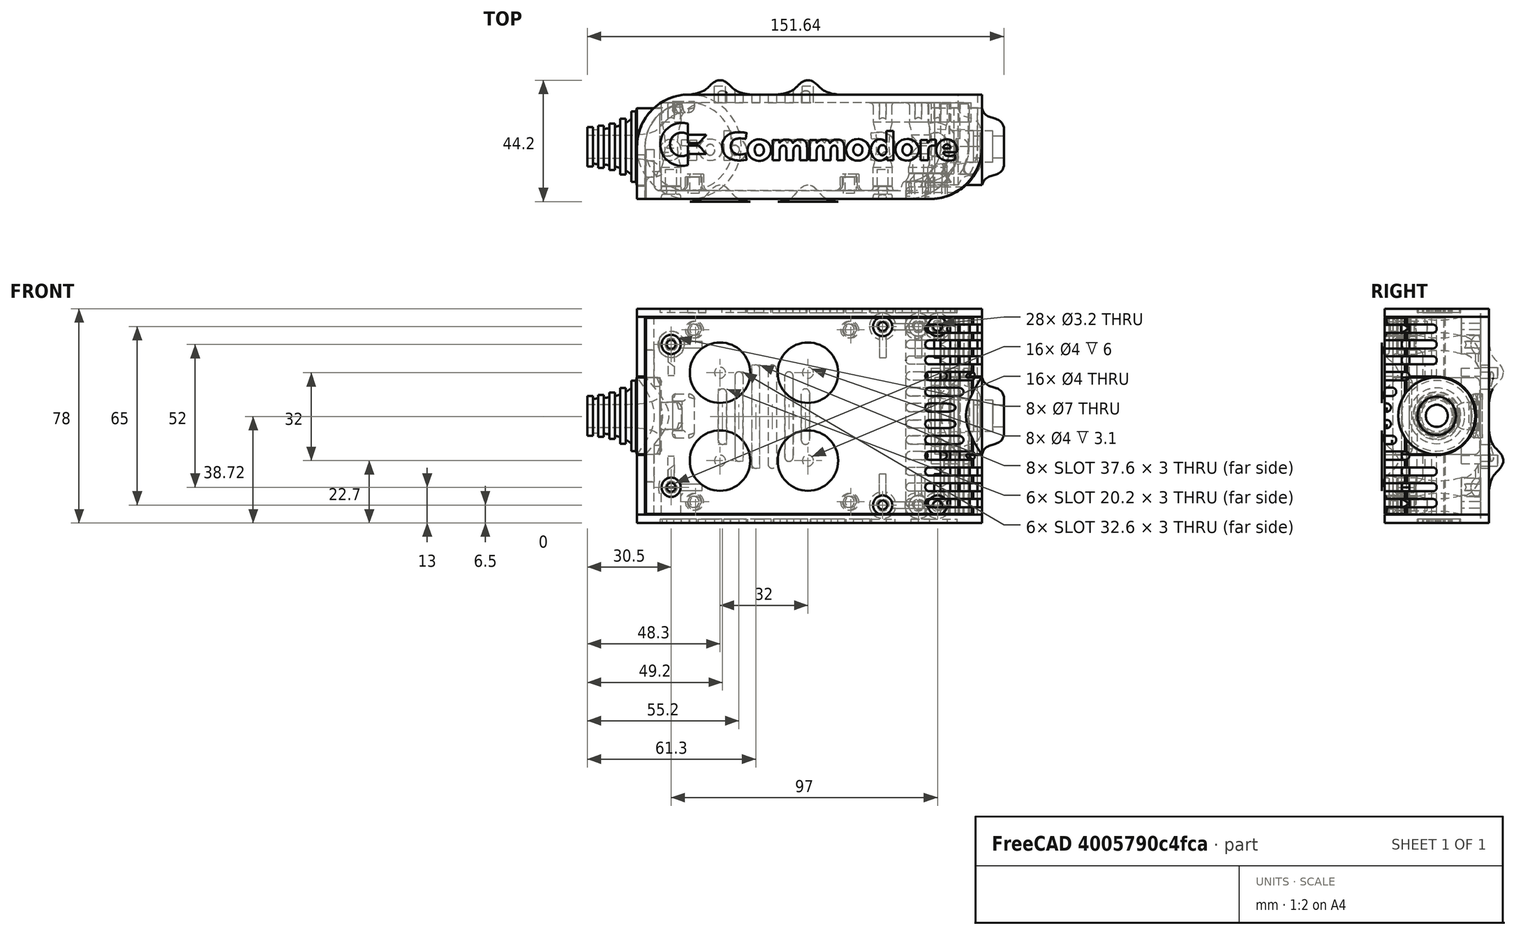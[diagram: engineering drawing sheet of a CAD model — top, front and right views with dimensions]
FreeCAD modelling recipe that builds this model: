
FCSTD DOCUMENT  (FreeCAD 0.19R0.19.2)
Label: enclosure_212FCStd
License: All rights reserved
LicenseURL: http://en.wikipedia.org/wiki/All_rights_reserved
objects: Part::Revolution×152, Part::MultiFuse×146, Part::Feature×146, Sketcher::SketchObject×85, Part::Cut×72, Part::Cylinder×70, Part::Extrusion×69, Part::Fillet×58, Part::Box×37, App::MeasureDistance×4, Part::FeaturePython×2, Image::ImagePlane×1, PartDesign::Body×1, Part::Mirroring×1
note: 839 computed .brp shape members not serialized (recipe doc carries the construction recipe); baked Part::Feature solids carry a one-line shape summary decoded from their .brp

FEATURE [Sketcher::SketchObject] Sketch  label="topSketch"
  FullyConstrained = true
  sketch-geometry (20):
    g0: LineSegment StartX=5.21097e-06 StartY=3 StartZ=0 EndX=5.21097e-06 EndY=19 EndZ=0
    g1: ArcOfCircle CenterX=19 CenterY=19 CenterZ=0 NormalX=0 NormalY=0 NormalZ=1 AngleXU=0 Radius=19 StartAngle=1.5708 EndAngle=3.14159
    g2: ArcOfCircle CenterX=19 CenterY=19 CenterZ=0 NormalX=0 NormalY=0 NormalZ=1 AngleXU=0 Radius=16 StartAngle=1.5708 EndAngle=3.14159
    g3: LineSegment StartX=114 StartY=35 StartZ=0 EndX=19 EndY=35 EndZ=0
    g4: LineSegment StartX=5.21097e-06 StartY=3 StartZ=0 EndX=5.21097e-06 EndY=0 EndZ=0
    g5: LineSegment StartX=3 StartY=0 StartZ=0 EndX=5.21097e-06 EndY=0 EndZ=0
    g6: LineSegment StartX=3 StartY=19 StartZ=0 EndX=3 EndY=0 EndZ=0
    g7: LineSegment StartX=19 StartY=38 StartZ=0 EndX=124 EndY=38 EndZ=0
    g8: Circle CenterX=119 CenterY=35 CenterZ=0 NormalX=0 NormalY=0 NormalZ=1 AngleXU=0 Radius=1
    g9: Circle CenterX=121 CenterY=35 CenterZ=0 NormalX=0 NormalY=0 NormalZ=1 AngleXU=0 Radius=1
    g10: Circle CenterX=121 CenterY=33 CenterZ=0 NormalX=0 NormalY=0 NormalZ=1 AngleXU=0 Radius=1
    g11: BSplineCurve PolesCount=3 KnotsCount=2 Degree=2 IsPeriodic=0
    g12: GeomPoint X=119 Y=35 Z=0
    g13: GeomPoint X=121 Y=33 Z=0
    g14: LineSegment StartX=119 StartY=35 StartZ=0 EndX=114 EndY=35 EndZ=0
    g15: ArcOfCircle CenterX=105 CenterY=19 CenterZ=0 NormalX=0 NormalY=0 NormalZ=1 AngleXU=0 Radius=19 StartAngle=5.7297 EndAngle=6.28319
    g16: ArcOfCircle CenterX=105 CenterY=19 CenterZ=0 NormalX=0 NormalY=0 NormalZ=1 AngleXU=0 Radius=16 StartAngle=5.60905 EndAngle=6.28319
    g17: LineSegment StartX=121 StartY=33 StartZ=0 EndX=121 EndY=19 EndZ=0
    g18: LineSegment StartX=124 StartY=38 StartZ=0 EndX=124 EndY=19 EndZ=0
    g19: LineSegment StartX=117.5 StartY=9.01251 StartZ=0 EndX=121.163 EndY=9.0125 EndZ=0
  constraints (46):
    c: Vertical(g0)
    c: Block(g0)
    c: Coincident(g1,g0)
    c: Block(g1)
    c: Coincident(g2,g1)
    c: Block(g2)
    c: Coincident(g3,g2)
    c: Horizontal(g3)
    c: Tangent(g3,g2)
    c: Coincident(g4,g0)
    c: Distance(g4) = 3
    c: Vertical(g4)
    c: Coincident(g5,g4)
    c: Horizontal(g5)
    c: Coincident(g6,g2)
    c: Coincident(g6,g5)
    c: Vertical(g6)
    c: Horizontal(g7)
    c: Distance(g7) = 105
    c: Coincident(g7,g1)
    c: Block(g3)
    c: Weight(g8) = 1
    c: Equal(g8,g9)
    c: Equal(g8,g10)
    c: InternalAlignment(g8,g11)
    c: InternalAlignment(g9,g11)
    c: InternalAlignment(g10,g11)
    c: InternalAlignment(g12,g11)
    c: InternalAlignment(g13,g11)
    c: Block(g11)
    c: Coincident(g14,g11)
    c: Coincident(g14,g3)
    c: Horizontal(g14)
    c: Block(g15)
    c: Coincident(g16,g15)
    c: Block(g16)
    c: Coincident(g17,g11)
    c: Coincident(g17,g16)
    c: Vertical(g17)
    c: Distance(g17) = 14
    c: Coincident(g18,g7)
    c: Coincident(g18,g15)
    c: Vertical(g18)
    c: Distance(g18) = 19
    c: Coincident(g19,g16)
    c: Coincident(g19,g15)
FEATURE [Sketcher::SketchObject] Sketch001  label="bottomSketch"
  FullyConstrained = true
  sketch-geometry (32):
    g0: LineSegment StartX=3.3 StartY=-6.03275e-07 StartZ=0 EndX=98 EndY=-6.03275e-07 EndZ=0
    g1: ArcOfCircle CenterX=98 CenterY=19 CenterZ=0 NormalX=0 NormalY=0 NormalZ=1 AngleXU=0 Radius=19 StartAngle=4.71239 EndAngle=5.71103
    g2: LineSegment StartX=6.3 StartY=8 StartZ=0 EndX=3.3 EndY=8 EndZ=0
    g3: LineSegment StartX=3.3 StartY=8 StartZ=0 EndX=3.3 EndY=-6.03275e-07 EndZ=0
    g4: ArcOfCircle CenterX=8.3 CenterY=5 CenterZ=0 NormalX=0 NormalY=0 NormalZ=1 AngleXU=0 Radius=2 StartAngle=3.14159 EndAngle=4.71239
    g5: LineSegment StartX=6.3 StartY=8 StartZ=0 EndX=6.3 EndY=5 EndZ=0
    g6: ArcOfCircle CenterX=98 CenterY=19 CenterZ=0 NormalX=0 NormalY=0 NormalZ=1 AngleXU=0 Radius=12.7 StartAngle=4.71239 EndAngle=6.28319
    g7: LineSegment StartX=94.7 StartY=3 StartZ=0 EndX=8.3 EndY=3 EndZ=0
    g8-g12: Circle x5 (B-spline internal-alignment scaffolding for g13; pole/knot coordinates omitted)
    g13: BSplineCurve PolesCount=5 KnotsCount=3 Degree=3 IsPeriodic=0
    g14: GeomPoint X=98 Y=6.3 Z=0
    g15: GeomPoint X=96.3938 Y=4.71946 Z=0
    g16: GeomPoint X=94.7 Y=3 Z=0
    g17-g23: Circle x7 (B-spline internal-alignment scaffolding for g24; pole/knot coordinates omitted)
    g24: BSplineCurve PolesCount=7 KnotsCount=5 Degree=3 IsPeriodic=0
    g25-g29: GeomPoint x5 (B-spline internal-alignment scaffolding for g24; pole/knot coordinates omitted)
    g30: ArcOfCircle CenterX=98 CenterY=19 CenterZ=0 NormalX=0 NormalY=0 NormalZ=1 AngleXU=0 Radius=15.7 StartAngle=5.81226 EndAngle=6.28319
    g31: LineSegment StartX=110.7 StartY=19 StartZ=0 EndX=113.7 EndY=19 EndZ=0
  constraints (41):
    c: Horizontal(g0)
    c: Coincident(g1,g0)
    c: Block(g1)
    c: Horizontal(g2)
    c: Distance(g2) = 3
    c: Coincident(g3,g2)
    c: Vertical(g3)
    c: Coincident(g3,g0)
    c: Block(g4)
    c: Block(g2)
    c: Coincident(g5,g2)
    c: Coincident(g5,g4)
    c: Vertical(g5)
    c: Coincident(g6,g1)
    c: Block(g6)
    c: Coincident(g7,g4)
    c: Horizontal(g7)
    c: Block(g0)
    c: Block(g7)
    c: Block(g3)
    c: Coincident(g13,g6)
    c: Weight(g8) = 1
    c: Equal(g8, g9-g12) x4
    c: Coincident(g13,g7)
    c: InternalAlignment(g8-g12 -> g13) x5
    c: InternalAlignment(g14,g13)
    c: InternalAlignment(g15,g13)
    c: InternalAlignment(g16,g13)
    c: Block(g13)
    c: Weight(g17) = 1
    c: Equal(g17, g18-g23) x6
    c: Coincident(g24,g1)
    c: InternalAlignment(g17-g23 -> g24) x7
    c: InternalAlignment(g25-g29 -> g24) x5
    c: Block(g24)
    c: Coincident(g30,g24)
    c: Coincident(g31,g6)
    c: Coincident(g31,g30)
    c: Horizontal(g31)
    c: Block(g31)
    c: Block(g30)
FEATURE [Part::Extrusion] Extrude  label="top"
  Base = -> Sketch
  Dir = (0,0,1)
  DirMode = 2
  FaceMakerClass = Part::FaceMakerBullseye
  LengthFwd = 72
  LengthRev = 0
  Solid = true
  Symmetric = false
FEATURE [Part::Extrusion] Extrude001  label="bottom"
  Base = -> Sketch001
  Dir = (0,0,1)
  DirMode = 2
  FaceMakerClass = Part::FaceMakerBullseye
  LengthFwd = 71.4
  LengthRev = 0
  Placement = pos=(0,0,0.3) rot=(0,0,1;0rad)
  Solid = true
  Symmetric = false
FEATURE [Sketcher::SketchObject] Sketch002  label="topSketch001"
  FullyConstrained = true
  sketch-geometry (8):
    g0: ArcOfCircle CenterX=19 CenterY=19.0975 CenterZ=0 NormalX=0 NormalY=0 NormalZ=1 AngleXU=0 Radius=18.9025 StartAngle=1.5708 EndAngle=3.14674
    g1: LineSegment StartX=0.0977805 StartY=19.0003 StartZ=0 EndX=0.0977805 EndY=0.000251602 EndZ=0
    g2: LineSegment StartX=19 StartY=38 StartZ=0 EndX=124 EndY=38 EndZ=0
    g3: LineSegment StartX=0.0977805 StartY=0.000251602 StartZ=0 EndX=105.098 EndY=0.000251602 EndZ=0
    g4: LineSegment StartX=124 StartY=38 StartZ=0 EndX=125.616 EndY=38 EndZ=0
    g5: LineSegment StartX=105.098 StartY=0.000251602 StartZ=0 EndX=106.713 EndY=0.000251602 EndZ=0
    g6: ArcOfCircle CenterX=106.616 CenterY=19 CenterZ=0 NormalX=0 NormalY=0 NormalZ=1 AngleXU=0 Radius=19 StartAngle=4.71754 EndAngle=6.28319
    g7: LineSegment StartX=125.616 StartY=38 StartZ=0 EndX=125.616 EndY=19 EndZ=0
  constraints (21):
    c: Block(g0)
    c: Coincident(g1,g0)
    c: Vertical(g1)
    c: Horizontal(g2)
    c: Distance(g2) = 105
    c: Coincident(g2,g0)
    c: Distance(g1) = 19
    c: Coincident(g3,g1)
    c: Horizontal(g3)
    c: Distance(g3) = 105
    c: Coincident(g4,g2)
    c: Horizontal(g4)
    c: Distance(g4) = 1.61553
    c: Horizontal(g5)
    c: Equal(g4,g5) = 1.61553
    c: Coincident(g5,g3)
    c: Block(g6)
    c: Coincident(g6,g5)
    c: Coincident(g7,g4)
    c: Coincident(g7,g6)
    c: Vertical(g7)
FEATURE [Part::Extrusion] Extrude002  label="sideA"
  Base = -> Sketch002
  Dir = (0,0,1)
  DirMode = 2
  FaceMakerClass = Part::FaceMakerBullseye
  LengthFwd = 3
  LengthRev = 0
  Placement = pos=(0,0,-3) rot=(0,0,1;0rad)
  Solid = true
  Symmetric = false
FEATURE [Sketcher::SketchObject] Sketch003  label="topSketch002"
  FullyConstrained = true
  sketch-geometry (6):
    g0: LineSegment StartX=19 StartY=38 StartZ=0 EndX=117 EndY=38 EndZ=0
    g1: ArcOfCircle CenterX=19 CenterY=19 CenterZ=0 NormalX=0 NormalY=0 NormalZ=1 AngleXU=0 Radius=19 StartAngle=1.5708 EndAngle=3.14159
    g2: LineSegment StartX=117 StartY=38 StartZ=0 EndX=117 EndY=19 EndZ=0
    g3: LineSegment StartX=98 StartY=1.0161e-12 StartZ=0 EndX=5.22862e-06 EndY=1.0161e-12 EndZ=0
    g4: LineSegment StartX=5.22862e-06 StartY=19 StartZ=0 EndX=5.22862e-06 EndY=1.0161e-12 EndZ=0
    g5: ArcOfCircle CenterX=98 CenterY=19 CenterZ=0 NormalX=0 NormalY=0 NormalZ=1 AngleXU=0 Radius=19 StartAngle=4.71239 EndAngle=6.28319
  constraints (16):
    c: Horizontal(g0)
    c: Distance(g0) = 98
    c: Coincident(g1,g0)
    c: Block(g1)
    c: Coincident(g2,g0)
    c: Vertical(g2)
    c: Distance(g2) = 19
    c: Horizontal(g3)
    c: Coincident(g4,g1)
    c: Vertical(g4)
    c: Coincident(g3,g4)
    c: Block(g3)
    c: Coincident(g5,g2)
    c: Coincident(g5,g3)
    c: Block(g0)
    c: Block(g5)
FEATURE [Sketcher::SketchObject] Sketch004
  FullyConstrained = true
  MapMode = 3
  Placement = pos=(0,0,0) rot=(1,0,0;1.5708rad)
  Support = -> [Extrude]
  sketch-geometry (8):
    g0: Circle CenterX=80.351 CenterY=-67.6202 CenterZ=0 NormalX=0 NormalY=0 NormalZ=1 AngleXU=0 Radius=2
    g1: Circle CenterX=80.351 CenterY=-67.6202 CenterZ=0 NormalX=0 NormalY=0 NormalZ=1 AngleXU=0 Radius=3
    g2: Circle CenterX=80.351 CenterY=-4.92017 CenterZ=0 NormalX=0 NormalY=0 NormalZ=1 AngleXU=0 Radius=2
    g3: Circle CenterX=80.351 CenterY=-4.92017 CenterZ=0 NormalX=0 NormalY=0 NormalZ=1 AngleXU=0 Radius=3
    g4: Circle CenterX=23.851 CenterY=-4.92017 CenterZ=0 NormalX=0 NormalY=0 NormalZ=1 AngleXU=0 Radius=2
    g5: Circle CenterX=23.851 CenterY=-4.92017 CenterZ=0 NormalX=0 NormalY=0 NormalZ=1 AngleXU=0 Radius=3
    g6: Circle CenterX=23.851 CenterY=-67.6202 CenterZ=0 NormalX=0 NormalY=0 NormalZ=1 AngleXU=0 Radius=2
    g7: Circle CenterX=23.851 CenterY=-67.6202 CenterZ=0 NormalX=0 NormalY=0 NormalZ=1 AngleXU=0 Radius=3
  constraints (8):
    c: Block(g3)
    c: Block(g2)
    c: Block(g1)
    c: Block(g0)
    c: Block(g6)
    c: Block(g7)
    c: Block(g4)
    c: Block(g5)
FEATURE [Part::Extrusion] Extrude004
  Base = -> Sketch004
  Dir = (0,-1,2e-16)
  DirMode = 2
  FaceMakerClass = Part::FaceMakerBullseye
  LengthFwd = 6
  LengthRev = 0
  Placement = pos=(0,9,0) rot=(0,0,1;0rad)
  Solid = true
  Symmetric = false
FEATURE [Sketcher::SketchObject] Sketch005
  FullyConstrained = true
  MapMode = 3
  Placement = pos=(0,0,0) rot=(1,0,0;1.5708rad)
  Support = -> [Extrude]
  sketch-geometry (8):
    g0: Circle CenterX=80.351 CenterY=-67.6202 CenterZ=0 NormalX=0 NormalY=0 NormalZ=1 AngleXU=0 Radius=3
    g1: Circle CenterX=80.351 CenterY=-4.92017 CenterZ=0 NormalX=0 NormalY=0 NormalZ=1 AngleXU=0 Radius=3
    g2: Circle CenterX=23.851 CenterY=-4.92017 CenterZ=0 NormalX=0 NormalY=0 NormalZ=1 AngleXU=0 Radius=3
    g3: Circle CenterX=23.851 CenterY=-67.6202 CenterZ=0 NormalX=0 NormalY=0 NormalZ=1 AngleXU=0 Radius=3
    g4: Circle CenterX=23.851 CenterY=-67.6202 CenterZ=0 NormalX=0 NormalY=0 NormalZ=1 AngleXU=0 Radius=5
    g5: Circle CenterX=80.351 CenterY=-67.6202 CenterZ=0 NormalX=0 NormalY=0 NormalZ=1 AngleXU=0 Radius=5
    g6: Circle CenterX=23.851 CenterY=-4.92017 CenterZ=0 NormalX=0 NormalY=0 NormalZ=1 AngleXU=0 Radius=5
    g7: Circle CenterX=80.351 CenterY=-4.92017 CenterZ=0 NormalX=0 NormalY=0 NormalZ=1 AngleXU=0 Radius=5
  constraints (8):
    c: Block(g1)
    c: Block(g0)
    c: Block(g3)
    c: Block(g2)
    c: Block(g5)
    c: Block(g4)
    c: Block(g6)
    c: Block(g7)
FEATURE [Part::Extrusion] Extrude005
  Base = -> Sketch005
  Dir = (0,-1,2e-16)
  DirMode = 2
  FaceMakerClass = Part::FaceMakerBullseye
  LengthFwd = 2
  LengthRev = 0
  Solid = true
  Symmetric = false
FEATURE [Sketcher::SketchObject] Sketch006
  FullyConstrained = true
  MapMode = 3
  Placement = pos=(0,0,0) rot=(1,0,0;1.5708rad)
  sketch-geometry (8):
    g0: Circle CenterX=80.351 CenterY=-67.6202 CenterZ=0 NormalX=0 NormalY=0 NormalZ=1 AngleXU=0 Radius=3
    g1: Circle CenterX=80.351 CenterY=-4.92017 CenterZ=0 NormalX=0 NormalY=0 NormalZ=1 AngleXU=0 Radius=3
    g2: Circle CenterX=23.851 CenterY=-4.92017 CenterZ=0 NormalX=0 NormalY=0 NormalZ=1 AngleXU=0 Radius=3
    g3: Circle CenterX=23.851 CenterY=-67.6202 CenterZ=0 NormalX=0 NormalY=0 NormalZ=1 AngleXU=0 Radius=3
    g4: Circle CenterX=23.851 CenterY=-67.6202 CenterZ=0 NormalX=0 NormalY=0 NormalZ=1 AngleXU=0 Radius=5
    g5: Circle CenterX=80.351 CenterY=-67.6202 CenterZ=0 NormalX=0 NormalY=0 NormalZ=1 AngleXU=0 Radius=5
    g6: Circle CenterX=23.851 CenterY=-4.92017 CenterZ=0 NormalX=0 NormalY=0 NormalZ=1 AngleXU=0 Radius=5
    g7: Circle CenterX=80.351 CenterY=-4.92017 CenterZ=0 NormalX=0 NormalY=0 NormalZ=1 AngleXU=0 Radius=5
  constraints (8):
    c: Block(g1)
    c: Block(g0)
    c: Block(g3)
    c: Block(g2)
    c: Block(g5)
    c: Block(g4)
    c: Block(g6)
    c: Block(g7)
FEATURE [Part::Extrusion] Extrude007
  Base = -> Sketch006
  Dir = (0,-1,2e-16)
  DirMode = 2
  FaceMakerClass = Part::FaceMakerBullseye
  LengthFwd = 2
  LengthRev = 0
  Solid = true
  Symmetric = false
FEATURE [Part::Fillet] Fillet
  Base = -> Extrude007
  Edges = 4 edges r=1.99: [Edge6,Edge12,Edge18,Edge24]
FEATURE [Part::Cut] Cut
  Base = -> Extrude005
  Placement = pos=(0,5,0) rot=(0,0,1;0rad)
  Tool = -> Fillet
FEATURE [Part::MultiFuse] Fusion  label="pCBScrews"
  Placement = pos=(-2.5,0,72.3) rot=(0,0,1;0rad)
  Shapes = -> [Extrude004,Cut]
FEATURE [App::MeasureDistance] Distance  label="Distance: 0.69 mm"
  Distance = 0.685967
  P1 = (24.0138,2.9647,0.3)
  P2 = (23.8901,3,-0.373787)
FEATURE [App::MeasureDistance] Distance001  label="Distance: 0.53 mm"
  Distance = 0.533607
  P1 = (80.2939,3,72.2334)
  P2 = (80.281,2.99661,71.7)
FEATURE [Part::Fillet] Fillet001
  Base = -> Extrude001
  Edges = 1 edges r=2.4: [Edge17]
FEATURE [Part::Fillet] Fillet002  label="bottom001"
  Base = -> Fillet001
  Edges = 1 edges r=2.4: [Edge36]
FEATURE [Part::Fillet] Fillet003  label="top001"
  Base = -> Extrude
  Edges = 1 edges r=2: [Edge1]
FEATURE [Sketcher::SketchObject] Sketch007
  FullyConstrained = true
  sketch-geometry (16):
    g0: LineSegment StartX=4 StartY=0 StartZ=0 EndX=4 EndY=2.4 EndZ=0
    g1: LineSegment StartX=4 StartY=2.4 StartZ=0 EndX=7 EndY=2.4 EndZ=0
    g2: LineSegment StartX=4 StartY=0 StartZ=0 EndX=5.7 EndY=0 EndZ=0
    g3: LineSegment StartX=5.7 StartY=0 StartZ=0 EndX=5.7 EndY=-5.6 EndZ=0
    g4-g8: Circle x5 (B-spline internal-alignment scaffolding for g9; pole/knot coordinates omitted)
    g9: BSplineCurve PolesCount=5 KnotsCount=3 Degree=3 IsPeriodic=0
    g10: GeomPoint X=7 Y=2.4 Z=0
    g11: GeomPoint X=10.4582 Y=-1.55472 Z=0
    g12: GeomPoint X=14 Y=-5.6 Z=0
    g13: LineSegment StartX=14 StartY=-5.6 StartZ=0 EndX=14 EndY=-14.1 EndZ=0
    g14: LineSegment StartX=14 StartY=-14.1 StartZ=0 EndX=6.5 EndY=-14.1 EndZ=0
    g15: LineSegment StartX=5.7 StartY=-5.6 StartZ=0 EndX=6.5 EndY=-14.1 EndZ=0
  constraints (28):
    c: Distance(g0) = 2.4
    c: Vertical(g0)
    c: Block(g0)
    c: Coincident(g1,g0)
    c: Horizontal(g1)
    c: Distance(g1) = 3
    c: Coincident(g2,g0)
    c: Horizontal(g2)
    c: Distance(g2) = 1.7
    c: Coincident(g3,g2)
    c: Vertical(g3)
    c: Distance(g3) = 5.6
    c: Coincident(g9,g1)
    c: Weight(g4) = 1
    c: Equal(g4, g5-g8) x4
    c: InternalAlignment(g4-g8 -> g9) x5
    c: InternalAlignment(g10,g9)
    c: InternalAlignment(g11,g9)
    c: InternalAlignment(g12,g9)
    c: Block(g9)
    c: Coincident(g13,g9)
    c: Vertical(g13)
    c: Distance(g13) = 8.5
    c: Coincident(g14,g13)
    c: Horizontal(g14)
    c: Distance(g14) = 7.5
    c: Coincident(g15,g3)
    c: Coincident(g15,g14)
FEATURE [Part::Feature] Face
  shape: bbox 10 x 16.5 x 2e-07 mm, 1 faces, 0 solids (baked)
FEATURE [Part::Revolution] Revolve  label="plugHousing"
  Angle = 360
  Axis = (0,1,0)
  Base = (0,0,0)
  FaceMakerClass = Part::FaceMakerBullseye
  Placement = pos=(0,0,36.15) rot=(0,0,1;0rad)
  Solid = false
  Source = -> Face
  Symmetric = false
FEATURE [Part::Feature] Face001
  shape: bbox 10 x 16.5 x 2e-07 mm, 1 faces, 0 solids (baked)
FEATURE [Part::Revolution] Revolve001  label="plugHousing001"
  Angle = 360
  Axis = (0,1,0)
  Base = (0,0,0)
  FaceMakerClass = Part::FaceMakerBullseye
  Placement = pos=(0,0,36.15) rot=(0,0,1;0rad)
  Solid = false
  Source = -> Face001
  Symmetric = false
FEATURE [Part::MultiFuse] Fusion001  label="plugHousing002"
  Placement = pos=(0,0,0) rot=(0,0,1;1.5708rad)
  Shapes = -> [Revolve001,Revolve]
FEATURE [Part::Feature] Face002
  shape: bbox 10 x 16.5 x 2e-07 mm, 1 faces, 0 solids (baked)
FEATURE [Part::Revolution] Revolve003  label="plugHousing005"
  Angle = 360
  Axis = (0,1,0)
  Base = (0,0,0)
  FaceMakerClass = Part::FaceMakerBullseye
  Placement = pos=(0,0,36.15) rot=(0,0,1;0rad)
  Solid = false
  Source = -> Face002
  Symmetric = false
FEATURE [Part::Feature] Face003
  shape: bbox 10 x 16.5 x 2e-07 mm, 1 faces, 0 solids (baked)
FEATURE [Part::Revolution] Revolve002  label="plugHousing003"
  Angle = 360
  Axis = (0,1,0)
  Base = (0,0,0)
  FaceMakerClass = Part::FaceMakerBullseye
  Placement = pos=(0,0,36.15) rot=(0,0,1;0rad)
  Solid = false
  Source = -> Face003
  Symmetric = false
FEATURE [Part::MultiFuse] Fusion002  label="plugHousing004"
  Placement = pos=(0,0,0) rot=(0,0,1;1.5708rad)
  Shapes = -> [Revolve002,Revolve003]
FEATURE [Part::MultiFuse] Fusion003  label="plugHousing006"
  Placement = pos=(0,19,0) rot=(0,0,1;3.14159rad)
  Shapes = -> [Fusion002,Fusion001]
FEATURE [Part::Feature] Face004
  shape: bbox 10 x 16.5 x 2e-07 mm, 1 faces, 0 solids (baked)
FEATURE [Part::Revolution] Revolve006  label="plugHousing010"
  Angle = 360
  Axis = (0,1,0)
  Base = (0,0,0)
  FaceMakerClass = Part::FaceMakerBullseye
  Placement = pos=(0,0,36.15) rot=(0,0,1;0rad)
  Solid = false
  Source = -> Face004
  Symmetric = false
FEATURE [Part::Feature] Face005
  shape: bbox 10 x 16.5 x 2e-07 mm, 1 faces, 0 solids (baked)
FEATURE [Part::Revolution] Revolve007  label="plugHousing011"
  Angle = 360
  Axis = (0,1,0)
  Base = (0,0,0)
  FaceMakerClass = Part::FaceMakerBullseye
  Placement = pos=(0,0,36.15) rot=(0,0,1;0rad)
  Solid = false
  Source = -> Face005
  Symmetric = false
FEATURE [Part::Feature] Face006
  shape: bbox 10 x 16.5 x 2e-07 mm, 1 faces, 0 solids (baked)
FEATURE [Part::Revolution] Revolve004  label="plugHousing007"
  Angle = 360
  Axis = (0,1,0)
  Base = (0,0,0)
  FaceMakerClass = Part::FaceMakerBullseye
  Placement = pos=(0,0,36.15) rot=(0,0,1;0rad)
  Solid = false
  Source = -> Face006
  Symmetric = false
FEATURE [Part::MultiFuse] Fusion004  label="plugHousing009"
  Placement = pos=(0,0,0) rot=(0,0,1;1.5708rad)
  Shapes = -> [Revolve004,Revolve007]
FEATURE [Part::Feature] Face007
  shape: bbox 10 x 16.5 x 2e-07 mm, 1 faces, 0 solids (baked)
FEATURE [Part::Revolution] Revolve005  label="plugHousing008"
  Angle = 360
  Axis = (0,1,0)
  Base = (0,0,0)
  FaceMakerClass = Part::FaceMakerBullseye
  Placement = pos=(0,0,36.15) rot=(0,0,1;0rad)
  Solid = false
  Source = -> Face007
  Symmetric = false
FEATURE [Part::MultiFuse] Fusion005  label="plugHousing012"
  Placement = pos=(0,0,0) rot=(0,0,1;1.5708rad)
  Shapes = -> [Revolve006,Revolve005]
FEATURE [Part::MultiFuse] Fusion006  label="plugHousing013"
  Placement = pos=(0,19,0) rot=(0,0,1;3.14159rad)
  Shapes = -> [Fusion005,Fusion004]
FEATURE [Part::MultiFuse] Fusion007  label="plugHousing014"
  Placement = pos=(122.621,0,-0.15) rot=(0,0,1;0rad)
  Shapes = -> [Fusion003,Fusion006]
FEATURE [Part::Cylinder] Cylinder002
  Angle = 360
  AttacherType = Attacher::AttachEngine3D
  Height = 20
  Placement = pos=(0,0,36.15) rot=(0,0,1;0rad)
  Radius = 4
FEATURE [Part::Cylinder] Cylinder003
  Angle = 360
  AttacherType = Attacher::AttachEngine3D
  Height = 10
  Placement = pos=(0,0,36.15) rot=(0,0,1;0rad)
  Radius = 4
FEATURE [Part::MultiFuse] Fusion009  label="removeToCreateHoleForPlugHousing"
  Placement = pos=(70,19,36.15) rot=(0,1,0;1.5708rad)
  Shapes = -> [Cylinder002,Cylinder003]
FEATURE [Part::Cylinder] Cylinder004
  Angle = 360
  AttacherType = Attacher::AttachEngine3D
  Height = 20
  Placement = pos=(0,0,36.15) rot=(0,0,1;0rad)
  Radius = 4
FEATURE [Part::Cylinder] Cylinder005
  Angle = 360
  AttacherType = Attacher::AttachEngine3D
  Height = 10
  Placement = pos=(0,0,36.15) rot=(0,0,1;0rad)
  Radius = 4
FEATURE [Part::MultiFuse] Fusion010  label="removeToCreateHoleForPlugHousing001"
  Placement = pos=(70,19,36.15) rot=(0,1,0;1.5708rad)
  Shapes = -> [Cylinder004,Cylinder005]
FEATURE [Part::Cut] Cut001
  Base = -> Fillet003
  Tool = -> Fusion010
FEATURE [Part::Cut] Cut002  label="Bottom"
  Base = -> Fillet002
  Tool = -> Fusion009
FEATURE [Part::Feature] Face008
  shape: bbox 10 x 16.5 x 2e-07 mm, 1 faces, 0 solids (baked)
FEATURE [Part::Revolution] Revolve011  label="plugHousing021"
  Angle = 360
  Axis = (0,1,0)
  Base = (0,0,0)
  FaceMakerClass = Part::FaceMakerBullseye
  Placement = pos=(0,0,36.15) rot=(0,0,1;0rad)
  Solid = false
  Source = -> Face008
  Symmetric = false
FEATURE [Part::Feature] Face009
  shape: bbox 10 x 16.5 x 2e-07 mm, 1 faces, 0 solids (baked)
FEATURE [Part::Revolution] Revolve012  label="plugHousing022"
  Angle = 360
  Axis = (0,1,0)
  Base = (0,0,0)
  FaceMakerClass = Part::FaceMakerBullseye
  Placement = pos=(0,0,36.15) rot=(0,0,1;0rad)
  Solid = false
  Source = -> Face009
  Symmetric = false
FEATURE [Part::Feature] Face010 .. Face013  x4 (patterned run collapsed; names and placements below)
  shape: bbox 10 x 16.5 x 2e-07 mm, 1 faces, 0 solids (baked)
FEATURE [Part::Revolution] Revolve015  label="plugHousing027"
  Angle = 360
  Axis = (0,1,0)
  Base = (0,0,0)
  FaceMakerClass = Part::FaceMakerBullseye
  Placement = pos=(0,0,36.15) rot=(0,0,1;0rad)
  Solid = false
  Source = -> Face013
  Symmetric = false
FEATURE [Part::Feature] Face014
  shape: bbox 10 x 16.5 x 2e-07 mm, 1 faces, 0 solids (baked)
FEATURE [Part::Feature] Face015
  shape: bbox 10 x 16.5 x 2e-07 mm, 1 faces, 0 solids (baked)
FEATURE [Part::Feature] Face016
  shape: bbox 10 x 16.5 x 2e-07 mm, 1 faces, 0 solids (baked)
FEATURE [Part::Revolution] Revolve019  label="plugHousing033"
  Angle = 360
  Axis = (0,1,0)
  Base = (0,0,0)
  FaceMakerClass = Part::FaceMakerBullseye
  Placement = pos=(0,0,36.15) rot=(0,0,1;0rad)
  Solid = false
  Source = -> Face016
  Symmetric = false
FEATURE [Part::Feature] Face017
  shape: bbox 10 x 16.5 x 2e-07 mm, 1 faces, 0 solids (baked)
FEATURE [Part::Revolution] Revolve020  label="plugHousing034"
  Angle = 360
  Axis = (0,1,0)
  Base = (0,0,0)
  FaceMakerClass = Part::FaceMakerBullseye
  Placement = pos=(0,0,36.15) rot=(0,0,1;0rad)
  Solid = false
  Source = -> Face017
  Symmetric = false
FEATURE [Part::Feature] Face018
  shape: bbox 10 x 16.5 x 2e-07 mm, 1 faces, 0 solids (baked)
FEATURE [Part::Revolution] Revolve016  label="plugHousing030"
  Angle = 360
  Axis = (0,1,0)
  Base = (0,0,0)
  FaceMakerClass = Part::FaceMakerBullseye
  Placement = pos=(0,0,36.15) rot=(0,0,1;0rad)
  Solid = false
  Source = -> Face018
  Symmetric = false
FEATURE [Part::MultiFuse] Fusion020  label="plugHousing038"
  Placement = pos=(0,0,0) rot=(0,0,1;1.5708rad)
  Shapes = -> [Revolve016,Revolve020]
FEATURE [Part::Feature] Face019
  shape: bbox 10 x 16.5 x 2e-07 mm, 1 faces, 0 solids (baked)
FEATURE [Part::Feature] Face020
  shape: bbox 10 x 16.5 x 2e-07 mm, 1 faces, 0 solids (baked)
FEATURE [Part::Revolution] Revolve017  label="plugHousing031"
  Angle = 360
  Axis = (0,1,0)
  Base = (0,0,0)
  FaceMakerClass = Part::FaceMakerBullseye
  Placement = pos=(0,0,36.15) rot=(0,0,1;0rad)
  Solid = false
  Source = -> Face020
  Symmetric = false
FEATURE [Part::MultiFuse] Fusion021  label="plugHousing039"
  Placement = pos=(0,0,0) rot=(0,0,1;1.5708rad)
  Shapes = -> [Revolve019,Revolve017]
FEATURE [Part::MultiFuse] Fusion023  label="plugHousing041"
  Placement = pos=(0,19,0) rot=(0,0,1;3.14159rad)
  Shapes = -> [Fusion021,Fusion020]
FEATURE [Part::Revolution] Revolve022  label="plugHousing043"
  Angle = 360
  Axis = (0,1,0)
  Base = (0,0,0)
  FaceMakerClass = Part::FaceMakerBullseye
  Placement = pos=(0,0,36.15) rot=(0,0,1;0rad)
  Solid = false
  Source = -> Face019
  Symmetric = false
FEATURE [Part::Feature] Face021
  shape: bbox 10 x 16.5 x 2e-07 mm, 1 faces, 0 solids (baked)
FEATURE [Part::Revolution] Revolve023  label="plugHousing044"
  Angle = 360
  Axis = (0,1,0)
  Base = (0,0,0)
  FaceMakerClass = Part::FaceMakerBullseye
  Placement = pos=(0,0,36.15) rot=(0,0,1;0rad)
  Solid = false
  Source = -> Face021
  Symmetric = false
FEATURE [Part::Feature] Face022
  shape: bbox 10 x 16.5 x 2e-07 mm, 1 faces, 0 solids (baked)
FEATURE [Part::Revolution] Revolve018  label="plugHousing032"
  Angle = 360
  Axis = (0,1,0)
  Base = (0,0,0)
  FaceMakerClass = Part::FaceMakerBullseye
  Placement = pos=(0,0,36.15) rot=(0,0,1;0rad)
  Solid = false
  Source = -> Face022
  Symmetric = false
FEATURE [Part::MultiFuse] Fusion022  label="plugHousing040"
  Placement = pos=(0,0,0) rot=(0,0,1;1.5708rad)
  Shapes = -> [Revolve018,Revolve023]
FEATURE [Part::Feature] Face023
  shape: bbox 10 x 16.5 x 2e-07 mm, 1 faces, 0 solids (baked)
FEATURE [Part::Revolution] Revolve021  label="plugHousing035"
  Angle = 360
  Axis = (0,1,0)
  Base = (0,0,0)
  FaceMakerClass = Part::FaceMakerBullseye
  Placement = pos=(0,0,36.15) rot=(0,0,1;0rad)
  Solid = false
  Source = -> Face023
  Symmetric = false
FEATURE [Part::MultiFuse] Fusion018  label="plugHousing036"
  Placement = pos=(0,0,0) rot=(0,0,1;1.5708rad)
  Shapes = -> [Revolve022,Revolve021]
FEATURE [Part::MultiFuse] Fusion019  label="plugHousing037"
  Placement = pos=(0,19,0) rot=(0,0,1;3.14159rad)
  Shapes = -> [Fusion018,Fusion022]
FEATURE [Part::MultiFuse] Fusion024  label="plugHousing042"
  Placement = pos=(122.621,0,-0.15) rot=(0,0,1;0rad)
  Shapes = -> [Fusion023,Fusion019]
FEATURE [Part::Cylinder] Cylinder006
  Angle = 360
  AttacherType = Attacher::AttachEngine3D
  Height = 20
  Placement = pos=(0,0,36.15) rot=(0,0,1;0rad)
  Radius = 14.3
FEATURE [Part::Cylinder] Cylinder007
  Angle = 360
  AttacherType = Attacher::AttachEngine3D
  Height = 10
  Placement = pos=(0,0,36.15) rot=(0,0,1;0rad)
  Radius = 4
FEATURE [Part::MultiFuse] Fusion026  label="removeToCreteHoleForPlugHousing"
  Placement = pos=(70,19,36) rot=(0,1,0;1.5708rad)
  Shapes = -> [Cylinder006,Cylinder007]
FEATURE [Part::Box] Box001  label="Cube001"
  AttacherType = Attacher::AttachEngine3D
  Height = 28
  Length = 3
  Placement = pos=(110.7,19,22) rot=(0,0,1;0rad)
  Width = 15.7
FEATURE [Part::Cut] Cut003  label="top002"
  Base = -> Cut001
  Tool = -> Fusion007
FEATURE [Part::Revolution] Revolve008  label="plugHousing015"
  Angle = 360
  Axis = (0,1,0)
  Base = (0,0,0)
  FaceMakerClass = Part::FaceMakerBullseye
  Placement = pos=(0,0,36.15) rot=(0,0,1;0rad)
  Solid = false
  Source = -> Face010
  Symmetric = false
FEATURE [Part::MultiFuse] Fusion013  label="plugHousing020"
  Placement = pos=(0,0,0) rot=(0,0,1;1.5708rad)
  Shapes = -> [Revolve008,Revolve012]
FEATURE [Part::Cut] Cut004  label="top003"
  Base = -> Cut003
  Placement = pos=(1,0,0) rot=(0,0,1;0rad)
  Tool = -> Fusion026
FEATURE [Part::Cylinder] Cylinder008
  Angle = 360
  AttacherType = Attacher::AttachEngine3D
  Height = 20
  Placement = pos=(0,0,36.15) rot=(0,0,1;0rad)
  Radius = 10.3
FEATURE [Part::Cylinder] Cylinder009
  Angle = 360
  AttacherType = Attacher::AttachEngine3D
  Height = 10
  Placement = pos=(0,0,36.15) rot=(0,0,1;0rad)
  Radius = 4
FEATURE [Part::MultiFuse] Fusion027  label="removeToCreteHoleForPlugHousing001"
  Placement = pos=(70,19,36) rot=(0,1,0;1.5708rad)
  Shapes = -> [Cylinder008,Cylinder009]
FEATURE [Part::Cut] Cut005  label="plugHousingTab"
  Base = -> Box001
  Tool = -> Fusion027
FEATURE [Part::MultiFuse] Fusion028  label="plugHousing045"
  Shapes = -> [Fusion024,Cut005]
FEATURE [Part::Box] Box002  label="Cube002"
  AttacherType = Attacher::AttachEngine3D
  Height = 28.8
  Length = 3
  Placement = pos=(107.3,28,21.6) rot=(0,0,1;0rad)
  Width = 7
FEATURE [Part::Box] Box003  label="Cube003"
  AttacherType = Attacher::AttachEngine3D
  Height = 3
  Length = 6.4
  Placement = pos=(107.3,28,18.6) rot=(0,0,1;0rad)
  Width = 7
FEATURE [Part::Box] Box004  label="Cube004"
  AttacherType = Attacher::AttachEngine3D
  Height = 3
  Length = 6.4
  Placement = pos=(107.3,28,50.4) rot=(0,0,1;0rad)
  Width = 7
FEATURE [Part::MultiFuse] Fusion029  label="plugHousingBracketHolder"
  Shapes = -> [Box004,Box002,Box003]
FEATURE [Part::Cylinder] Cylinder010
  Angle = 360
  AttacherType = Attacher::AttachEngine3D
  Height = 20
  Placement = pos=(0,0,36.15) rot=(0,0,1;0rad)
  Radius = 14.3
FEATURE [Part::Cylinder] Cylinder011
  Angle = 360
  AttacherType = Attacher::AttachEngine3D
  Height = 10
  Placement = pos=(0,0,36.15) rot=(0,0,1;0rad)
  Radius = 4
FEATURE [Part::MultiFuse] Fusion030  label="removeToCreteHoleForPlugHousing002"
  Placement = pos=(70,19,36) rot=(0,1,0;1.5708rad)
  Shapes = -> [Cylinder010,Cylinder011]
FEATURE [Part::Cut] Cut006  label="plugHousingBracketHolder001"
  Base = -> Fusion029
  Tool = -> Fusion030
FEATURE [Part::Cylinder] Cylinder012
  Angle = 360
  AttacherType = Attacher::AttachEngine3D
  Height = 20
  Placement = pos=(0,0,36.15) rot=(0,0,1;0rad)
  Radius = 7
FEATURE [Part::Cylinder] Cylinder013
  Angle = 360
  AttacherType = Attacher::AttachEngine3D
  Height = 10
  Placement = pos=(0,0,36.15) rot=(0,0,1;0rad)
  Radius = 4
FEATURE [Part::MultiFuse] Fusion032  label="removeToCreteHoleForPlugHousing003"
  Placement = pos=(70,19,36) rot=(0,1,0;1.5708rad)
  Shapes = -> [Cylinder012,Cylinder013]
FEATURE [Part::Cut] Cut007  label="bottom002"
  Base = -> Cut002
  Tool = -> Fusion032
FEATURE [Sketcher::SketchObject] Sketch008
  FullyConstrained = true
  sketch-geometry (54):
    g0: LineSegment StartX=-4.2 StartY=0 StartZ=0 EndX=-6.2 EndY=0 EndZ=0
    g1: LineSegment StartX=-14 StartY=-18 StartZ=0 EndX=-14 EndY=-26.5 EndZ=0
    g2: LineSegment StartX=-4.2 StartY=0 StartZ=0 EndX=-4.2 EndY=-13.4877 EndZ=0
    g3: Circle CenterX=-4.2 CenterY=-13.4877 CenterZ=0 NormalX=0 NormalY=0 NormalZ=1 AngleXU=0 Radius=1
    g4: Circle CenterX=-4.2 CenterY=-26.5 CenterZ=0 NormalX=0 NormalY=0 NormalZ=1 AngleXU=0 Radius=1
    g5: Circle CenterX=-8.2 CenterY=-26.5 CenterZ=0 NormalX=0 NormalY=0 NormalZ=1 AngleXU=0 Radius=1
    g6: BSplineCurve PolesCount=3 KnotsCount=2 Degree=2 IsPeriodic=0
    g7: GeomPoint X=-4.2 Y=-13.4877 Z=0
    g8: GeomPoint X=-8.2 Y=-26.5 Z=0
    g9: LineSegment StartX=-14 StartY=-26.5 StartZ=0 EndX=-8.2 EndY=-26.5 EndZ=0
    g10: LineSegment StartX=-10.15 StartY=-12 StartZ=0 EndX=-10.15 EndY=-14 EndZ=0
    g11: LineSegment StartX=-12.8401 StartY=-16 StartZ=0 EndX=-10.1571 EndY=-16 EndZ=0
    g12: LineSegment StartX=-10.15 StartY=-14 StartZ=0 EndX=-8.70761 EndY=-14 EndZ=0
    g13: LineSegment StartX=-12.8401 StartY=-16 StartZ=0 EndX=-12.8401 EndY=-17.6958 EndZ=0
    g14: LineSegment StartX=-10.15 StartY=-12 StartZ=0 EndX=-7.79258 EndY=-12 EndZ=0
    g15: Circle CenterX=-6.2215 CenterY=-2 CenterZ=0 NormalX=0 NormalY=0 NormalZ=1 AngleXU=0 Radius=1
    g16: Circle CenterX=-6.22762 CenterY=-2.58724 CenterZ=0 NormalX=0 NormalY=0 NormalZ=1 AngleXU=0 Radius=1
    g17: Circle CenterX=-6.32538 CenterY=-4 CenterZ=0 NormalX=0 NormalY=0 NormalZ=1 AngleXU=0 Radius=1
    g18: BSplineCurve PolesCount=3 KnotsCount=2 Degree=2 IsPeriodic=0
    g19: GeomPoint X=-6.2215 Y=-2 Z=0
    g20: GeomPoint X=-6.32538 Y=-4 Z=0
    g21: Circle CenterX=-6.48644 CenterY=-5.99526 CenterZ=0 NormalX=0 NormalY=0 NormalZ=1 AngleXU=0 Radius=1
    g22: Circle CenterX=-6.58486 CenterY=-6.99526 CenterZ=0 NormalX=0 NormalY=0 NormalZ=1 AngleXU=0 Radius=1
    g23: Circle CenterX=-6.77343 CenterY=-8 CenterZ=0 NormalX=0 NormalY=0 NormalZ=1 AngleXU=0 Radius=1
    g24: BSplineCurve PolesCount=3 KnotsCount=2 Degree=2 IsPeriodic=0
    g25: GeomPoint X=-6.48644 Y=-5.99526 Z=0
    g26: GeomPoint X=-6.77343 Y=-8 Z=0
    g27: Circle CenterX=-7.19003 CenterY=-10 CenterZ=0 NormalX=0 NormalY=0 NormalZ=1 AngleXU=0 Radius=1
    g28: Circle CenterX=-7.44407 CenterY=-11.0915 CenterZ=0 NormalX=0 NormalY=0 NormalZ=1 AngleXU=0 Radius=1
    g29: Circle CenterX=-7.79258 CenterY=-12 CenterZ=0 NormalX=0 NormalY=0 NormalZ=1 AngleXU=0 Radius=1
    g30: BSplineCurve PolesCount=3 KnotsCount=2 Degree=2 IsPeriodic=0
    g31: GeomPoint X=-7.19003 Y=-10 Z=0
    g32: GeomPoint X=-7.79258 Y=-12 Z=0
    g33: Circle CenterX=-8.70761 CenterY=-14 CenterZ=0 NormalX=0 NormalY=0 NormalZ=1 AngleXU=0 Radius=1
    g34: Circle CenterX=-9.33087 CenterY=-15.1837 CenterZ=0 NormalX=0 NormalY=0 NormalZ=1 AngleXU=0 Radius=1
    g35: Circle CenterX=-10.1571 CenterY=-16 CenterZ=0 NormalX=0 NormalY=0 NormalZ=1 AngleXU=0 Radius=1
    g36: BSplineCurve PolesCount=3 KnotsCount=2 Degree=2 IsPeriodic=0
    g37: GeomPoint X=-8.70761 Y=-14 Z=0
    g38: GeomPoint X=-10.1571 Y=-16 Z=0
    g39: Circle CenterX=-12.8401 CenterY=-17.6958 CenterZ=0 NormalX=0 NormalY=0 NormalZ=1 AngleXU=0 Radius=1
    g40: Circle CenterX=-13.3521 CenterY=-17.9027 CenterZ=0 NormalX=0 NormalY=0 NormalZ=1 AngleXU=0 Radius=1
    g41: Circle CenterX=-14 CenterY=-18 CenterZ=0 NormalX=0 NormalY=0 NormalZ=1 AngleXU=0 Radius=1
    g42: BSplineCurve PolesCount=3 KnotsCount=2 Degree=2 IsPeriodic=0
    g43: GeomPoint X=-12.8401 Y=-17.6958 Z=0
    g44: GeomPoint X=-14 Y=-18 Z=0
    g45: LineSegment StartX=-6.2 StartY=0 StartZ=0 EndX=-7.2 EndY=0 EndZ=0
    g46: LineSegment StartX=-7.2 StartY=0 StartZ=0 EndX=-7.2 EndY=-2 EndZ=0
    g47: LineSegment StartX=-7.2 StartY=-2 StartZ=0 EndX=-6.2215 EndY=-2 EndZ=0
    g48: LineSegment StartX=-6.32538 StartY=-4 StartZ=0 EndX=-7.65538 EndY=-4 EndZ=0
    g49: LineSegment StartX=-7.65538 StartY=-4 StartZ=0 EndX=-7.65538 EndY=-5.99526 EndZ=0
    g50: LineSegment StartX=-7.65538 StartY=-5.99526 StartZ=0 EndX=-6.48644 EndY=-5.99526 EndZ=0
    g51: LineSegment StartX=-6.77343 StartY=-8 StartZ=0 EndX=-8.43343 EndY=-8 EndZ=0
    g52: LineSegment StartX=-8.43343 StartY=-8 StartZ=0 EndX=-8.43343 EndY=-10 EndZ=0
    g53: LineSegment StartX=-8.43343 StartY=-10 StartZ=0 EndX=-7.19003 EndY=-10 EndZ=0
  constraints (112):
    c: Horizontal(g0)
    c: Distance(g0) = 2
    c: Block(g0)
    c: Vertical(g1)
    c: Coincident(g2,g0)
    c: Vertical(g2)
    c: Block(g2)
    c: Coincident(g6,g2)
    c: Weight(g3) = 1
    c: Equal(g3,g4)
    c: Equal(g3,g5)
    c: InternalAlignment(g3,g6)
    c: InternalAlignment(g4,g6)
    c: InternalAlignment(g5,g6)
    c: InternalAlignment(g7,g6)
    c: InternalAlignment(g8,g6)
    c: Block(g6)
    c: Coincident(g9,g1)
    c: Coincident(g9,g6)
    c: Horizontal(g9)
    c: Vertical(g10)
    c: Block(g10)
    c: Horizontal(g11)
    c: Block(g11)
    c: Coincident(g12,g10)
    c: Horizontal(g12)
    c: Block(g12)
    c: Coincident(g13,g11)
    c: Vertical(g13)
    c: Block(g13)
    c: Coincident(g14,g10)
    c: Horizontal(g14)
    c: Block(g14)
    c: Block(g9)
    c: Block(g1)
    c: Weight(g15) = 1
    c: Equal(g15,g16)
    c: Equal(g15,g17)
    c: InternalAlignment(g15,g18)
    c: InternalAlignment(g16,g18)
    c: InternalAlignment(g17,g18)
    c: InternalAlignment(g19,g18)
    c: InternalAlignment(g20,g18)
    c: Weight(g21) = 1
    c: Equal(g21,g22)
    c: Equal(g21,g23)
    c: InternalAlignment(g21,g24)
    c: InternalAlignment(g22,g24)
    c: InternalAlignment(g23,g24)
    c: InternalAlignment(g25,g24)
    c: InternalAlignment(g26,g24)
    c: Weight(g27) = 1
    c: Equal(g27,g28)
    c: Equal(g27,g29)
    c: Coincident(g30,g14)
    c: InternalAlignment(g27,g30)
    c: InternalAlignment(g28,g30)
    c: InternalAlignment(g29,g30)
    c: InternalAlignment(g31,g30)
    c: InternalAlignment(g32,g30)
    c: Coincident(g36,g12)
    c: Weight(g33) = 1
    c: Equal(g33,g34)
    c: Equal(g33,g35)
    c: Coincident(g36,g11)
    c: InternalAlignment(g33,g36)
    c: InternalAlignment(g34,g36)
    c: InternalAlignment(g35,g36)
    c: InternalAlignment(g37,g36)
    c: InternalAlignment(g38,g36)
    c: Coincident(g42,g13)
    c: Weight(g39) = 1
    c: Equal(g39,g40)
    c: Equal(g39,g41)
    c: Coincident(g42,g1)
    c: InternalAlignment(g39,g42)
    c: InternalAlignment(g40,g42)
    c: InternalAlignment(g41,g42)
    c: InternalAlignment(g43,g42)
    c: InternalAlignment(g44,g42)
    c: Block(g18)
    c: Block(g24)
    c: Block(g30)
    c: Block(g36)
    c: Block(g42)
    c: Horizontal(g45)
    c: Coincident(g45,g0)
    c: Vertical(g46)
    c: Coincident(g46,g45)
    c: Coincident(g47,g46)
    c: Coincident(g47,g18)
    c: Horizontal(g47)
    c: Block(g46)
    c: Coincident(g48,g18)
    c: Horizontal(g48)
    c: Distance(g48) = 1.33
    c: Vertical(g49)
    c: Coincident(g49,g48)
    c: Coincident(g50,g49)
    c: Coincident(g50,g24)
    c: Horizontal(g50)
    c: Tangent(g50,g22)
    c: Horizontal(g51)
    c: Coincident(g51,g24)
    c: Block(g51)
    c: Vertical(g52)
    c: Block(g52)
    c: Coincident(g52,g51)
    c: Coincident(g53,g52)
    c: Coincident(g53,g30)
    c: Horizontal(g53)
    c: Distance(g1) = 8.5
FEATURE [Part::Feature] Face024
  shape: bbox 9.8 x 26.5 x 2e-07 mm, 1 faces, 0 solids (baked)
FEATURE [Part::Revolution] Revolve024
  Angle = 360
  Axis = (0,1,0)
  Base = (0,0,0)
  FaceMakerClass = Part::FaceMakerBullseye
  Placement = pos=(0,0,0) rot=(0,0,1;1.5708rad)
  Solid = false
  Source = -> Face024
  Symmetric = false
FEATURE [Part::Feature] Face025
  shape: bbox 9.8 x 26.5 x 2e-07 mm, 1 faces, 0 solids (baked)
FEATURE [Part::Revolution] Revolve025
  Angle = 360
  Axis = (0,1,0)
  Base = (0,0,0)
  FaceMakerClass = Part::FaceMakerBullseye
  Placement = pos=(0,0,0) rot=(0,0,1;1.5708rad)
  Solid = false
  Source = -> Face025
  Symmetric = false
FEATURE [Part::MultiFuse] Fusion033
  Placement = pos=(-18,19,36) rot=(0,0,1;0rad)
  Shapes = -> [Revolve025,Revolve024]
FEATURE [Part::Cylinder] Cylinder014
  Angle = 360
  AttacherType = Attacher::AttachEngine3D
  Height = 20
  Placement = pos=(0,0,36.15) rot=(0,0,1;0rad)
  Radius = 14.3
FEATURE [Part::Cylinder] Cylinder015
  Angle = 360
  AttacherType = Attacher::AttachEngine3D
  Height = 10
  Placement = pos=(0,0,36.15) rot=(0,0,1;0rad)
  Radius = 4
FEATURE [Part::MultiFuse] Fusion034  label="removeToCreteHoleForPlugHousing004"
  Placement = pos=(-42,19,36) rot=(0,1,0;1.5708rad)
  Shapes = -> [Cylinder014,Cylinder015]
FEATURE [Part::Cut] Cut008  label="top004"
  Base = -> Cut004
  Placement = pos=(-1,0,0) rot=(0,0,1;0rad)
  Tool = -> Fusion034
FEATURE [Part::Box] Box005  label="Cube005"
  AttacherType = Attacher::AttachEngine3D
  Height = 28
  Length = 3
  Placement = pos=(110.7,19,22) rot=(0,0,1;0rad)
  Width = 15.7
FEATURE [Part::Cylinder] Cylinder016
  Angle = 360
  AttacherType = Attacher::AttachEngine3D
  Height = 10
  Placement = pos=(0,0,36.15) rot=(0,0,1;0rad)
  Radius = 4
FEATURE [Part::Cylinder] Cylinder017
  Angle = 360
  AttacherType = Attacher::AttachEngine3D
  Height = 20
  Placement = pos=(0,0,36.15) rot=(0,0,1;0rad)
  Radius = 10.3
FEATURE [Part::MultiFuse] Fusion035  label="removeToCreteHoleForPlugHousing005"
  Placement = pos=(70,19,36) rot=(0,1,0;1.5708rad)
  Shapes = -> [Cylinder017,Cylinder016]
FEATURE [Part::Cut] Cut009  label="plugHousingTab001"
  Base = -> Box005
  Placement = pos=(-107.4,-14,0) rot=(0,0,1;0rad)
  Tool = -> Fusion035
FEATURE [Part::Box] Box006  label="Cube006"
  AttacherType = Attacher::AttachEngine3D
  Height = 28
  Length = 3
  Placement = pos=(110.7,19,22) rot=(0,0,1;0rad)
  Width = 15.7
FEATURE [Part::Cylinder] Cylinder018
  Angle = 360
  AttacherType = Attacher::AttachEngine3D
  Height = 10
  Placement = pos=(0,0,36.15) rot=(0,0,1;0rad)
  Radius = 4
FEATURE [Part::Cylinder] Cylinder019
  Angle = 360
  AttacherType = Attacher::AttachEngine3D
  Height = 20
  Placement = pos=(0,0,36.15) rot=(0,0,1;0rad)
  Radius = 10.3
FEATURE [Part::MultiFuse] Fusion036  label="removeToCreteHoleForPlugHousing006"
  Placement = pos=(70,19,36) rot=(0,1,0;1.5708rad)
  Shapes = -> [Cylinder019,Cylinder018]
FEATURE [Part::Cut] Cut010  label="plugHousingTab002"
  Base = -> Box006
  Placement = pos=(-107.4,-14,0) rot=(0,0,1;0rad)
  Tool = -> Fusion036
FEATURE [Part::MultiFuse] Fusion037
  Placement = pos=(9.6,23,0) rot=(0,0,1;3.14159rad)
  Shapes = -> [Cut009,Cut010]
FEATURE [Part::Box] Box  label="Cube"
  AttacherType = Attacher::AttachEngine3D
  Height = 10
  Length = 3
  Placement = pos=(3.3,4,12) rot=(0,0,1;0rad)
  Width = 10
FEATURE [Part::Fillet] Fillet004
  Base = -> Fusion028
  Edges = 1 edges r=2: [Edge25]
FEATURE [Part::Fillet] Fillet005  label="plugHousing046"
  Base = -> Fillet004
  Edges = 1 edges r=2: [Edge8]
FEATURE [Part::Fillet] Fillet006
  Base = -> Box
  Edges = 1 edges r=2: [Edge11]
FEATURE [Part::Box] Box007  label="Cube007"
  AttacherType = Attacher::AttachEngine3D
  Height = 10
  Length = 3
  Placement = pos=(3.3,4,50) rot=(0,0,1;0rad)
  Width = 10
FEATURE [Part::Fillet] Fillet007
  Base = -> Box007
  Edges = 1 edges r=2: [Edge12]
FEATURE [Part::Box] Box008  label="Cube008"
  AttacherType = Attacher::AttachEngine3D
  Height = 28
  Length = 4
  Placement = pos=(5,0,22) rot=(0,0,1;0rad)
  Width = 10
FEATURE [Part::Fillet] Fillet008
  Base = -> Box008
  Edges = 1 edges r=1: [Edge7]
FEATURE [Part::Fillet] Fillet009
  Base = -> Fillet008
  Edges = 1 edges r=2: [Edge5]
FEATURE [Part::Fillet] Fillet010
  Base = -> Fillet009
  Edges = 1 edges r=2: [Edge2]
FEATURE [Sketcher::SketchObject] Sketch009  label="topSketch003"
  FullyConstrained = true
  sketch-geometry (4):
    g0: LineSegment StartX=16.8446 StartY=31.512 StartZ=0 EndX=16.3251 EndY=34.4666 EndZ=0
    g1: ArcOfCircle CenterX=19 CenterY=19.2524 CenterZ=0 NormalX=0 NormalY=0 NormalZ=1 AngleXU=0 Radius=15.4476 StartAngle=1.74483 EndAngle=2.72717
    g2: ArcOfCircle CenterX=19 CenterY=19.2524 CenterZ=0 NormalX=0 NormalY=0 NormalZ=1 AngleXU=0 Radius=12.4476 StartAngle=1.74483 EndAngle=2.73189
    g3: LineSegment StartX=4.86004 StartY=25.4725 StartZ=0 EndX=7.58253 EndY=24.2107 EndZ=0
  constraints (7):
    c: Block(g0)
    c: Coincident(g1,g0)
    c: Coincident(g2,g0)
    c: Coincident(g3,g1)
    c: Coincident(g3,g2)
    c: Block(g1)
    c: Block(g2)
FEATURE [Part::Extrusion] Extrude008
  Base = -> Sketch009
  Dir = (0,0,1)
  DirMode = 2
  FaceMakerClass = Part::FaceMakerBullseye
  LengthFwd = 10
  LengthRev = 0
  Placement = pos=(0,0,31) rot=(0,0,1;0rad)
  Solid = true
  Symmetric = false
FEATURE [Part::Cylinder] Cylinder020
  Angle = 360
  AttacherType = Attacher::AttachEngine3D
  Height = 20
  Placement = pos=(0,0,36.15) rot=(0,0,1;0rad)
  Radius = 8.2
FEATURE [Part::Cylinder] Cylinder021
  Angle = 360
  AttacherType = Attacher::AttachEngine3D
  Height = 10
  Placement = pos=(0,0,36.15) rot=(0,0,1;0rad)
  Radius = 4
FEATURE [Part::MultiFuse] Fusion038  label="removeToCreteHoleForPlugHousing007"
  Placement = pos=(-42,19,36) rot=(0,1,0;1.5708rad)
  Shapes = -> [Cylinder020,Cylinder021]
FEATURE [Part::Cut] Cut011
  Base = -> Extrude008
  Tool = -> Fusion038
FEATURE [Part::Fillet] Fillet011
  Base = -> Cut011
  Edges = 1 edges r=2: [Edge1]
FEATURE [Part::Fillet] Fillet012
  Base = -> Fillet011
  Edges = 1 edges r=2.5: [Edge1]
FEATURE [Part::Fillet] Fillet013
  Base = -> Fillet012
  Edges = 1 edges r=2.5: [Edge2]
FEATURE [Part::Box] Box010  label="Cube010"
  AttacherType = Attacher::AttachEngine3D
  Height = 16
  Length = 8
  Placement = pos=(12.7,31.52,28) rot=(0,0,1;0rad)
  Width = 4
FEATURE [Sketcher::SketchObject] Sketch010  label="topSketch004"
  FullyConstrained = true
  sketch-geometry (4):
    g0: LineSegment StartX=16.8446 StartY=31.512 StartZ=0 EndX=16.3251 EndY=34.4666 EndZ=0
    g1: ArcOfCircle CenterX=19 CenterY=19.2524 CenterZ=0 NormalX=0 NormalY=0 NormalZ=1 AngleXU=0 Radius=15.4476 StartAngle=1.74483 EndAngle=2.72717
    g2: ArcOfCircle CenterX=19 CenterY=19.2524 CenterZ=0 NormalX=0 NormalY=0 NormalZ=1 AngleXU=0 Radius=12.4476 StartAngle=1.74483 EndAngle=2.73189
    g3: LineSegment StartX=4.86004 StartY=25.4725 StartZ=0 EndX=7.58253 EndY=24.2107 EndZ=0
  constraints (7):
    c: Block(g0)
    c: Coincident(g1,g0)
    c: Coincident(g2,g0)
    c: Coincident(g3,g1)
    c: Coincident(g3,g2)
    c: Block(g1)
    c: Block(g2)
FEATURE [Part::Cylinder] Cylinder022
  Angle = 360
  AttacherType = Attacher::AttachEngine3D
  Height = 10
  Placement = pos=(0,0,36.15) rot=(0,0,1;0rad)
  Radius = 4
FEATURE [Sketcher::SketchObject] Sketch011  label="topSketch005"
  FullyConstrained = true
  sketch-geometry (4):
    g0: LineSegment StartX=16.8446 StartY=31.512 StartZ=0 EndX=16.3251 EndY=34.4666 EndZ=0
    g1: ArcOfCircle CenterX=19 CenterY=19.2524 CenterZ=0 NormalX=0 NormalY=0 NormalZ=1 AngleXU=0 Radius=15.4476 StartAngle=1.74483 EndAngle=2.72717
    g2: ArcOfCircle CenterX=19 CenterY=19.2524 CenterZ=0 NormalX=0 NormalY=0 NormalZ=1 AngleXU=0 Radius=12.4476 StartAngle=1.74483 EndAngle=2.73189
    g3: LineSegment StartX=4.86004 StartY=25.4725 StartZ=0 EndX=7.58253 EndY=24.2107 EndZ=0
  constraints (7):
    c: Block(g0)
    c: Coincident(g1,g0)
    c: Coincident(g2,g0)
    c: Coincident(g3,g1)
    c: Coincident(g3,g2)
    c: Block(g1)
    c: Block(g2)
FEATURE [Part::Extrusion] Extrude010
  Base = -> Sketch011
  Dir = (0,0,1)
  DirMode = 2
  FaceMakerClass = Part::FaceMakerBullseye
  LengthFwd = 10.6
  LengthRev = 0
  Placement = pos=(0,0,31) rot=(0,0,1;0rad)
  Solid = true
  Symmetric = false
FEATURE [Part::Cylinder] Cylinder023
  Angle = 360
  AttacherType = Attacher::AttachEngine3D
  Height = 20
  Placement = pos=(0,0,36.15) rot=(0,0,1;0rad)
  Radius = 8.2
FEATURE [Part::MultiFuse] Fusion039  label="removeToCreteHoleForPlugHousing008"
  Placement = pos=(-42,19,36) rot=(0,1,0;1.5708rad)
  Shapes = -> [Cylinder023,Cylinder022]
FEATURE [Part::Cut] Cut012
  Base = -> Extrude010
  Placement = pos=(0,0,-0.3) rot=(0,0,1;0rad)
  Tool = -> Fusion039
FEATURE [Part::Cut] Cut013
  Base = -> Box010
  Tool = -> Cut012
FEATURE [Part::Fillet] Fillet014
  Base = -> Cut013
  Edges = 1 edges r=0.7: [Edge13]
FEATURE [Part::Fillet] Fillet015
  Base = -> Fillet014
  Edges = 1 edges r=0.7: [Edge13]
FEATURE [Part::Fillet] Fillet016
  Base = -> Fillet015
  Edges = 1 edges r=0.7: [Edge16]
FEATURE [Part::Fillet] Fillet017
  Base = -> Fillet016
  Edges = 1 edges r=0.7: [Edge11]
FEATURE [Part::Fillet] Fillet018
  Base = -> Fillet017
  Edges = 1 edges r=0.7: [Edge10]
FEATURE [Part::Fillet] Fillet019
  Base = -> Fillet018
  Edges = 1 edges r=1.2: [Edge5]
FEATURE [Part::Fillet] Fillet020
  Base = -> Fillet019
  Edges = 1 edges r=1.2: [Edge12]
FEATURE [Part::Fillet] Fillet021
  Base = -> Fillet020
  Edges = 1 edges r=2: [Edge1]
  Placement = pos=(0.3,0,0) rot=(0,0,1;0rad)
FEATURE [Part::MultiFuse] Fusion040  label="top005"
  Shapes = -> [Cut008,Fillet021]
FEATURE [Part::MultiFuse] Fusion041  label="wireHolder"
  Shapes = -> [Fusion033,Fillet013]
FEATURE [Part::MultiFuse] Fusion042
  Shapes = -> [Fillet007,Fusion041]
FEATURE [Part::MultiFuse] Fusion043  label="wireHolder001"
  Shapes = -> [Fusion042,Fillet010]
FEATURE [Part::MultiFuse] Fusion044  label="wireHolder002"
  Shapes = -> [Fillet006,Fusion037,Fusion043]
FEATURE [Part::Feature] Face026
  shape: bbox 11 x 6 x 2e-07 mm, 1 faces, 0 solids (baked)
FEATURE [Part::Revolution] Revolve026
  Angle = 360
  Axis = (0,1,0)
  Base = (0,0,0)
  FaceMakerClass = Part::FaceMakerBullseye
  Placement = pos=(30.3,-1,19.7) rot=(0,0,1;0rad)
  Solid = false
  Source = -> Face026
  Symmetric = false
FEATURE [Sketcher::SketchObject] Sketch013  label="topSketch006"
  FullyConstrained = true
  sketch-geometry (13):
    g0: LineSegment StartX=117 StartY=19 StartZ=0 EndX=117 EndY=38 EndZ=0
    g1: ArcOfCircle CenterX=98 CenterY=19 CenterZ=0 NormalX=0 NormalY=0 NormalZ=1 AngleXU=0 Radius=19 StartAngle=5.7297 EndAngle=6.28319
    g2: LineSegment StartX=0 StartY=3 StartZ=0 EndX=0 EndY=19 EndZ=0
    g3: LineSegment StartX=19 StartY=38 StartZ=0 EndX=117 EndY=38 EndZ=0
    g4: ArcOfCircle CenterX=19 CenterY=19 CenterZ=0 NormalX=0 NormalY=0 NormalZ=1 AngleXU=0 Radius=19 StartAngle=1.5708 EndAngle=3.14159
    g5: ArcOfCircle CenterX=19 CenterY=19 CenterZ=0 NormalX=0 NormalY=0 NormalZ=1 AngleXU=0 Radius=16 StartAngle=1.5708 EndAngle=3.14159
    g6: ArcOfCircle CenterX=98 CenterY=19 CenterZ=0 NormalX=0 NormalY=0 NormalZ=1 AngleXU=0 Radius=16 StartAngle=5.60905 EndAngle=6.28319
    g7: LineSegment StartX=114 StartY=19 StartZ=0 EndX=114 EndY=35 EndZ=0
    g8: LineSegment StartX=110.5 StartY=9.01251 StartZ=0 EndX=114.163 EndY=9.01251 EndZ=0
    g9: LineSegment StartX=114 StartY=35 StartZ=0 EndX=19 EndY=35 EndZ=0
    g10: LineSegment StartX=0 StartY=3 StartZ=0 EndX=0 EndY=0 EndZ=0
    g11: LineSegment StartX=3 StartY=0 StartZ=0 EndX=0 EndY=0 EndZ=0
    g12: LineSegment StartX=3 StartY=19 StartZ=0 EndX=3 EndY=0 EndZ=0
  constraints (33):
    c: Vertical(g0)
    c: Distance(g0) = 19
    c: Block(g0)
    c: Coincident(g1,g0)
    c: Block(g1)
    c: Vertical(g2)
    c: Block(g2)
    c: Coincident(g3,g0)
    c: Horizontal(g3)
    c: Distance(g3) = 98
    c: Coincident(g4,g3)
    c: Coincident(g4,g2)
    c: Block(g4)
    c: Coincident(g5,g4)
    c: Coincident(g6,g1)
    c: Block(g6)
    c: Block(g5)
    c: Coincident(g7,g6)
    c: Vertical(g7)
    c: Coincident(g8,g6)
    c: Coincident(g8,g1)
    c: Coincident(g9,g7)
    c: Coincident(g9,g5)
    c: Horizontal(g9)
    c: Tangent(g9,g5)
    c: Coincident(g10,g2)
    c: Distance(g10) = 3
    c: Vertical(g10)
    c: Coincident(g11,g10)
    c: Horizontal(g11)
    c: Coincident(g12,g5)
    c: Coincident(g12,g11)
    c: Vertical(g12)
FEATURE [Part::Extrusion] Extrude011  label="top006"
  Base = -> Sketch013
  Dir = (0,0,1)
  DirMode = 2
  FaceMakerClass = Part::FaceMakerBullseye
  LengthFwd = 72
  LengthRev = 0
  Solid = true
  Symmetric = false
FEATURE [Sketcher::SketchObject] Sketch014
  FullyConstrained = true
  MapMode = 3
  Placement = pos=(0,0,0) rot=(1,0,0;1.5708rad)
  Support = -> [Extrude011]
  sketch-geometry (8):
    g0: Circle CenterX=80.351 CenterY=-67.6202 CenterZ=0 NormalX=0 NormalY=0 NormalZ=1 AngleXU=0 Radius=2
    g1: Circle CenterX=80.351 CenterY=-67.6202 CenterZ=0 NormalX=0 NormalY=0 NormalZ=1 AngleXU=0 Radius=3
    g2: Circle CenterX=80.351 CenterY=-4.92017 CenterZ=0 NormalX=0 NormalY=0 NormalZ=1 AngleXU=0 Radius=2
    g3: Circle CenterX=80.351 CenterY=-4.92017 CenterZ=0 NormalX=0 NormalY=0 NormalZ=1 AngleXU=0 Radius=3
    g4: Circle CenterX=23.851 CenterY=-4.92017 CenterZ=0 NormalX=0 NormalY=0 NormalZ=1 AngleXU=0 Radius=2
    g5: Circle CenterX=23.851 CenterY=-4.92017 CenterZ=0 NormalX=0 NormalY=0 NormalZ=1 AngleXU=0 Radius=3
    g6: Circle CenterX=23.851 CenterY=-67.6202 CenterZ=0 NormalX=0 NormalY=0 NormalZ=1 AngleXU=0 Radius=2
    g7: Circle CenterX=23.851 CenterY=-67.6202 CenterZ=0 NormalX=0 NormalY=0 NormalZ=1 AngleXU=0 Radius=3
  constraints (8):
    c: Block(g3)
    c: Block(g2)
    c: Block(g1)
    c: Block(g0)
    c: Block(g6)
    c: Block(g7)
    c: Block(g4)
    c: Block(g5)
FEATURE [Part::Feature] Face027
  shape: bbox 11 x 6 x 2e-07 mm, 1 faces, 0 solids (baked)
FEATURE [Part::Revolution] Revolve027
  Angle = 360
  Axis = (0,1,0)
  Base = (0,0,0)
  FaceMakerClass = Part::FaceMakerBullseye
  Placement = pos=(30.3,-1,51.7) rot=(0,0,1;0rad)
  Solid = false
  Source = -> Face027
  Symmetric = false
FEATURE [Part::Feature] Face028
  shape: bbox 11 x 6 x 2e-07 mm, 1 faces, 0 solids (baked)
FEATURE [Part::Revolution] Revolve028
  Angle = 360
  Axis = (0,1,0)
  Base = (0,0,0)
  FaceMakerClass = Part::FaceMakerBullseye
  Placement = pos=(62.3,-1,19.7) rot=(0,0,1;0rad)
  Solid = false
  Source = -> Face028
  Symmetric = false
FEATURE [Part::Feature] Face029
  shape: bbox 11 x 6 x 2e-07 mm, 1 faces, 0 solids (baked)
FEATURE [Part::Revolution] Revolve029
  Angle = 360
  Axis = (0,1,0)
  Base = (0,0,0)
  FaceMakerClass = Part::FaceMakerBullseye
  Placement = pos=(62.3,-1,51.7) rot=(0,0,1;0rad)
  Solid = false
  Source = -> Face029
  Symmetric = false
FEATURE [Part::Feature] Wire
  shape: bbox 11 x 5.2 x 2e-07 mm, 0 faces, 0 solids (baked)
FEATURE [Part::Revolution] Revolve030
  Angle = 360
  Axis = (0,1,0)
  Base = (0,0,0)
  FaceMakerClass = Part::FaceMakerBullseye
  Placement = pos=(30.3,38,19.7) rot=(0,0,1;0rad)
  Solid = true
  Source = -> Wire
  Symmetric = false
FEATURE [Part::Feature] Wire001
  shape: bbox 11 x 5.2 x 2e-07 mm, 0 faces, 0 solids (baked)
FEATURE [Part::Revolution] Revolve031
  Angle = 360
  Axis = (0,1,0)
  Base = (0,0,0)
  FaceMakerClass = Part::FaceMakerBullseye
  Placement = pos=(30.3,38,51.7) rot=(0,0,1;0rad)
  Solid = true
  Source = -> Wire001
  Symmetric = false
FEATURE [Part::Feature] Wire002
  shape: bbox 11 x 5.2 x 2e-07 mm, 0 faces, 0 solids (baked)
FEATURE [Part::Revolution] Revolve032
  Angle = 360
  Axis = (0,1,0)
  Base = (0,0,0)
  FaceMakerClass = Part::FaceMakerBullseye
  Placement = pos=(62.3,38,51.7) rot=(0,0,1;0rad)
  Solid = true
  Source = -> Wire002
  Symmetric = false
FEATURE [Part::Feature] Wire003
  shape: bbox 11 x 5.2 x 2e-07 mm, 0 faces, 0 solids (baked)
FEATURE [Part::Revolution] Revolve033
  Angle = 360
  Axis = (0,1,0)
  Base = (0,0,0)
  FaceMakerClass = Part::FaceMakerBullseye
  Placement = pos=(62.3,38,19.7) rot=(0,0,1;0rad)
  Solid = true
  Source = -> Wire003
  Symmetric = false
FEATURE [Part::MultiFuse] Fusion045  label="altRandScrewHousing"
  Shapes = -> [Revolve029,Revolve027,Revolve028,Revolve026]
FEATURE [Part::MultiFuse] Fusion046  label="fanScrewHousing"
  Shapes = -> [Revolve033,Revolve032,Revolve031,Revolve030]
FEATURE [Sketcher::SketchObject] Sketch015
  FullyConstrained = true
  sketch-geometry (17):
    g0: Circle CenterX=-3.5 CenterY=23.5 CenterZ=0 NormalX=0 NormalY=0 NormalZ=1 AngleXU=0 Radius=1
    g1: Circle CenterX=-1 CenterY=15.25 CenterZ=0 NormalX=0 NormalY=0 NormalZ=1 AngleXU=0 Radius=1
    g2: Circle CenterX=-3.5 CenterY=7 CenterZ=0 NormalX=0 NormalY=0 NormalZ=1 AngleXU=0 Radius=1
    g3: BSplineCurve PolesCount=3 KnotsCount=2 Degree=2 IsPeriodic=0
    g4: GeomPoint X=-3.5 Y=23.5 Z=0
    g5: GeomPoint X=-3.5 Y=7 Z=0
    g6: Circle CenterX=-4.8 CenterY=30.5 CenterZ=0 NormalX=0 NormalY=0 NormalZ=1 AngleXU=0 Radius=1
    g7: Circle CenterX=-3.5 CenterY=30.5 CenterZ=0 NormalX=0 NormalY=0 NormalZ=1 AngleXU=0 Radius=1
    g8: Circle CenterX=-3.5 CenterY=29.2 CenterZ=0 NormalX=0 NormalY=0 NormalZ=1 AngleXU=0 Radius=1
    g9: BSplineCurve PolesCount=3 KnotsCount=2 Degree=2 IsPeriodic=0
    g10: GeomPoint X=-4.8 Y=30.5 Z=0
    g11: GeomPoint X=-3.5 Y=29.2 Z=0
    g12: LineSegment StartX=-3.5 StartY=29.2 StartZ=0 EndX=-3.5 EndY=23.5 EndZ=0
    g13: LineSegment StartX=-4.8 StartY=30.5 StartZ=0 EndX=0 EndY=30.5 EndZ=0
    g14: LineSegment StartX=-3.5 StartY=0.3 StartZ=0 EndX=0 EndY=0.3 EndZ=0
    g15: LineSegment StartX=-3.5 StartY=0.3 StartZ=0 EndX=-3.5 EndY=7 EndZ=0
    g16: LineSegment StartX=0 StartY=0.3 StartZ=0 EndX=0 EndY=30.5 EndZ=0
  constraints (34):
    c: Weight(g0) = 1
    c: Equal(g0,g1)
    c: Equal(g0,g2)
    c: InternalAlignment(g0,g3)
    c: InternalAlignment(g1,g3)
    c: InternalAlignment(g2,g3)
    c: InternalAlignment(g4,g3)
    c: InternalAlignment(g5,g3)
    c: Block(g3)
    c: Weight(g6) = 1
    c: Equal(g6,g7)
    c: Equal(g6,g8)
    c: InternalAlignment(g6,g9)
    c: InternalAlignment(g7,g9)
    c: InternalAlignment(g8,g9)
    c: InternalAlignment(g10,g9)
    c: InternalAlignment(g11,g9)
    c: Block(g9)
    c: Coincident(g12,g9)
    c: Coincident(g12,g3)
    c: Vertical(g12)
    c: Coincident(g13,g9)
    c: Horizontal(g13)
    c: Distance(g13) = 4.8
    c: Horizontal(g14)
    c: Block(g14)
    c: Coincident(g15,g14)
    c: Coincident(g15,g3)
    c: Vertical(g15)
    c: Coincident(g16,g14)
    c: Coincident(g16,g13)
    c: Vertical(g16)
    c: Tangent(g16,g1)
    c: Distance(g14) = 3.5
FEATURE [Sketcher::SketchObject] Sketch016
  FullyConstrained = true
  sketch-geometry (16):
    g0: Circle CenterX=-3.5 CenterY=23.5 CenterZ=0 NormalX=0 NormalY=0 NormalZ=1 AngleXU=0 Radius=1
    g1: Circle CenterX=-1 CenterY=15.25 CenterZ=0 NormalX=0 NormalY=0 NormalZ=1 AngleXU=0 Radius=1
    g2: Circle CenterX=-3.5 CenterY=7 CenterZ=0 NormalX=0 NormalY=0 NormalZ=1 AngleXU=0 Radius=1
    g3: BSplineCurve PolesCount=3 KnotsCount=2 Degree=2 IsPeriodic=0
    g4: GeomPoint X=-3.5 Y=23.5 Z=0
    g5: GeomPoint X=-3.5 Y=7 Z=0
    g6: LineSegment StartX=-3.5 StartY=28.2 StartZ=0 EndX=-3.5 EndY=23.5 EndZ=0
    g7: LineSegment StartX=0 StartY=29.5 StartZ=0 EndX=0 EndY=30 EndZ=0
    g8: LineSegment StartX=-3.5 StartY=28.2 StartZ=0 EndX=-3.5 EndY=30 EndZ=0
    g9: LineSegment StartX=0 StartY=30 StartZ=0 EndX=0 EndY=30.5 EndZ=0
    g10: LineSegment StartX=0 StartY=30.5 StartZ=0 EndX=-3.5 EndY=30.5 EndZ=0
    g11: LineSegment StartX=-3.5 StartY=30.5 StartZ=0 EndX=-3.5 EndY=30 EndZ=0
    g12: LineSegment StartX=0 StartY=29.5 StartZ=0 EndX=0 EndY=5 EndZ=0
    g13: LineSegment StartX=-3.5 StartY=0.3 StartZ=0 EndX=-3.5 EndY=7 EndZ=0
    g14: LineSegment StartX=-3.5 StartY=0.3 StartZ=0 EndX=0 EndY=0.3 EndZ=0
    g15: LineSegment StartX=0 StartY=5 StartZ=0 EndX=0 EndY=0.3 EndZ=0
  constraints (39):
    c: Weight(g0) = 1
    c: Equal(g0,g1)
    c: Equal(g0,g2)
    c: InternalAlignment(g0,g3)
    c: InternalAlignment(g1,g3)
    c: InternalAlignment(g2,g3)
    c: InternalAlignment(g4,g3)
    c: InternalAlignment(g5,g3)
    c: Block(g3)
    c: Coincident(g6,g3)
    c: Vertical(g6)
    c: Vertical(g7)
    c: Distance(g7) = 0.5
    c: Coincident(g8,g6)
    c: Vertical(g8)
    c: Block(g6)
    c: Block(g7)
    c: Vertical(g9)
    c: Equal(g7,g9) = 0.5
    c: Block(g9)
    c: Coincident(g9,g7)
    c: Horizontal(g10)
    c: Coincident(g10,g9)
    c: Coincident(g11,g10)
    c: Coincident(g11,g8)
    c: Vertical(g11)
    c: Block(g11)
    c: Coincident(g12,g7)
    c: Vertical(g12)
    c: Coincident(g13,g3)
    c: Vertical(g13)
    c: Distance(g13) = 6.7
    c: Coincident(g14,g13)
    c: Horizontal(g14)
    c: Block(g14)
    c: Coincident(g15,g12)
    c: Coincident(g15,g14)
    c: Vertical(g15)
    c: Block(g15)
FEATURE [Sketcher::SketchObject] Sketch017
  FullyConstrained = true
  sketch-geometry (11):
    g0: LineSegment StartX=-3.5 StartY=1e-16 StartZ=0 EndX=-1.6 EndY=1e-16 EndZ=0
    g1: LineSegment StartX=-1.6 StartY=1e-16 StartZ=0 EndX=-1.6 EndY=1.5 EndZ=0
    g2: LineSegment StartX=-3.5 StartY=1.5 StartZ=0 EndX=-1.6 EndY=1.5 EndZ=0
    g3: LineSegment StartX=-3.5 StartY=1e-16 StartZ=0 EndX=-4.8 EndY=1e-16 EndZ=0
    g4: Circle CenterX=-3.5 CenterY=1.3 CenterZ=0 NormalX=0 NormalY=0 NormalZ=1 AngleXU=0 Radius=1
    g5: Circle CenterX=-3.5 CenterY=1e-16 CenterZ=0 NormalX=0 NormalY=0 NormalZ=1 AngleXU=0 Radius=1
    g6: Circle CenterX=-4.8 CenterY=1e-16 CenterZ=0 NormalX=0 NormalY=0 NormalZ=1 AngleXU=0 Radius=1
    g7: BSplineCurve PolesCount=3 KnotsCount=2 Degree=2 IsPeriodic=0
    g8: GeomPoint X=-3.5 Y=1.3 Z=0
    g9: GeomPoint X=-4.8 Y=1e-16 Z=0
    g10: LineSegment StartX=-3.5 StartY=1.3 StartZ=0 EndX=-3.5 EndY=1.5 EndZ=0
  constraints (24):
    c: Horizontal(g0)
    c: Distance(g0) = 1.9
    c: Block(g0)
    c: Coincident(g1,g0)
    c: Vertical(g1)
    c: Coincident(g2,g1)
    c: Horizontal(g2)
    c: Coincident(g3,g0)
    c: Horizontal(g3)
    c: Distance(g3) = 1.3
    c: Weight(g4) = 1
    c: Equal(g4,g5)
    c: Coincident(g5,g0)
    c: Equal(g4,g6)
    c: Coincident(g7,g3)
    c: InternalAlignment(g4,g7)
    c: InternalAlignment(g5,g7)
    c: InternalAlignment(g6,g7)
    c: InternalAlignment(g8,g7)
    c: InternalAlignment(g9,g7)
    c: Coincident(g10,g7)
    c: Coincident(g10,g2)
    c: Vertical(g10)
    c: Block(g10)
FEATURE [Part::Feature] Face035
  shape: bbox 3.2 x 1.5 x 2e-07 mm, 1 faces, 0 solids (baked)
FEATURE [Part::Revolution] Revolve039  label="backCaseScrewRetainer"
  Angle = 360
  Axis = (0,1,0)
  Base = (0,0,0)
  FaceMakerClass = Part::FaceMakerBullseye
  Placement = pos=(12.5,3,62) rot=(0,0,1;0rad)
  Solid = false
  Source = -> Face035
  Symmetric = false
FEATURE [Part::Feature] Face036
  shape: bbox 3.2 x 1.5 x 2e-07 mm, 1 faces, 0 solids (baked)
FEATURE [Part::Feature] Face039
  shape: bbox 4.8 x 30.2 x 2e-07 mm, 1 faces, 0 solids (baked)
FEATURE [Part::Revolution] Revolve043  label="frontCaseScrewPost002"
  Angle = 360
  Axis = (0,1,0)
  Base = (0,0,0)
  FaceMakerClass = Part::FaceMakerBullseye
  Placement = pos=(89.5,4.5,3.5) rot=(0,0,1;0rad)
  Solid = false
  Source = -> Face039
  Symmetric = false
FEATURE [Part::Feature] Face042
  shape: bbox 4.8 x 30.2 x 2e-07 mm, 1 faces, 0 solids (baked)
FEATURE [Part::Revolution] Revolve046  label="frontCaseScrewPost003"
  Angle = 360
  Axis = (0,1,0)
  Base = (0,0,0)
  FaceMakerClass = Part::FaceMakerBullseye
  Placement = pos=(89.5,4.5,68.5) rot=(0,0,1;0rad)
  Solid = false
  Source = -> Face042
  Symmetric = false
FEATURE [Part::Feature] Face043
  shape: bbox 3.2 x 1.5 x 2e-07 mm, 1 faces, 0 solids (baked)
FEATURE [Part::Revolution] Revolve047  label="frontCaseScrewRetainer002"
  Angle = 360
  Axis = (0,1,0)
  Base = (0,0,0)
  FaceMakerClass = Part::FaceMakerBullseye
  Placement = pos=(89.5,3,68.5) rot=(0,0,1;0rad)
  Solid = false
  Source = -> Face043
  Symmetric = false
FEATURE [Part::Feature] Face044
  shape: bbox 3.2 x 1.5 x 2e-07 mm, 1 faces, 0 solids (baked)
FEATURE [Part::Revolution] Revolve048  label="frontCaseScrewRetainer003"
  Angle = 360
  Axis = (0,1,0)
  Base = (0,0,0)
  FaceMakerClass = Part::FaceMakerBullseye
  Placement = pos=(89.5,3,3.5) rot=(0,0,1;0rad)
  Solid = false
  Source = -> Face044
  Symmetric = false
FEATURE [App::MeasureDistance] Distance002  label="Distance: 1.67 mm"
  Distance = 1.66921
  P1 = (99.2361,4.7524,71.7)
  P2 = (99.2347,6.42161,71.7)
FEATURE [Sketcher::SketchObject] Sketch018
  FullyConstrained = true
  sketch-geometry (7):
    g0: LineSegment StartX=0 StartY=0 StartZ=0 EndX=0 EndY=6 EndZ=0
    g1: Circle CenterX=0 CenterY=0 CenterZ=0 NormalX=0 NormalY=0 NormalZ=1 AngleXU=0 Radius=1
    g2: Circle CenterX=8 CenterY=6 CenterZ=0 NormalX=0 NormalY=0 NormalZ=1 AngleXU=0 Radius=1
    g3: BSplineCurve PolesCount=3 KnotsCount=2 Degree=2 IsPeriodic=0
    g4: GeomPoint X=0 Y=0 Z=0
    g5: GeomPoint X=8 Y=6 Z=0
    g6: LineSegment StartX=0 StartY=6 StartZ=0 EndX=8 EndY=6 EndZ=0
  constraints (14):
    c: Coincident(g0,g-1)
    c: Distance(g0) = 6
    c: Vertical(g0)
    c: Coincident(g3,g0)
    c: Weight(g1) = 1
    c: Equal(g1,g2)
    c: InternalAlignment(g1,g3)
    c: InternalAlignment(g2,g3)
    c: InternalAlignment(g4,g3)
    c: InternalAlignment(g5,g3)
    c: Block(g3)
    c: Coincident(g6,g0)
    c: Coincident(g6,g3)
    c: Horizontal(g6)
FEATURE [Part::Extrusion] Extrude012  label="caseScrewPillarBracket"
  Base = -> Sketch018
  Dir = (0,0,1)
  DirMode = 2
  FaceMakerClass = Part::FaceMakerBullseye
  LengthFwd = 2.4
  LengthRev = 0
  Placement = pos=(15.76,29,8.8) rot=(0,1,0;0rad)
  Solid = true
  Symmetric = false
FEATURE [Sketcher::SketchObject] Sketch019
  FullyConstrained = true
  sketch-geometry (7):
    g0: LineSegment StartX=0 StartY=0 StartZ=0 EndX=0 EndY=6 EndZ=0
    g1: Circle CenterX=0 CenterY=0 CenterZ=0 NormalX=0 NormalY=0 NormalZ=1 AngleXU=0 Radius=1
    g2: Circle CenterX=8 CenterY=6 CenterZ=0 NormalX=0 NormalY=0 NormalZ=1 AngleXU=0 Radius=1
    g3: BSplineCurve PolesCount=3 KnotsCount=2 Degree=2 IsPeriodic=0
    g4: GeomPoint X=0 Y=0 Z=0
    g5: GeomPoint X=8 Y=6 Z=0
    g6: LineSegment StartX=0 StartY=6 StartZ=0 EndX=8 EndY=6 EndZ=0
  constraints (14):
    c: Coincident(g0,g-1)
    c: Distance(g0) = 6
    c: Vertical(g0)
    c: Coincident(g3,g0)
    c: Weight(g1) = 1
    c: Equal(g1,g2)
    c: InternalAlignment(g1,g3)
    c: InternalAlignment(g2,g3)
    c: InternalAlignment(g4,g3)
    c: InternalAlignment(g5,g3)
    c: Block(g3)
    c: Coincident(g6,g0)
    c: Coincident(g6,g3)
    c: Horizontal(g6)
FEATURE [Part::Extrusion] Extrude013  label="caseScrewPillarBracket001"
  Base = -> Sketch019
  Dir = (0,0,1)
  DirMode = 2
  FaceMakerClass = Part::FaceMakerBullseye
  LengthFwd = 2.4
  LengthRev = 0
  Placement = pos=(15.76,29,60.8) rot=(0,0,1;0rad)
  Solid = true
  Symmetric = false
FEATURE [Sketcher::SketchObject] Sketch020
  FullyConstrained = true
  sketch-geometry (7):
    g0: LineSegment StartX=0 StartY=0 StartZ=0 EndX=0 EndY=6 EndZ=0
    g1: Circle CenterX=0 CenterY=0 CenterZ=0 NormalX=0 NormalY=0 NormalZ=1 AngleXU=0 Radius=1
    g2: Circle CenterX=8 CenterY=6 CenterZ=0 NormalX=0 NormalY=0 NormalZ=1 AngleXU=0 Radius=1
    g3: BSplineCurve PolesCount=3 KnotsCount=2 Degree=2 IsPeriodic=0
    g4: GeomPoint X=0 Y=0 Z=0
    g5: GeomPoint X=8 Y=6 Z=0
    g6: LineSegment StartX=0 StartY=6 StartZ=0 EndX=8 EndY=6 EndZ=0
  constraints (14):
    c: Coincident(g0,g-1)
    c: Distance(g0) = 6
    c: Vertical(g0)
    c: Coincident(g3,g0)
    c: Weight(g1) = 1
    c: Equal(g1,g2)
    c: InternalAlignment(g1,g3)
    c: InternalAlignment(g2,g3)
    c: InternalAlignment(g4,g3)
    c: InternalAlignment(g5,g3)
    c: Block(g3)
    c: Coincident(g6,g0)
    c: Coincident(g6,g3)
    c: Horizontal(g6)
FEATURE [Part::Extrusion] Extrude014  label="caseScrewPillarBracket002"
  Base = -> Sketch020
  Dir = (0,0,1)
  DirMode = 2
  FaceMakerClass = Part::FaceMakerBullseye
  LengthFwd = 2.4
  LengthRev = 0
  Placement = pos=(13.7,29,13.26) rot=(0,-1,0;1.5708rad)
  Solid = true
  Symmetric = false
FEATURE [Sketcher::SketchObject] Sketch021
  FullyConstrained = true
  sketch-geometry (7):
    g0: LineSegment StartX=0 StartY=0 StartZ=0 EndX=0 EndY=6 EndZ=0
    g1: Circle CenterX=0 CenterY=0 CenterZ=0 NormalX=0 NormalY=0 NormalZ=1 AngleXU=0 Radius=1
    g2: Circle CenterX=8 CenterY=6 CenterZ=0 NormalX=0 NormalY=0 NormalZ=1 AngleXU=0 Radius=1
    g3: BSplineCurve PolesCount=3 KnotsCount=2 Degree=2 IsPeriodic=0
    g4: GeomPoint X=0 Y=0 Z=0
    g5: GeomPoint X=8 Y=6 Z=0
    g6: LineSegment StartX=0 StartY=6 StartZ=0 EndX=8 EndY=6 EndZ=0
  constraints (14):
    c: Coincident(g0,g-1)
    c: Distance(g0) = 6
    c: Vertical(g0)
    c: Coincident(g3,g0)
    c: Weight(g1) = 1
    c: Equal(g1,g2)
    c: InternalAlignment(g1,g3)
    c: InternalAlignment(g2,g3)
    c: InternalAlignment(g4,g3)
    c: InternalAlignment(g5,g3)
    c: Block(g3)
    c: Coincident(g6,g0)
    c: Coincident(g6,g3)
    c: Horizontal(g6)
FEATURE [Part::Extrusion] Extrude015  label="caseScrewPillarBracket003"
  Base = -> Sketch021
  Dir = (0,0,1)
  DirMode = 2
  FaceMakerClass = Part::FaceMakerBullseye
  LengthFwd = 2.4
  LengthRev = 0
  Placement = pos=(11.3,29,58.74) rot=(0,1,0;1.5708rad)
  Solid = true
  Symmetric = false
FEATURE [Sketcher::SketchObject] Sketch022
  FullyConstrained = true
  sketch-geometry (7):
    g0: LineSegment StartX=0 StartY=0 StartZ=0 EndX=0 EndY=6 EndZ=0
    g1: Circle CenterX=0 CenterY=0 CenterZ=0 NormalX=0 NormalY=0 NormalZ=1 AngleXU=0 Radius=1
    g2: Circle CenterX=8 CenterY=6 CenterZ=0 NormalX=0 NormalY=0 NormalZ=1 AngleXU=0 Radius=1
    g3: BSplineCurve PolesCount=3 KnotsCount=2 Degree=2 IsPeriodic=0
    g4: GeomPoint X=0 Y=0 Z=0
    g5: GeomPoint X=8 Y=6 Z=0
    g6: LineSegment StartX=0 StartY=6 StartZ=0 EndX=8 EndY=6 EndZ=0
  constraints (14):
    c: Coincident(g0,g-1)
    c: Distance(g0) = 6
    c: Vertical(g0)
    c: Coincident(g3,g0)
    c: Weight(g1) = 1
    c: Equal(g1,g2)
    c: InternalAlignment(g1,g3)
    c: InternalAlignment(g2,g3)
    c: InternalAlignment(g4,g3)
    c: InternalAlignment(g5,g3)
    c: Block(g3)
    c: Coincident(g6,g0)
    c: Coincident(g6,g3)
    c: Horizontal(g6)
FEATURE [Part::Extrusion] Extrude016  label="caseScrewPillarBracket004"
  Base = -> Sketch022
  Dir = (0,0,1)
  DirMode = 2
  FaceMakerClass = Part::FaceMakerBullseye
  LengthFwd = 2.4
  LengthRev = 0
  Placement = pos=(88.3,29,65.23) rot=(0,1,0;1.5708rad)
  Solid = true
  Symmetric = false
FEATURE [Sketcher::SketchObject] Sketch023
  FullyConstrained = true
  sketch-geometry (7):
    g0: LineSegment StartX=0 StartY=0 StartZ=0 EndX=0 EndY=6 EndZ=0
    g1: Circle CenterX=0 CenterY=0 CenterZ=0 NormalX=0 NormalY=0 NormalZ=1 AngleXU=0 Radius=1
    g2: Circle CenterX=8 CenterY=6 CenterZ=0 NormalX=0 NormalY=0 NormalZ=1 AngleXU=0 Radius=1
    g3: BSplineCurve PolesCount=3 KnotsCount=2 Degree=2 IsPeriodic=0
    g4: GeomPoint X=0 Y=0 Z=0
    g5: GeomPoint X=8 Y=6 Z=0
    g6: LineSegment StartX=0 StartY=6 StartZ=0 EndX=8 EndY=6 EndZ=0
  constraints (14):
    c: Coincident(g0,g-1)
    c: Distance(g0) = 6
    c: Vertical(g0)
    c: Coincident(g3,g0)
    c: Weight(g1) = 1
    c: Equal(g1,g2)
    c: InternalAlignment(g1,g3)
    c: InternalAlignment(g2,g3)
    c: InternalAlignment(g4,g3)
    c: InternalAlignment(g5,g3)
    c: Block(g3)
    c: Coincident(g6,g0)
    c: Coincident(g6,g3)
    c: Horizontal(g6)
FEATURE [Part::Extrusion] Extrude017  label="caseScrewPillarBracket005"
  Base = -> Sketch023
  Dir = (0,0,1)
  DirMode = 2
  FaceMakerClass = Part::FaceMakerBullseye
  LengthFwd = 2.4
  LengthRev = 0
  Placement = pos=(90.7,29,6.77) rot=(0,-1,0;1.5708rad)
  Solid = true
  Symmetric = false
FEATURE [Sketcher::SketchObject] Sketch024
  FullyConstrained = true
  sketch-geometry (7):
    g0: LineSegment StartX=0 StartY=0 StartZ=0 EndX=0 EndY=6 EndZ=0
    g1: Circle CenterX=0 CenterY=0 CenterZ=0 NormalX=0 NormalY=0 NormalZ=1 AngleXU=0 Radius=1
    g2: Circle CenterX=8 CenterY=6 CenterZ=0 NormalX=0 NormalY=0 NormalZ=1 AngleXU=0 Radius=1
    g3: BSplineCurve PolesCount=3 KnotsCount=2 Degree=2 IsPeriodic=0
    g4: GeomPoint X=0 Y=0 Z=0
    g5: GeomPoint X=8 Y=6 Z=0
    g6: LineSegment StartX=0 StartY=6 StartZ=0 EndX=8 EndY=6 EndZ=0
  constraints (14):
    c: Coincident(g0,g-1)
    c: Distance(g0) = 6
    c: Vertical(g0)
    c: Coincident(g3,g0)
    c: Weight(g1) = 1
    c: Equal(g1,g2)
    c: InternalAlignment(g1,g3)
    c: InternalAlignment(g2,g3)
    c: InternalAlignment(g4,g3)
    c: InternalAlignment(g5,g3)
    c: Block(g3)
    c: Coincident(g6,g0)
    c: Coincident(g6,g3)
    c: Horizontal(g6)
FEATURE [Part::Extrusion] Extrude018  label="caseScrewPillarBracket006"
  Base = -> Sketch024
  Dir = (0,0,1)
  DirMode = 2
  FaceMakerClass = Part::FaceMakerBullseye
  LengthFwd = 2.4
  LengthRev = 0
  Placement = pos=(103.7,29,6.77) rot=(0,-1,0;1.5708rad)
  Solid = true
  Symmetric = false
FEATURE [Sketcher::SketchObject] Sketch025
  FullyConstrained = true
  sketch-geometry (7):
    g0: LineSegment StartX=0 StartY=0 StartZ=0 EndX=0 EndY=6 EndZ=0
    g1: Circle CenterX=0 CenterY=0 CenterZ=0 NormalX=0 NormalY=0 NormalZ=1 AngleXU=0 Radius=1
    g2: Circle CenterX=8 CenterY=6 CenterZ=0 NormalX=0 NormalY=0 NormalZ=1 AngleXU=0 Radius=1
    g3: BSplineCurve PolesCount=3 KnotsCount=2 Degree=2 IsPeriodic=0
    g4: GeomPoint X=0 Y=0 Z=0
    g5: GeomPoint X=8 Y=6 Z=0
    g6: LineSegment StartX=0 StartY=6 StartZ=0 EndX=8 EndY=6 EndZ=0
  constraints (14):
    c: Coincident(g0,g-1)
    c: Distance(g0) = 6
    c: Vertical(g0)
    c: Coincident(g3,g0)
    c: Weight(g1) = 1
    c: Equal(g1,g2)
    c: InternalAlignment(g1,g3)
    c: InternalAlignment(g2,g3)
    c: InternalAlignment(g4,g3)
    c: InternalAlignment(g5,g3)
    c: Block(g3)
    c: Coincident(g6,g0)
    c: Coincident(g6,g3)
    c: Horizontal(g6)
FEATURE [Part::Extrusion] Extrude019  label="caseScrewPillarBracket007"
  Base = -> Sketch025
  Dir = (0,0,1)
  DirMode = 2
  FaceMakerClass = Part::FaceMakerBullseye
  LengthFwd = 2.4
  LengthRev = 0
  Placement = pos=(101.3,29,65.23) rot=(0,1,0;1.5708rad)
  Solid = true
  Symmetric = false
FEATURE [Part::Box] Box011  label="frontCaseScrewPillarBracket"
  AttacherType = Attacher::AttachEngine3D
  Height = 2.4
  Length = 16
  Placement = pos=(87,28,2.3) rot=(0,0,1;0rad)
  Width = 7
FEATURE [Part::Box] Box012  label="frontCaseScrewPillarBracket001"
  AttacherType = Attacher::AttachEngine3D
  Height = 2.4
  Length = 16
  Placement = pos=(87,28,67.3) rot=(0,0,1;0rad)
  Width = 7
FEATURE [Sketcher::SketchObject] Sketch026
  FullyConstrained = true
  sketch-geometry (17):
    g0: Circle CenterX=-3.5 CenterY=23.5 CenterZ=0 NormalX=0 NormalY=0 NormalZ=1 AngleXU=0 Radius=1
    g1: Circle CenterX=-1 CenterY=15.25 CenterZ=0 NormalX=0 NormalY=0 NormalZ=1 AngleXU=0 Radius=1
    g2: Circle CenterX=-3.5 CenterY=7 CenterZ=0 NormalX=0 NormalY=0 NormalZ=1 AngleXU=0 Radius=1
    g3: BSplineCurve PolesCount=3 KnotsCount=2 Degree=2 IsPeriodic=0
    g4: GeomPoint X=-3.5 Y=23.5 Z=0
    g5: GeomPoint X=-3.5 Y=7 Z=0
    g6: Circle CenterX=-4.8 CenterY=30.5 CenterZ=0 NormalX=0 NormalY=0 NormalZ=1 AngleXU=0 Radius=1
    g7: Circle CenterX=-3.5 CenterY=30.5 CenterZ=0 NormalX=0 NormalY=0 NormalZ=1 AngleXU=0 Radius=1
    g8: Circle CenterX=-3.5 CenterY=29.2 CenterZ=0 NormalX=0 NormalY=0 NormalZ=1 AngleXU=0 Radius=1
    g9: BSplineCurve PolesCount=3 KnotsCount=2 Degree=2 IsPeriodic=0
    g10: GeomPoint X=-4.8 Y=30.5 Z=0
    g11: GeomPoint X=-3.5 Y=29.2 Z=0
    g12: LineSegment StartX=-3.5 StartY=29.2 StartZ=0 EndX=-3.5 EndY=23.5 EndZ=0
    g13: LineSegment StartX=-4.8 StartY=30.5 StartZ=0 EndX=0 EndY=30.5 EndZ=0
    g14: LineSegment StartX=-3.5 StartY=5 StartZ=0 EndX=-3.5 EndY=7 EndZ=0
    g15: LineSegment StartX=0 StartY=5 StartZ=0 EndX=0 EndY=30.5 EndZ=0
    g16: LineSegment StartX=-3.5 StartY=5 StartZ=0 EndX=0 EndY=5 EndZ=0
  constraints (33):
    c: Weight(g0) = 1
    c: Equal(g0,g1)
    c: Equal(g0,g2)
    c: InternalAlignment(g0,g3)
    c: InternalAlignment(g1,g3)
    c: InternalAlignment(g2,g3)
    c: InternalAlignment(g4,g3)
    c: InternalAlignment(g5,g3)
    c: Block(g3)
    c: Weight(g6) = 1
    c: Equal(g6,g7)
    c: Equal(g6,g8)
    c: InternalAlignment(g6,g9)
    c: InternalAlignment(g7,g9)
    c: InternalAlignment(g8,g9)
    c: InternalAlignment(g10,g9)
    c: InternalAlignment(g11,g9)
    c: Block(g9)
    c: Coincident(g12,g9)
    c: Coincident(g12,g3)
    c: Vertical(g12)
    c: Coincident(g13,g9)
    c: Horizontal(g13)
    c: Distance(g13) = 4.8
    c: Coincident(g14,g3)
    c: Vertical(g14)
    c: Coincident(g15,g13)
    c: Vertical(g15)
    c: Tangent(g15,g1)
    c: Distance(g14) = 2
    c: Coincident(g16,g14)
    c: Horizontal(g16)
    c: Coincident(g15,g16)
FEATURE [Part::Feature] Face050
  shape: bbox 4.8 x 25.5 x 2e-07 mm, 1 faces, 0 solids (baked)
FEATURE [Part::Revolution] Revolve054  label="moreFrontCaseScrewPost001"
  Angle = 360
  Axis = (0,1,0)
  Base = (0,0,0)
  FaceMakerClass = Part::FaceMakerBullseye
  Placement = pos=(102.5,4.5,3.5) rot=(0,0,1;0rad)
  Solid = false
  Source = -> Face050
  Symmetric = false
FEATURE [Part::Feature] Face051
  shape: bbox 4.8 x 25.5 x 2e-07 mm, 1 faces, 0 solids (baked)
FEATURE [Part::Revolution] Revolve055  label="moreFrontCaseScrewPost002"
  Angle = 360
  Axis = (0,1,0)
  Base = (0,0,0)
  FaceMakerClass = Part::FaceMakerBullseye
  Placement = pos=(102.5,4.5,68.5) rot=(0,0,1;0rad)
  Solid = false
  Source = -> Face051
  Symmetric = false
FEATURE [Sketcher::SketchObject] Sketch027
  FullyConstrained = true
  sketch-geometry (10):
    g0: LineSegment StartX=-1.6 StartY=4.7 StartZ=0 EndX=-1.6 EndY=1.7 EndZ=0
    g1: LineSegment StartX=-3.5 StartY=4.7 StartZ=0 EndX=-1.6 EndY=4.7 EndZ=0
    g2: LineSegment StartX=-1.6 StartY=1.7 StartZ=0 EndX=-1.6 EndY=1.5 EndZ=0
    g3: LineSegment StartX=-1.6 StartY=1.5 StartZ=0 EndX=-5.2 EndY=1.5 EndZ=0
    g4: Circle CenterX=-3.5 CenterY=4.7 CenterZ=0 NormalX=0 NormalY=0 NormalZ=1 AngleXU=0 Radius=1
    g5: Circle CenterX=-3.59627 CenterY=2.99743 CenterZ=0 NormalX=0 NormalY=0 NormalZ=1 AngleXU=0 Radius=1
    g6: Circle CenterX=-5.2 CenterY=1.5 CenterZ=0 NormalX=0 NormalY=0 NormalZ=1 AngleXU=0 Radius=1
    g7: BSplineCurve PolesCount=3 KnotsCount=2 Degree=2 IsPeriodic=0
    g8: GeomPoint X=-3.5 Y=4.7 Z=0
    g9: GeomPoint X=-5.2 Y=1.5 Z=0
  constraints (23):
    c: Vertical(g0)
    c: Distance(g0) = 3
    c: Coincident(g1,g0)
    c: Horizontal(g1)
    c: Block(g0)
    c: Block(g1)
    c: Coincident(g2,g0)
    c: Vertical(g2)
    c: Distance(g2) = 0.2
    c: Coincident(g3,g2)
    c: Horizontal(g3)
    c: Block(g3)
    c: Coincident(g7,g1)
    c: Weight(g4) = 1
    c: Equal(g4,g5)
    c: Equal(g4,g6)
    c: Coincident(g7,g3)
    c: InternalAlignment(g4,g7)
    c: InternalAlignment(g5,g7)
    c: InternalAlignment(g6,g7)
    c: InternalAlignment(g8,g7)
    c: InternalAlignment(g9,g7)
    c: Block(g7)
FEATURE [Sketcher::SketchObject] Sketch028
  FullyConstrained = true
  sketch-geometry (18):
    g0: LineSegment StartX=0 StartY=3e-16 StartZ=0 EndX=0 EndY=1.7 EndZ=0
    g1: LineSegment StartX=-3.5 StartY=0 StartZ=0 EndX=-3.5 EndY=0.9 EndZ=0
    g2: Circle CenterX=-2.7 CenterY=1.7 CenterZ=0 NormalX=0 NormalY=0 NormalZ=1 AngleXU=0 Radius=1
    g3: Circle CenterX=-3.5 CenterY=1.7 CenterZ=0 NormalX=0 NormalY=0 NormalZ=1 AngleXU=0 Radius=1
    g4: Circle CenterX=-3.5 CenterY=0.9 CenterZ=0 NormalX=0 NormalY=0 NormalZ=1 AngleXU=0 Radius=1
    g5: BSplineCurve PolesCount=3 KnotsCount=2 Degree=2 IsPeriodic=0
    g6: GeomPoint X=-2.7 Y=1.7 Z=0
    g7: GeomPoint X=-3.5 Y=0.9 Z=0
    g8: LineSegment StartX=-3.5 StartY=0 StartZ=0 EndX=-3.5 EndY=-7 EndZ=0
    g9: LineSegment StartX=0 StartY=3e-16 StartZ=0 EndX=0 EndY=-7 EndZ=0
    g10: LineSegment StartX=-3.5 StartY=-7 StartZ=0 EndX=0 EndY=-7 EndZ=0
    g11: LineSegment StartX=-2.7 StartY=1.7 StartZ=0 EndX=-1.6 EndY=1.7 EndZ=0
    g12: LineSegment StartX=0 StartY=1.7 StartZ=0 EndX=0 EndY=4.5 EndZ=0
    g13: LineSegment StartX=0 StartY=4.5 StartZ=0 EndX=0 EndY=10.8 EndZ=0
    g14: LineSegment StartX=0 StartY=10.8 StartZ=0 EndX=-2 EndY=10.8 EndZ=0
    g15: LineSegment StartX=-1.6 StartY=4.7 StartZ=0 EndX=-1.6 EndY=1.7 EndZ=0
    g16: LineSegment StartX=-1.6 StartY=4.7 StartZ=0 EndX=-2 EndY=4.7 EndZ=0
    g17: LineSegment StartX=-2 StartY=4.7 StartZ=0 EndX=-2 EndY=10.8 EndZ=0
  constraints (44):
    c: Vertical(g0)
    c: Vertical(g1)
    c: Distance(g1) = 0.9
    c: Block(g0)
    c: Distance(g0) = 1.7
    c: Weight(g2) = 1
    c: Equal(g2,g3)
    c: Equal(g2,g4)
    c: Coincident(g5,g1)
    c: InternalAlignment(g2,g5)
    c: InternalAlignment(g3,g5)
    c: InternalAlignment(g4,g5)
    c: InternalAlignment(g6,g5)
    c: InternalAlignment(g7,g5)
    c: Block(g5)
    c: Coincident(g8,g1)
    c: Vertical(g8)
    c: Distance(g8) = 7
    c: Vertical(g9)
    c: Equal(g8,g9) = 7
    c: Coincident(g9,g0)
    c: Coincident(g10,g8)
    c: Coincident(g10,g9)
    c: Horizontal(g10)
    c: Coincident(g11,g5)
    c: Horizontal(g11)
    c: Coincident(g12,g0)
    c: Vertical(g12)
    c: Distance(g12) = 2.8
    c: Coincident(g13,g12)
    c: Vertical(g13)
    c: Distance(g13) = 6.3
    c: Coincident(g14,g13)
    c: Horizontal(g14)
    c: Distance(g14) = 2
    c: Vertical(g15)
    c: Distance(g15) = 3
    c: Block(g11)
    c: Coincident(g15,g11)
    c: Coincident(g16,g15)
    c: Horizontal(g16)
    c: Coincident(g17,g16)
    c: Coincident(g17,g14)
    c: Vertical(g17)
FEATURE [Part::Revolution] Revolve040  label="backCaseScrewRetainer001"
  Angle = 360
  Axis = (0,1,0)
  Base = (0,0,0)
  FaceMakerClass = Part::FaceMakerBullseye
  Placement = pos=(12.5,3,10) rot=(0,0,1;0rad)
  Solid = false
  Source = -> Face036
  Symmetric = false
FEATURE [Part::Feature] Face055
  shape: bbox 3.5 x 30.2 x 2e-07 mm, 1 faces, 0 solids (baked)
FEATURE [Part::Revolution] Revolve059  label="backCaseScrewPost"
  Angle = 360
  Axis = (0,1,0)
  Base = (0,0,0)
  FaceMakerClass = Part::FaceMakerBullseye
  Placement = pos=(12.5,4.5,10) rot=(0,0,1;0rad)
  Solid = false
  Source = -> Face055
  Symmetric = false
FEATURE [Part::Feature] Face056
  shape: bbox 3.5 x 30.2 x 2e-07 mm, 1 faces, 0 solids (baked)
FEATURE [Part::Revolution] Revolve060  label="backCaseScrewPost001"
  Angle = 360
  Axis = (0,1,0)
  Base = (0,0,0)
  FaceMakerClass = Part::FaceMakerBullseye
  Placement = pos=(12.5,4.5,62) rot=(0,0,1;0rad)
  Solid = false
  Source = -> Face056
  Symmetric = false
FEATURE [Part::Feature] Face057
  shape: bbox 3.5 x 17.8 x 2e-07 mm, 1 faces, 0 solids (baked)
FEATURE [Part::Revolution] Revolve061  label="removeToCreateScrewAndThreadedInsertHole"
  Angle = 360
  Axis = (0,1,0)
  Base = (0,0,0)
  FaceMakerClass = Part::FaceMakerBullseye
  Placement = pos=(12.5,0,10) rot=(0,0,1;0rad)
  Solid = false
  Source = -> Face057
  Symmetric = false
FEATURE [Part::Feature] Face058
  shape: bbox 3.5 x 17.8 x 2e-07 mm, 1 faces, 0 solids (baked)
FEATURE [Part::Revolution] Revolve062  label="removeToCreateScrewAndThreadedInsertHole001"
  Angle = 360
  Axis = (0,1,0)
  Base = (0,0,0)
  FaceMakerClass = Part::FaceMakerBullseye
  Placement = pos=(12.5,0,62) rot=(0,0,1;0rad)
  Solid = false
  Source = -> Face058
  Symmetric = false
FEATURE [Part::Feature] Face059
  shape: bbox 3.5 x 17.8 x 2e-07 mm, 1 faces, 0 solids (baked)
FEATURE [Part::Revolution] Revolve063  label="removeToCreateScrewAndThreadedInsertHole002"
  Angle = 360
  Axis = (0,1,0)
  Base = (0,0,0)
  FaceMakerClass = Part::FaceMakerBullseye
  Placement = pos=(89.5,0,68.5) rot=(0,0,1;0rad)
  Solid = false
  Source = -> Face059
  Symmetric = false
FEATURE [Part::Feature] Face060
  shape: bbox 3.5 x 17.8 x 2e-07 mm, 1 faces, 0 solids (baked)
FEATURE [Part::Revolution] Revolve064  label="removeToCreateScrewAndThreadedInsertHole003"
  Angle = 360
  Axis = (0,1,0)
  Base = (0,0,0)
  FaceMakerClass = Part::FaceMakerBullseye
  Placement = pos=(89.5,0,3.5) rot=(0,0,1;0rad)
  Solid = false
  Source = -> Face060
  Symmetric = false
FEATURE [Part::Feature] Face061
  shape: bbox 3.5 x 17.8 x 2e-07 mm, 1 faces, 0 solids (baked)
FEATURE [Part::Revolution] Revolve065  label="removeToCreateScrewAndThreadedInsertHole004"
  Angle = 360
  Axis = (0,1,0)
  Base = (0,0,0)
  FaceMakerClass = Part::FaceMakerBullseye
  Placement = pos=(102.5,4.7,3.5) rot=(0,0,1;0rad)
  Solid = false
  Source = -> Face061
  Symmetric = false
FEATURE [Part::Feature] Face062
  shape: bbox 3.5 x 17.8 x 2e-07 mm, 1 faces, 0 solids (baked)
FEATURE [Part::Revolution] Revolve066  label="removeToCreateScrewAndThreadedInsertHole005"
  Angle = 360
  Axis = (0,1,0)
  Base = (0,0,0)
  FaceMakerClass = Part::FaceMakerBullseye
  Placement = pos=(102.5,4.7,68.5) rot=(0,0,1;0rad)
  Solid = false
  Source = -> Face062
  Symmetric = false
FEATURE [Part::MultiFuse] Fusion047  label="makeHoles"
  Shapes = -> [Revolve066,Revolve065,Revolve064,Revolve063,Revolve062,Revolve061]
FEATURE [Part::Feature] Face063
  shape: bbox 3.6 x 3.2 x 2e-07 mm, 1 faces, 0 solids (baked)
FEATURE [Part::Revolution] Revolve067  label="moreFrontCaseScrewRetainer002"
  Angle = 360
  Axis = (0,1,0)
  Base = (0,0,0)
  FaceMakerClass = Part::FaceMakerBullseye
  Placement = pos=(102.5,4.5,68.5) rot=(0,0,1;0rad)
  Solid = false
  Source = -> Face063
  Symmetric = false
FEATURE [Part::Feature] Face064
  shape: bbox 3.6 x 3.2 x 2e-07 mm, 1 faces, 0 solids (baked)
FEATURE [Part::Revolution] Revolve068  label="moreFrontCaseScrewRetainer003"
  Angle = 360
  Axis = (0,1,0)
  Base = (0,0,0)
  FaceMakerClass = Part::FaceMakerBullseye
  Placement = pos=(102.5,4.5,3.5) rot=(0,0,1;0rad)
  Solid = false
  Source = -> Face064
  Symmetric = false
FEATURE [Part::Feature] Face065
  shape: bbox 3.5 x 17.8 x 2e-07 mm, 1 faces, 0 solids (baked)
FEATURE [Part::Revolution] Revolve069  label="removeToCreateScrewAndThreadedInsertHole006"
  Angle = 360
  Axis = (0,1,0)
  Base = (0,0,0)
  FaceMakerClass = Part::FaceMakerBullseye
  Placement = pos=(12.5,0,10) rot=(0,0,1;0rad)
  Solid = false
  Source = -> Face065
  Symmetric = false
FEATURE [Part::Feature] Face066
  shape: bbox 3.5 x 17.8 x 2e-07 mm, 1 faces, 0 solids (baked)
FEATURE [Part::Revolution] Revolve070  label="removeToCreateScrewAndThreadedInsertHole007"
  Angle = 360
  Axis = (0,1,0)
  Base = (0,0,0)
  FaceMakerClass = Part::FaceMakerBullseye
  Placement = pos=(12.5,0,62) rot=(0,0,1;0rad)
  Solid = false
  Source = -> Face066
  Symmetric = false
FEATURE [Part::Feature] Face067
  shape: bbox 3.5 x 17.8 x 2e-07 mm, 1 faces, 0 solids (baked)
FEATURE [Part::Revolution] Revolve071  label="removeToCreateScrewAndThreadedInsertHole008"
  Angle = 360
  Axis = (0,1,0)
  Base = (0,0,0)
  FaceMakerClass = Part::FaceMakerBullseye
  Placement = pos=(89.5,0,68.5) rot=(0,0,1;0rad)
  Solid = false
  Source = -> Face067
  Symmetric = false
FEATURE [Part::Feature] Face068
  shape: bbox 3.5 x 17.8 x 2e-07 mm, 1 faces, 0 solids (baked)
FEATURE [Part::Revolution] Revolve072  label="removeToCreateScrewAndThreadedInsertHole009"
  Angle = 360
  Axis = (0,1,0)
  Base = (0,0,0)
  FaceMakerClass = Part::FaceMakerBullseye
  Placement = pos=(89.5,0,3.5) rot=(0,0,1;0rad)
  Solid = false
  Source = -> Face068
  Symmetric = false
FEATURE [Part::Feature] Face069
  shape: bbox 3.5 x 17.8 x 2e-07 mm, 1 faces, 0 solids (baked)
FEATURE [Part::Feature] Face070
  shape: bbox 3.5 x 17.8 x 2e-07 mm, 1 faces, 0 solids (baked)
FEATURE [Part::Revolution] Revolve073  label="removeToCreateScrewAndThreadedInsertHole010"
  Angle = 360
  Axis = (0,1,0)
  Base = (0,0,0)
  FaceMakerClass = Part::FaceMakerBullseye
  Placement = pos=(102.5,4.7,3.5) rot=(0,0,1;0rad)
  Solid = false
  Source = -> Face069
  Symmetric = false
FEATURE [Part::Revolution] Revolve074  label="removeToCreateScrewAndThreadedInsertHole011"
  Angle = 360
  Axis = (0,1,0)
  Base = (0,0,0)
  FaceMakerClass = Part::FaceMakerBullseye
  Placement = pos=(102.5,4.7,68.5) rot=(0,0,1;0rad)
  Solid = false
  Source = -> Face070
  Symmetric = false
FEATURE [Part::MultiFuse] Fusion048  label="makeHoles001"
  Shapes = -> [Revolve074,Revolve073,Revolve072,Revolve071,Revolve070,Revolve069]
FEATURE [Part::MultiFuse] Fusion049  label="caseScrewRetainers"
  Shapes = -> [Revolve067,Revolve068,Revolve048,Revolve047,Revolve039,Revolve040]
FEATURE [Part::Cut] Cut015  label="caseScrewRetainers001"
  Base = -> Fusion049
  Tool = -> Fusion048
FEATURE [Part::MultiFuse] Fusion050  label="casePillars"
  Shapes = -> [Revolve055,Revolve054,Revolve043,Revolve046,Revolve059,Revolve060]
FEATURE [Part::Feature] Face071 .. Face076  x6 (patterned run collapsed; names and placements below)
  shape: bbox 3.5 x 17.8 x 2e-07 mm, 1 faces, 0 solids (baked)
FEATURE [Part::Revolution] Revolve075  label="removeToCreateScrewAndThreadedInsertHole012"
  Angle = 360
  Axis = (0,1,0)
  Base = (0,0,0)
  FaceMakerClass = Part::FaceMakerBullseye
  Placement = pos=(12.5,0,10) rot=(0,0,1;0rad)
  Solid = false
  Source = -> Face071
  Symmetric = false
FEATURE [Part::Revolution] Revolve076  label="removeToCreateScrewAndThreadedInsertHole013"
  Angle = 360
  Axis = (0,1,0)
  Base = (0,0,0)
  FaceMakerClass = Part::FaceMakerBullseye
  Placement = pos=(12.5,0,62) rot=(0,0,1;0rad)
  Solid = false
  Source = -> Face072
  Symmetric = false
FEATURE [Part::Revolution] Revolve077  label="removeToCreateScrewAndThreadedInsertHole014"
  Angle = 360
  Axis = (0,1,0)
  Base = (0,0,0)
  FaceMakerClass = Part::FaceMakerBullseye
  Placement = pos=(89.5,0,68.5) rot=(0,0,1;0rad)
  Solid = false
  Source = -> Face073
  Symmetric = false
FEATURE [Part::Revolution] Revolve078  label="removeToCreateScrewAndThreadedInsertHole015"
  Angle = 360
  Axis = (0,1,0)
  Base = (0,0,0)
  FaceMakerClass = Part::FaceMakerBullseye
  Placement = pos=(89.5,0,3.5) rot=(0,0,1;0rad)
  Solid = false
  Source = -> Face074
  Symmetric = false
FEATURE [Part::Revolution] Revolve079  label="removeToCreateScrewAndThreadedInsertHole016"
  Angle = 360
  Axis = (0,1,0)
  Base = (0,0,0)
  FaceMakerClass = Part::FaceMakerBullseye
  Placement = pos=(102.5,4.7,3.5) rot=(0,0,1;0rad)
  Solid = false
  Source = -> Face075
  Symmetric = false
FEATURE [Part::Revolution] Revolve080  label="removeToCreateScrewAndThreadedInsertHole017"
  Angle = 360
  Axis = (0,1,0)
  Base = (0,0,0)
  FaceMakerClass = Part::FaceMakerBullseye
  Placement = pos=(102.5,4.7,68.5) rot=(0,0,1;0rad)
  Solid = false
  Source = -> Face076
  Symmetric = false
FEATURE [Part::MultiFuse] Fusion051  label="makeHoles002"
  Shapes = -> [Revolve080,Revolve079,Revolve078,Revolve077,Revolve076,Revolve075]
FEATURE [Part::Cut] Cut016  label="caesPillars"
  Base = -> Fusion050
  Tool = -> Fusion051
FEATURE [Part::Revolution] Revolve009  label="plugHousing016"
  Angle = 360
  Axis = (0,1,0)
  Base = (0,0,0)
  FaceMakerClass = Part::FaceMakerBullseye
  Placement = pos=(0,0,36.15) rot=(0,0,1;0rad)
  Solid = false
  Source = -> Face012
  Symmetric = false
FEATURE [Part::MultiFuse] Fusion014  label="plugHousing023"
  Placement = pos=(0,0,0) rot=(0,0,1;1.5708rad)
  Shapes = -> [Revolve011,Revolve009]
FEATURE [Part::Revolution] Revolve010  label="plugHousing017"
  Angle = 360
  Axis = (0,1,0)
  Base = (0,0,0)
  FaceMakerClass = Part::FaceMakerBullseye
  Placement = pos=(0,0,36.15) rot=(0,0,1;0rad)
  Solid = false
  Source = -> Face014
  Symmetric = false
FEATURE [Part::MultiFuse] Fusion015  label="plugHousing024"
  Placement = pos=(0,0,0) rot=(0,0,1;1.5708rad)
  Shapes = -> [Revolve010,Revolve015]
FEATURE [Part::Revolution] Revolve014  label="plugHousing026"
  Angle = 360
  Axis = (0,1,0)
  Base = (0,0,0)
  FaceMakerClass = Part::FaceMakerBullseye
  Placement = pos=(0,0,36.15) rot=(0,0,1;0rad)
  Solid = false
  Source = -> Face011
  Symmetric = false
FEATURE [Part::Revolution] Revolve013  label="plugHousing025"
  Angle = 360
  Axis = (0,1,0)
  Base = (0,0,0)
  FaceMakerClass = Part::FaceMakerBullseye
  Placement = pos=(0,0,36.15) rot=(0,0,1;0rad)
  Solid = false
  Source = -> Face015
  Symmetric = false
FEATURE [Part::MultiFuse] Fusion016  label="plugHousing028"
  Placement = pos=(0,19,0) rot=(0,0,1;3.14159rad)
  Shapes = -> [Fusion014,Fusion013]
FEATURE [Part::MultiFuse] Fusion011  label="plugHousing018"
  Placement = pos=(0,0,0) rot=(0,0,1;1.5708rad)
  Shapes = -> [Revolve014,Revolve013]
FEATURE [Part::MultiFuse] Fusion012  label="plugHousing019"
  Placement = pos=(0,19,0) rot=(0,0,1;3.14159rad)
  Shapes = -> [Fusion011,Fusion015]
FEATURE [Part::MultiFuse] Fusion017  label="plugHousing029"
  Placement = pos=(122.621,0,-0.15) rot=(0,0,1;0rad)
  Shapes = -> [Fusion016,Fusion012]
FEATURE [Part::MultiFuse] Fusion052  label="casePillarRetainers"
  Shapes = -> [Extrude012,Extrude013,Extrude014,Extrude015,Extrude016,Extrude017,Extrude018,Extrude019,Box011,Box012]
FEATURE [Part::Feature] Face077
  shape: bbox 3.5 x 17.8 x 2e-07 mm, 1 faces, 0 solids (baked)
FEATURE [Part::Revolution] Revolve081  label="removeToCreateScrewAndThreadedInsertHole018"
  Angle = 360
  Axis = (0,1,0)
  Base = (0,0,0)
  FaceMakerClass = Part::FaceMakerBullseye
  Placement = pos=(62.3,30.3,19.7) rot=(0,0,1;0rad)
  Solid = false
  Source = -> Face077
  Symmetric = false
FEATURE [Part::Feature] Face078
  shape: bbox 3.5 x 17.8 x 2e-07 mm, 1 faces, 0 solids (baked)
FEATURE [Part::Revolution] Revolve082  label="removeToCreateScrewAndThreadedInsertHole019"
  Angle = 360
  Axis = (0,1,0)
  Base = (0,0,0)
  FaceMakerClass = Part::FaceMakerBullseye
  Placement = pos=(62.3,30.3,51.7) rot=(0,0,1;0rad)
  Solid = false
  Source = -> Face078
  Symmetric = false
FEATURE [Part::Feature] Face079
  shape: bbox 3.5 x 17.8 x 2e-07 mm, 1 faces, 0 solids (baked)
FEATURE [Part::Revolution] Revolve083  label="removeToCreateScrewAndThreadedInsertHole020"
  Angle = 360
  Axis = (0,1,0)
  Base = (0,0,0)
  FaceMakerClass = Part::FaceMakerBullseye
  Placement = pos=(30.3,30.3,19.7) rot=(0,0,1;0rad)
  Solid = false
  Source = -> Face079
  Symmetric = false
FEATURE [Part::Feature] Face080
  shape: bbox 3.5 x 17.8 x 2e-07 mm, 1 faces, 0 solids (baked)
FEATURE [Part::Revolution] Revolve084  label="removeToCreateScrewAndThreadedInsertHole021"
  Angle = 360
  Axis = (0,1,0)
  Base = (0,0,0)
  FaceMakerClass = Part::FaceMakerBullseye
  Placement = pos=(30.3,30.3,51.7) rot=(0,0,1;0rad)
  Solid = false
  Source = -> Face080
  Symmetric = false
FEATURE [Part::MultiFuse] Fusion053  label="createThreadedInsertHolesForFan"
  Shapes = -> [Revolve081,Revolve082,Revolve083,Revolve084]
FEATURE [Part::Cut] Cut017  label="fanScrewHousing001"
  Base = -> Fusion046
  Tool = -> Fusion053
FEATURE [Part::Feature] Face081
  shape: bbox 3.5 x 17.8 x 2e-07 mm, 1 faces, 0 solids (baked)
FEATURE [Part::Revolution] Revolve085  label="removeToCreateScrewAndThreadedInsertHole022"
  Angle = 360
  Axis = (0,1,0)
  Base = (0,0,0)
  FaceMakerClass = Part::FaceMakerBullseye
  Placement = pos=(62.3,30.3,19.7) rot=(0,0,1;0rad)
  Solid = false
  Source = -> Face081
  Symmetric = false
FEATURE [Part::Feature] Face082
  shape: bbox 3.5 x 17.8 x 2e-07 mm, 1 faces, 0 solids (baked)
FEATURE [Part::Revolution] Revolve086  label="removeToCreateScrewAndThreadedInsertHole023"
  Angle = 360
  Axis = (0,1,0)
  Base = (0,0,0)
  FaceMakerClass = Part::FaceMakerBullseye
  Placement = pos=(62.3,30.3,51.7) rot=(0,0,1;0rad)
  Solid = false
  Source = -> Face082
  Symmetric = false
FEATURE [Part::Feature] Face083
  shape: bbox 3.5 x 17.8 x 2e-07 mm, 1 faces, 0 solids (baked)
FEATURE [Part::Revolution] Revolve087  label="removeToCreateScrewAndThreadedInsertHole024"
  Angle = 360
  Axis = (0,1,0)
  Base = (0,0,0)
  FaceMakerClass = Part::FaceMakerBullseye
  Placement = pos=(30.3,30.3,19.7) rot=(0,0,1;0rad)
  Solid = false
  Source = -> Face083
  Symmetric = false
FEATURE [Part::Feature] Face084
  shape: bbox 3.5 x 17.8 x 2e-07 mm, 1 faces, 0 solids (baked)
FEATURE [Part::Revolution] Revolve088  label="removeToCreateScrewAndThreadedInsertHole025"
  Angle = 360
  Axis = (0,1,0)
  Base = (0,0,0)
  FaceMakerClass = Part::FaceMakerBullseye
  Placement = pos=(30.3,30.3,51.7) rot=(0,0,1;0rad)
  Solid = false
  Source = -> Face084
  Symmetric = false
FEATURE [Part::MultiFuse] Fusion054  label="createThreadedInsertHolesForFan001"
  Shapes = -> [Revolve085,Revolve086,Revolve087,Revolve088]
FEATURE [Part::Cut] Cut018  label="top007"
  Base = -> Fusion040
  Tool = -> Fusion054
FEATURE [Sketcher::SketchObject] Sketch029
  FullyConstrained = false
  Placement = pos=(0,0,0) rot=(1,0,0;1.5708rad)
  sketch-geometry (24):
    g0: ArcOfCircle CenterX=-4 CenterY=-10.5 CenterZ=0 NormalX=0 NormalY=0 NormalZ=1 AngleXU=0 Radius=1.5 StartAngle=6e-16 EndAngle=3.14159
    g1: ArcOfCircle CenterX=-34.2 CenterY=-10.5 CenterZ=0 NormalX=0 NormalY=0 NormalZ=1 AngleXU=0 Radius=1.5 StartAngle=0 EndAngle=3.14159
    g2: ArcOfCircle CenterX=-34.2 CenterY=-27.7 CenterZ=0 NormalX=0 NormalY=0 NormalZ=1 AngleXU=0 Radius=1.5 StartAngle=3.14159 EndAngle=6.28319
    g3: ArcOfCircle CenterX=-4 CenterY=-27.7 CenterZ=0 NormalX=0 NormalY=0 NormalZ=1 AngleXU=0 Radius=1.5 StartAngle=3.1416 EndAngle=6.28319
    g4: ArcOfCircle CenterX=-10 CenterY=-4.3 CenterZ=0 NormalX=0 NormalY=0 NormalZ=1 AngleXU=0 Radius=1.5 StartAngle=2e-16 EndAngle=3.14159
    g5: ArcOfCircle CenterX=-16.1 CenterY=-1.8 CenterZ=0 NormalX=0 NormalY=0 NormalZ=1 AngleXU=0 Radius=1.5 StartAngle=5e-16 EndAngle=3.14159
    g6: ArcOfCircle CenterX=-22.1 CenterY=-1.8 CenterZ=0 NormalX=0 NormalY=0 NormalZ=1 AngleXU=0 Radius=1.5 StartAngle=5e-16 EndAngle=3.14159
    g7: ArcOfCircle CenterX=-28.2 CenterY=-4.3 CenterZ=0 NormalX=0 NormalY=0 NormalZ=1 AngleXU=0 Radius=1.5 StartAngle=2e-16 EndAngle=3.14159
    g8: ArcOfCircle CenterX=-10 CenterY=-33.9 CenterZ=0 NormalX=0 NormalY=0 NormalZ=1 AngleXU=0 Radius=1.5 StartAngle=3.14159 EndAngle=6.28319
    g9: ArcOfCircle CenterX=-16.1 CenterY=-36.4 CenterZ=0 NormalX=0 NormalY=0 NormalZ=1 AngleXU=0 Radius=1.5 StartAngle=3.14159 EndAngle=6.28319
    g10: ArcOfCircle CenterX=-22.1 CenterY=-36.4 CenterZ=0 NormalX=0 NormalY=0 NormalZ=1 AngleXU=0 Radius=1.5 StartAngle=3.14159 EndAngle=6.28319
    g11: ArcOfCircle CenterX=-28.2 CenterY=-33.9 CenterZ=0 NormalX=0 NormalY=0 NormalZ=1 AngleXU=0 Radius=1.5 StartAngle=3.14159 EndAngle=6.28319
    g12: LineSegment StartX=-35.7 StartY=-10.5 StartZ=0 EndX=-35.7 EndY=-27.7 EndZ=0
    g13: LineSegment StartX=-32.7 StartY=-10.5 StartZ=0 EndX=-32.7 EndY=-27.7 EndZ=0
    g14: LineSegment StartX=-29.7 StartY=-33.9 StartZ=0 EndX=-29.7 EndY=-4.3 EndZ=0
    g15: LineSegment StartX=-26.7 StartY=-33.9 StartZ=0 EndX=-26.7 EndY=-4.3 EndZ=0
    g16: LineSegment StartX=-2.5 StartY=-10.5 StartZ=0 EndX=-2.5 EndY=-27.7 EndZ=0
    g17: LineSegment StartX=-8.5 StartY=-4.3 StartZ=0 EndX=-8.5 EndY=-33.9 EndZ=0
    g18: LineSegment StartX=-5.5 StartY=-10.5 StartZ=0 EndX=-5.5 EndY=-27.7 EndZ=0
    g19: LineSegment StartX=-11.5 StartY=-4.3 StartZ=0 EndX=-11.5 EndY=-33.9 EndZ=0
    g20: LineSegment StartX=-14.6 StartY=-1.8 StartZ=0 EndX=-14.6 EndY=-36.4 EndZ=0
    g21: LineSegment StartX=-17.6 StartY=-1.8 StartZ=0 EndX=-17.6 EndY=-36.4 EndZ=0
    g22: LineSegment StartX=-20.6 StartY=-36.4 StartZ=0 EndX=-20.6 EndY=-1.8 EndZ=0
    g23: LineSegment StartX=-23.6 StartY=-1.8 StartZ=0 EndX=-23.6 EndY=-36.4 EndZ=0
  constraints (48):
    c: Block(g0)
    c: Block(g1)
    c: Block(g2)
    c: Block(g3)
    c: Block(g4)
    c: Block(g5)
    c: Block(g6)
    c: Block(g7)
    c: Block(g8)
    c: Block(g9)
    c: Block(g10)
    c: Block(g11)
    c: Coincident(g12,g1)
    c: Coincident(g12,g2)
    c: Vertical(g12)
    c: Coincident(g13,g1)
    c: Coincident(g13,g2)
    c: Vertical(g13)
    c: Coincident(g14,g11)
    c: Coincident(g14,g7)
    c: Vertical(g14)
    c: Coincident(g15,g11)
    c: Coincident(g15,g7)
    c: Vertical(g15)
    c: Coincident(g16,g0)
    c: Coincident(g16,g3)
    c: Vertical(g16)
    c: Coincident(g17,g4)
    c: Coincident(g17,g8)
    c: Vertical(g17)
    c: Coincident(g18,g0)
    c: Coincident(g18,g3)
    c: Vertical(g18)
    c: Coincident(g19,g4)
    c: Coincident(g19,g8)
    c: Vertical(g19)
    c: Coincident(g20,g5)
    c: Coincident(g20,g9)
    c: Vertical(g20)
    c: Coincident(g21,g5)
    c: Coincident(g21,g9)
    c: Vertical(g21)
    c: Coincident(g22,g10)
    c: Coincident(g22,g6)
    c: Vertical(g22)
    c: Coincident(g23,g6)
    c: Coincident(g23,g10)
    c: Vertical(g23)
FEATURE [Part::Extrusion] Extrude020  label="removeToCreateFanGrillHoles"
  Base = -> Sketch029
  Dir = (0,-1,6e-16)
  DirMode = 2
  FaceMakerClass = Part::FaceMakerBullseye
  LengthFwd = 10
  LengthRev = 0
  Placement = pos=(65.4,44,54.82) rot=(0,0,1;0rad)
  Solid = true
  Symmetric = false
FEATURE [Part::MultiFuse] Fusion055  label="top008"
  Shapes = -> [Cut017,Cut018]
FEATURE [Part::Cut] Cut019  label="top009"
  Base = -> Fusion055
  Tool = -> Extrude020
FEATURE [App::MeasureDistance] Distance003  label="Distance: 71.95 mm"
  Distance = 71.9513
  P1 = (117,38,72)
  P2 = (117,38,0.0487319)
FEATURE [Sketcher::SketchObject] Sketch030
  FullyConstrained = true
  Placement = pos=(117,19,0) rot=(0.57735,0.57735,0.57735;2.0944rad)
  sketch-geometry (48):
    g0: LineSegment StartX=-49.19 StartY=69.25 StartZ=0 EndX=-49.19 EndY=66.25 EndZ=0
    g1: LineSegment StartX=-49.19 StartY=63.5 StartZ=0 EndX=-49.19 EndY=60.5 EndZ=0
    g2: LineSegment StartX=-49.19 StartY=57.75 StartZ=0 EndX=-49.19 EndY=54.75 EndZ=0
    g3: LineSegment StartX=-49.19 StartY=52 StartZ=0 EndX=-49.19 EndY=49 EndZ=0
    g4: LineSegment StartX=-49.19 StartY=46.25 StartZ=0 EndX=-49.19 EndY=43.25 EndZ=0
    g5: LineSegment StartX=-49.19 StartY=40.5 StartZ=0 EndX=-49.19 EndY=37.5 EndZ=0
    g6: LineSegment StartX=-49.19 StartY=34.5 StartZ=0 EndX=-49.19 EndY=31.5 EndZ=0
    g7: LineSegment StartX=-49.19 StartY=28.75 StartZ=0 EndX=-49.19 EndY=25.75 EndZ=0
    g8: LineSegment StartX=-49.19 StartY=23 StartZ=0 EndX=-49.19 EndY=20 EndZ=0
    g9: LineSegment StartX=-49.19 StartY=17.25 StartZ=0 EndX=-49.19 EndY=14.25 EndZ=0
    g10: LineSegment StartX=-49.19 StartY=11.5 StartZ=0 EndX=-49.19 EndY=8.5 EndZ=0
    g11: LineSegment StartX=-49.19 StartY=5.75 StartZ=0 EndX=-49.19 EndY=2.75 EndZ=0
    g12: ArcOfCircle CenterX=-1.5 CenterY=67.75 CenterZ=0 NormalX=0 NormalY=0 NormalZ=1 AngleXU=0 Radius=1.5 StartAngle=4.71239 EndAngle=7.85398
    g13: ArcOfCircle CenterX=-1.5 CenterY=62 CenterZ=0 NormalX=0 NormalY=0 NormalZ=1 AngleXU=0 Radius=1.5 StartAngle=4.71239 EndAngle=7.85398
    g14: ArcOfCircle CenterX=-1.5 CenterY=56.25 CenterZ=0 NormalX=0 NormalY=0 NormalZ=1 AngleXU=0 Radius=1.5 StartAngle=4.71239 EndAngle=7.85398
    g15: ArcOfCircle CenterX=-11.49 CenterY=50.5 CenterZ=0 NormalX=0 NormalY=0 NormalZ=1 AngleXU=0 Radius=1.5 StartAngle=4.71239 EndAngle=7.85398
    g16: ArcOfCircle CenterX=-16.28 CenterY=44.75 CenterZ=0 NormalX=0 NormalY=0 NormalZ=1 AngleXU=0 Radius=1.5 StartAngle=4.71239 EndAngle=7.85398
    g17: ArcOfCircle CenterX=-18.2337 CenterY=39 CenterZ=0 NormalX=0 NormalY=0 NormalZ=1 AngleXU=0 Radius=1.5 StartAngle=4.71485 EndAngle=7.85398
    g18: ArcOfCircle CenterX=-16.2837 CenterY=27.25 CenterZ=0 NormalX=0 NormalY=0 NormalZ=1 AngleXU=0 Radius=1.5 StartAngle=4.71485 EndAngle=7.85398
    g19: ArcOfCircle CenterX=-18.2337 CenterY=33 CenterZ=0 NormalX=0 NormalY=0 NormalZ=1 AngleXU=0 Radius=1.5 StartAngle=4.71485 EndAngle=7.85398
    g20: ArcOfCircle CenterX=-11.49 CenterY=21.5 CenterZ=0 NormalX=0 NormalY=0 NormalZ=1 AngleXU=0 Radius=1.5 StartAngle=4.71239 EndAngle=7.85398
    g21: ArcOfCircle CenterX=-1.5 CenterY=4.25 CenterZ=0 NormalX=0 NormalY=0 NormalZ=1 AngleXU=0 Radius=1.5 StartAngle=4.71239 EndAngle=7.85398
    g22: ArcOfCircle CenterX=-1.5 CenterY=10 CenterZ=0 NormalX=0 NormalY=0 NormalZ=1 AngleXU=0 Radius=1.5 StartAngle=4.71239 EndAngle=7.85398
    g23: ArcOfCircle CenterX=-1.5 CenterY=15.75 CenterZ=0 NormalX=0 NormalY=0 NormalZ=1 AngleXU=0 Radius=1.5 StartAngle=4.71239 EndAngle=7.85398
    g24: LineSegment StartX=-49.19 StartY=69.25 StartZ=0 EndX=-1.5 EndY=69.25 EndZ=0
    g25: LineSegment StartX=-49.19 StartY=66.25 StartZ=0 EndX=-1.5 EndY=66.25 EndZ=0
    g26: LineSegment StartX=-49.19 StartY=63.5 StartZ=0 EndX=-1.5 EndY=63.5 EndZ=0
    g27: LineSegment StartX=-49.19 StartY=60.5 StartZ=0 EndX=-1.5 EndY=60.5 EndZ=0
    g28: LineSegment StartX=-49.19 StartY=57.75 StartZ=0 EndX=-1.5 EndY=57.75 EndZ=0
    g29: LineSegment StartX=-49.19 StartY=54.75 StartZ=0 EndX=-1.5 EndY=54.75 EndZ=0
    g30: LineSegment StartX=-49.19 StartY=52 StartZ=0 EndX=-11.49 EndY=52 EndZ=0
    g31: LineSegment StartX=-49.19 StartY=49 StartZ=0 EndX=-11.49 EndY=49 EndZ=0
    g32: LineSegment StartX=-49.19 StartY=46.25 StartZ=0 EndX=-16.28 EndY=46.25 EndZ=0
    g33: LineSegment StartX=-49.19 StartY=43.25 StartZ=0 EndX=-16.28 EndY=43.25 EndZ=0
    g34: LineSegment StartX=-49.19 StartY=40.5 StartZ=0 EndX=-18.2337 EndY=40.5 EndZ=0
    g35: LineSegment StartX=-49.19 StartY=37.5 StartZ=0 EndX=-18.23 EndY=37.5 EndZ=0
    g36: LineSegment StartX=-49.19 StartY=34.5 StartZ=0 EndX=-18.2337 EndY=34.5 EndZ=0
    g37: LineSegment StartX=-49.19 StartY=31.5 StartZ=0 EndX=-18.23 EndY=31.5 EndZ=0
    g38: LineSegment StartX=-49.19 StartY=28.75 StartZ=0 EndX=-16.2837 EndY=28.75 EndZ=0
    g39: LineSegment StartX=-49.19 StartY=25.75 StartZ=0 EndX=-16.28 EndY=25.75 EndZ=0
    g40: LineSegment StartX=-49.19 StartY=23 StartZ=0 EndX=-11.49 EndY=23 EndZ=0
    g41: LineSegment StartX=-49.19 StartY=20 StartZ=0 EndX=-11.49 EndY=20 EndZ=0
    g42: LineSegment StartX=-49.19 StartY=17.25 StartZ=0 EndX=-1.5 EndY=17.25 EndZ=0
    g43: LineSegment StartX=-49.19 StartY=14.25 StartZ=0 EndX=-1.5 EndY=14.25 EndZ=0
    g44: LineSegment StartX=-49.19 StartY=11.5 StartZ=0 EndX=-1.5 EndY=11.5 EndZ=0
    g45: LineSegment StartX=-49.19 StartY=8.5 StartZ=0 EndX=-1.5 EndY=8.5 EndZ=0
    g46: LineSegment StartX=-49.19 StartY=5.75 StartZ=0 EndX=-1.5 EndY=5.75 EndZ=0
    g47: LineSegment StartX=-49.19 StartY=2.75 StartZ=0 EndX=-1.5 EndY=2.75 EndZ=0
  constraints (120):
    c: Vertical(g0)
    c: Distance(g0) = 3
    c: Block(g0)
    c: Vertical(g1)
    c: Distance(g1) = 3
    c: Vertical(g2)
    c: Equal(g0,g2) = 3
    c: Block(g2)
    c: Vertical(g3)
    c: Equal(g1,g3) = 3
    c: Vertical(g4)
    c: Equal(g0,g4) = 3
    c: Block(g4)
    c: Vertical(g5)
    c: Equal(g1,g5) = 3
    c: Vertical(g6)
    c: Equal(g0,g6) = 3
    c: Block(g6)
    c: Vertical(g7)
    c: Equal(g1,g7) = 3
    c: Vertical(g8)
    c: Equal(g0,g8) = 3
    c: Block(g8)
    c: Vertical(g9)
    c: Equal(g1,g9) = 3
    c: Vertical(g10)
    c: Equal(g0,g10) = 3
    c: Block(g10)
    c: Vertical(g11)
    c: Equal(g1,g11) = 3
    c: Block(g12)
    c: Block(g13)
    c: Block(g14)
    c: Block(g15)
    c: Block(g16)
    c: Block(g17)
    c: Block(g18)
    c: Block(g19)
    c: Block(g20)
    c: Block(g21)
    c: Block(g22)
    c: Block(g23)
    c: Block(g11)
    c: Block(g9)
    c: Block(g7)
    c: Block(g5)
    c: Block(g3)
    c: Block(g1)
    c: Coincident(g24,g0)
    c: Coincident(g24,g12)
    c: Horizontal(g24)
    c: Coincident(g25,g0)
    c: Coincident(g25,g12)
    c: Horizontal(g25)
    c: Coincident(g26,g1)
    c: Coincident(g26,g13)
    c: Horizontal(g26)
    c: Coincident(g27,g1)
    c: Coincident(g27,g13)
    c: Horizontal(g27)
    c: Coincident(g28,g2)
    c: Coincident(g28,g14)
    c: Horizontal(g28)
    c: Coincident(g29,g2)
    c: Coincident(g29,g14)
    c: Horizontal(g29)
    c: Coincident(g30,g3)
    c: Coincident(g30,g15)
    c: Horizontal(g30)
    c: Coincident(g31,g3)
    c: Coincident(g31,g15)
    c: Horizontal(g31)
    c: Coincident(g32,g4)
    c: Coincident(g32,g16)
    c: Horizontal(g32)
    c: Coincident(g33,g4)
    c: Coincident(g33,g16)
    c: Horizontal(g33)
    c: Coincident(g34,g5)
    c: Coincident(g34,g17)
    c: Horizontal(g34)
    c: Coincident(g35,g5)
    c: Coincident(g35,g17)
    c: Horizontal(g35)
    c: Coincident(g36,g6)
    c: Coincident(g36,g19)
    c: Horizontal(g36)
    c: Coincident(g37,g6)
    c: Coincident(g37,g19)
    c: Horizontal(g37)
    c: Coincident(g38,g7)
    c: Coincident(g38,g18)
    c: Horizontal(g38)
    c: Coincident(g39,g7)
    c: Coincident(g39,g18)
    c: Horizontal(g39)
    c: Coincident(g40,g8)
    c: Coincident(g40,g20)
    c: Horizontal(g40)
    c: Coincident(g41,g8)
    c: Coincident(g41,g20)
    c: Horizontal(g41)
    c: Coincident(g42,g9)
    c: Coincident(g42,g23)
    c: Horizontal(g42)
    c: Coincident(g43,g9)
    c: Coincident(g43,g23)
    c: Horizontal(g43)
    c: Coincident(g44,g10)
    c: Coincident(g44,g22)
    c: Horizontal(g44)
    c: Coincident(g45,g10)
    c: Coincident(g45,g22)
    c: Horizontal(g45)
    c: Coincident(g46,g11)
    c: Coincident(g46,g21)
    c: Horizontal(g46)
    c: Coincident(g47,g11)
    c: Coincident(g47,g21)
    c: Horizontal(g47)
FEATURE [Sketcher::SketchObject] Sketch031
  FullyConstrained = true
  Placement = pos=(117,19,0) rot=(0.57735,0.57735,0.57735;2.0944rad)
  sketch-geometry (24):
    g0: ArcOfCircle CenterX=-49.19 CenterY=67.75 CenterZ=0 NormalX=0 NormalY=0 NormalZ=1 AngleXU=0 Radius=1.5 StartAngle=1.5708 EndAngle=4.71239
    g1: ArcOfCircle CenterX=-49.19 CenterY=62 CenterZ=0 NormalX=0 NormalY=0 NormalZ=1 AngleXU=0 Radius=1.5 StartAngle=1.5708 EndAngle=4.71239
    g2: ArcOfCircle CenterX=-49.19 CenterY=56.25 CenterZ=0 NormalX=0 NormalY=0 NormalZ=1 AngleXU=0 Radius=1.5 StartAngle=1.5708 EndAngle=4.71239
    g3: ArcOfCircle CenterX=-49.19 CenterY=50.5 CenterZ=0 NormalX=0 NormalY=0 NormalZ=1 AngleXU=0 Radius=1.5 StartAngle=1.5708 EndAngle=4.71239
    g4: ArcOfCircle CenterX=-49.19 CenterY=44.75 CenterZ=0 NormalX=0 NormalY=0 NormalZ=1 AngleXU=0 Radius=1.5 StartAngle=1.5708 EndAngle=4.71239
    g5: ArcOfCircle CenterX=-49.19 CenterY=39 CenterZ=0 NormalX=0 NormalY=0 NormalZ=1 AngleXU=0 Radius=1.5 StartAngle=1.5708 EndAngle=4.71239
    g6: ArcOfCircle CenterX=-49.19 CenterY=33 CenterZ=0 NormalX=0 NormalY=0 NormalZ=1 AngleXU=0 Radius=1.5 StartAngle=1.5708 EndAngle=4.71239
    g7: ArcOfCircle CenterX=-49.19 CenterY=27.25 CenterZ=0 NormalX=0 NormalY=0 NormalZ=1 AngleXU=0 Radius=1.5 StartAngle=1.5708 EndAngle=4.71239
    g8: ArcOfCircle CenterX=-49.19 CenterY=21.5 CenterZ=0 NormalX=0 NormalY=0 NormalZ=1 AngleXU=0 Radius=1.5 StartAngle=1.5708 EndAngle=4.71239
    g9: ArcOfCircle CenterX=-49.19 CenterY=15.75 CenterZ=0 NormalX=0 NormalY=0 NormalZ=1 AngleXU=0 Radius=1.5 StartAngle=1.5708 EndAngle=4.71239
    g10: ArcOfCircle CenterX=-49.19 CenterY=10 CenterZ=0 NormalX=0 NormalY=0 NormalZ=1 AngleXU=0 Radius=1.5 StartAngle=1.5708 EndAngle=4.71239
    g11: ArcOfCircle CenterX=-49.19 CenterY=4.25 CenterZ=0 NormalX=0 NormalY=0 NormalZ=1 AngleXU=0 Radius=1.5 StartAngle=1.5708 EndAngle=4.71239
    g12: LineSegment StartX=-49.19 StartY=69.25 StartZ=0 EndX=-49.19 EndY=66.25 EndZ=0
    g13: LineSegment StartX=-49.19 StartY=63.5 StartZ=0 EndX=-49.19 EndY=60.5 EndZ=0
    g14: LineSegment StartX=-49.19 StartY=57.75 StartZ=0 EndX=-49.19 EndY=54.75 EndZ=0
    g15: LineSegment StartX=-49.19 StartY=52 StartZ=0 EndX=-49.19 EndY=49 EndZ=0
    g16: LineSegment StartX=-49.19 StartY=46.25 StartZ=0 EndX=-49.19 EndY=43.25 EndZ=0
    g17: LineSegment StartX=-49.19 StartY=40.5 StartZ=0 EndX=-49.19 EndY=37.5 EndZ=0
    g18: LineSegment StartX=-49.19 StartY=34.5 StartZ=0 EndX=-49.19 EndY=31.5 EndZ=0
    g19: LineSegment StartX=-49.19 StartY=28.75 StartZ=0 EndX=-49.19 EndY=25.75 EndZ=0
    g20: LineSegment StartX=-49.19 StartY=23 StartZ=0 EndX=-49.19 EndY=20 EndZ=0
    g21: LineSegment StartX=-49.19 StartY=17.25 StartZ=0 EndX=-49.19 EndY=14.25 EndZ=0
    g22: LineSegment StartX=-49.19 StartY=11.5 StartZ=0 EndX=-49.19 EndY=8.5 EndZ=0
    g23: LineSegment StartX=-49.19 StartY=5.75 StartZ=0 EndX=-49.19 EndY=2.75 EndZ=0
  constraints (48):
    c: Block(g0)
    c: Block(g1)
    c: Block(g2)
    c: Block(g3)
    c: Block(g4)
    c: Block(g5)
    c: Block(g6)
    c: Block(g7)
    c: Block(g8)
    c: Block(g9)
    c: Block(g10)
    c: Block(g11)
    c: Coincident(g12,g0)
    c: Coincident(g12,g0)
    c: Vertical(g12)
    c: Vertical(g13)
    c: Coincident(g13,g1)
    c: Vertical(g14)
    c: Coincident(g14,g2)
    c: Vertical(g15)
    c: Coincident(g15,g3)
    c: Vertical(g16)
    c: Coincident(g16,g4)
    c: Vertical(g17)
    c: Coincident(g17,g5)
    c: Vertical(g18)
    c: Coincident(g18,g6)
    c: Vertical(g19)
    c: Coincident(g19,g7)
    c: Vertical(g20)
    c: Coincident(g20,g8)
    c: Vertical(g21)
    c: Coincident(g21,g9)
    c: Vertical(g22)
    c: Coincident(g22,g10)
    c: Vertical(g23)
    c: Coincident(g23,g11)
    c: Block(g23)
    c: Block(g22)
    c: Block(g21)
    c: Block(g20)
    c: Block(g13)
    c: Block(g14)
    c: Block(g15)
    c: Block(g16)
    c: Block(g17)
    c: Block(g18)
    c: Block(g19)
FEATURE [Part::Extrusion] Extrude022
  Base = -> Sketch030
  Dir = (1,-2e-16,2e-16)
  DirMode = 2
  FaceMakerClass = Part::FaceMakerBullseye
  LengthFwd = 19
  LengthRev = 0
  Placement = pos=(-19,0,0) rot=(0,0,1;0rad)
  Solid = true
  Symmetric = false
FEATURE [Part::Fillet] Fillet022
  Base = -> Extrude022
  Edges = 24 edges r=1.49: [Edge6,Edge11,Edge18,Edge23,Edge30,Edge35,Edge42,Edge47,Edge54,Edge59,Edge66,Edge71,Edge78,Edge83,Edge90,Edge95,Edge102,Edge107,Edge114,Edge119,Edge126,Edge131,Edge138,Edge143]
FEATURE [Part::Cut] Cut020  label="top010"
  Base = -> Cut019
  Tool = -> Fillet022
FEATURE [Sketcher::SketchObject] Sketch032
  FullyConstrained = true
  Placement = pos=(117,19,0) rot=(0.57735,0.57735,0.57735;2.0944rad)
  sketch-geometry (48):
    g0: LineSegment StartX=-49.19 StartY=69.25 StartZ=0 EndX=-49.19 EndY=66.25 EndZ=0
    g1: LineSegment StartX=-49.19 StartY=63.5 StartZ=0 EndX=-49.19 EndY=60.5 EndZ=0
    g2: LineSegment StartX=-49.19 StartY=57.75 StartZ=0 EndX=-49.19 EndY=54.75 EndZ=0
    g3: LineSegment StartX=-49.19 StartY=52 StartZ=0 EndX=-49.19 EndY=49 EndZ=0
    g4: LineSegment StartX=-49.19 StartY=46.25 StartZ=0 EndX=-49.19 EndY=43.25 EndZ=0
    g5: LineSegment StartX=-49.19 StartY=40.5 StartZ=0 EndX=-49.19 EndY=37.5 EndZ=0
    g6: LineSegment StartX=-49.19 StartY=34.5 StartZ=0 EndX=-49.19 EndY=31.5 EndZ=0
    g7: LineSegment StartX=-49.19 StartY=28.75 StartZ=0 EndX=-49.19 EndY=25.75 EndZ=0
    g8: LineSegment StartX=-49.19 StartY=23 StartZ=0 EndX=-49.19 EndY=20 EndZ=0
    g9: LineSegment StartX=-49.19 StartY=17.25 StartZ=0 EndX=-49.19 EndY=14.25 EndZ=0
    g10: LineSegment StartX=-49.19 StartY=11.5 StartZ=0 EndX=-49.19 EndY=8.5 EndZ=0
    g11: LineSegment StartX=-49.19 StartY=5.75 StartZ=0 EndX=-49.19 EndY=2.75 EndZ=0
    g12: ArcOfCircle CenterX=-1.5 CenterY=67.75 CenterZ=0 NormalX=0 NormalY=0 NormalZ=1 AngleXU=0 Radius=1.5 StartAngle=4.71239 EndAngle=7.85398
    g13: ArcOfCircle CenterX=-1.5 CenterY=62 CenterZ=0 NormalX=0 NormalY=0 NormalZ=1 AngleXU=0 Radius=1.5 StartAngle=4.71239 EndAngle=7.85398
    g14: ArcOfCircle CenterX=-1.5 CenterY=56.25 CenterZ=0 NormalX=0 NormalY=0 NormalZ=1 AngleXU=0 Radius=1.5 StartAngle=4.71239 EndAngle=7.85398
    g15: ArcOfCircle CenterX=-11.49 CenterY=50.5 CenterZ=0 NormalX=0 NormalY=0 NormalZ=1 AngleXU=0 Radius=1.5 StartAngle=4.71239 EndAngle=7.85398
    g16: ArcOfCircle CenterX=-16.28 CenterY=44.75 CenterZ=0 NormalX=0 NormalY=0 NormalZ=1 AngleXU=0 Radius=1.5 StartAngle=4.71239 EndAngle=7.85398
    g17: ArcOfCircle CenterX=-18.2337 CenterY=39 CenterZ=0 NormalX=0 NormalY=0 NormalZ=1 AngleXU=0 Radius=1.5 StartAngle=4.71485 EndAngle=7.85398
    g18: ArcOfCircle CenterX=-16.2837 CenterY=27.25 CenterZ=0 NormalX=0 NormalY=0 NormalZ=1 AngleXU=0 Radius=1.5 StartAngle=4.71485 EndAngle=7.85398
    g19: ArcOfCircle CenterX=-18.2337 CenterY=33 CenterZ=0 NormalX=0 NormalY=0 NormalZ=1 AngleXU=0 Radius=1.5 StartAngle=4.71485 EndAngle=7.85398
    g20: ArcOfCircle CenterX=-11.49 CenterY=21.5 CenterZ=0 NormalX=0 NormalY=0 NormalZ=1 AngleXU=0 Radius=1.5 StartAngle=4.71239 EndAngle=7.85398
    g21: ArcOfCircle CenterX=-1.5 CenterY=4.25 CenterZ=0 NormalX=0 NormalY=0 NormalZ=1 AngleXU=0 Radius=1.5 StartAngle=4.71239 EndAngle=7.85398
    g22: ArcOfCircle CenterX=-1.5 CenterY=10 CenterZ=0 NormalX=0 NormalY=0 NormalZ=1 AngleXU=0 Radius=1.5 StartAngle=4.71239 EndAngle=7.85398
    g23: ArcOfCircle CenterX=-1.5 CenterY=15.75 CenterZ=0 NormalX=0 NormalY=0 NormalZ=1 AngleXU=0 Radius=1.5 StartAngle=4.71239 EndAngle=7.85398
    g24: LineSegment StartX=-49.19 StartY=69.25 StartZ=0 EndX=-1.5 EndY=69.25 EndZ=0
    g25: LineSegment StartX=-49.19 StartY=66.25 StartZ=0 EndX=-1.5 EndY=66.25 EndZ=0
    g26: LineSegment StartX=-49.19 StartY=63.5 StartZ=0 EndX=-1.5 EndY=63.5 EndZ=0
    g27: LineSegment StartX=-49.19 StartY=60.5 StartZ=0 EndX=-1.5 EndY=60.5 EndZ=0
    g28: LineSegment StartX=-49.19 StartY=57.75 StartZ=0 EndX=-1.5 EndY=57.75 EndZ=0
    g29: LineSegment StartX=-49.19 StartY=54.75 StartZ=0 EndX=-1.5 EndY=54.75 EndZ=0
    g30: LineSegment StartX=-49.19 StartY=52 StartZ=0 EndX=-11.49 EndY=52 EndZ=0
    g31: LineSegment StartX=-49.19 StartY=49 StartZ=0 EndX=-11.49 EndY=49 EndZ=0
    g32: LineSegment StartX=-49.19 StartY=46.25 StartZ=0 EndX=-16.28 EndY=46.25 EndZ=0
    g33: LineSegment StartX=-49.19 StartY=43.25 StartZ=0 EndX=-16.28 EndY=43.25 EndZ=0
    g34: LineSegment StartX=-49.19 StartY=40.5 StartZ=0 EndX=-18.2337 EndY=40.5 EndZ=0
    g35: LineSegment StartX=-49.19 StartY=37.5 StartZ=0 EndX=-18.23 EndY=37.5 EndZ=0
    g36: LineSegment StartX=-49.19 StartY=34.5 StartZ=0 EndX=-18.2337 EndY=34.5 EndZ=0
    g37: LineSegment StartX=-49.19 StartY=31.5 StartZ=0 EndX=-18.23 EndY=31.5 EndZ=0
    g38: LineSegment StartX=-49.19 StartY=28.75 StartZ=0 EndX=-16.2837 EndY=28.75 EndZ=0
    g39: LineSegment StartX=-49.19 StartY=25.75 StartZ=0 EndX=-16.28 EndY=25.75 EndZ=0
    g40: LineSegment StartX=-49.19 StartY=23 StartZ=0 EndX=-11.49 EndY=23 EndZ=0
    g41: LineSegment StartX=-49.19 StartY=20 StartZ=0 EndX=-11.49 EndY=20 EndZ=0
    g42: LineSegment StartX=-49.19 StartY=17.25 StartZ=0 EndX=-1.5 EndY=17.25 EndZ=0
    g43: LineSegment StartX=-49.19 StartY=14.25 StartZ=0 EndX=-1.5 EndY=14.25 EndZ=0
    g44: LineSegment StartX=-49.19 StartY=11.5 StartZ=0 EndX=-1.5 EndY=11.5 EndZ=0
    g45: LineSegment StartX=-49.19 StartY=8.5 StartZ=0 EndX=-1.5 EndY=8.5 EndZ=0
    g46: LineSegment StartX=-49.19 StartY=5.75 StartZ=0 EndX=-1.5 EndY=5.75 EndZ=0
    g47: LineSegment StartX=-49.19 StartY=2.75 StartZ=0 EndX=-1.5 EndY=2.75 EndZ=0
  constraints (120):
    c: Vertical(g0)
    c: Distance(g0) = 3
    c: Block(g0)
    c: Vertical(g1)
    c: Distance(g1) = 3
    c: Vertical(g2)
    c: Equal(g0,g2) = 3
    c: Block(g2)
    c: Vertical(g3)
    c: Equal(g1,g3) = 3
    c: Vertical(g4)
    c: Equal(g0,g4) = 3
    c: Block(g4)
    c: Vertical(g5)
    c: Equal(g1,g5) = 3
    c: Vertical(g6)
    c: Equal(g0,g6) = 3
    c: Block(g6)
    c: Vertical(g7)
    c: Equal(g1,g7) = 3
    c: Vertical(g8)
    c: Equal(g0,g8) = 3
    c: Block(g8)
    c: Vertical(g9)
    c: Equal(g1,g9) = 3
    c: Vertical(g10)
    c: Equal(g0,g10) = 3
    c: Block(g10)
    c: Vertical(g11)
    c: Equal(g1,g11) = 3
    c: Block(g12)
    c: Block(g13)
    c: Block(g14)
    c: Block(g15)
    c: Block(g16)
    c: Block(g17)
    c: Block(g18)
    c: Block(g19)
    c: Block(g20)
    c: Block(g21)
    c: Block(g22)
    c: Block(g23)
    c: Block(g11)
    c: Block(g9)
    c: Block(g7)
    c: Block(g5)
    c: Block(g3)
    c: Block(g1)
    c: Coincident(g24,g0)
    c: Coincident(g24,g12)
    c: Horizontal(g24)
    c: Coincident(g25,g0)
    c: Coincident(g25,g12)
    c: Horizontal(g25)
    c: Coincident(g26,g1)
    c: Coincident(g26,g13)
    c: Horizontal(g26)
    c: Coincident(g27,g1)
    c: Coincident(g27,g13)
    c: Horizontal(g27)
    c: Coincident(g28,g2)
    c: Coincident(g28,g14)
    c: Horizontal(g28)
    c: Coincident(g29,g2)
    c: Coincident(g29,g14)
    c: Horizontal(g29)
    c: Coincident(g30,g3)
    c: Coincident(g30,g15)
    c: Horizontal(g30)
    c: Coincident(g31,g3)
    c: Coincident(g31,g15)
    c: Horizontal(g31)
    c: Coincident(g32,g4)
    c: Coincident(g32,g16)
    c: Horizontal(g32)
    c: Coincident(g33,g4)
    c: Coincident(g33,g16)
    c: Horizontal(g33)
    c: Coincident(g34,g5)
    c: Coincident(g34,g17)
    c: Horizontal(g34)
    c: Coincident(g35,g5)
    c: Coincident(g35,g17)
    c: Horizontal(g35)
    c: Coincident(g36,g6)
    c: Coincident(g36,g19)
    c: Horizontal(g36)
    c: Coincident(g37,g6)
    c: Coincident(g37,g19)
    c: Horizontal(g37)
    c: Coincident(g38,g7)
    c: Coincident(g38,g18)
    c: Horizontal(g38)
    c: Coincident(g39,g7)
    c: Coincident(g39,g18)
    c: Horizontal(g39)
    c: Coincident(g40,g8)
    c: Coincident(g40,g20)
    c: Horizontal(g40)
    c: Coincident(g41,g8)
    c: Coincident(g41,g20)
    c: Horizontal(g41)
    c: Coincident(g42,g9)
    c: Coincident(g42,g23)
    c: Horizontal(g42)
    c: Coincident(g43,g9)
    c: Coincident(g43,g23)
    c: Horizontal(g43)
    c: Coincident(g44,g10)
    c: Coincident(g44,g22)
    c: Horizontal(g44)
    c: Coincident(g45,g10)
    c: Coincident(g45,g22)
    c: Horizontal(g45)
    c: Coincident(g46,g11)
    c: Coincident(g46,g21)
    c: Horizontal(g46)
    c: Coincident(g47,g11)
    c: Coincident(g47,g21)
    c: Horizontal(g47)
FEATURE [Part::Extrusion] Extrude023
  Base = -> Sketch032
  Dir = (1,-2e-16,2e-16)
  DirMode = 2
  FaceMakerClass = Part::FaceMakerBullseye
  LengthFwd = 19
  LengthRev = 0
  Placement = pos=(-19,0,0) rot=(0,0,1;0rad)
  Solid = true
  Symmetric = false
FEATURE [Part::Fillet] Fillet023
  Base = -> Extrude023
  Edges = <same value as first occurrence — deduplicated (x6 in doc)>
  Placement = pos=(0,0.05,0) rot=(0,0,1;0rad)
FEATURE [Part::Cut] Cut014  label="bottom003"
  Base = -> Cut007
  Tool = -> Fusion047
FEATURE [Part::Cut] Cut021  label="bottom004"
  Base = -> Cut014
  Tool = -> Fillet023
FEATURE [Sketcher::SketchObject] Sketch033
  FullyConstrained = true
  Placement = pos=(117,19,0) rot=(0.57735,0.57735,0.57735;2.0944rad)
  sketch-geometry (8):
    g0: LineSegment StartX=-49.19 StartY=69.25 StartZ=0 EndX=-49.19 EndY=66.25 EndZ=0
    g1: LineSegment StartX=-49.19 StartY=5.75 StartZ=0 EndX=-49.19 EndY=2.75 EndZ=0
    g2: ArcOfCircle CenterX=-1.5 CenterY=67.75 CenterZ=0 NormalX=0 NormalY=0 NormalZ=1 AngleXU=0 Radius=1.5 StartAngle=4.71239 EndAngle=7.85398
    g3: ArcOfCircle CenterX=-1.5 CenterY=4.25 CenterZ=0 NormalX=0 NormalY=0 NormalZ=1 AngleXU=0 Radius=1.5 StartAngle=4.71239 EndAngle=7.85398
    g4: LineSegment StartX=-49.19 StartY=69.25 StartZ=0 EndX=-1.5 EndY=69.25 EndZ=0
    g5: LineSegment StartX=-49.19 StartY=66.25 StartZ=0 EndX=-1.5 EndY=66.25 EndZ=0
    g6: LineSegment StartX=-49.19 StartY=5.75 StartZ=0 EndX=-1.5 EndY=5.75 EndZ=0
    g7: LineSegment StartX=-49.19 StartY=2.75 StartZ=0 EndX=-1.5 EndY=2.75 EndZ=0
  constraints (19):
    c: Vertical(g0)
    c: Distance(g0) = 3
    c: Block(g0)
    c: Vertical(g1)
    c: Block(g2)
    c: Block(g3)
    c: Block(g1)
    c: Coincident(g4,g0)
    c: Coincident(g4,g2)
    c: Horizontal(g4)
    c: Coincident(g5,g0)
    c: Coincident(g5,g2)
    c: Horizontal(g5)
    c: Coincident(g6,g1)
    c: Coincident(g6,g3)
    c: Horizontal(g6)
    c: Coincident(g7,g1)
    c: Coincident(g7,g3)
    c: Horizontal(g7)
FEATURE [Sketcher::SketchObject] Sketch034
  FullyConstrained = true
  Placement = pos=(117,19,0) rot=(0.57735,0.57735,0.57735;2.0944rad)
  sketch-geometry (8):
    g0: LineSegment StartX=-49.19 StartY=63.5 StartZ=0 EndX=-49.19 EndY=60.5 EndZ=0
    g1: LineSegment StartX=-49.19 StartY=11.5 StartZ=0 EndX=-49.19 EndY=8.5 EndZ=0
    g2: ArcOfCircle CenterX=-1.5 CenterY=62 CenterZ=0 NormalX=0 NormalY=0 NormalZ=1 AngleXU=0 Radius=1.5 StartAngle=4.71239 EndAngle=7.85398
    g3: ArcOfCircle CenterX=-1.5 CenterY=10 CenterZ=0 NormalX=0 NormalY=0 NormalZ=1 AngleXU=0 Radius=1.5 StartAngle=4.71239 EndAngle=7.85398
    g4: LineSegment StartX=-49.19 StartY=63.5 StartZ=0 EndX=-1.5 EndY=63.5 EndZ=0
    g5: LineSegment StartX=-49.19 StartY=60.5 StartZ=0 EndX=-1.5 EndY=60.5 EndZ=0
    g6: LineSegment StartX=-49.19 StartY=11.5 StartZ=0 EndX=-1.5 EndY=11.5 EndZ=0
    g7: LineSegment StartX=-49.19 StartY=8.5 StartZ=0 EndX=-1.5 EndY=8.5 EndZ=0
  constraints (19):
    c: Vertical(g0)
    c: Distance(g0) = 3
    c: Vertical(g1)
    c: Block(g1)
    c: Block(g2)
    c: Block(g3)
    c: Block(g0)
    c: Coincident(g4,g0)
    c: Coincident(g4,g2)
    c: Horizontal(g4)
    c: Coincident(g5,g0)
    c: Coincident(g5,g2)
    c: Horizontal(g5)
    c: Coincident(g6,g1)
    c: Coincident(g6,g3)
    c: Horizontal(g6)
    c: Coincident(g7,g1)
    c: Coincident(g7,g3)
    c: Horizontal(g7)
FEATURE [Part::Extrusion] Extrude024
  Base = -> Sketch033
  Dir = (1,0,0)
  DirMode = 2
  FaceMakerClass = Part::FaceMakerBullseye
  LengthFwd = 10
  LengthRev = 0
  Solid = true
  Symmetric = false
FEATURE [Part::Extrusion] Extrude025
  Base = -> Sketch034
  Dir = (1,0,0)
  DirMode = 2
  FaceMakerClass = Part::FaceMakerBullseye
  LengthFwd = 10
  LengthRev = 0
  Solid = true
  Symmetric = false
FEATURE [Part::Fillet] Fillet024  label="removeFromtMoreFrontCaseScrewRetainers"
  Base = -> Extrude024
  Edges = 4 edges r=1.49: [Edge6,Edge11,Edge18,Edge23]
  Placement = pos=(-11,0,0) rot=(0,0,1;0rad)
FEATURE [Part::Fillet] Fillet025  label="removeFromtMoreFrontCaseScrewRetainers001"
  Base = -> Extrude025
  Edges = 4 edges r=1.49: [Edge6,Edge11,Edge18,Edge23]
  Placement = pos=(-19,0,0) rot=(0,0,1;0rad)
FEATURE [Part::Cut] Cut022
  Base = -> Cut015
  Tool = -> Fillet025
FEATURE [Part::Cut] Cut023  label="screwRetainers"
  Base = -> Cut022
  Tool = -> Fillet024
FEATURE [Part::MultiFuse] Fusion056  label="bottom005"
  Shapes = -> [Fusion044,Cut021]
FEATURE [Part::MultiFuse] Fusion057  label="casePillars001"
  Shapes = -> [Cut016,Fusion052]
FEATURE [Part::MultiFuse] Fusion058  label="bottom006"
  Shapes = -> [Fusion056,Cut023]
FEATURE [Part::MultiFuse] Fusion059  label="bottom007"
  Shapes = -> [Fusion058,Fillet005]
FEATURE [Part::MultiFuse] Fusion060  label="bottom008"
  Shapes = -> [Fusion059,Fusion]
FEATURE [Part::MultiFuse] Fusion061  label="top011"
  Shapes = -> [Cut006,Cut020]
FEATURE [Part::MultiFuse] Fusion062  label="top012"
  Shapes = -> [Fusion057,Fusion061]
FEATURE [Sketcher::SketchObject] Sketch035  label="topSketch007"
  FullyConstrained = true
  sketch-geometry (6):
    g0: LineSegment StartX=19 StartY=38 StartZ=0 EndX=117 EndY=38 EndZ=0
    g1: ArcOfCircle CenterX=19 CenterY=19 CenterZ=0 NormalX=0 NormalY=0 NormalZ=1 AngleXU=0 Radius=19 StartAngle=1.5708 EndAngle=3.14159
    g2: LineSegment StartX=117 StartY=38 StartZ=0 EndX=117 EndY=19 EndZ=0
    g3: LineSegment StartX=98 StartY=1.0161e-12 StartZ=0 EndX=5.22862e-06 EndY=1.0161e-12 EndZ=0
    g4: LineSegment StartX=5.22862e-06 StartY=19 StartZ=0 EndX=5.22862e-06 EndY=1.0161e-12 EndZ=0
    g5: ArcOfCircle CenterX=98 CenterY=19 CenterZ=0 NormalX=0 NormalY=0 NormalZ=1 AngleXU=0 Radius=19 StartAngle=4.71239 EndAngle=6.28319
  constraints (16):
    c: Horizontal(g0)
    c: Distance(g0) = 98
    c: Coincident(g1,g0)
    c: Block(g1)
    c: Coincident(g2,g0)
    c: Vertical(g2)
    c: Distance(g2) = 19
    c: Horizontal(g3)
    c: Coincident(g4,g1)
    c: Vertical(g4)
    c: Coincident(g3,g4)
    c: Block(g3)
    c: Coincident(g5,g2)
    c: Coincident(g5,g3)
    c: Block(g0)
    c: Block(g5)
FEATURE [Part::Extrusion] Extrude026  label="sideA001"
  Base = -> Sketch035
  Dir = (0,0,1)
  DirMode = 2
  FaceMakerClass = Part::FaceMakerBullseye
  LengthFwd = 3
  LengthRev = 0
  Placement = pos=(0,0,-2.7) rot=(0,0,1;0rad)
  Solid = true
  Symmetric = false
FEATURE [Sketcher::SketchObject] Sketch036  label="topSketch008"
  FullyConstrained = true
  sketch-geometry (6):
    g0: LineSegment StartX=19 StartY=38 StartZ=0 EndX=117 EndY=38 EndZ=0
    g1: ArcOfCircle CenterX=19 CenterY=19 CenterZ=0 NormalX=0 NormalY=0 NormalZ=1 AngleXU=0 Radius=19 StartAngle=1.5708 EndAngle=3.14159
    g2: LineSegment StartX=117 StartY=38 StartZ=0 EndX=117 EndY=19 EndZ=0
    g3: LineSegment StartX=98 StartY=1.0161e-12 StartZ=0 EndX=5.22862e-06 EndY=1.0161e-12 EndZ=0
    g4: LineSegment StartX=5.22862e-06 StartY=19 StartZ=0 EndX=5.22862e-06 EndY=1.0161e-12 EndZ=0
    g5: ArcOfCircle CenterX=98 CenterY=19 CenterZ=0 NormalX=0 NormalY=0 NormalZ=1 AngleXU=0 Radius=19 StartAngle=4.71239 EndAngle=6.28319
  constraints (16):
    c: Horizontal(g0)
    c: Distance(g0) = 98
    c: Coincident(g1,g0)
    c: Block(g1)
    c: Coincident(g2,g0)
    c: Vertical(g2)
    c: Distance(g2) = 19
    c: Horizontal(g3)
    c: Coincident(g4,g1)
    c: Vertical(g4)
    c: Coincident(g3,g4)
    c: Block(g3)
    c: Coincident(g5,g2)
    c: Coincident(g5,g3)
    c: Block(g0)
    c: Block(g5)
FEATURE [Part::Extrusion] Extrude027  label="sideB001"
  Base = -> Sketch036
  Dir = (0,0,1)
  DirMode = 2
  FaceMakerClass = Part::FaceMakerBullseye
  LengthFwd = 3
  LengthRev = 0
  Placement = pos=(0,0,71.7) rot=(0,0,1;0rad)
  Solid = true
  Symmetric = false
FEATURE [Part::MultiFuse] Fusion064  label="removeFromBottom"
  Shapes = -> [Extrude026,Extrude027]
FEATURE [Part::Cut] Cut024  label="bottom009"
  Base = -> Fusion060
  Tool = -> Fusion064
FEATURE [Sketcher::SketchObject] Sketch037  label="topSketch009"
  FullyConstrained = true
  sketch-geometry (8):
    g0: ArcOfCircle CenterX=19 CenterY=19.1201 CenterZ=0 NormalX=0 NormalY=0 NormalZ=1 AngleXU=0 Radius=18.8799 StartAngle=1.5708 EndAngle=3.14793
    g1: LineSegment StartX=0.120501 StartY=19.0004 StartZ=0 EndX=0.120501 EndY=0.000382114 EndZ=0
    g2: LineSegment StartX=19 StartY=38 StartZ=0 EndX=124 EndY=38 EndZ=0
    g3: LineSegment StartX=0.120501 StartY=0.000382114 StartZ=0 EndX=105.121 EndY=0.000382114 EndZ=0
    g4: LineSegment StartX=124 StartY=38 StartZ=0 EndX=125.616 EndY=38 EndZ=0
    g5: LineSegment StartX=105.121 StartY=0.000382114 StartZ=0 EndX=106.736 EndY=0.000382114 EndZ=0
    g6: ArcOfCircle CenterX=106.616 CenterY=19 CenterZ=0 NormalX=0 NormalY=0 NormalZ=1 AngleXU=0 Radius=19 StartAngle=4.71873 EndAngle=6.28319
    g7: LineSegment StartX=125.616 StartY=38 StartZ=0 EndX=125.616 EndY=19 EndZ=0
  constraints (21):
    c: Block(g0)
    c: Coincident(g1,g0)
    c: Vertical(g1)
    c: Horizontal(g2)
    c: Distance(g2) = 105
    c: Coincident(g2,g0)
    c: Distance(g1) = 19
    c: Coincident(g3,g1)
    c: Horizontal(g3)
    c: Distance(g3) = 105
    c: Coincident(g4,g2)
    c: Horizontal(g4)
    c: Distance(g4) = 1.61553
    c: Horizontal(g5)
    c: Equal(g4,g5) = 1.61553
    c: Coincident(g5,g3)
    c: Block(g6)
    c: Coincident(g6,g5)
    c: Coincident(g7,g4)
    c: Coincident(g7,g6)
    c: Vertical(g7)
FEATURE [Part::Extrusion] Extrude028  label="sideB"
  Base = -> Sketch037
  Dir = (0,0,1)
  DirMode = 2
  FaceMakerClass = Part::FaceMakerBullseye
  LengthFwd = 3
  LengthRev = 0
  Placement = pos=(0,0,72) rot=(0,0,1;0rad)
  Solid = true
  Symmetric = false
FEATURE [Sketcher::SketchObject] Sketch038  label="topSketch010"
  FullyConstrained = true
  sketch-geometry (22):
    g0: LineSegment StartX=5.21097e-06 StartY=3 StartZ=0 EndX=5.21097e-06 EndY=19 EndZ=0
    g1: ArcOfCircle CenterX=19 CenterY=19 CenterZ=0 NormalX=0 NormalY=0 NormalZ=1 AngleXU=0 Radius=19 StartAngle=1.5708 EndAngle=3.14159
    g2: ArcOfCircle CenterX=19 CenterY=19 CenterZ=0 NormalX=0 NormalY=0 NormalZ=1 AngleXU=0 Radius=16 StartAngle=1.5708 EndAngle=3.14159
    g3: LineSegment StartX=114 StartY=35 StartZ=0 EndX=19 EndY=35 EndZ=0
    g4: LineSegment StartX=5.21097e-06 StartY=3 StartZ=0 EndX=5.21097e-06 EndY=0 EndZ=0
    g5: LineSegment StartX=3 StartY=0 StartZ=0 EndX=5.21097e-06 EndY=0 EndZ=0
    g6: LineSegment StartX=3 StartY=19 StartZ=0 EndX=3 EndY=0 EndZ=0
    g7: LineSegment StartX=19 StartY=38 StartZ=0 EndX=124 EndY=38 EndZ=0
    g8: Circle CenterX=119 CenterY=35 CenterZ=0 NormalX=0 NormalY=0 NormalZ=1 AngleXU=0 Radius=1
    g9: Circle CenterX=121 CenterY=35 CenterZ=0 NormalX=0 NormalY=0 NormalZ=1 AngleXU=0 Radius=1
    g10: Circle CenterX=121 CenterY=33 CenterZ=0 NormalX=0 NormalY=0 NormalZ=1 AngleXU=0 Radius=1
    g11: BSplineCurve PolesCount=3 KnotsCount=2 Degree=2 IsPeriodic=0
    g12: GeomPoint X=119 Y=35 Z=0
    g13: GeomPoint X=121 Y=33 Z=0
    g14: LineSegment StartX=119 StartY=35 StartZ=0 EndX=114 EndY=35 EndZ=0
    g15: ArcOfCircle CenterX=105 CenterY=19 CenterZ=0 NormalX=0 NormalY=0 NormalZ=1 AngleXU=0 Radius=16 StartAngle=5.60905 EndAngle=6.28319
    g16: LineSegment StartX=121 StartY=33 StartZ=0 EndX=121 EndY=19 EndZ=0
    g17: LineSegment StartX=117.5 StartY=9.01251 StartZ=0 EndX=121.163 EndY=9.0125 EndZ=0
    g18: ArcOfCircle CenterX=105 CenterY=19 CenterZ=0 NormalX=0 NormalY=0 NormalZ=1 AngleXU=0 Radius=20.6155 StartAngle=5.7297 EndAngle=6.28319
    g19: LineSegment StartX=121.163 StartY=9.0125 StartZ=0 EndX=122.538 EndY=8.16329 EndZ=0
    g20: LineSegment StartX=124 StartY=38 StartZ=0 EndX=125.616 EndY=38 EndZ=0
    g21: LineSegment StartX=125.616 StartY=19 StartZ=0 EndX=125.616 EndY=38 EndZ=0
  constraints (49):
    c: Vertical(g0)
    c: Block(g0)
    c: Coincident(g1,g0)
    c: Block(g1)
    c: Coincident(g2,g1)
    c: Block(g2)
    c: Coincident(g3,g2)
    c: Horizontal(g3)
    c: Tangent(g3,g2)
    c: Coincident(g4,g0)
    c: Distance(g4) = 3
    c: Vertical(g4)
    c: Coincident(g5,g4)
    c: Horizontal(g5)
    c: Coincident(g6,g2)
    c: Coincident(g6,g5)
    c: Vertical(g6)
    c: Horizontal(g7)
    c: Distance(g7) = 105
    c: Coincident(g7,g1)
    c: Block(g3)
    c: Weight(g8) = 1
    c: Equal(g8,g9)
    c: Equal(g8,g10)
    c: InternalAlignment(g8,g11)
    c: InternalAlignment(g9,g11)
    c: InternalAlignment(g10,g11)
    c: InternalAlignment(g12,g11)
    c: InternalAlignment(g13,g11)
    c: Block(g11)
    c: Coincident(g14,g11)
    c: Coincident(g14,g3)
    c: Horizontal(g14)
    c: Block(g15)
    c: Coincident(g16,g11)
    c: Coincident(g16,g15)
    c: Vertical(g16)
    c: Distance(g16) = 14
    c: Coincident(g17,g15)
    c: Block(g18)
    c: Coincident(g19,g18)
    c: Coincident(g20,g7)
    c: Horizontal(g20)
    c: Vertical(g21)
    c: Coincident(g20,g21)
    c: Block(g20)
    c: Block(g21)
    c: Block(g19)
    c: Block(g17)
FEATURE [Part::Extrusion] Extrude029
  Base = -> Sketch038
  Dir = (0,0,1)
  DirMode = 2
  FaceMakerClass = Part::FaceMakerBullseye
  LengthFwd = 72
  LengthRev = 0
  Solid = true
  Symmetric = false
FEATURE [Part::Feature] Face085
  shape: bbox 4.8 x 25.5 x 2e-07 mm, 1 faces, 0 solids (baked)
FEATURE [Part::Revolution] Revolve089  label="moreFrontCaseScrewPost003"
  Angle = 360
  Axis = (0,1,0)
  Base = (0,0,0)
  FaceMakerClass = Part::FaceMakerBullseye
  Placement = pos=(109.5,4.5,3.5) rot=(0,0,1;0rad)
  Solid = false
  Source = -> Face085
  Symmetric = false
FEATURE [Part::Feature] Face086
  shape: bbox 4.8 x 25.5 x 2e-07 mm, 1 faces, 0 solids (baked)
FEATURE [Part::Revolution] Revolve090  label="moreFrontCaseScrewPost004"
  Angle = 360
  Axis = (0,1,0)
  Base = (0,0,0)
  FaceMakerClass = Part::FaceMakerBullseye
  Placement = pos=(109.5,4.5,68.5) rot=(0,0,1;0rad)
  Solid = false
  Source = -> Face086
  Symmetric = false
FEATURE [Part::Fillet] Fillet026  label="top013"
  Base = -> Extrude029
  Edges = 1 edges r=2: [Edge35]
FEATURE [Sketcher::SketchObject] Sketch039
  FullyConstrained = true
  sketch-geometry (7):
    g0: LineSegment StartX=0 StartY=0 StartZ=0 EndX=0 EndY=6 EndZ=0
    g1: Circle CenterX=0 CenterY=0 CenterZ=0 NormalX=0 NormalY=0 NormalZ=1 AngleXU=0 Radius=1
    g2: Circle CenterX=8 CenterY=6 CenterZ=0 NormalX=0 NormalY=0 NormalZ=1 AngleXU=0 Radius=1
    g3: BSplineCurve PolesCount=3 KnotsCount=2 Degree=2 IsPeriodic=0
    g4: GeomPoint X=0 Y=0 Z=0
    g5: GeomPoint X=8 Y=6 Z=0
    g6: LineSegment StartX=0 StartY=6 StartZ=0 EndX=8 EndY=6 EndZ=0
  constraints (14):
    c: Coincident(g0,g-1)
    c: Distance(g0) = 6
    c: Vertical(g0)
    c: Coincident(g3,g0)
    c: Weight(g1) = 1
    c: Equal(g1,g2)
    c: InternalAlignment(g1,g3)
    c: InternalAlignment(g2,g3)
    c: InternalAlignment(g4,g3)
    c: InternalAlignment(g5,g3)
    c: Block(g3)
    c: Coincident(g6,g0)
    c: Coincident(g6,g3)
    c: Horizontal(g6)
FEATURE [Sketcher::SketchObject] Sketch040
  FullyConstrained = true
  sketch-geometry (7):
    g0: LineSegment StartX=0 StartY=0 StartZ=0 EndX=0 EndY=6 EndZ=0
    g1: Circle CenterX=0 CenterY=0 CenterZ=0 NormalX=0 NormalY=0 NormalZ=1 AngleXU=0 Radius=1
    g2: Circle CenterX=8 CenterY=6 CenterZ=0 NormalX=0 NormalY=0 NormalZ=1 AngleXU=0 Radius=1
    g3: BSplineCurve PolesCount=3 KnotsCount=2 Degree=2 IsPeriodic=0
    g4: GeomPoint X=0 Y=0 Z=0
    g5: GeomPoint X=8 Y=6 Z=0
    g6: LineSegment StartX=0 StartY=6 StartZ=0 EndX=8 EndY=6 EndZ=0
  constraints (14):
    c: Coincident(g0,g-1)
    c: Distance(g0) = 6
    c: Vertical(g0)
    c: Coincident(g3,g0)
    c: Weight(g1) = 1
    c: Equal(g1,g2)
    c: InternalAlignment(g1,g3)
    c: InternalAlignment(g2,g3)
    c: InternalAlignment(g4,g3)
    c: InternalAlignment(g5,g3)
    c: Block(g3)
    c: Coincident(g6,g0)
    c: Coincident(g6,g3)
    c: Horizontal(g6)
FEATURE [Sketcher::SketchObject] Sketch041
  FullyConstrained = true
  sketch-geometry (7):
    g0: LineSegment StartX=0 StartY=0 StartZ=0 EndX=0 EndY=6 EndZ=0
    g1: Circle CenterX=0 CenterY=0 CenterZ=0 NormalX=0 NormalY=0 NormalZ=1 AngleXU=0 Radius=1
    g2: Circle CenterX=8 CenterY=6 CenterZ=0 NormalX=0 NormalY=0 NormalZ=1 AngleXU=0 Radius=1
    g3: BSplineCurve PolesCount=3 KnotsCount=2 Degree=2 IsPeriodic=0
    g4: GeomPoint X=0 Y=0 Z=0
    g5: GeomPoint X=8 Y=6 Z=0
    g6: LineSegment StartX=0 StartY=6 StartZ=0 EndX=8 EndY=6 EndZ=0
  constraints (14):
    c: Coincident(g0,g-1)
    c: Distance(g0) = 6
    c: Vertical(g0)
    c: Coincident(g3,g0)
    c: Weight(g1) = 1
    c: Equal(g1,g2)
    c: InternalAlignment(g1,g3)
    c: InternalAlignment(g2,g3)
    c: InternalAlignment(g4,g3)
    c: InternalAlignment(g5,g3)
    c: Block(g3)
    c: Coincident(g6,g0)
    c: Coincident(g6,g3)
    c: Horizontal(g6)
FEATURE [Sketcher::SketchObject] Sketch042
  FullyConstrained = true
  sketch-geometry (7):
    g0: LineSegment StartX=0 StartY=0 StartZ=0 EndX=0 EndY=6 EndZ=0
    g1: Circle CenterX=0 CenterY=0 CenterZ=0 NormalX=0 NormalY=0 NormalZ=1 AngleXU=0 Radius=1
    g2: Circle CenterX=8 CenterY=6 CenterZ=0 NormalX=0 NormalY=0 NormalZ=1 AngleXU=0 Radius=1
    g3: BSplineCurve PolesCount=3 KnotsCount=2 Degree=2 IsPeriodic=0
    g4: GeomPoint X=0 Y=0 Z=0
    g5: GeomPoint X=8 Y=6 Z=0
    g6: LineSegment StartX=0 StartY=6 StartZ=0 EndX=8 EndY=6 EndZ=0
  constraints (14):
    c: Coincident(g0,g-1)
    c: Distance(g0) = 6
    c: Vertical(g0)
    c: Coincident(g3,g0)
    c: Weight(g1) = 1
    c: Equal(g1,g2)
    c: InternalAlignment(g1,g3)
    c: InternalAlignment(g2,g3)
    c: InternalAlignment(g4,g3)
    c: InternalAlignment(g5,g3)
    c: Block(g3)
    c: Coincident(g6,g0)
    c: Coincident(g6,g3)
    c: Horizontal(g6)
FEATURE [Part::Extrusion] Extrude030  label="caseScrewPillarBracket008"
  Base = -> Sketch039
  Dir = (0,0,1)
  DirMode = 2
  FaceMakerClass = Part::FaceMakerBullseye
  LengthFwd = 2.4
  LengthRev = 0
  Placement = pos=(15.76,29,8.8) rot=(0,1,0;0rad)
  Solid = true
  Symmetric = false
FEATURE [Part::Extrusion] Extrude031  label="caseScrewPillarBracket009"
  Base = -> Sketch040
  Dir = (0,0,1)
  DirMode = 2
  FaceMakerClass = Part::FaceMakerBullseye
  LengthFwd = 2.4
  LengthRev = 0
  Placement = pos=(15.76,29,60.8) rot=(0,0,1;0rad)
  Solid = true
  Symmetric = false
FEATURE [Part::Extrusion] Extrude032  label="caseScrewPillarBracket010"
  Base = -> Sketch041
  Dir = (0,0,1)
  DirMode = 2
  FaceMakerClass = Part::FaceMakerBullseye
  LengthFwd = 2.4
  LengthRev = 0
  Placement = pos=(13.7,29,13.26) rot=(0,-1,0;1.5708rad)
  Solid = true
  Symmetric = false
FEATURE [Part::Extrusion] Extrude033  label="caseScrewPillarBracket011"
  Base = -> Sketch042
  Dir = (0,0,1)
  DirMode = 2
  FaceMakerClass = Part::FaceMakerBullseye
  LengthFwd = 2.4
  LengthRev = 0
  Placement = pos=(11.3,29,58.74) rot=(0,1,0;1.5708rad)
  Solid = true
  Symmetric = false
FEATURE [Sketcher::SketchObject] Sketch043
  FullyConstrained = true
  sketch-geometry (7):
    g0: LineSegment StartX=0 StartY=0 StartZ=0 EndX=0 EndY=6 EndZ=0
    g1: Circle CenterX=0 CenterY=0 CenterZ=0 NormalX=0 NormalY=0 NormalZ=1 AngleXU=0 Radius=1
    g2: Circle CenterX=8 CenterY=6 CenterZ=0 NormalX=0 NormalY=0 NormalZ=1 AngleXU=0 Radius=1
    g3: BSplineCurve PolesCount=3 KnotsCount=2 Degree=2 IsPeriodic=0
    g4: GeomPoint X=0 Y=0 Z=0
    g5: GeomPoint X=8 Y=6 Z=0
    g6: LineSegment StartX=0 StartY=6 StartZ=0 EndX=8 EndY=6 EndZ=0
  constraints (14):
    c: Coincident(g0,g-1)
    c: Distance(g0) = 6
    c: Vertical(g0)
    c: Coincident(g3,g0)
    c: Weight(g1) = 1
    c: Equal(g1,g2)
    c: InternalAlignment(g1,g3)
    c: InternalAlignment(g2,g3)
    c: InternalAlignment(g4,g3)
    c: InternalAlignment(g5,g3)
    c: Block(g3)
    c: Coincident(g6,g0)
    c: Coincident(g6,g3)
    c: Horizontal(g6)
FEATURE [Part::Extrusion] Extrude034  label="caseScrewPillarBracket012"
  Base = -> Sketch043
  Dir = (0,0,1)
  DirMode = 2
  FaceMakerClass = Part::FaceMakerBullseye
  LengthFwd = 2.4
  LengthRev = 0
  Placement = pos=(88.3,29,65.23) rot=(0,1,0;1.5708rad)
  Solid = true
  Symmetric = false
FEATURE [Sketcher::SketchObject] Sketch044
  FullyConstrained = true
  sketch-geometry (7):
    g0: LineSegment StartX=0 StartY=0 StartZ=0 EndX=0 EndY=6 EndZ=0
    g1: Circle CenterX=0 CenterY=0 CenterZ=0 NormalX=0 NormalY=0 NormalZ=1 AngleXU=0 Radius=1
    g2: Circle CenterX=8 CenterY=6 CenterZ=0 NormalX=0 NormalY=0 NormalZ=1 AngleXU=0 Radius=1
    g3: BSplineCurve PolesCount=3 KnotsCount=2 Degree=2 IsPeriodic=0
    g4: GeomPoint X=0 Y=0 Z=0
    g5: GeomPoint X=8 Y=6 Z=0
    g6: LineSegment StartX=0 StartY=6 StartZ=0 EndX=8 EndY=6 EndZ=0
  constraints (14):
    c: Coincident(g0,g-1)
    c: Distance(g0) = 6
    c: Vertical(g0)
    c: Coincident(g3,g0)
    c: Weight(g1) = 1
    c: Equal(g1,g2)
    c: InternalAlignment(g1,g3)
    c: InternalAlignment(g2,g3)
    c: InternalAlignment(g4,g3)
    c: InternalAlignment(g5,g3)
    c: Block(g3)
    c: Coincident(g6,g0)
    c: Coincident(g6,g3)
    c: Horizontal(g6)
FEATURE [Part::Extrusion] Extrude035  label="caseScrewPillarBracket013"
  Base = -> Sketch044
  Dir = (0,0,1)
  DirMode = 2
  FaceMakerClass = Part::FaceMakerBullseye
  LengthFwd = 2.4
  LengthRev = 0
  Placement = pos=(90.7,29,6.77) rot=(0,-1,0;1.5708rad)
  Solid = true
  Symmetric = false
FEATURE [Sketcher::SketchObject] Sketch045
  FullyConstrained = true
  sketch-geometry (7):
    g0: LineSegment StartX=0 StartY=0 StartZ=0 EndX=0 EndY=6 EndZ=0
    g1: Circle CenterX=0 CenterY=0 CenterZ=0 NormalX=0 NormalY=0 NormalZ=1 AngleXU=0 Radius=1
    g2: Circle CenterX=8 CenterY=6 CenterZ=0 NormalX=0 NormalY=0 NormalZ=1 AngleXU=0 Radius=1
    g3: BSplineCurve PolesCount=3 KnotsCount=2 Degree=2 IsPeriodic=0
    g4: GeomPoint X=0 Y=0 Z=0
    g5: GeomPoint X=8 Y=6 Z=0
    g6: LineSegment StartX=0 StartY=6 StartZ=0 EndX=8 EndY=6 EndZ=0
  constraints (14):
    c: Coincident(g0,g-1)
    c: Distance(g0) = 6
    c: Vertical(g0)
    c: Coincident(g3,g0)
    c: Weight(g1) = 1
    c: Equal(g1,g2)
    c: InternalAlignment(g1,g3)
    c: InternalAlignment(g2,g3)
    c: InternalAlignment(g4,g3)
    c: InternalAlignment(g5,g3)
    c: Block(g3)
    c: Coincident(g6,g0)
    c: Coincident(g6,g3)
    c: Horizontal(g6)
FEATURE [Sketcher::SketchObject] Sketch046
  FullyConstrained = true
  sketch-geometry (7):
    g0: LineSegment StartX=0 StartY=0 StartZ=0 EndX=0 EndY=6 EndZ=0
    g1: Circle CenterX=0 CenterY=0 CenterZ=0 NormalX=0 NormalY=0 NormalZ=1 AngleXU=0 Radius=1
    g2: Circle CenterX=8 CenterY=6 CenterZ=0 NormalX=0 NormalY=0 NormalZ=1 AngleXU=0 Radius=1
    g3: BSplineCurve PolesCount=3 KnotsCount=2 Degree=2 IsPeriodic=0
    g4: GeomPoint X=0 Y=0 Z=0
    g5: GeomPoint X=8 Y=6 Z=0
    g6: LineSegment StartX=0 StartY=6 StartZ=0 EndX=8 EndY=6 EndZ=0
  constraints (14):
    c: Coincident(g0,g-1)
    c: Distance(g0) = 6
    c: Vertical(g0)
    c: Coincident(g3,g0)
    c: Weight(g1) = 1
    c: Equal(g1,g2)
    c: InternalAlignment(g1,g3)
    c: InternalAlignment(g2,g3)
    c: InternalAlignment(g4,g3)
    c: InternalAlignment(g5,g3)
    c: Block(g3)
    c: Coincident(g6,g0)
    c: Coincident(g6,g3)
    c: Horizontal(g6)
FEATURE [Part::Extrusion] Extrude036  label="caseScrewPillarBracket014"
  Base = -> Sketch045
  Dir = (0,0,1)
  DirMode = 2
  FaceMakerClass = Part::FaceMakerBullseye
  LengthFwd = 2.4
  LengthRev = 0
  Placement = pos=(110.7,29,6.77) rot=(0,-1,0;1.5708rad)
  Solid = true
  Symmetric = false
FEATURE [Part::Extrusion] Extrude037  label="caseScrewPillarBracket015"
  Base = -> Sketch046
  Dir = (0,0,1)
  DirMode = 2
  FaceMakerClass = Part::FaceMakerBullseye
  LengthFwd = 2.4
  LengthRev = 0
  Placement = pos=(108.3,29,65.23) rot=(0,1,0;1.5708rad)
  Solid = true
  Symmetric = false
FEATURE [Part::Box] Box013  label="frontCaseScrewPillarBracket002"
  AttacherType = Attacher::AttachEngine3D
  Height = 2.4
  Length = 22
  Placement = pos=(87,28,2.3) rot=(0,0,1;0rad)
  Width = 7
FEATURE [Part::Box] Box014  label="frontCaseScrewPillarBracket003"
  AttacherType = Attacher::AttachEngine3D
  Height = 2.4
  Length = 22
  Placement = pos=(87,28,67.3) rot=(0,0,1;0rad)
  Width = 7
FEATURE [Part::Feature] Face087
  shape: bbox 4.8 x 30.2 x 2e-07 mm, 1 faces, 0 solids (baked)
FEATURE [Part::Revolution] Revolve091  label="frontCaseScrewPost004"
  Angle = 360
  Axis = (0,1,0)
  Base = (0,0,0)
  FaceMakerClass = Part::FaceMakerBullseye
  Placement = pos=(89.5,4.5,3.5) rot=(0,0,1;0rad)
  Solid = false
  Source = -> Face087
  Symmetric = false
FEATURE [Part::Feature] Face088
  shape: bbox 4.8 x 30.2 x 2e-07 mm, 1 faces, 0 solids (baked)
FEATURE [Part::Revolution] Revolve092  label="frontCaseScrewPost005"
  Angle = 360
  Axis = (0,1,0)
  Base = (0,0,0)
  FaceMakerClass = Part::FaceMakerBullseye
  Placement = pos=(89.5,4.5,68.5) rot=(0,0,1;0rad)
  Solid = false
  Source = -> Face088
  Symmetric = false
FEATURE [Part::Feature] Face089
  shape: bbox 3.5 x 30.2 x 2e-07 mm, 1 faces, 0 solids (baked)
FEATURE [Part::Revolution] Revolve093  label="backCaseScrewPost002"
  Angle = 360
  Axis = (0,1,0)
  Base = (0,0,0)
  FaceMakerClass = Part::FaceMakerBullseye
  Placement = pos=(12.5,4.5,10) rot=(0,0,1;0rad)
  Solid = false
  Source = -> Face089
  Symmetric = false
FEATURE [Part::Feature] Face090
  shape: bbox 3.5 x 30.2 x 2e-07 mm, 1 faces, 0 solids (baked)
FEATURE [Part::Revolution] Revolve094  label="backCaseScrewPost003"
  Angle = 360
  Axis = (0,1,0)
  Base = (0,0,0)
  FaceMakerClass = Part::FaceMakerBullseye
  Placement = pos=(12.5,4.5,62) rot=(0,0,1;0rad)
  Solid = false
  Source = -> Face090
  Symmetric = false
FEATURE [Part::Box] Box015  label="Cube011"
  AttacherType = Attacher::AttachEngine3D
  Height = 28.8
  Length = 3
  Placement = pos=(107.3,28,21.6) rot=(0,0,1;0rad)
  Width = 7
FEATURE [Part::Box] Box016  label="Cube012"
  AttacherType = Attacher::AttachEngine3D
  Height = 3
  Length = 7.4
  Placement = pos=(107.3,28,18.6) rot=(0,0,1;0rad)
  Width = 7
FEATURE [Part::Box] Box017  label="Cube013"
  AttacherType = Attacher::AttachEngine3D
  Height = 3
  Length = 7.4
  Placement = pos=(107.3,28,50.4) rot=(0,0,1;0rad)
  Width = 7
FEATURE [Part::Cylinder] Cylinder024
  Angle = 360
  AttacherType = Attacher::AttachEngine3D
  Height = 20
  Placement = pos=(0,0,36.15) rot=(0,0,1;0rad)
  Radius = 14.3
FEATURE [Part::Cylinder] Cylinder025
  Angle = 360
  AttacherType = Attacher::AttachEngine3D
  Height = 10
  Placement = pos=(0,0,36.15) rot=(0,0,1;0rad)
  Radius = 4
FEATURE [Part::MultiFuse] Fusion066  label="removeToCreteHoleForPlugHousing009"
  Placement = pos=(70,19,36) rot=(0,1,0;1.5708rad)
  Shapes = -> [Cylinder024,Cylinder025]
FEATURE [Part::MultiFuse] Fusion065  label="plugHousingBracketHolder002"
  Shapes = -> [Box017,Box015,Box016]
FEATURE [Part::Cut] Cut025  label="plugHousingBracketHolder003"
  Base = -> Fusion065
  Placement = pos=(7,0,0) rot=(0,0,1;0rad)
  Tool = -> Fusion066
FEATURE [Sketcher::SketchObject] Sketch047
  FullyConstrained = false
  Placement = pos=(0,0,0) rot=(1,0,0;1.5708rad)
  sketch-geometry (24):
    g0: ArcOfCircle CenterX=-4 CenterY=-10.5 CenterZ=0 NormalX=0 NormalY=0 NormalZ=1 AngleXU=0 Radius=1.5 StartAngle=6e-16 EndAngle=3.14159
    g1: ArcOfCircle CenterX=-34.2 CenterY=-10.5 CenterZ=0 NormalX=0 NormalY=0 NormalZ=1 AngleXU=0 Radius=1.5 StartAngle=0 EndAngle=3.14159
    g2: ArcOfCircle CenterX=-34.2 CenterY=-27.7 CenterZ=0 NormalX=0 NormalY=0 NormalZ=1 AngleXU=0 Radius=1.5 StartAngle=3.14159 EndAngle=6.28319
    g3: ArcOfCircle CenterX=-4 CenterY=-27.7 CenterZ=0 NormalX=0 NormalY=0 NormalZ=1 AngleXU=0 Radius=1.5 StartAngle=3.1416 EndAngle=6.28319
    g4: ArcOfCircle CenterX=-10 CenterY=-4.3 CenterZ=0 NormalX=0 NormalY=0 NormalZ=1 AngleXU=0 Radius=1.5 StartAngle=2e-16 EndAngle=3.14159
    g5: ArcOfCircle CenterX=-16.1 CenterY=-1.8 CenterZ=0 NormalX=0 NormalY=0 NormalZ=1 AngleXU=0 Radius=1.5 StartAngle=5e-16 EndAngle=3.14159
    g6: ArcOfCircle CenterX=-22.1 CenterY=-1.8 CenterZ=0 NormalX=0 NormalY=0 NormalZ=1 AngleXU=0 Radius=1.5 StartAngle=5e-16 EndAngle=3.14159
    g7: ArcOfCircle CenterX=-28.2 CenterY=-4.3 CenterZ=0 NormalX=0 NormalY=0 NormalZ=1 AngleXU=0 Radius=1.5 StartAngle=2e-16 EndAngle=3.14159
    g8: ArcOfCircle CenterX=-10 CenterY=-33.9 CenterZ=0 NormalX=0 NormalY=0 NormalZ=1 AngleXU=0 Radius=1.5 StartAngle=3.14159 EndAngle=6.28319
    g9: ArcOfCircle CenterX=-16.1 CenterY=-36.4 CenterZ=0 NormalX=0 NormalY=0 NormalZ=1 AngleXU=0 Radius=1.5 StartAngle=3.14159 EndAngle=6.28319
    g10: ArcOfCircle CenterX=-22.1 CenterY=-36.4 CenterZ=0 NormalX=0 NormalY=0 NormalZ=1 AngleXU=0 Radius=1.5 StartAngle=3.14159 EndAngle=6.28319
    g11: ArcOfCircle CenterX=-28.2 CenterY=-33.9 CenterZ=0 NormalX=0 NormalY=0 NormalZ=1 AngleXU=0 Radius=1.5 StartAngle=3.14159 EndAngle=6.28319
    g12: LineSegment StartX=-35.7 StartY=-10.5 StartZ=0 EndX=-35.7 EndY=-27.7 EndZ=0
    g13: LineSegment StartX=-32.7 StartY=-10.5 StartZ=0 EndX=-32.7 EndY=-27.7 EndZ=0
    g14: LineSegment StartX=-29.7 StartY=-33.9 StartZ=0 EndX=-29.7 EndY=-4.3 EndZ=0
    g15: LineSegment StartX=-26.7 StartY=-33.9 StartZ=0 EndX=-26.7 EndY=-4.3 EndZ=0
    g16: LineSegment StartX=-2.5 StartY=-10.5 StartZ=0 EndX=-2.5 EndY=-27.7 EndZ=0
    g17: LineSegment StartX=-8.5 StartY=-4.3 StartZ=0 EndX=-8.5 EndY=-33.9 EndZ=0
    g18: LineSegment StartX=-5.5 StartY=-10.5 StartZ=0 EndX=-5.5 EndY=-27.7 EndZ=0
    g19: LineSegment StartX=-11.5 StartY=-4.3 StartZ=0 EndX=-11.5 EndY=-33.9 EndZ=0
    g20: LineSegment StartX=-14.6 StartY=-1.8 StartZ=0 EndX=-14.6 EndY=-36.4 EndZ=0
    g21: LineSegment StartX=-17.6 StartY=-1.8 StartZ=0 EndX=-17.6 EndY=-36.4 EndZ=0
    g22: LineSegment StartX=-20.6 StartY=-36.4 StartZ=0 EndX=-20.6 EndY=-1.8 EndZ=0
    g23: LineSegment StartX=-23.6 StartY=-1.8 StartZ=0 EndX=-23.6 EndY=-36.4 EndZ=0
  constraints (48):
    c: Block(g0)
    c: Block(g1)
    c: Block(g2)
    c: Block(g3)
    c: Block(g4)
    c: Block(g5)
    c: Block(g6)
    c: Block(g7)
    c: Block(g8)
    c: Block(g9)
    c: Block(g10)
    c: Block(g11)
    c: Coincident(g12,g1)
    c: Coincident(g12,g2)
    c: Vertical(g12)
    c: Coincident(g13,g1)
    c: Coincident(g13,g2)
    c: Vertical(g13)
    c: Coincident(g14,g11)
    c: Coincident(g14,g7)
    c: Vertical(g14)
    c: Coincident(g15,g11)
    c: Coincident(g15,g7)
    c: Vertical(g15)
    c: Coincident(g16,g0)
    c: Coincident(g16,g3)
    c: Vertical(g16)
    c: Coincident(g17,g4)
    c: Coincident(g17,g8)
    c: Vertical(g17)
    c: Coincident(g18,g0)
    c: Coincident(g18,g3)
    c: Vertical(g18)
    c: Coincident(g19,g4)
    c: Coincident(g19,g8)
    c: Vertical(g19)
    c: Coincident(g20,g5)
    c: Coincident(g20,g9)
    c: Vertical(g20)
    c: Coincident(g21,g5)
    c: Coincident(g21,g9)
    c: Vertical(g21)
    c: Coincident(g22,g10)
    c: Coincident(g22,g6)
    c: Vertical(g22)
    c: Coincident(g23,g6)
    c: Coincident(g23,g10)
    c: Vertical(g23)
FEATURE [Part::Extrusion] Extrude038  label="removeToCreateFanGrillHoles001"
  Base = -> Sketch047
  Dir = (0,-1,6e-16)
  DirMode = 2
  FaceMakerClass = Part::FaceMakerBullseye
  LengthFwd = 10
  LengthRev = 0
  Placement = pos=(65.4,44,54.82) rot=(0,0,1;0rad)
  Solid = true
  Symmetric = false
FEATURE [Part::Feature] Wire004
  shape: bbox 11 x 5.2 x 2e-07 mm, 0 faces, 0 solids (baked)
FEATURE [Part::Revolution] Revolve095
  Angle = 360
  Axis = (0,1,0)
  Base = (0,0,0)
  FaceMakerClass = Part::FaceMakerBullseye
  Placement = pos=(30.3,38,19.7) rot=(0,0,1;0rad)
  Solid = true
  Source = -> Wire004
  Symmetric = false
FEATURE [Part::Feature] Wire005
  shape: bbox 11 x 5.2 x 2e-07 mm, 0 faces, 0 solids (baked)
FEATURE [Part::Revolution] Revolve096
  Angle = 360
  Axis = (0,1,0)
  Base = (0,0,0)
  FaceMakerClass = Part::FaceMakerBullseye
  Placement = pos=(30.3,38,51.7) rot=(0,0,1;0rad)
  Solid = true
  Source = -> Wire005
  Symmetric = false
FEATURE [Part::Feature] Wire006
  shape: bbox 11 x 5.2 x 2e-07 mm, 0 faces, 0 solids (baked)
FEATURE [Part::Revolution] Revolve097
  Angle = 360
  Axis = (0,1,0)
  Base = (0,0,0)
  FaceMakerClass = Part::FaceMakerBullseye
  Placement = pos=(62.3,38,51.7) rot=(0,0,1;0rad)
  Solid = true
  Source = -> Wire006
  Symmetric = false
FEATURE [Part::Feature] Wire007
  shape: bbox 11 x 5.2 x 2e-07 mm, 0 faces, 0 solids (baked)
FEATURE [Part::Revolution] Revolve098
  Angle = 360
  Axis = (0,1,0)
  Base = (0,0,0)
  FaceMakerClass = Part::FaceMakerBullseye
  Placement = pos=(62.3,38,19.7) rot=(0,0,1;0rad)
  Solid = true
  Source = -> Wire007
  Symmetric = false
FEATURE [Part::MultiFuse] Fusion067  label="fanScrewHousing002"
  Shapes = -> [Revolve098,Revolve097,Revolve096,Revolve095]
FEATURE [Part::Feature] Face091 .. Face094  x4 (patterned run collapsed; names and placements below)
  shape: bbox 3.5 x 17.8 x 2e-07 mm, 1 faces, 0 solids (baked)
FEATURE [Part::Revolution] Revolve099  label="removeToCreateScrewAndThreadedInsertHole026"
  Angle = 360
  Axis = (0,1,0)
  Base = (0,0,0)
  FaceMakerClass = Part::FaceMakerBullseye
  Placement = pos=(62.3,30.3,19.7) rot=(0,0,1;0rad)
  Solid = false
  Source = -> Face091
  Symmetric = false
FEATURE [Part::Revolution] Revolve100  label="removeToCreateScrewAndThreadedInsertHole027"
  Angle = 360
  Axis = (0,1,0)
  Base = (0,0,0)
  FaceMakerClass = Part::FaceMakerBullseye
  Placement = pos=(62.3,30.3,51.7) rot=(0,0,1;0rad)
  Solid = false
  Source = -> Face092
  Symmetric = false
FEATURE [Part::Revolution] Revolve101  label="removeToCreateScrewAndThreadedInsertHole028"
  Angle = 360
  Axis = (0,1,0)
  Base = (0,0,0)
  FaceMakerClass = Part::FaceMakerBullseye
  Placement = pos=(30.3,30.3,19.7) rot=(0,0,1;0rad)
  Solid = false
  Source = -> Face093
  Symmetric = false
FEATURE [Part::Revolution] Revolve102  label="removeToCreateScrewAndThreadedInsertHole029"
  Angle = 360
  Axis = (0,1,0)
  Base = (0,0,0)
  FaceMakerClass = Part::FaceMakerBullseye
  Placement = pos=(30.3,30.3,51.7) rot=(0,0,1;0rad)
  Solid = false
  Source = -> Face094
  Symmetric = false
FEATURE [Part::MultiFuse] Fusion068  label="createThreadedInsertHolesForFan002"
  Shapes = -> [Revolve099,Revolve100,Revolve101,Revolve102]
FEATURE [Part::Cut] Cut026  label="fanScrewHousing003"
  Base = -> Fusion067
  Tool = -> Fusion068
FEATURE [Sketcher::SketchObject] Sketch048
  FullyConstrained = false
  Placement = pos=(0,0,0) rot=(1,0,0;1.5708rad)
  sketch-geometry (24):
    g0: ArcOfCircle CenterX=-4 CenterY=-10.5 CenterZ=0 NormalX=0 NormalY=0 NormalZ=1 AngleXU=0 Radius=1.5 StartAngle=6e-16 EndAngle=3.14159
    g1: ArcOfCircle CenterX=-34.2 CenterY=-10.5 CenterZ=0 NormalX=0 NormalY=0 NormalZ=1 AngleXU=0 Radius=1.5 StartAngle=0 EndAngle=3.14159
    g2: ArcOfCircle CenterX=-34.2 CenterY=-27.7 CenterZ=0 NormalX=0 NormalY=0 NormalZ=1 AngleXU=0 Radius=1.5 StartAngle=3.14159 EndAngle=6.28319
    g3: ArcOfCircle CenterX=-4 CenterY=-27.7 CenterZ=0 NormalX=0 NormalY=0 NormalZ=1 AngleXU=0 Radius=1.5 StartAngle=3.1416 EndAngle=6.28319
    g4: ArcOfCircle CenterX=-10 CenterY=-4.3 CenterZ=0 NormalX=0 NormalY=0 NormalZ=1 AngleXU=0 Radius=1.5 StartAngle=2e-16 EndAngle=3.14159
    g5: ArcOfCircle CenterX=-16.1 CenterY=-1.8 CenterZ=0 NormalX=0 NormalY=0 NormalZ=1 AngleXU=0 Radius=1.5 StartAngle=5e-16 EndAngle=3.14159
    g6: ArcOfCircle CenterX=-22.1 CenterY=-1.8 CenterZ=0 NormalX=0 NormalY=0 NormalZ=1 AngleXU=0 Radius=1.5 StartAngle=5e-16 EndAngle=3.14159
    g7: ArcOfCircle CenterX=-28.2 CenterY=-4.3 CenterZ=0 NormalX=0 NormalY=0 NormalZ=1 AngleXU=0 Radius=1.5 StartAngle=2e-16 EndAngle=3.14159
    g8: ArcOfCircle CenterX=-10 CenterY=-33.9 CenterZ=0 NormalX=0 NormalY=0 NormalZ=1 AngleXU=0 Radius=1.5 StartAngle=3.14159 EndAngle=6.28319
    g9: ArcOfCircle CenterX=-16.1 CenterY=-36.4 CenterZ=0 NormalX=0 NormalY=0 NormalZ=1 AngleXU=0 Radius=1.5 StartAngle=3.14159 EndAngle=6.28319
    g10: ArcOfCircle CenterX=-22.1 CenterY=-36.4 CenterZ=0 NormalX=0 NormalY=0 NormalZ=1 AngleXU=0 Radius=1.5 StartAngle=3.14159 EndAngle=6.28319
    g11: ArcOfCircle CenterX=-28.2 CenterY=-33.9 CenterZ=0 NormalX=0 NormalY=0 NormalZ=1 AngleXU=0 Radius=1.5 StartAngle=3.14159 EndAngle=6.28319
    g12: LineSegment StartX=-35.7 StartY=-10.5 StartZ=0 EndX=-35.7 EndY=-27.7 EndZ=0
    g13: LineSegment StartX=-32.7 StartY=-10.5 StartZ=0 EndX=-32.7 EndY=-27.7 EndZ=0
    g14: LineSegment StartX=-29.7 StartY=-33.9 StartZ=0 EndX=-29.7 EndY=-4.3 EndZ=0
    g15: LineSegment StartX=-26.7 StartY=-33.9 StartZ=0 EndX=-26.7 EndY=-4.3 EndZ=0
    g16: LineSegment StartX=-2.5 StartY=-10.5 StartZ=0 EndX=-2.5 EndY=-27.7 EndZ=0
    g17: LineSegment StartX=-8.5 StartY=-4.3 StartZ=0 EndX=-8.5 EndY=-33.9 EndZ=0
    g18: LineSegment StartX=-5.5 StartY=-10.5 StartZ=0 EndX=-5.5 EndY=-27.7 EndZ=0
    g19: LineSegment StartX=-11.5 StartY=-4.3 StartZ=0 EndX=-11.5 EndY=-33.9 EndZ=0
    g20: LineSegment StartX=-14.6 StartY=-1.8 StartZ=0 EndX=-14.6 EndY=-36.4 EndZ=0
    g21: LineSegment StartX=-17.6 StartY=-1.8 StartZ=0 EndX=-17.6 EndY=-36.4 EndZ=0
    g22: LineSegment StartX=-20.6 StartY=-36.4 StartZ=0 EndX=-20.6 EndY=-1.8 EndZ=0
    g23: LineSegment StartX=-23.6 StartY=-1.8 StartZ=0 EndX=-23.6 EndY=-36.4 EndZ=0
  constraints (48):
    c: Block(g0)
    c: Block(g1)
    c: Block(g2)
    c: Block(g3)
    c: Block(g4)
    c: Block(g5)
    c: Block(g6)
    c: Block(g7)
    c: Block(g8)
    c: Block(g9)
    c: Block(g10)
    c: Block(g11)
    c: Coincident(g12,g1)
    c: Coincident(g12,g2)
    c: Vertical(g12)
    c: Coincident(g13,g1)
    c: Coincident(g13,g2)
    c: Vertical(g13)
    c: Coincident(g14,g11)
    c: Coincident(g14,g7)
    c: Vertical(g14)
    c: Coincident(g15,g11)
    c: Coincident(g15,g7)
    c: Vertical(g15)
    c: Coincident(g16,g0)
    c: Coincident(g16,g3)
    c: Vertical(g16)
    c: Coincident(g17,g4)
    c: Coincident(g17,g8)
    c: Vertical(g17)
    c: Coincident(g18,g0)
    c: Coincident(g18,g3)
    c: Vertical(g18)
    c: Coincident(g19,g4)
    c: Coincident(g19,g8)
    c: Vertical(g19)
    c: Coincident(g20,g5)
    c: Coincident(g20,g9)
    c: Vertical(g20)
    c: Coincident(g21,g5)
    c: Coincident(g21,g9)
    c: Vertical(g21)
    c: Coincident(g22,g10)
    c: Coincident(g22,g6)
    c: Vertical(g22)
    c: Coincident(g23,g6)
    c: Coincident(g23,g10)
    c: Vertical(g23)
FEATURE [Part::Extrusion] Extrude039  label="removeToCreateFanGrillHoles002"
  Base = -> Sketch048
  Dir = (0,-1,6e-16)
  DirMode = 2
  FaceMakerClass = Part::FaceMakerBullseye
  LengthFwd = 10
  LengthRev = 0
  Placement = pos=(65.4,44,54.82) rot=(0,0,1;0rad)
  Solid = true
  Symmetric = false
FEATURE [Part::Cut] Cut027  label="fanScrewHousing004"
  Base = -> Cut026
  Tool = -> Extrude038
FEATURE [Part::Cut] Cut028  label="top014"
  Base = -> Fillet026
  Tool = -> Extrude039
FEATURE [Part::Feature] Face095 .. Face098  x4 (patterned run collapsed; names and placements below)
  shape: bbox 3.5 x 17.8 x 2e-07 mm, 1 faces, 0 solids (baked)
FEATURE [Part::Revolution] Revolve103  label="removeToCreateScrewAndThreadedInsertHole030"
  Angle = 360
  Axis = (0,1,0)
  Base = (0,0,0)
  FaceMakerClass = Part::FaceMakerBullseye
  Placement = pos=(62.3,30.3,19.7) rot=(0,0,1;0rad)
  Solid = false
  Source = -> Face095
  Symmetric = false
FEATURE [Part::Revolution] Revolve104  label="removeToCreateScrewAndThreadedInsertHole031"
  Angle = 360
  Axis = (0,1,0)
  Base = (0,0,0)
  FaceMakerClass = Part::FaceMakerBullseye
  Placement = pos=(62.3,30.3,51.7) rot=(0,0,1;0rad)
  Solid = false
  Source = -> Face096
  Symmetric = false
FEATURE [Part::Revolution] Revolve105  label="removeToCreateScrewAndThreadedInsertHole032"
  Angle = 360
  Axis = (0,1,0)
  Base = (0,0,0)
  FaceMakerClass = Part::FaceMakerBullseye
  Placement = pos=(30.3,30.3,19.7) rot=(0,0,1;0rad)
  Solid = false
  Source = -> Face097
  Symmetric = false
FEATURE [Part::Revolution] Revolve106  label="removeToCreateScrewAndThreadedInsertHole033"
  Angle = 360
  Axis = (0,1,0)
  Base = (0,0,0)
  FaceMakerClass = Part::FaceMakerBullseye
  Placement = pos=(30.3,30.3,51.7) rot=(0,0,1;0rad)
  Solid = false
  Source = -> Face098
  Symmetric = false
FEATURE [Part::MultiFuse] Fusion069  label="createThreadedInsertHolesForFan003"
  Shapes = -> [Revolve103,Revolve104,Revolve105,Revolve106]
FEATURE [Part::Cut] Cut029  label="top015"
  Base = -> Cut028
  Tool = -> Fusion054
FEATURE [Part::Cut] Cut030  label="fanScrewHousing005"
  Base = -> Cut027
  Tool = -> Fusion069
FEATURE [Part::Cylinder] Cylinder026  label="removeToCreteHoleForPlugHousing010"
  Angle = 360
  AttacherType = Attacher::AttachEngine3D
  Height = 20
  Placement = pos=(-2,19,36) rot=(0,1,0;1.5708rad)
  Radius = 14.3
FEATURE [Part::Box] Box018  label="removeToCreteHoleForPlugHousing011"
  AttacherType = Attacher::AttachEngine3D
  Height = 28.6
  Length = 10
  Placement = pos=(-2,0,21.7) rot=(0,0,1;0rad)
  Width = 19
FEATURE [Part::Box] Box019  label="wireHolderBottomCaseBit"
  AttacherType = Attacher::AttachEngine3D
  Height = 28
  Length = 3
  Placement = pos=(0,0,22) rot=(0,0,1;0rad)
  Width = 21
FEATURE [Part::Cylinder] Cylinder027  label="removeToCreteHoleForPlugHousing012"
  Angle = 360
  AttacherType = Attacher::AttachEngine3D
  Height = 20
  Placement = pos=(-2,19,36) rot=(0,1,0;1.5708rad)
  Radius = 14.3
FEATURE [Part::Cut] Cut031  label="wireHolderBottomCaseBit001"
  Base = -> Box019
  Tool = -> Cylinder027
FEATURE [Part::MultiFuse] Fusion070  label="removeToCreteHoleForPlugHousing013"
  Shapes = -> [Box018,Cylinder026]
FEATURE [Part::Cut] Cut032  label="top016"
  Base = -> Cut029
  Tool = -> Fusion070
FEATURE [Part::Cylinder] Cylinder028
  Angle = 360
  AttacherType = Attacher::AttachEngine3D
  Height = 20
  Placement = pos=(0,0,36.15) rot=(0,0,1;0rad)
  Radius = 14.3
FEATURE [Part::Cylinder] Cylinder029
  Angle = 360
  AttacherType = Attacher::AttachEngine3D
  Height = 10
  Placement = pos=(0,0,36.15) rot=(0,0,1;0rad)
  Radius = 4
FEATURE [Part::MultiFuse] Fusion071  label="removeToCreteHoleForPlugHousing014"
  Placement = pos=(70,19,36) rot=(0,1,0;1.5708rad)
  Shapes = -> [Cylinder028,Cylinder029]
FEATURE [Sketcher::SketchObject] Sketch049  label="topSketch011"
  FullyConstrained = true
  sketch-geometry (4):
    g0: ArcOfCircle CenterX=105 CenterY=19 CenterZ=0 NormalX=0 NormalY=0 NormalZ=1 AngleXU=0 Radius=20.6155 StartAngle=5.54125 EndAngle=6.28319
    g1: ArcOfCircle CenterX=105 CenterY=19 CenterZ=0 NormalX=0 NormalY=0 NormalZ=1 AngleXU=0 Radius=13 StartAngle=5.54125 EndAngle=6.28319
    g2: LineSegment StartX=118 StartY=19 StartZ=0 EndX=125.616 EndY=19 EndZ=0
    g3: LineSegment StartX=114.583 StartY=10.2157 StartZ=0 EndX=120.197 EndY=5.06982 EndZ=0
  constraints (7):
    c: Block(g0)
    c: Block(g1)
    c: Coincident(g2,g1)
    c: Coincident(g2,g0)
    c: Horizontal(g2)
    c: Coincident(g3,g1)
    c: Coincident(g3,g0)
FEATURE [Part::Box] Box020  label="removeToCreteHoleForPlugHousing015"
  AttacherType = Attacher::AttachEngine3D
  Height = 28.6
  Length = 20
  Placement = pos=(106.15,0,21.7) rot=(0,0,1;0rad)
  Width = 19
FEATURE [Part::MultiFuse] Fusion072  label="removeToCreteHoleForPlugHousing016"
  Shapes = -> [Box020,Fusion071]
FEATURE [Part::Cut] Cut033  label="removeToCreteHoleForPlugHousing017"
  Base = -> Cut032
  Tool = -> Fusion072
FEATURE [Part::Cylinder] Cylinder030
  Angle = 360
  AttacherType = Attacher::AttachEngine3D
  Height = 20
  Placement = pos=(0,0,36.15) rot=(0,0,1;0rad)
  Radius = 14.3
FEATURE [Part::Cylinder] Cylinder031
  Angle = 360
  AttacherType = Attacher::AttachEngine3D
  Height = 10
  Placement = pos=(0,0,36.15) rot=(0,0,1;0rad)
  Radius = 4
FEATURE [Part::Box] Box021  label="removeToCreteHoleForPlugHousing019"
  AttacherType = Attacher::AttachEngine3D
  Height = 28.6
  Length = 20
  Placement = pos=(106.15,0,21.7) rot=(0,0,1;0rad)
  Width = 19
FEATURE [Part::MultiFuse] Fusion074  label="removeToCreteHoleForPlugHousing020"
  Placement = pos=(70,19,36) rot=(0,1,0;1.5708rad)
  Shapes = -> [Cylinder030,Cylinder031]
FEATURE [Part::MultiFuse] Fusion073  label="removeToCreteHoleForPlugHousing018"
  Placement = pos=(0,0,28.3) rot=(0,0,1;0rad)
  Shapes = -> [Box021,Fusion074]
FEATURE [Part::Cylinder] Cylinder032
  Angle = 360
  AttacherType = Attacher::AttachEngine3D
  Height = 20
  Placement = pos=(0,0,36.15) rot=(0,0,1;0rad)
  Radius = 14.3
FEATURE [Part::Cylinder] Cylinder033
  Angle = 360
  AttacherType = Attacher::AttachEngine3D
  Height = 10
  Placement = pos=(0,0,36.15) rot=(0,0,1;0rad)
  Radius = 4
FEATURE [Part::Box] Box022  label="removeToCreteHoleForPlugHousing021"
  AttacherType = Attacher::AttachEngine3D
  Height = 28.6
  Length = 20
  Placement = pos=(106.15,0,21.7) rot=(0,0,1;0rad)
  Width = 19
FEATURE [Part::MultiFuse] Fusion076  label="removeToCreteHoleForPlugHousing023"
  Placement = pos=(70,19,36) rot=(0,1,0;1.5708rad)
  Shapes = -> [Cylinder032,Cylinder033]
FEATURE [Part::MultiFuse] Fusion075  label="removeToCreteHoleForPlugHousing022"
  Placement = pos=(0,0,-28.3) rot=(0,0,1;0rad)
  Shapes = -> [Box022,Fusion076]
FEATURE [Part::MultiFuse] Fusion077  label="removeToCreatePlugHousingBottomBit"
  Shapes = -> [Fusion075,Fusion073]
FEATURE [Part::Cylinder] Cylinder034
  Angle = 360
  AttacherType = Attacher::AttachEngine3D
  Height = 20
  Placement = pos=(0,0,36.15) rot=(0,0,1;0rad)
  Radius = 14
FEATURE [Part::Cylinder] Cylinder035
  Angle = 360
  AttacherType = Attacher::AttachEngine3D
  Height = 10
  Placement = pos=(0,0,36.15) rot=(0,0,1;0rad)
  Radius = 4
FEATURE [Part::MultiFuse] Fusion078  label="removeToCreteHoleForPlugHousing024"
  Placement = pos=(70,19,36) rot=(0,1,0;1.5708rad)
  Shapes = -> [Cylinder034,Cylinder035]
FEATURE [Part::MultiFuse] Fusion079  label="removeToCreatePlugHousingBottomBit001"
  Shapes = -> [Fusion078,Fusion077]
FEATURE [Part::Extrusion] Extrude040  label="bottomPlugHousingBit"
  Base = -> Sketch049
  Dir = (0,0,1)
  DirMode = 2
  FaceMakerClass = Part::FaceMakerBullseye
  LengthFwd = 72
  LengthRev = 0
  Solid = true
  Symmetric = false
FEATURE [Part::Cut] Cut034  label="bottomPlugHousingBit001"
  Base = -> Extrude040
  Placement = pos=(-0.09,0,0) rot=(0,0,1;0rad)
  Tool = -> Fusion079
FEATURE [Part::Box] Box023  label="Cube014"
  AttacherType = Attacher::AttachEngine3D
  Height = 16
  Length = 8
  Placement = pos=(12.7,31.52,28) rot=(0,0,1;0rad)
  Width = 4
FEATURE [Part::Cylinder] Cylinder036
  Angle = 360
  AttacherType = Attacher::AttachEngine3D
  Height = 10
  Placement = pos=(0,0,36.15) rot=(0,0,1;0rad)
  Radius = 4
FEATURE [Part::Cylinder] Cylinder037
  Angle = 360
  AttacherType = Attacher::AttachEngine3D
  Height = 20
  Placement = pos=(0,0,36.15) rot=(0,0,1;0rad)
  Radius = 8.2
FEATURE [Part::MultiFuse] Fusion080  label="removeToCreteHoleForPlugHousing025"
  Placement = pos=(-42,19,36) rot=(0,1,0;1.5708rad)
  Shapes = -> [Cylinder037,Cylinder036]
FEATURE [Sketcher::SketchObject] Sketch050  label="topSketch012"
  FullyConstrained = true
  sketch-geometry (4):
    g0: LineSegment StartX=16.8446 StartY=31.512 StartZ=0 EndX=16.3251 EndY=34.4666 EndZ=0
    g1: ArcOfCircle CenterX=19 CenterY=19.2524 CenterZ=0 NormalX=0 NormalY=0 NormalZ=1 AngleXU=0 Radius=15.4476 StartAngle=1.74483 EndAngle=2.72717
    g2: ArcOfCircle CenterX=19 CenterY=19.2524 CenterZ=0 NormalX=0 NormalY=0 NormalZ=1 AngleXU=0 Radius=12.4476 StartAngle=1.74483 EndAngle=2.73189
    g3: LineSegment StartX=4.86004 StartY=25.4725 StartZ=0 EndX=7.58253 EndY=24.2107 EndZ=0
  constraints (7):
    c: Block(g0)
    c: Coincident(g1,g0)
    c: Coincident(g2,g0)
    c: Coincident(g3,g1)
    c: Coincident(g3,g2)
    c: Block(g1)
    c: Block(g2)
FEATURE [Part::Extrusion] Extrude041
  Base = -> Sketch050
  Dir = (0,0,1)
  DirMode = 2
  FaceMakerClass = Part::FaceMakerBullseye
  LengthFwd = 10.6
  LengthRev = 0
  Placement = pos=(0,0,31) rot=(0,0,1;0rad)
  Solid = true
  Symmetric = false
FEATURE [Part::Cut] Cut035
  Base = -> Extrude041
  Placement = pos=(0,0,-0.3) rot=(0,0,1;0rad)
  Tool = -> Fusion080
FEATURE [Part::Cut] Cut036
  Base = -> Box023
  Tool = -> Cut035
FEATURE [Part::Fillet] Fillet027
  Base = -> Cut036
  Edges = 1 edges r=0.7: [Edge13]
FEATURE [Part::Fillet] Fillet028
  Base = -> Fillet027
  Edges = 1 edges r=0.7: [Edge13]
FEATURE [Part::Fillet] Fillet029
  Base = -> Fillet028
  Edges = 1 edges r=0.7: [Edge16]
FEATURE [Part::Fillet] Fillet030
  Base = -> Fillet029
  Edges = 1 edges r=0.7: [Edge11]
FEATURE [Part::Fillet] Fillet031
  Base = -> Fillet030
  Edges = 1 edges r=0.7: [Edge10]
FEATURE [Part::Fillet] Fillet032
  Base = -> Fillet031
  Edges = 1 edges r=1.2: [Edge5]
FEATURE [Part::Fillet] Fillet033
  Base = -> Fillet032
  Edges = 1 edges r=1.2: [Edge12]
FEATURE [Part::Fillet] Fillet034  label="wireHousingRetainer"
  Base = -> Fillet033
  Edges = 1 edges r=2: [Edge1]
  Placement = pos=(0.3,0,0) rot=(0,0,1;0rad)
FEATURE [Part::Feature] Face099
  shape: bbox 3.5 x 17.8 x 2e-07 mm, 1 faces, 0 solids (baked)
FEATURE [Part::Revolution] Revolve107  label="removeToCreateScrewAndThreadedInsertHole034"
  Angle = 360
  Axis = (0,1,0)
  Base = (0,0,0)
  FaceMakerClass = Part::FaceMakerBullseye
  Placement = pos=(12.5,0,10) rot=(0,0,1;0rad)
  Solid = false
  Source = -> Face099
  Symmetric = false
FEATURE [Part::Feature] Face100
  shape: bbox 3.5 x 17.8 x 2e-07 mm, 1 faces, 0 solids (baked)
FEATURE [Part::Revolution] Revolve108  label="removeToCreateScrewAndThreadedInsertHole035"
  Angle = 360
  Axis = (0,1,0)
  Base = (0,0,0)
  FaceMakerClass = Part::FaceMakerBullseye
  Placement = pos=(12.5,0,62) rot=(0,0,1;0rad)
  Solid = false
  Source = -> Face100
  Symmetric = false
FEATURE [Part::Feature] Face101
  shape: bbox 3.5 x 17.8 x 2e-07 mm, 1 faces, 0 solids (baked)
FEATURE [Part::Revolution] Revolve109  label="removeToCreateScrewAndThreadedInsertHole036"
  Angle = 360
  Axis = (0,1,0)
  Base = (0,0,0)
  FaceMakerClass = Part::FaceMakerBullseye
  Placement = pos=(89.5,0,68.5) rot=(0,0,1;0rad)
  Solid = false
  Source = -> Face101
  Symmetric = false
FEATURE [Part::Feature] Face102
  shape: bbox 3.5 x 17.8 x 2e-07 mm, 1 faces, 0 solids (baked)
FEATURE [Part::Revolution] Revolve110  label="removeToCreateScrewAndThreadedInsertHole037"
  Angle = 360
  Axis = (0,1,0)
  Base = (0,0,0)
  FaceMakerClass = Part::FaceMakerBullseye
  Placement = pos=(89.5,0,3.5) rot=(0,0,1;0rad)
  Solid = false
  Source = -> Face102
  Symmetric = false
FEATURE [Part::Feature] Face103
  shape: bbox 3.5 x 17.8 x 2e-07 mm, 1 faces, 0 solids (baked)
FEATURE [Part::Revolution] Revolve111  label="removeToCreateScrewAndThreadedInsertHole038"
  Angle = 360
  Axis = (0,1,0)
  Base = (0,0,0)
  FaceMakerClass = Part::FaceMakerBullseye
  Placement = pos=(109.5,4.7,3.5) rot=(0,0,1;0rad)
  Solid = false
  Source = -> Face103
  Symmetric = false
FEATURE [Part::Feature] Face104
  shape: bbox 3.5 x 17.8 x 2e-07 mm, 1 faces, 0 solids (baked)
FEATURE [Part::Revolution] Revolve112  label="removeToCreateScrewAndThreadedInsertHole039"
  Angle = 360
  Axis = (0,1,0)
  Base = (0,0,0)
  FaceMakerClass = Part::FaceMakerBullseye
  Placement = pos=(109.5,4.7,68.5) rot=(0,0,1;0rad)
  Solid = false
  Source = -> Face104
  Symmetric = false
FEATURE [Part::MultiFuse] Fusion081  label="removeToCreateScrewAndThreadedInsertHole040"
  Shapes = -> [Revolve107,Revolve108,Revolve109,Revolve110,Revolve111,Revolve112]
FEATURE [Part::MultiFuse] Fusion082  label="casePillars002"
  Shapes = -> [Revolve094,Revolve092,Revolve090,Revolve089,Revolve091,Revolve093]
FEATURE [Part::Cut] Cut037  label="casePillars003"
  Base = -> Fusion082
  Tool = -> Fusion081
FEATURE [Sketcher::SketchObject] Sketch051
  FullyConstrained = true
  Placement = pos=(117,19,0) rot=(0.57735,0.57735,0.57735;2.0944rad)
  sketch-geometry (48):
    g0: LineSegment StartX=-49.19 StartY=69.25 StartZ=0 EndX=-49.19 EndY=66.25 EndZ=0
    g1: LineSegment StartX=-49.19 StartY=63.5 StartZ=0 EndX=-49.19 EndY=60.5 EndZ=0
    g2: LineSegment StartX=-49.19 StartY=57.75 StartZ=0 EndX=-49.19 EndY=54.75 EndZ=0
    g3: LineSegment StartX=-49.19 StartY=52 StartZ=0 EndX=-49.19 EndY=49 EndZ=0
    g4: LineSegment StartX=-49.19 StartY=46.25 StartZ=0 EndX=-49.19 EndY=43.25 EndZ=0
    g5: LineSegment StartX=-49.19 StartY=40.5 StartZ=0 EndX=-49.19 EndY=37.5 EndZ=0
    g6: LineSegment StartX=-49.19 StartY=34.5 StartZ=0 EndX=-49.19 EndY=31.5 EndZ=0
    g7: LineSegment StartX=-49.19 StartY=28.75 StartZ=0 EndX=-49.19 EndY=25.75 EndZ=0
    g8: LineSegment StartX=-49.19 StartY=23 StartZ=0 EndX=-49.19 EndY=20 EndZ=0
    g9: LineSegment StartX=-49.19 StartY=17.25 StartZ=0 EndX=-49.19 EndY=14.25 EndZ=0
    g10: LineSegment StartX=-49.19 StartY=11.5 StartZ=0 EndX=-49.19 EndY=8.5 EndZ=0
    g11: LineSegment StartX=-49.19 StartY=5.75 StartZ=0 EndX=-49.19 EndY=2.75 EndZ=0
    g12: ArcOfCircle CenterX=-1.5 CenterY=67.75 CenterZ=0 NormalX=0 NormalY=0 NormalZ=1 AngleXU=0 Radius=1.5 StartAngle=4.71239 EndAngle=7.85398
    g13: ArcOfCircle CenterX=-1.5 CenterY=62 CenterZ=0 NormalX=0 NormalY=0 NormalZ=1 AngleXU=0 Radius=1.5 StartAngle=4.71239 EndAngle=7.85398
    g14: ArcOfCircle CenterX=-1.5 CenterY=56.25 CenterZ=0 NormalX=0 NormalY=0 NormalZ=1 AngleXU=0 Radius=1.5 StartAngle=4.71239 EndAngle=7.85398
    g15: ArcOfCircle CenterX=-11.49 CenterY=50.5 CenterZ=0 NormalX=0 NormalY=0 NormalZ=1 AngleXU=0 Radius=1.5 StartAngle=4.71239 EndAngle=7.85398
    g16: ArcOfCircle CenterX=-16.28 CenterY=44.75 CenterZ=0 NormalX=0 NormalY=0 NormalZ=1 AngleXU=0 Radius=1.5 StartAngle=4.71239 EndAngle=7.85398
    g17: ArcOfCircle CenterX=-18.2337 CenterY=39 CenterZ=0 NormalX=0 NormalY=0 NormalZ=1 AngleXU=0 Radius=1.5 StartAngle=4.71485 EndAngle=7.85398
    g18: ArcOfCircle CenterX=-16.2837 CenterY=27.25 CenterZ=0 NormalX=0 NormalY=0 NormalZ=1 AngleXU=0 Radius=1.5 StartAngle=4.71485 EndAngle=7.85398
    g19: ArcOfCircle CenterX=-18.2337 CenterY=33 CenterZ=0 NormalX=0 NormalY=0 NormalZ=1 AngleXU=0 Radius=1.5 StartAngle=4.71485 EndAngle=7.85398
    g20: ArcOfCircle CenterX=-11.49 CenterY=21.5 CenterZ=0 NormalX=0 NormalY=0 NormalZ=1 AngleXU=0 Radius=1.5 StartAngle=4.71239 EndAngle=7.85398
    g21: ArcOfCircle CenterX=-1.5 CenterY=4.25 CenterZ=0 NormalX=0 NormalY=0 NormalZ=1 AngleXU=0 Radius=1.5 StartAngle=4.71239 EndAngle=7.85398
    g22: ArcOfCircle CenterX=-1.5 CenterY=10 CenterZ=0 NormalX=0 NormalY=0 NormalZ=1 AngleXU=0 Radius=1.5 StartAngle=4.71239 EndAngle=7.85398
    g23: ArcOfCircle CenterX=-1.5 CenterY=15.75 CenterZ=0 NormalX=0 NormalY=0 NormalZ=1 AngleXU=0 Radius=1.5 StartAngle=4.71239 EndAngle=7.85398
    g24: LineSegment StartX=-49.19 StartY=69.25 StartZ=0 EndX=-1.5 EndY=69.25 EndZ=0
    g25: LineSegment StartX=-49.19 StartY=66.25 StartZ=0 EndX=-1.5 EndY=66.25 EndZ=0
    g26: LineSegment StartX=-49.19 StartY=63.5 StartZ=0 EndX=-1.5 EndY=63.5 EndZ=0
    g27: LineSegment StartX=-49.19 StartY=60.5 StartZ=0 EndX=-1.5 EndY=60.5 EndZ=0
    g28: LineSegment StartX=-49.19 StartY=57.75 StartZ=0 EndX=-1.5 EndY=57.75 EndZ=0
    g29: LineSegment StartX=-49.19 StartY=54.75 StartZ=0 EndX=-1.5 EndY=54.75 EndZ=0
    g30: LineSegment StartX=-49.19 StartY=52 StartZ=0 EndX=-11.49 EndY=52 EndZ=0
    g31: LineSegment StartX=-49.19 StartY=49 StartZ=0 EndX=-11.49 EndY=49 EndZ=0
    g32: LineSegment StartX=-49.19 StartY=46.25 StartZ=0 EndX=-16.28 EndY=46.25 EndZ=0
    g33: LineSegment StartX=-49.19 StartY=43.25 StartZ=0 EndX=-16.28 EndY=43.25 EndZ=0
    g34: LineSegment StartX=-49.19 StartY=40.5 StartZ=0 EndX=-18.2337 EndY=40.5 EndZ=0
    g35: LineSegment StartX=-49.19 StartY=37.5 StartZ=0 EndX=-18.23 EndY=37.5 EndZ=0
    g36: LineSegment StartX=-49.19 StartY=34.5 StartZ=0 EndX=-18.2337 EndY=34.5 EndZ=0
    g37: LineSegment StartX=-49.19 StartY=31.5 StartZ=0 EndX=-18.23 EndY=31.5 EndZ=0
    g38: LineSegment StartX=-49.19 StartY=28.75 StartZ=0 EndX=-16.2837 EndY=28.75 EndZ=0
    g39: LineSegment StartX=-49.19 StartY=25.75 StartZ=0 EndX=-16.28 EndY=25.75 EndZ=0
    g40: LineSegment StartX=-49.19 StartY=23 StartZ=0 EndX=-11.49 EndY=23 EndZ=0
    g41: LineSegment StartX=-49.19 StartY=20 StartZ=0 EndX=-11.49 EndY=20 EndZ=0
    g42: LineSegment StartX=-49.19 StartY=17.25 StartZ=0 EndX=-1.5 EndY=17.25 EndZ=0
    g43: LineSegment StartX=-49.19 StartY=14.25 StartZ=0 EndX=-1.5 EndY=14.25 EndZ=0
    g44: LineSegment StartX=-49.19 StartY=11.5 StartZ=0 EndX=-1.5 EndY=11.5 EndZ=0
    g45: LineSegment StartX=-49.19 StartY=8.5 StartZ=0 EndX=-1.5 EndY=8.5 EndZ=0
    g46: LineSegment StartX=-49.19 StartY=5.75 StartZ=0 EndX=-1.5 EndY=5.75 EndZ=0
    g47: LineSegment StartX=-49.19 StartY=2.75 StartZ=0 EndX=-1.5 EndY=2.75 EndZ=0
  constraints (120):
    c: Vertical(g0)
    c: Distance(g0) = 3
    c: Block(g0)
    c: Vertical(g1)
    c: Distance(g1) = 3
    c: Vertical(g2)
    c: Equal(g0,g2) = 3
    c: Block(g2)
    c: Vertical(g3)
    c: Equal(g1,g3) = 3
    c: Vertical(g4)
    c: Equal(g0,g4) = 3
    c: Block(g4)
    c: Vertical(g5)
    c: Equal(g1,g5) = 3
    c: Vertical(g6)
    c: Equal(g0,g6) = 3
    c: Block(g6)
    c: Vertical(g7)
    c: Equal(g1,g7) = 3
    c: Vertical(g8)
    c: Equal(g0,g8) = 3
    c: Block(g8)
    c: Vertical(g9)
    c: Equal(g1,g9) = 3
    c: Vertical(g10)
    c: Equal(g0,g10) = 3
    c: Block(g10)
    c: Vertical(g11)
    c: Equal(g1,g11) = 3
    c: Block(g12)
    c: Block(g13)
    c: Block(g14)
    c: Block(g15)
    c: Block(g16)
    c: Block(g17)
    c: Block(g18)
    c: Block(g19)
    c: Block(g20)
    c: Block(g21)
    c: Block(g22)
    c: Block(g23)
    c: Block(g11)
    c: Block(g9)
    c: Block(g7)
    c: Block(g5)
    c: Block(g3)
    c: Block(g1)
    c: Coincident(g24,g0)
    c: Coincident(g24,g12)
    c: Horizontal(g24)
    c: Coincident(g25,g0)
    c: Coincident(g25,g12)
    c: Horizontal(g25)
    c: Coincident(g26,g1)
    c: Coincident(g26,g13)
    c: Horizontal(g26)
    c: Coincident(g27,g1)
    c: Coincident(g27,g13)
    c: Horizontal(g27)
    c: Coincident(g28,g2)
    c: Coincident(g28,g14)
    c: Horizontal(g28)
    c: Coincident(g29,g2)
    c: Coincident(g29,g14)
    c: Horizontal(g29)
    c: Coincident(g30,g3)
    c: Coincident(g30,g15)
    c: Horizontal(g30)
    c: Coincident(g31,g3)
    c: Coincident(g31,g15)
    c: Horizontal(g31)
    c: Coincident(g32,g4)
    c: Coincident(g32,g16)
    c: Horizontal(g32)
    c: Coincident(g33,g4)
    c: Coincident(g33,g16)
    c: Horizontal(g33)
    c: Coincident(g34,g5)
    c: Coincident(g34,g17)
    c: Horizontal(g34)
    c: Coincident(g35,g5)
    c: Coincident(g35,g17)
    c: Horizontal(g35)
    c: Coincident(g36,g6)
    c: Coincident(g36,g19)
    c: Horizontal(g36)
    c: Coincident(g37,g6)
    c: Coincident(g37,g19)
    c: Horizontal(g37)
    c: Coincident(g38,g7)
    c: Coincident(g38,g18)
    c: Horizontal(g38)
    c: Coincident(g39,g7)
    c: Coincident(g39,g18)
    c: Horizontal(g39)
    c: Coincident(g40,g8)
    c: Coincident(g40,g20)
    c: Horizontal(g40)
    c: Coincident(g41,g8)
    c: Coincident(g41,g20)
    c: Horizontal(g41)
    c: Coincident(g42,g9)
    c: Coincident(g42,g23)
    c: Horizontal(g42)
    c: Coincident(g43,g9)
    c: Coincident(g43,g23)
    c: Horizontal(g43)
    c: Coincident(g44,g10)
    c: Coincident(g44,g22)
    c: Horizontal(g44)
    c: Coincident(g45,g10)
    c: Coincident(g45,g22)
    c: Horizontal(g45)
    c: Coincident(g46,g11)
    c: Coincident(g46,g21)
    c: Horizontal(g46)
    c: Coincident(g47,g11)
    c: Coincident(g47,g21)
    c: Horizontal(g47)
FEATURE [Part::Extrusion] Extrude042
  Base = -> Sketch051
  Dir = (1,-2e-16,2e-16)
  DirMode = 2
  FaceMakerClass = Part::FaceMakerBullseye
  LengthFwd = 19
  LengthRev = 0
  Placement = pos=(-19,0,0) rot=(0,0,1;0rad)
  Solid = true
  Symmetric = false
FEATURE [Part::Fillet] Fillet035  label="removeToCreateVentalationHoles"
  Base = -> Extrude042
  Edges = <same value as first occurrence — deduplicated (x6 in doc)>
  Placement = pos=(7,0,0) rot=(0,0,1;0rad)
FEATURE [Part::Cut] Cut038  label="top017"
  Base = -> Cut033
  Tool = -> Fillet035
FEATURE [Sketcher::SketchObject] Sketch052  label="bottomSketch001"
  FullyConstrained = true
  sketch-geometry (45):
    g0: LineSegment StartX=6.29999 StartY=8 StartZ=0 EndX=3.29999 EndY=8 EndZ=0
    g1: LineSegment StartX=3.29999 StartY=8 StartZ=0 EndX=3.29999 EndY=-6.03275e-07 EndZ=0
    g2: ArcOfCircle CenterX=8.29999 CenterY=5 CenterZ=0 NormalX=0 NormalY=0 NormalZ=1 AngleXU=0 Radius=2 StartAngle=3.14159 EndAngle=4.71239
    g3: LineSegment StartX=6.29999 StartY=8 StartZ=0 EndX=6.29999 EndY=5 EndZ=0
    g4: ArcOfCircle CenterX=105 CenterY=19 CenterZ=0 NormalX=0 NormalY=0 NormalZ=1 AngleXU=0 Radius=12.7 StartAngle=4.71239 EndAngle=5.94289
    g5-g11: Circle x7 (B-spline internal-alignment scaffolding for g12; pole/knot coordinates omitted)
    g12: BSplineCurve PolesCount=7 KnotsCount=5 Degree=3 IsPeriodic=0
    g13-g17: GeomPoint x5 (B-spline internal-alignment scaffolding for g12; pole/knot coordinates omitted)
    g18: ArcOfCircle CenterX=105 CenterY=19 CenterZ=0 NormalX=0 NormalY=0 NormalZ=1 AngleXU=0 Radius=15.7 StartAngle=5.81226 EndAngle=6.28319
    g19: BSplineCurve PolesCount=5 KnotsCount=3 Degree=3 IsPeriodic=0
    g20: LineSegment StartX=8.29999 StartY=3 StartZ=0 EndX=101.7 EndY=3 EndZ=0
    g21: LineSegment StartX=3.29999 StartY=-6.03275e-07 StartZ=0 EndX=105 EndY=-6.03275e-07 EndZ=0
    g22: LineSegment StartX=120.974 StartY=8.71251 StartZ=0 EndX=122.332 EndY=7.83778 EndZ=0
    g23: LineSegment StartX=105 StartY=-6.03274e-07 StartZ=0 EndX=113 EndY=-6.03274e-07 EndZ=0
    g24: ArcOfCircle CenterX=105 CenterY=19 CenterZ=0 NormalX=0 NormalY=0 NormalZ=1 AngleXU=0 Radius=20.6155 StartAngle=5.11091 EndAngle=5.71103
    g25: ArcOfCircle CenterX=117.7 CenterY=19 CenterZ=0 NormalX=0 NormalY=0 NormalZ=1 AngleXU=0 Radius=3 StartAngle=1.2e-15 EndAngle=2.10468
    g26: Circle CenterX=116.345 CenterY=16.3232 CenterZ=0 NormalX=0 NormalY=0 NormalZ=1 AngleXU=0 Radius=1
    g27: Circle CenterX=117.24 CenterY=15.7584 CenterZ=0 NormalX=0 NormalY=0 NormalZ=1 AngleXU=0 Radius=1
    g28: Circle CenterX=116.972 CenterY=14.7612 CenterZ=0 NormalX=0 NormalY=0 NormalZ=1 AngleXU=0 Radius=1
    g29: BSplineCurve PolesCount=3 KnotsCount=2 Degree=2 IsPeriodic=0
    g30: GeomPoint X=116.345 Y=16.3232 Z=0
    g31: GeomPoint X=116.972 Y=14.7612 Z=0
    g32: Circle CenterX=115.828 CenterY=17.157 CenterZ=0 NormalX=0 NormalY=0 NormalZ=1 AngleXU=0 Radius=1
    g33: Circle CenterX=115.841 CenterY=16.639 CenterZ=0 NormalX=0 NormalY=0 NormalZ=1 AngleXU=0 Radius=1
    g34: Circle CenterX=116.345 CenterY=16.3232 CenterZ=0 NormalX=0 NormalY=0 NormalZ=1 AngleXU=0 Radius=1
    g35: BSplineCurve PolesCount=3 KnotsCount=2 Degree=2 IsPeriodic=0
    g36: GeomPoint X=115.828 Y=17.157 Z=0
    g37: GeomPoint X=116.345 Y=16.3232 Z=0
    g38: LineSegment StartX=115.828 StartY=17.157 StartZ=0 EndX=115.828 EndY=20.8307 EndZ=0
    g39: Circle CenterX=115.828 CenterY=20.8307 CenterZ=0 NormalX=0 NormalY=0 NormalZ=1 AngleXU=0 Radius=1
    g40: Circle CenterX=115.831 CenterY=21.3396 CenterZ=0 NormalX=0 NormalY=0 NormalZ=1 AngleXU=0 Radius=1
    g41: Circle CenterX=116.173 CenterY=21.5825 CenterZ=0 NormalX=0 NormalY=0 NormalZ=1 AngleXU=0 Radius=1
    g42: BSplineCurve PolesCount=3 KnotsCount=2 Degree=2 IsPeriodic=0
    g43: GeomPoint X=115.828 Y=20.8307 Z=0
    g44: GeomPoint X=116.173 Y=21.5825 Z=0
  constraints (70):
    c: Horizontal(g0)
    c: Distance(g0) = 3
    c: Coincident(g1,g0)
    c: Vertical(g1)
    c: Block(g2)
    c: Block(g0)
    c: Coincident(g3,g0)
    c: Coincident(g3,g2)
    c: Vertical(g3)
    c: Block(g1)
    c: Block(g4)
    c: Coincident(g19,g4)
    c: Block(g19)
    c: Equal(g5, g6-g11) x6
    c: InternalAlignment(g5-g11 -> g12) x7
    c: InternalAlignment(g13-g17 -> g12) x5
    c: Block(g12)
    c: Coincident(g18,g12)
    c: Block(g18)
    c: Coincident(g20,g2)
    c: Coincident(g20,g19)
    c: Horizontal(g20)
    c: Distance(g20) = 93.4
    c: Coincident(g21,g1)
    c: Horizontal(g21)
    c: Distance(g21) = 101.7
    c: Horizontal(g23)
    c: Distance(g23) = 8
    c: Coincident(g24,g23)
    c: Block(g23)
    c: Coincident(g22,g24)
    c: Block(g24)
    c: Block(g22)
    c: Distance(g22) = 1.61553
    c: Coincident(g25,g18)
    c: Block(g25)
    c: Weight(g26) = 1
    c: Equal(g26,g27)
    c: Equal(g26,g28)
    c: Coincident(g29,g4)
    c: InternalAlignment(g26,g29)
    c: InternalAlignment(g27,g29)
    c: InternalAlignment(g28,g29)
    c: InternalAlignment(g30,g29)
    c: InternalAlignment(g31,g29)
    c: Block(g29)
    c: Weight(g32) = 1
    c: Equal(g32,g33)
    c: Equal(g32,g34)
    c: Coincident(g35,g29)
    c: InternalAlignment(g32,g35)
    c: InternalAlignment(g33,g35)
    c: InternalAlignment(g34,g35)
    c: InternalAlignment(g36,g35)
    c: InternalAlignment(g37,g35)
    c: Block(g35)
    c: Coincident(g38,g35)
    c: Vertical(g38)
    c: Block(g38)
    c: Coincident(g42,g38)
    c: Weight(g39) = 1
    c: Equal(g39,g40)
    c: Equal(g39,g41)
    c: Coincident(g42,g25)
    c: InternalAlignment(g39,g42)
    c: InternalAlignment(g40,g42)
    c: InternalAlignment(g41,g42)
    c: InternalAlignment(g43,g42)
    c: InternalAlignment(g44,g42)
    c: Block(g42)
FEATURE [Part::Extrusion] Extrude043  label="bottom010"
  Base = -> Sketch052
  Dir = (0,0,1)
  DirMode = 2
  FaceMakerClass = Part::FaceMakerBullseye
  LengthFwd = 71.4
  LengthRev = 0
  Placement = pos=(0,0,0.3) rot=(0,0,1;0rad)
  Solid = true
  Symmetric = false
FEATURE [Sketcher::SketchObject] Sketch053  label="topSketch013"
  FullyConstrained = true
  sketch-geometry (22):
    g0: LineSegment StartX=5.21097e-06 StartY=3 StartZ=0 EndX=5.21097e-06 EndY=19 EndZ=0
    g1: ArcOfCircle CenterX=19 CenterY=19 CenterZ=0 NormalX=0 NormalY=0 NormalZ=1 AngleXU=0 Radius=19 StartAngle=1.5708 EndAngle=3.14159
    g2: ArcOfCircle CenterX=19 CenterY=19 CenterZ=0 NormalX=0 NormalY=0 NormalZ=1 AngleXU=0 Radius=16 StartAngle=1.5708 EndAngle=3.14159
    g3: LineSegment StartX=114 StartY=35 StartZ=0 EndX=19 EndY=35 EndZ=0
    g4: LineSegment StartX=5.21097e-06 StartY=3 StartZ=0 EndX=5.21097e-06 EndY=0 EndZ=0
    g5: LineSegment StartX=3 StartY=0 StartZ=0 EndX=5.21097e-06 EndY=0 EndZ=0
    g6: LineSegment StartX=3 StartY=19 StartZ=0 EndX=3 EndY=0 EndZ=0
    g7: LineSegment StartX=19 StartY=38 StartZ=0 EndX=124 EndY=38 EndZ=0
    g8: Circle CenterX=119 CenterY=35 CenterZ=0 NormalX=0 NormalY=0 NormalZ=1 AngleXU=0 Radius=1
    g9: Circle CenterX=121 CenterY=35 CenterZ=0 NormalX=0 NormalY=0 NormalZ=1 AngleXU=0 Radius=1
    g10: Circle CenterX=121 CenterY=33 CenterZ=0 NormalX=0 NormalY=0 NormalZ=1 AngleXU=0 Radius=1
    g11: BSplineCurve PolesCount=3 KnotsCount=2 Degree=2 IsPeriodic=0
    g12: GeomPoint X=119 Y=35 Z=0
    g13: GeomPoint X=121 Y=33 Z=0
    g14: LineSegment StartX=119 StartY=35 StartZ=0 EndX=114 EndY=35 EndZ=0
    g15: ArcOfCircle CenterX=105 CenterY=19 CenterZ=0 NormalX=0 NormalY=0 NormalZ=1 AngleXU=0 Radius=16 StartAngle=5.60905 EndAngle=6.28319
    g16: LineSegment StartX=121 StartY=33 StartZ=0 EndX=121 EndY=19 EndZ=0
    g17: LineSegment StartX=117.5 StartY=9.01251 StartZ=0 EndX=121.163 EndY=9.0125 EndZ=0
    g18: ArcOfCircle CenterX=105 CenterY=19 CenterZ=0 NormalX=0 NormalY=0 NormalZ=1 AngleXU=0 Radius=20.6155 StartAngle=5.7297 EndAngle=6.28319
    g19: LineSegment StartX=121.163 StartY=9.0125 StartZ=0 EndX=122.538 EndY=8.16329 EndZ=0
    g20: LineSegment StartX=124 StartY=38 StartZ=0 EndX=125.616 EndY=38 EndZ=0
    g21: LineSegment StartX=125.616 StartY=19 StartZ=0 EndX=125.616 EndY=38 EndZ=0
  constraints (50):
    c: Vertical(g0)
    c: Block(g0)
    c: Coincident(g1,g0)
    c: Block(g1)
    c: Coincident(g2,g1)
    c: Block(g2)
    c: Coincident(g3,g2)
    c: Horizontal(g3)
    c: Tangent(g3,g2)
    c: Coincident(g4,g0)
    c: Distance(g4) = 3
    c: Vertical(g4)
    c: Coincident(g5,g4)
    c: Horizontal(g5)
    c: Coincident(g6,g2)
    c: Coincident(g6,g5)
    c: Vertical(g6)
    c: Horizontal(g7)
    c: Distance(g7) = 105
    c: Coincident(g7,g1)
    c: Block(g3)
    c: Weight(g8) = 1
    c: Equal(g8,g9)
    c: Equal(g8,g10)
    c: InternalAlignment(g8,g11)
    c: InternalAlignment(g9,g11)
    c: InternalAlignment(g10,g11)
    c: InternalAlignment(g12,g11)
    c: InternalAlignment(g13,g11)
    c: Block(g11)
    c: Coincident(g14,g11)
    c: Coincident(g14,g3)
    c: Horizontal(g14)
    c: Block(g15)
    c: Coincident(g16,g11)
    c: Coincident(g16,g15)
    c: Vertical(g16)
    c: Distance(g16) = 14
    c: Coincident(g17,g15)
    c: Block(g18)
    c: Coincident(g19,g18)
    c: Coincident(g20,g7)
    c: Horizontal(g20)
    c: Vertical(g21)
    c: Coincident(g20,g21)
    c: Block(g20)
    c: Block(g21)
    c: Block(g19)
    c: Block(g17)
    c: Distance(g20) = 1.61553
FEATURE [Part::Extrusion] Extrude044
  Base = -> Sketch053
  Dir = (0,0,1)
  DirMode = 2
  FaceMakerClass = Part::FaceMakerBullseye
  LengthFwd = 72
  LengthRev = 0
  Solid = true
  Symmetric = false
FEATURE [Part::Fillet] Fillet036  label="top018"
  Base = -> Extrude044
  Edges = 1 edges r=2: [Edge41]
FEATURE [Sketcher::SketchObject] Sketch054
  FullyConstrained = false
  Placement = pos=(0,0,0) rot=(1,0,0;1.5708rad)
  sketch-geometry (24):
    g0: ArcOfCircle CenterX=-4 CenterY=-10.5 CenterZ=0 NormalX=0 NormalY=0 NormalZ=1 AngleXU=0 Radius=1.5 StartAngle=6e-16 EndAngle=3.14159
    g1: ArcOfCircle CenterX=-34.2 CenterY=-10.5 CenterZ=0 NormalX=0 NormalY=0 NormalZ=1 AngleXU=0 Radius=1.5 StartAngle=0 EndAngle=3.14159
    g2: ArcOfCircle CenterX=-34.2 CenterY=-27.7 CenterZ=0 NormalX=0 NormalY=0 NormalZ=1 AngleXU=0 Radius=1.5 StartAngle=3.14159 EndAngle=6.28319
    g3: ArcOfCircle CenterX=-4 CenterY=-27.7 CenterZ=0 NormalX=0 NormalY=0 NormalZ=1 AngleXU=0 Radius=1.5 StartAngle=3.1416 EndAngle=6.28319
    g4: ArcOfCircle CenterX=-10 CenterY=-4.3 CenterZ=0 NormalX=0 NormalY=0 NormalZ=1 AngleXU=0 Radius=1.5 StartAngle=2e-16 EndAngle=3.14159
    g5: ArcOfCircle CenterX=-16.1 CenterY=-1.8 CenterZ=0 NormalX=0 NormalY=0 NormalZ=1 AngleXU=0 Radius=1.5 StartAngle=5e-16 EndAngle=3.14159
    g6: ArcOfCircle CenterX=-22.1 CenterY=-1.8 CenterZ=0 NormalX=0 NormalY=0 NormalZ=1 AngleXU=0 Radius=1.5 StartAngle=5e-16 EndAngle=3.14159
    g7: ArcOfCircle CenterX=-28.2 CenterY=-4.3 CenterZ=0 NormalX=0 NormalY=0 NormalZ=1 AngleXU=0 Radius=1.5 StartAngle=2e-16 EndAngle=3.14159
    g8: ArcOfCircle CenterX=-10 CenterY=-33.9 CenterZ=0 NormalX=0 NormalY=0 NormalZ=1 AngleXU=0 Radius=1.5 StartAngle=3.14159 EndAngle=6.28319
    g9: ArcOfCircle CenterX=-16.1 CenterY=-36.4 CenterZ=0 NormalX=0 NormalY=0 NormalZ=1 AngleXU=0 Radius=1.5 StartAngle=3.14159 EndAngle=6.28319
    g10: ArcOfCircle CenterX=-22.1 CenterY=-36.4 CenterZ=0 NormalX=0 NormalY=0 NormalZ=1 AngleXU=0 Radius=1.5 StartAngle=3.14159 EndAngle=6.28319
    g11: ArcOfCircle CenterX=-28.2 CenterY=-33.9 CenterZ=0 NormalX=0 NormalY=0 NormalZ=1 AngleXU=0 Radius=1.5 StartAngle=3.14159 EndAngle=6.28319
    g12: LineSegment StartX=-35.7 StartY=-10.5 StartZ=0 EndX=-35.7 EndY=-27.7 EndZ=0
    g13: LineSegment StartX=-32.7 StartY=-10.5 StartZ=0 EndX=-32.7 EndY=-27.7 EndZ=0
    g14: LineSegment StartX=-29.7 StartY=-33.9 StartZ=0 EndX=-29.7 EndY=-4.3 EndZ=0
    g15: LineSegment StartX=-26.7 StartY=-33.9 StartZ=0 EndX=-26.7 EndY=-4.3 EndZ=0
    g16: LineSegment StartX=-2.5 StartY=-10.5 StartZ=0 EndX=-2.5 EndY=-27.7 EndZ=0
    g17: LineSegment StartX=-8.5 StartY=-4.3 StartZ=0 EndX=-8.5 EndY=-33.9 EndZ=0
    g18: LineSegment StartX=-5.5 StartY=-10.5 StartZ=0 EndX=-5.5 EndY=-27.7 EndZ=0
    g19: LineSegment StartX=-11.5 StartY=-4.3 StartZ=0 EndX=-11.5 EndY=-33.9 EndZ=0
    g20: LineSegment StartX=-14.6 StartY=-1.8 StartZ=0 EndX=-14.6 EndY=-36.4 EndZ=0
    g21: LineSegment StartX=-17.6 StartY=-1.8 StartZ=0 EndX=-17.6 EndY=-36.4 EndZ=0
    g22: LineSegment StartX=-20.6 StartY=-36.4 StartZ=0 EndX=-20.6 EndY=-1.8 EndZ=0
    g23: LineSegment StartX=-23.6 StartY=-1.8 StartZ=0 EndX=-23.6 EndY=-36.4 EndZ=0
  constraints (48):
    c: Block(g0)
    c: Block(g1)
    c: Block(g2)
    c: Block(g3)
    c: Block(g4)
    c: Block(g5)
    c: Block(g6)
    c: Block(g7)
    c: Block(g8)
    c: Block(g9)
    c: Block(g10)
    c: Block(g11)
    c: Coincident(g12,g1)
    c: Coincident(g12,g2)
    c: Vertical(g12)
    c: Coincident(g13,g1)
    c: Coincident(g13,g2)
    c: Vertical(g13)
    c: Coincident(g14,g11)
    c: Coincident(g14,g7)
    c: Vertical(g14)
    c: Coincident(g15,g11)
    c: Coincident(g15,g7)
    c: Vertical(g15)
    c: Coincident(g16,g0)
    c: Coincident(g16,g3)
    c: Vertical(g16)
    c: Coincident(g17,g4)
    c: Coincident(g17,g8)
    c: Vertical(g17)
    c: Coincident(g18,g0)
    c: Coincident(g18,g3)
    c: Vertical(g18)
    c: Coincident(g19,g4)
    c: Coincident(g19,g8)
    c: Vertical(g19)
    c: Coincident(g20,g5)
    c: Coincident(g20,g9)
    c: Vertical(g20)
    c: Coincident(g21,g5)
    c: Coincident(g21,g9)
    c: Vertical(g21)
    c: Coincident(g22,g10)
    c: Coincident(g22,g6)
    c: Vertical(g22)
    c: Coincident(g23,g6)
    c: Coincident(g23,g10)
    c: Vertical(g23)
FEATURE [Part::Extrusion] Extrude045  label="removeToCreateFanGrillHoles003"
  Base = -> Sketch054
  Dir = (0,-1,6e-16)
  DirMode = 2
  FaceMakerClass = Part::FaceMakerBullseye
  LengthFwd = 10
  LengthRev = 0
  Placement = pos=(65.4,44,54.82) rot=(0,0,1;0rad)
  Solid = true
  Symmetric = false
FEATURE [Part::Feature] Face105 .. Face108  x4 (patterned run collapsed; names and placements below)
  shape: bbox 3.5 x 17.8 x 2e-07 mm, 1 faces, 0 solids (baked)
FEATURE [Part::Revolution] Revolve113  label="removeToCreateScrewAndThreadedInsertHole041"
  Angle = 360
  Axis = (0,1,0)
  Base = (0,0,0)
  FaceMakerClass = Part::FaceMakerBullseye
  Placement = pos=(62.3,30.3,19.7) rot=(0,0,1;0rad)
  Solid = false
  Source = -> Face105
  Symmetric = false
FEATURE [Part::Revolution] Revolve114  label="removeToCreateScrewAndThreadedInsertHole042"
  Angle = 360
  Axis = (0,1,0)
  Base = (0,0,0)
  FaceMakerClass = Part::FaceMakerBullseye
  Placement = pos=(62.3,30.3,51.7) rot=(0,0,1;0rad)
  Solid = false
  Source = -> Face106
  Symmetric = false
FEATURE [Part::Revolution] Revolve115  label="removeToCreateScrewAndThreadedInsertHole043"
  Angle = 360
  Axis = (0,1,0)
  Base = (0,0,0)
  FaceMakerClass = Part::FaceMakerBullseye
  Placement = pos=(30.3,30.3,19.7) rot=(0,0,1;0rad)
  Solid = false
  Source = -> Face107
  Symmetric = false
FEATURE [Part::Revolution] Revolve116  label="removeToCreateScrewAndThreadedInsertHole044"
  Angle = 360
  Axis = (0,1,0)
  Base = (0,0,0)
  FaceMakerClass = Part::FaceMakerBullseye
  Placement = pos=(30.3,30.3,51.7) rot=(0,0,1;0rad)
  Solid = false
  Source = -> Face108
  Symmetric = false
FEATURE [Part::MultiFuse] Fusion083  label="createThreadedInsertHolesForFan004"
  Shapes = -> [Revolve113,Revolve114,Revolve115,Revolve116]
FEATURE [Part::Box] Box024  label="removeToCreteHoleForPlugHousing026"
  AttacherType = Attacher::AttachEngine3D
  Height = 28.6
  Length = 10
  Placement = pos=(-2,0,21.7) rot=(0,0,1;0rad)
  Width = 19
FEATURE [Part::Cylinder] Cylinder038  label="removeToCreteHoleForPlugHousing027"
  Angle = 360
  AttacherType = Attacher::AttachEngine3D
  Height = 20
  Placement = pos=(-2,19,36) rot=(0,1,0;1.5708rad)
  Radius = 14.3
FEATURE [Part::MultiFuse] Fusion084  label="removeToCreteHoleForPlugHousing028"
  Shapes = -> [Box024,Cylinder038]
FEATURE [Part::Cylinder] Cylinder039
  Angle = 360
  AttacherType = Attacher::AttachEngine3D
  Height = 20
  Placement = pos=(0,0,36.15) rot=(0,0,1;0rad)
  Radius = 14.3
FEATURE [Part::Cylinder] Cylinder040
  Angle = 360
  AttacherType = Attacher::AttachEngine3D
  Height = 10
  Placement = pos=(0,0,36.15) rot=(0,0,1;0rad)
  Radius = 4
FEATURE [Part::Box] Box025  label="removeToCreteHoleForPlugHousing030"
  AttacherType = Attacher::AttachEngine3D
  Height = 28.6
  Length = 20
  Placement = pos=(106.15,0,21.7) rot=(0,0,1;0rad)
  Width = 19
FEATURE [Part::MultiFuse] Fusion086  label="removeToCreteHoleForPlugHousing031"
  Placement = pos=(70,19,36) rot=(0,1,0;1.5708rad)
  Shapes = -> [Cylinder039,Cylinder040]
FEATURE [Part::MultiFuse] Fusion085  label="removeToCreteHoleForPlugHousing029"
  Shapes = -> [Box025,Fusion086]
FEATURE [Sketcher::SketchObject] Sketch055
  FullyConstrained = true
  Placement = pos=(117,19,0) rot=(0.57735,0.57735,0.57735;2.0944rad)
  sketch-geometry (48):
    g0: LineSegment StartX=-49.19 StartY=69.25 StartZ=0 EndX=-49.19 EndY=66.25 EndZ=0
    g1: LineSegment StartX=-49.19 StartY=63.5 StartZ=0 EndX=-49.19 EndY=60.5 EndZ=0
    g2: LineSegment StartX=-49.19 StartY=57.75 StartZ=0 EndX=-49.19 EndY=54.75 EndZ=0
    g3: LineSegment StartX=-49.19 StartY=52 StartZ=0 EndX=-49.19 EndY=49 EndZ=0
    g4: LineSegment StartX=-49.19 StartY=46.25 StartZ=0 EndX=-49.19 EndY=43.25 EndZ=0
    g5: LineSegment StartX=-49.19 StartY=40.5 StartZ=0 EndX=-49.19 EndY=37.5 EndZ=0
    g6: LineSegment StartX=-49.19 StartY=34.5 StartZ=0 EndX=-49.19 EndY=31.5 EndZ=0
    g7: LineSegment StartX=-49.19 StartY=28.75 StartZ=0 EndX=-49.19 EndY=25.75 EndZ=0
    g8: LineSegment StartX=-49.19 StartY=23 StartZ=0 EndX=-49.19 EndY=20 EndZ=0
    g9: LineSegment StartX=-49.19 StartY=17.25 StartZ=0 EndX=-49.19 EndY=14.25 EndZ=0
    g10: LineSegment StartX=-49.19 StartY=11.5 StartZ=0 EndX=-49.19 EndY=8.5 EndZ=0
    g11: LineSegment StartX=-49.19 StartY=5.75 StartZ=0 EndX=-49.19 EndY=2.75 EndZ=0
    g12: ArcOfCircle CenterX=-1.5 CenterY=67.75 CenterZ=0 NormalX=0 NormalY=0 NormalZ=1 AngleXU=0 Radius=1.5 StartAngle=4.71239 EndAngle=7.85398
    g13: ArcOfCircle CenterX=-1.5 CenterY=62 CenterZ=0 NormalX=0 NormalY=0 NormalZ=1 AngleXU=0 Radius=1.5 StartAngle=4.71239 EndAngle=7.85398
    g14: ArcOfCircle CenterX=-1.5 CenterY=56.25 CenterZ=0 NormalX=0 NormalY=0 NormalZ=1 AngleXU=0 Radius=1.5 StartAngle=4.71239 EndAngle=7.85398
    g15: ArcOfCircle CenterX=-11.49 CenterY=50.5 CenterZ=0 NormalX=0 NormalY=0 NormalZ=1 AngleXU=0 Radius=1.5 StartAngle=4.71239 EndAngle=7.85398
    g16: ArcOfCircle CenterX=-16.28 CenterY=44.75 CenterZ=0 NormalX=0 NormalY=0 NormalZ=1 AngleXU=0 Radius=1.5 StartAngle=4.71239 EndAngle=7.85398
    g17: ArcOfCircle CenterX=-18.2337 CenterY=39 CenterZ=0 NormalX=0 NormalY=0 NormalZ=1 AngleXU=0 Radius=1.5 StartAngle=4.71485 EndAngle=7.85398
    g18: ArcOfCircle CenterX=-16.2837 CenterY=27.25 CenterZ=0 NormalX=0 NormalY=0 NormalZ=1 AngleXU=0 Radius=1.5 StartAngle=4.71485 EndAngle=7.85398
    g19: ArcOfCircle CenterX=-18.2337 CenterY=33 CenterZ=0 NormalX=0 NormalY=0 NormalZ=1 AngleXU=0 Radius=1.5 StartAngle=4.71485 EndAngle=7.85398
    g20: ArcOfCircle CenterX=-11.49 CenterY=21.5 CenterZ=0 NormalX=0 NormalY=0 NormalZ=1 AngleXU=0 Radius=1.5 StartAngle=4.71239 EndAngle=7.85398
    g21: ArcOfCircle CenterX=-1.5 CenterY=4.25 CenterZ=0 NormalX=0 NormalY=0 NormalZ=1 AngleXU=0 Radius=1.5 StartAngle=4.71239 EndAngle=7.85398
    g22: ArcOfCircle CenterX=-1.5 CenterY=10 CenterZ=0 NormalX=0 NormalY=0 NormalZ=1 AngleXU=0 Radius=1.5 StartAngle=4.71239 EndAngle=7.85398
    g23: ArcOfCircle CenterX=-1.5 CenterY=15.75 CenterZ=0 NormalX=0 NormalY=0 NormalZ=1 AngleXU=0 Radius=1.5 StartAngle=4.71239 EndAngle=7.85398
    g24: LineSegment StartX=-49.19 StartY=69.25 StartZ=0 EndX=-1.5 EndY=69.25 EndZ=0
    g25: LineSegment StartX=-49.19 StartY=66.25 StartZ=0 EndX=-1.5 EndY=66.25 EndZ=0
    g26: LineSegment StartX=-49.19 StartY=63.5 StartZ=0 EndX=-1.5 EndY=63.5 EndZ=0
    g27: LineSegment StartX=-49.19 StartY=60.5 StartZ=0 EndX=-1.5 EndY=60.5 EndZ=0
    g28: LineSegment StartX=-49.19 StartY=57.75 StartZ=0 EndX=-1.5 EndY=57.75 EndZ=0
    g29: LineSegment StartX=-49.19 StartY=54.75 StartZ=0 EndX=-1.5 EndY=54.75 EndZ=0
    g30: LineSegment StartX=-49.19 StartY=52 StartZ=0 EndX=-11.49 EndY=52 EndZ=0
    g31: LineSegment StartX=-49.19 StartY=49 StartZ=0 EndX=-11.49 EndY=49 EndZ=0
    g32: LineSegment StartX=-49.19 StartY=46.25 StartZ=0 EndX=-16.28 EndY=46.25 EndZ=0
    g33: LineSegment StartX=-49.19 StartY=43.25 StartZ=0 EndX=-16.28 EndY=43.25 EndZ=0
    g34: LineSegment StartX=-49.19 StartY=40.5 StartZ=0 EndX=-18.2337 EndY=40.5 EndZ=0
    g35: LineSegment StartX=-49.19 StartY=37.5 StartZ=0 EndX=-18.23 EndY=37.5 EndZ=0
    g36: LineSegment StartX=-49.19 StartY=34.5 StartZ=0 EndX=-18.2337 EndY=34.5 EndZ=0
    g37: LineSegment StartX=-49.19 StartY=31.5 StartZ=0 EndX=-18.23 EndY=31.5 EndZ=0
    g38: LineSegment StartX=-49.19 StartY=28.75 StartZ=0 EndX=-16.2837 EndY=28.75 EndZ=0
    g39: LineSegment StartX=-49.19 StartY=25.75 StartZ=0 EndX=-16.28 EndY=25.75 EndZ=0
    g40: LineSegment StartX=-49.19 StartY=23 StartZ=0 EndX=-11.49 EndY=23 EndZ=0
    g41: LineSegment StartX=-49.19 StartY=20 StartZ=0 EndX=-11.49 EndY=20 EndZ=0
    g42: LineSegment StartX=-49.19 StartY=17.25 StartZ=0 EndX=-1.5 EndY=17.25 EndZ=0
    g43: LineSegment StartX=-49.19 StartY=14.25 StartZ=0 EndX=-1.5 EndY=14.25 EndZ=0
    g44: LineSegment StartX=-49.19 StartY=11.5 StartZ=0 EndX=-1.5 EndY=11.5 EndZ=0
    g45: LineSegment StartX=-49.19 StartY=8.5 StartZ=0 EndX=-1.5 EndY=8.5 EndZ=0
    g46: LineSegment StartX=-49.19 StartY=5.75 StartZ=0 EndX=-1.5 EndY=5.75 EndZ=0
    g47: LineSegment StartX=-49.19 StartY=2.75 StartZ=0 EndX=-1.5 EndY=2.75 EndZ=0
  constraints (120):
    c: Vertical(g0)
    c: Distance(g0) = 3
    c: Block(g0)
    c: Vertical(g1)
    c: Distance(g1) = 3
    c: Vertical(g2)
    c: Equal(g0,g2) = 3
    c: Block(g2)
    c: Vertical(g3)
    c: Equal(g1,g3) = 3
    c: Vertical(g4)
    c: Equal(g0,g4) = 3
    c: Block(g4)
    c: Vertical(g5)
    c: Equal(g1,g5) = 3
    c: Vertical(g6)
    c: Equal(g0,g6) = 3
    c: Block(g6)
    c: Vertical(g7)
    c: Equal(g1,g7) = 3
    c: Vertical(g8)
    c: Equal(g0,g8) = 3
    c: Block(g8)
    c: Vertical(g9)
    c: Equal(g1,g9) = 3
    c: Vertical(g10)
    c: Equal(g0,g10) = 3
    c: Block(g10)
    c: Vertical(g11)
    c: Equal(g1,g11) = 3
    c: Block(g12)
    c: Block(g13)
    c: Block(g14)
    c: Block(g15)
    c: Block(g16)
    c: Block(g17)
    c: Block(g18)
    c: Block(g19)
    c: Block(g20)
    c: Block(g21)
    c: Block(g22)
    c: Block(g23)
    c: Block(g11)
    c: Block(g9)
    c: Block(g7)
    c: Block(g5)
    c: Block(g3)
    c: Block(g1)
    c: Coincident(g24,g0)
    c: Coincident(g24,g12)
    c: Horizontal(g24)
    c: Coincident(g25,g0)
    c: Coincident(g25,g12)
    c: Horizontal(g25)
    c: Coincident(g26,g1)
    c: Coincident(g26,g13)
    c: Horizontal(g26)
    c: Coincident(g27,g1)
    c: Coincident(g27,g13)
    c: Horizontal(g27)
    c: Coincident(g28,g2)
    c: Coincident(g28,g14)
    c: Horizontal(g28)
    c: Coincident(g29,g2)
    c: Coincident(g29,g14)
    c: Horizontal(g29)
    c: Coincident(g30,g3)
    c: Coincident(g30,g15)
    c: Horizontal(g30)
    c: Coincident(g31,g3)
    c: Coincident(g31,g15)
    c: Horizontal(g31)
    c: Coincident(g32,g4)
    c: Coincident(g32,g16)
    c: Horizontal(g32)
    c: Coincident(g33,g4)
    c: Coincident(g33,g16)
    c: Horizontal(g33)
    c: Coincident(g34,g5)
    c: Coincident(g34,g17)
    c: Horizontal(g34)
    c: Coincident(g35,g5)
    c: Coincident(g35,g17)
    c: Horizontal(g35)
    c: Coincident(g36,g6)
    c: Coincident(g36,g19)
    c: Horizontal(g36)
    c: Coincident(g37,g6)
    c: Coincident(g37,g19)
    c: Horizontal(g37)
    c: Coincident(g38,g7)
    c: Coincident(g38,g18)
    c: Horizontal(g38)
    c: Coincident(g39,g7)
    c: Coincident(g39,g18)
    c: Horizontal(g39)
    c: Coincident(g40,g8)
    c: Coincident(g40,g20)
    c: Horizontal(g40)
    c: Coincident(g41,g8)
    c: Coincident(g41,g20)
    c: Horizontal(g41)
    c: Coincident(g42,g9)
    c: Coincident(g42,g23)
    c: Horizontal(g42)
    c: Coincident(g43,g9)
    c: Coincident(g43,g23)
    c: Horizontal(g43)
    c: Coincident(g44,g10)
    c: Coincident(g44,g22)
    c: Horizontal(g44)
    c: Coincident(g45,g10)
    c: Coincident(g45,g22)
    c: Horizontal(g45)
    c: Coincident(g46,g11)
    c: Coincident(g46,g21)
    c: Horizontal(g46)
    c: Coincident(g47,g11)
    c: Coincident(g47,g21)
    c: Horizontal(g47)
FEATURE [Part::Extrusion] Extrude046
  Base = -> Sketch055
  Dir = (1,0,0)
  DirMode = 2
  FaceMakerClass = Part::FaceMakerBullseye
  LengthFwd = 23
  LengthRev = 0
  Placement = pos=(-19,0,0) rot=(0,0,1;0rad)
  Solid = true
  Symmetric = false
FEATURE [Part::Fillet] Fillet038  label="removeToCreateVentalationHoles001"
  Base = -> Extrude046
  Edges = <same value as first occurrence — deduplicated (x6 in doc)>
  Placement = pos=(7,0,0) rot=(0,0,1;0rad)
FEATURE [Sketcher::SketchObject] Sketch056  label="topSketch014"
  FullyConstrained = true
  sketch-geometry (22):
    g0: LineSegment StartX=5.21097e-06 StartY=3 StartZ=0 EndX=5.21097e-06 EndY=19 EndZ=0
    g1: ArcOfCircle CenterX=19 CenterY=19 CenterZ=0 NormalX=0 NormalY=0 NormalZ=1 AngleXU=0 Radius=19 StartAngle=1.5708 EndAngle=3.14159
    g2: ArcOfCircle CenterX=19 CenterY=19 CenterZ=0 NormalX=0 NormalY=0 NormalZ=1 AngleXU=0 Radius=16 StartAngle=1.5708 EndAngle=3.14159
    g3: LineSegment StartX=114 StartY=35 StartZ=0 EndX=19 EndY=35 EndZ=0
    g4: LineSegment StartX=5.21097e-06 StartY=3 StartZ=0 EndX=5.21097e-06 EndY=0 EndZ=0
    g5: LineSegment StartX=3 StartY=0 StartZ=0 EndX=5.21097e-06 EndY=0 EndZ=0
    g6: LineSegment StartX=3 StartY=19 StartZ=0 EndX=3 EndY=0 EndZ=0
    g7: LineSegment StartX=19 StartY=38 StartZ=0 EndX=124 EndY=38 EndZ=0
    g8: Circle CenterX=119 CenterY=35 CenterZ=0 NormalX=0 NormalY=0 NormalZ=1 AngleXU=0 Radius=1
    g9: Circle CenterX=121 CenterY=35 CenterZ=0 NormalX=0 NormalY=0 NormalZ=1 AngleXU=0 Radius=1
    g10: Circle CenterX=121 CenterY=33 CenterZ=0 NormalX=0 NormalY=0 NormalZ=1 AngleXU=0 Radius=1
    g11: BSplineCurve PolesCount=3 KnotsCount=2 Degree=2 IsPeriodic=0
    g12: GeomPoint X=119 Y=35 Z=0
    g13: GeomPoint X=121 Y=33 Z=0
    g14: LineSegment StartX=119 StartY=35 StartZ=0 EndX=114 EndY=35 EndZ=0
    g15: ArcOfCircle CenterX=105 CenterY=19 CenterZ=0 NormalX=0 NormalY=0 NormalZ=1 AngleXU=0 Radius=16 StartAngle=5.60905 EndAngle=6.28319
    g16: LineSegment StartX=121 StartY=33 StartZ=0 EndX=121 EndY=19 EndZ=0
    g17: LineSegment StartX=117.5 StartY=9.01251 StartZ=0 EndX=121.163 EndY=9.0125 EndZ=0
    g18: ArcOfCircle CenterX=105 CenterY=19 CenterZ=0 NormalX=0 NormalY=0 NormalZ=1 AngleXU=0 Radius=20.6155 StartAngle=5.7297 EndAngle=6.28319
    g19: LineSegment StartX=121.163 StartY=9.0125 StartZ=0 EndX=122.538 EndY=8.16329 EndZ=0
    g20: LineSegment StartX=124 StartY=38 StartZ=0 EndX=125.616 EndY=38 EndZ=0
    g21: LineSegment StartX=125.616 StartY=19 StartZ=0 EndX=125.616 EndY=38 EndZ=0
  constraints (49):
    c: Vertical(g0)
    c: Block(g0)
    c: Coincident(g1,g0)
    c: Block(g1)
    c: Coincident(g2,g1)
    c: Block(g2)
    c: Coincident(g3,g2)
    c: Horizontal(g3)
    c: Tangent(g3,g2)
    c: Coincident(g4,g0)
    c: Distance(g4) = 3
    c: Vertical(g4)
    c: Coincident(g5,g4)
    c: Horizontal(g5)
    c: Coincident(g6,g2)
    c: Coincident(g6,g5)
    c: Vertical(g6)
    c: Horizontal(g7)
    c: Distance(g7) = 105
    c: Coincident(g7,g1)
    c: Block(g3)
    c: Weight(g8) = 1
    c: Equal(g8,g9)
    c: Equal(g8,g10)
    c: InternalAlignment(g8,g11)
    c: InternalAlignment(g9,g11)
    c: InternalAlignment(g10,g11)
    c: InternalAlignment(g12,g11)
    c: InternalAlignment(g13,g11)
    c: Block(g11)
    c: Coincident(g14,g11)
    c: Coincident(g14,g3)
    c: Horizontal(g14)
    c: Block(g15)
    c: Coincident(g16,g11)
    c: Coincident(g16,g15)
    c: Vertical(g16)
    c: Distance(g16) = 14
    c: Coincident(g17,g15)
    c: Block(g18)
    c: Coincident(g19,g18)
    c: Coincident(g20,g7)
    c: Horizontal(g20)
    c: Vertical(g21)
    c: Coincident(g20,g21)
    c: Block(g20)
    c: Block(g21)
    c: Block(g19)
    c: Block(g17)
FEATURE [Part::Box] Box026  label="removeToCreteHoleForPlugHousing032"
  AttacherType = Attacher::AttachEngine3D
  Height = 28.6
  Length = 10
  Placement = pos=(-2,0,21.7) rot=(0,0,1;0rad)
  Width = 19
FEATURE [Part::Feature] Face109 .. Face112  x4 (patterned run collapsed; names and placements below)
  shape: bbox 3.5 x 17.8 x 2e-07 mm, 1 faces, 0 solids (baked)
FEATURE [Part::Revolution] Revolve117  label="removeToCreateScrewAndThreadedInsertHole045"
  Angle = 360
  Axis = (0,1,0)
  Base = (0,0,0)
  FaceMakerClass = Part::FaceMakerBullseye
  Placement = pos=(62.3,30.3,19.7) rot=(0,0,1;0rad)
  Solid = false
  Source = -> Face109
  Symmetric = false
FEATURE [Part::Revolution] Revolve118  label="removeToCreateScrewAndThreadedInsertHole046"
  Angle = 360
  Axis = (0,1,0)
  Base = (0,0,0)
  FaceMakerClass = Part::FaceMakerBullseye
  Placement = pos=(62.3,30.3,51.7) rot=(0,0,1;0rad)
  Solid = false
  Source = -> Face110
  Symmetric = false
FEATURE [Part::Revolution] Revolve119  label="removeToCreateScrewAndThreadedInsertHole047"
  Angle = 360
  Axis = (0,1,0)
  Base = (0,0,0)
  FaceMakerClass = Part::FaceMakerBullseye
  Placement = pos=(30.3,30.3,19.7) rot=(0,0,1;0rad)
  Solid = false
  Source = -> Face111
  Symmetric = false
FEATURE [Part::Revolution] Revolve120  label="removeToCreateScrewAndThreadedInsertHole048"
  Angle = 360
  Axis = (0,1,0)
  Base = (0,0,0)
  FaceMakerClass = Part::FaceMakerBullseye
  Placement = pos=(30.3,30.3,51.7) rot=(0,0,1;0rad)
  Solid = false
  Source = -> Face112
  Symmetric = false
FEATURE [Part::MultiFuse] Fusion087  label="createThreadedInsertHolesForFan005"
  Shapes = -> [Revolve117,Revolve118,Revolve119,Revolve120]
FEATURE [Part::Extrusion] Extrude047
  Base = -> Sketch056
  Dir = (0,0,1)
  DirMode = 2
  FaceMakerClass = Part::FaceMakerBullseye
  LengthFwd = 72
  LengthRev = 0
  Solid = true
  Symmetric = false
FEATURE [Part::Fillet] Fillet039  label="top019"
  Base = -> Extrude047
  Edges = 1 edges r=2: [Edge35]
FEATURE [Sketcher::SketchObject] Sketch057
  FullyConstrained = false
  Placement = pos=(0,0,0) rot=(1,0,0;1.5708rad)
  sketch-geometry (24):
    g0: ArcOfCircle CenterX=-4 CenterY=-10.5 CenterZ=0 NormalX=0 NormalY=0 NormalZ=1 AngleXU=0 Radius=1.5 StartAngle=6e-16 EndAngle=3.14159
    g1: ArcOfCircle CenterX=-34.2 CenterY=-10.5 CenterZ=0 NormalX=0 NormalY=0 NormalZ=1 AngleXU=0 Radius=1.5 StartAngle=0 EndAngle=3.14159
    g2: ArcOfCircle CenterX=-34.2 CenterY=-27.7 CenterZ=0 NormalX=0 NormalY=0 NormalZ=1 AngleXU=0 Radius=1.5 StartAngle=3.14159 EndAngle=6.28319
    g3: ArcOfCircle CenterX=-4 CenterY=-27.7 CenterZ=0 NormalX=0 NormalY=0 NormalZ=1 AngleXU=0 Radius=1.5 StartAngle=3.1416 EndAngle=6.28319
    g4: ArcOfCircle CenterX=-10 CenterY=-4.3 CenterZ=0 NormalX=0 NormalY=0 NormalZ=1 AngleXU=0 Radius=1.5 StartAngle=2e-16 EndAngle=3.14159
    g5: ArcOfCircle CenterX=-16.1 CenterY=-1.8 CenterZ=0 NormalX=0 NormalY=0 NormalZ=1 AngleXU=0 Radius=1.5 StartAngle=5e-16 EndAngle=3.14159
    g6: ArcOfCircle CenterX=-22.1 CenterY=-1.8 CenterZ=0 NormalX=0 NormalY=0 NormalZ=1 AngleXU=0 Radius=1.5 StartAngle=5e-16 EndAngle=3.14159
    g7: ArcOfCircle CenterX=-28.2 CenterY=-4.3 CenterZ=0 NormalX=0 NormalY=0 NormalZ=1 AngleXU=0 Radius=1.5 StartAngle=2e-16 EndAngle=3.14159
    g8: ArcOfCircle CenterX=-10 CenterY=-33.9 CenterZ=0 NormalX=0 NormalY=0 NormalZ=1 AngleXU=0 Radius=1.5 StartAngle=3.14159 EndAngle=6.28319
    g9: ArcOfCircle CenterX=-16.1 CenterY=-36.4 CenterZ=0 NormalX=0 NormalY=0 NormalZ=1 AngleXU=0 Radius=1.5 StartAngle=3.14159 EndAngle=6.28319
    g10: ArcOfCircle CenterX=-22.1 CenterY=-36.4 CenterZ=0 NormalX=0 NormalY=0 NormalZ=1 AngleXU=0 Radius=1.5 StartAngle=3.14159 EndAngle=6.28319
    g11: ArcOfCircle CenterX=-28.2 CenterY=-33.9 CenterZ=0 NormalX=0 NormalY=0 NormalZ=1 AngleXU=0 Radius=1.5 StartAngle=3.14159 EndAngle=6.28319
    g12: LineSegment StartX=-35.7 StartY=-10.5 StartZ=0 EndX=-35.7 EndY=-27.7 EndZ=0
    g13: LineSegment StartX=-32.7 StartY=-10.5 StartZ=0 EndX=-32.7 EndY=-27.7 EndZ=0
    g14: LineSegment StartX=-29.7 StartY=-33.9 StartZ=0 EndX=-29.7 EndY=-4.3 EndZ=0
    g15: LineSegment StartX=-26.7 StartY=-33.9 StartZ=0 EndX=-26.7 EndY=-4.3 EndZ=0
    g16: LineSegment StartX=-2.5 StartY=-10.5 StartZ=0 EndX=-2.5 EndY=-27.7 EndZ=0
    g17: LineSegment StartX=-8.5 StartY=-4.3 StartZ=0 EndX=-8.5 EndY=-33.9 EndZ=0
    g18: LineSegment StartX=-5.5 StartY=-10.5 StartZ=0 EndX=-5.5 EndY=-27.7 EndZ=0
    g19: LineSegment StartX=-11.5 StartY=-4.3 StartZ=0 EndX=-11.5 EndY=-33.9 EndZ=0
    g20: LineSegment StartX=-14.6 StartY=-1.8 StartZ=0 EndX=-14.6 EndY=-36.4 EndZ=0
    g21: LineSegment StartX=-17.6 StartY=-1.8 StartZ=0 EndX=-17.6 EndY=-36.4 EndZ=0
    g22: LineSegment StartX=-20.6 StartY=-36.4 StartZ=0 EndX=-20.6 EndY=-1.8 EndZ=0
    g23: LineSegment StartX=-23.6 StartY=-1.8 StartZ=0 EndX=-23.6 EndY=-36.4 EndZ=0
  constraints (48):
    c: Block(g0)
    c: Block(g1)
    c: Block(g2)
    c: Block(g3)
    c: Block(g4)
    c: Block(g5)
    c: Block(g6)
    c: Block(g7)
    c: Block(g8)
    c: Block(g9)
    c: Block(g10)
    c: Block(g11)
    c: Coincident(g12,g1)
    c: Coincident(g12,g2)
    c: Vertical(g12)
    c: Coincident(g13,g1)
    c: Coincident(g13,g2)
    c: Vertical(g13)
    c: Coincident(g14,g11)
    c: Coincident(g14,g7)
    c: Vertical(g14)
    c: Coincident(g15,g11)
    c: Coincident(g15,g7)
    c: Vertical(g15)
    c: Coincident(g16,g0)
    c: Coincident(g16,g3)
    c: Vertical(g16)
    c: Coincident(g17,g4)
    c: Coincident(g17,g8)
    c: Vertical(g17)
    c: Coincident(g18,g0)
    c: Coincident(g18,g3)
    c: Vertical(g18)
    c: Coincident(g19,g4)
    c: Coincident(g19,g8)
    c: Vertical(g19)
    c: Coincident(g20,g5)
    c: Coincident(g20,g9)
    c: Vertical(g20)
    c: Coincident(g21,g5)
    c: Coincident(g21,g9)
    c: Vertical(g21)
    c: Coincident(g22,g10)
    c: Coincident(g22,g6)
    c: Vertical(g22)
    c: Coincident(g23,g6)
    c: Coincident(g23,g10)
    c: Vertical(g23)
FEATURE [Part::Extrusion] Extrude048  label="removeToCreateFanGrillHoles004"
  Base = -> Sketch057
  Dir = (0,-1,6e-16)
  DirMode = 2
  FaceMakerClass = Part::FaceMakerBullseye
  LengthFwd = 10
  LengthRev = 0
  Placement = pos=(65.4,44,54.82) rot=(0,0,1;0rad)
  Solid = true
  Symmetric = false
FEATURE [Part::Cut] Cut040  label="top021"
  Base = -> Fillet039
  Tool = -> Extrude048
FEATURE [Part::Cylinder] Cylinder041  label="removeToCreteHoleForPlugHousing034"
  Angle = 360
  AttacherType = Attacher::AttachEngine3D
  Height = 20
  Placement = pos=(-2,19,36) rot=(0,1,0;1.5708rad)
  Radius = 14.3
FEATURE [Part::MultiFuse] Fusion089  label="removeToCreteHoleForPlugHousing035"
  Shapes = -> [Box026,Cylinder041]
FEATURE [Part::Cylinder] Cylinder042
  Angle = 360
  AttacherType = Attacher::AttachEngine3D
  Height = 20
  Placement = pos=(0,0,36.15) rot=(0,0,1;0rad)
  Radius = 14.3
FEATURE [Part::Cylinder] Cylinder043
  Angle = 360
  AttacherType = Attacher::AttachEngine3D
  Height = 10
  Placement = pos=(0,0,36.15) rot=(0,0,1;0rad)
  Radius = 4
FEATURE [Part::Box] Box027  label="removeToCreteHoleForPlugHousing036"
  AttacherType = Attacher::AttachEngine3D
  Height = 28.6
  Length = 20
  Placement = pos=(106.15,0,21.7) rot=(0,0,1;0rad)
  Width = 19
FEATURE [Part::Cut] Cut041  label="top022"
  Base = -> Cut040
  Tool = -> Fusion087
FEATURE [Part::Cut] Cut039  label="top020"
  Base = -> Cut041
  Tool = -> Fusion089
FEATURE [Part::MultiFuse] Fusion090  label="removeToCreteHoleForPlugHousing037"
  Placement = pos=(70,19,36) rot=(0,1,0;1.5708rad)
  Shapes = -> [Cylinder042,Cylinder043]
FEATURE [Part::MultiFuse] Fusion088  label="removeToCreteHoleForPlugHousing033"
  Shapes = -> [Box027,Fusion090]
FEATURE [Part::Cut] Cut042  label="removeToCreteHoleForPlugHousing038"
  Base = -> Cut039
  Tool = -> Fusion088
FEATURE [Part::MultiFuse] Fusion091  label="removeFromTop"
  Shapes = -> [Fillet038,Fusion085,Fusion084,Fusion083,Extrude045]
FEATURE [Part::Cut] Cut043  label="REAL TOP ====="
  Base = -> Fillet036
  Tool = -> Fusion091
FEATURE [Part::MultiFuse] Fusion092  label="caseScrewPillarBracket016"
  Shapes = -> [Extrude030,Extrude031,Extrude032,Extrude033,Extrude034,Extrude035,Extrude036,Extrude037,Box013,Box014]
FEATURE [Sketcher::SketchObject] Sketch058  label="topSketch015"
  FullyConstrained = true
  sketch-geometry (20):
    g0: LineSegment StartX=5.21097e-06 StartY=3 StartZ=0 EndX=5.21097e-06 EndY=19 EndZ=0
    g1: ArcOfCircle CenterX=19 CenterY=19 CenterZ=0 NormalX=0 NormalY=0 NormalZ=1 AngleXU=0 Radius=19 StartAngle=1.5708 EndAngle=3.14159
    g2: ArcOfCircle CenterX=19 CenterY=19 CenterZ=0 NormalX=0 NormalY=0 NormalZ=1 AngleXU=0 Radius=16 StartAngle=1.5708 EndAngle=3.14159
    g3: LineSegment StartX=114 StartY=35 StartZ=0 EndX=19 EndY=35 EndZ=0
    g4: LineSegment StartX=5.21097e-06 StartY=3 StartZ=0 EndX=5.21097e-06 EndY=0 EndZ=0
    g5: LineSegment StartX=3 StartY=0 StartZ=0 EndX=5.21097e-06 EndY=0 EndZ=0
    g6: LineSegment StartX=3 StartY=19 StartZ=0 EndX=3 EndY=0 EndZ=0
    g7: LineSegment StartX=19 StartY=38 StartZ=0 EndX=124 EndY=38 EndZ=0
    g8: Circle CenterX=119 CenterY=35 CenterZ=0 NormalX=0 NormalY=0 NormalZ=1 AngleXU=0 Radius=1
    g9: Circle CenterX=121 CenterY=35 CenterZ=0 NormalX=0 NormalY=0 NormalZ=1 AngleXU=0 Radius=1
    g10: Circle CenterX=121 CenterY=33 CenterZ=0 NormalX=0 NormalY=0 NormalZ=1 AngleXU=0 Radius=1
    g11: BSplineCurve PolesCount=3 KnotsCount=2 Degree=2 IsPeriodic=0
    g12: GeomPoint X=119 Y=35 Z=0
    g13: GeomPoint X=121 Y=33 Z=0
    g14: LineSegment StartX=119 StartY=35 StartZ=0 EndX=114 EndY=35 EndZ=0
    g15: ArcOfCircle CenterX=105 CenterY=19 CenterZ=0 NormalX=0 NormalY=0 NormalZ=1 AngleXU=0 Radius=19 StartAngle=5.7297 EndAngle=6.28319
    g16: ArcOfCircle CenterX=105 CenterY=19 CenterZ=0 NormalX=0 NormalY=0 NormalZ=1 AngleXU=0 Radius=16 StartAngle=5.60905 EndAngle=6.28319
    g17: LineSegment StartX=121 StartY=33 StartZ=0 EndX=121 EndY=19 EndZ=0
    g18: LineSegment StartX=124 StartY=38 StartZ=0 EndX=124 EndY=19 EndZ=0
    g19: LineSegment StartX=117.5 StartY=9.01251 StartZ=0 EndX=121.163 EndY=9.0125 EndZ=0
  constraints (46):
    c: Vertical(g0)
    c: Block(g0)
    c: Coincident(g1,g0)
    c: Block(g1)
    c: Coincident(g2,g1)
    c: Block(g2)
    c: Coincident(g3,g2)
    c: Horizontal(g3)
    c: Tangent(g3,g2)
    c: Coincident(g4,g0)
    c: Distance(g4) = 3
    c: Vertical(g4)
    c: Coincident(g5,g4)
    c: Horizontal(g5)
    c: Coincident(g6,g2)
    c: Coincident(g6,g5)
    c: Vertical(g6)
    c: Horizontal(g7)
    c: Distance(g7) = 105
    c: Coincident(g7,g1)
    c: Block(g3)
    c: Weight(g8) = 1
    c: Equal(g8,g9)
    c: Equal(g8,g10)
    c: InternalAlignment(g8,g11)
    c: InternalAlignment(g9,g11)
    c: InternalAlignment(g10,g11)
    c: InternalAlignment(g12,g11)
    c: InternalAlignment(g13,g11)
    c: Block(g11)
    c: Coincident(g14,g11)
    c: Coincident(g14,g3)
    c: Horizontal(g14)
    c: Block(g15)
    c: Coincident(g16,g15)
    c: Block(g16)
    c: Coincident(g17,g11)
    c: Coincident(g17,g16)
    c: Vertical(g17)
    c: Distance(g17) = 14
    c: Coincident(g18,g7)
    c: Coincident(g18,g15)
    c: Vertical(g18)
    c: Distance(g18) = 19
    c: Coincident(g19,g16)
    c: Coincident(g19,g15)
FEATURE [Part::Extrusion] Extrude049  label="top023"
  Base = -> Sketch058
  Dir = (0,0,1)
  DirMode = 2
  FaceMakerClass = Part::FaceMakerBullseye
  LengthFwd = 72
  LengthRev = 0
  Solid = true
  Symmetric = false
FEATURE [Sketcher::SketchObject] Sketch059
  FullyConstrained = true
  MapMode = 3
  Placement = pos=(0,0,0) rot=(1,0,0;1.5708rad)
  Support = -> [Extrude049]
  sketch-geometry (8):
    g0: Circle CenterX=80.351 CenterY=-67.6202 CenterZ=0 NormalX=0 NormalY=0 NormalZ=1 AngleXU=0 Radius=2
    g1: Circle CenterX=80.351 CenterY=-67.6202 CenterZ=0 NormalX=0 NormalY=0 NormalZ=1 AngleXU=0 Radius=3
    g2: Circle CenterX=80.351 CenterY=-4.92017 CenterZ=0 NormalX=0 NormalY=0 NormalZ=1 AngleXU=0 Radius=2
    g3: Circle CenterX=80.351 CenterY=-4.92017 CenterZ=0 NormalX=0 NormalY=0 NormalZ=1 AngleXU=0 Radius=3
    g4: Circle CenterX=23.851 CenterY=-4.92017 CenterZ=0 NormalX=0 NormalY=0 NormalZ=1 AngleXU=0 Radius=2
    g5: Circle CenterX=23.851 CenterY=-4.92017 CenterZ=0 NormalX=0 NormalY=0 NormalZ=1 AngleXU=0 Radius=3
    g6: Circle CenterX=23.851 CenterY=-67.6202 CenterZ=0 NormalX=0 NormalY=0 NormalZ=1 AngleXU=0 Radius=2
    g7: Circle CenterX=23.851 CenterY=-67.6202 CenterZ=0 NormalX=0 NormalY=0 NormalZ=1 AngleXU=0 Radius=3
  constraints (8):
    c: Block(g3)
    c: Block(g2)
    c: Block(g1)
    c: Block(g0)
    c: Block(g6)
    c: Block(g7)
    c: Block(g4)
    c: Block(g5)
FEATURE [Sketcher::SketchObject] Sketch060
  FullyConstrained = true
  MapMode = 3
  Placement = pos=(0,0,0) rot=(1,0,0;1.5708rad)
  Support = -> [Extrude049]
  sketch-geometry (8):
    g0: Circle CenterX=80.351 CenterY=-67.6202 CenterZ=0 NormalX=0 NormalY=0 NormalZ=1 AngleXU=0 Radius=3
    g1: Circle CenterX=80.351 CenterY=-4.92017 CenterZ=0 NormalX=0 NormalY=0 NormalZ=1 AngleXU=0 Radius=3
    g2: Circle CenterX=23.851 CenterY=-4.92017 CenterZ=0 NormalX=0 NormalY=0 NormalZ=1 AngleXU=0 Radius=3
    g3: Circle CenterX=23.851 CenterY=-67.6202 CenterZ=0 NormalX=0 NormalY=0 NormalZ=1 AngleXU=0 Radius=3
    g4: Circle CenterX=23.851 CenterY=-67.6202 CenterZ=0 NormalX=0 NormalY=0 NormalZ=1 AngleXU=0 Radius=5
    g5: Circle CenterX=80.351 CenterY=-67.6202 CenterZ=0 NormalX=0 NormalY=0 NormalZ=1 AngleXU=0 Radius=5
    g6: Circle CenterX=23.851 CenterY=-4.92017 CenterZ=0 NormalX=0 NormalY=0 NormalZ=1 AngleXU=0 Radius=5
    g7: Circle CenterX=80.351 CenterY=-4.92017 CenterZ=0 NormalX=0 NormalY=0 NormalZ=1 AngleXU=0 Radius=5
  constraints (8):
    c: Block(g1)
    c: Block(g0)
    c: Block(g3)
    c: Block(g2)
    c: Block(g5)
    c: Block(g4)
    c: Block(g6)
    c: Block(g7)
FEATURE [Sketcher::SketchObject] Sketch061
  FullyConstrained = true
  MapMode = 3
  Placement = pos=(0,0,0) rot=(1,0,0;1.5708rad)
  sketch-geometry (8):
    g0: Circle CenterX=80.351 CenterY=-67.6202 CenterZ=0 NormalX=0 NormalY=0 NormalZ=1 AngleXU=0 Radius=3
    g1: Circle CenterX=80.351 CenterY=-4.92017 CenterZ=0 NormalX=0 NormalY=0 NormalZ=1 AngleXU=0 Radius=3
    g2: Circle CenterX=23.851 CenterY=-4.92017 CenterZ=0 NormalX=0 NormalY=0 NormalZ=1 AngleXU=0 Radius=3
    g3: Circle CenterX=23.851 CenterY=-67.6202 CenterZ=0 NormalX=0 NormalY=0 NormalZ=1 AngleXU=0 Radius=3
    g4: Circle CenterX=23.851 CenterY=-67.6202 CenterZ=0 NormalX=0 NormalY=0 NormalZ=1 AngleXU=0 Radius=5
    g5: Circle CenterX=80.351 CenterY=-67.6202 CenterZ=0 NormalX=0 NormalY=0 NormalZ=1 AngleXU=0 Radius=5
    g6: Circle CenterX=23.851 CenterY=-4.92017 CenterZ=0 NormalX=0 NormalY=0 NormalZ=1 AngleXU=0 Radius=5
    g7: Circle CenterX=80.351 CenterY=-4.92017 CenterZ=0 NormalX=0 NormalY=0 NormalZ=1 AngleXU=0 Radius=5
  constraints (8):
    c: Block(g1)
    c: Block(g0)
    c: Block(g3)
    c: Block(g2)
    c: Block(g5)
    c: Block(g4)
    c: Block(g6)
    c: Block(g7)
FEATURE [Sketcher::SketchObject] Sketch062  label="topSketch016"
  FullyConstrained = true
  sketch-geometry (20):
    g0: LineSegment StartX=5.21097e-06 StartY=3 StartZ=0 EndX=5.21097e-06 EndY=19 EndZ=0
    g1: ArcOfCircle CenterX=19 CenterY=19 CenterZ=0 NormalX=0 NormalY=0 NormalZ=1 AngleXU=0 Radius=19 StartAngle=1.5708 EndAngle=3.14159
    g2: ArcOfCircle CenterX=19 CenterY=19 CenterZ=0 NormalX=0 NormalY=0 NormalZ=1 AngleXU=0 Radius=16 StartAngle=1.5708 EndAngle=3.14159
    g3: LineSegment StartX=114 StartY=35 StartZ=0 EndX=19 EndY=35 EndZ=0
    g4: LineSegment StartX=5.21097e-06 StartY=3 StartZ=0 EndX=5.21097e-06 EndY=0 EndZ=0
    g5: LineSegment StartX=3 StartY=0 StartZ=0 EndX=5.21097e-06 EndY=0 EndZ=0
    g6: LineSegment StartX=3 StartY=19 StartZ=0 EndX=3 EndY=0 EndZ=0
    g7: LineSegment StartX=19 StartY=38 StartZ=0 EndX=124 EndY=38 EndZ=0
    g8: Circle CenterX=119 CenterY=35 CenterZ=0 NormalX=0 NormalY=0 NormalZ=1 AngleXU=0 Radius=1
    g9: Circle CenterX=121 CenterY=35 CenterZ=0 NormalX=0 NormalY=0 NormalZ=1 AngleXU=0 Radius=1
    g10: Circle CenterX=121 CenterY=33 CenterZ=0 NormalX=0 NormalY=0 NormalZ=1 AngleXU=0 Radius=1
    g11: BSplineCurve PolesCount=3 KnotsCount=2 Degree=2 IsPeriodic=0
    g12: GeomPoint X=119 Y=35 Z=0
    g13: GeomPoint X=121 Y=33 Z=0
    g14: LineSegment StartX=119 StartY=35 StartZ=0 EndX=114 EndY=35 EndZ=0
    g15: ArcOfCircle CenterX=105 CenterY=19 CenterZ=0 NormalX=0 NormalY=0 NormalZ=1 AngleXU=0 Radius=19 StartAngle=5.7297 EndAngle=6.28319
    g16: ArcOfCircle CenterX=105 CenterY=19 CenterZ=0 NormalX=0 NormalY=0 NormalZ=1 AngleXU=0 Radius=16 StartAngle=5.60905 EndAngle=6.28319
    g17: LineSegment StartX=121 StartY=33 StartZ=0 EndX=121 EndY=19 EndZ=0
    g18: LineSegment StartX=124 StartY=38 StartZ=0 EndX=124 EndY=19 EndZ=0
    g19: LineSegment StartX=117.5 StartY=9.01251 StartZ=0 EndX=121.163 EndY=9.0125 EndZ=0
  constraints (46):
    c: Vertical(g0)
    c: Block(g0)
    c: Coincident(g1,g0)
    c: Block(g1)
    c: Coincident(g2,g1)
    c: Block(g2)
    c: Coincident(g3,g2)
    c: Horizontal(g3)
    c: Tangent(g3,g2)
    c: Coincident(g4,g0)
    c: Distance(g4) = 3
    c: Vertical(g4)
    c: Coincident(g5,g4)
    c: Horizontal(g5)
    c: Coincident(g6,g2)
    c: Coincident(g6,g5)
    c: Vertical(g6)
    c: Horizontal(g7)
    c: Distance(g7) = 105
    c: Coincident(g7,g1)
    c: Block(g3)
    c: Weight(g8) = 1
    c: Equal(g8,g9)
    c: Equal(g8,g10)
    c: InternalAlignment(g8,g11)
    c: InternalAlignment(g9,g11)
    c: InternalAlignment(g10,g11)
    c: InternalAlignment(g12,g11)
    c: InternalAlignment(g13,g11)
    c: Block(g11)
    c: Coincident(g14,g11)
    c: Coincident(g14,g3)
    c: Horizontal(g14)
    c: Block(g15)
    c: Coincident(g16,g15)
    c: Block(g16)
    c: Coincident(g17,g11)
    c: Coincident(g17,g16)
    c: Vertical(g17)
    c: Distance(g17) = 14
    c: Coincident(g18,g7)
    c: Coincident(g18,g15)
    c: Vertical(g18)
    c: Distance(g18) = 19
    c: Coincident(g19,g16)
    c: Coincident(g19,g15)
FEATURE [Part::Extrusion] Extrude053  label="top024"
  Base = -> Sketch062
  Dir = (0,0,1)
  DirMode = 2
  FaceMakerClass = Part::FaceMakerBullseye
  LengthFwd = 72
  LengthRev = 0
  Solid = true
  Symmetric = false
FEATURE [Sketcher::SketchObject] Sketch063
  FullyConstrained = true
  MapMode = 3
  Placement = pos=(0,0,0) rot=(1,0,0;1.5708rad)
  Support = -> [Extrude053]
  sketch-geometry (8):
    g0: Circle CenterX=80.351 CenterY=-67.6202 CenterZ=0 NormalX=0 NormalY=0 NormalZ=1 AngleXU=0 Radius=2
    g1: Circle CenterX=80.351 CenterY=-67.6202 CenterZ=0 NormalX=0 NormalY=0 NormalZ=1 AngleXU=0 Radius=3
    g2: Circle CenterX=80.351 CenterY=-4.92017 CenterZ=0 NormalX=0 NormalY=0 NormalZ=1 AngleXU=0 Radius=2
    g3: Circle CenterX=80.351 CenterY=-4.92017 CenterZ=0 NormalX=0 NormalY=0 NormalZ=1 AngleXU=0 Radius=3
    g4: Circle CenterX=23.851 CenterY=-4.92017 CenterZ=0 NormalX=0 NormalY=0 NormalZ=1 AngleXU=0 Radius=2
    g5: Circle CenterX=23.851 CenterY=-4.92017 CenterZ=0 NormalX=0 NormalY=0 NormalZ=1 AngleXU=0 Radius=3
    g6: Circle CenterX=23.851 CenterY=-67.6202 CenterZ=0 NormalX=0 NormalY=0 NormalZ=1 AngleXU=0 Radius=2
    g7: Circle CenterX=23.851 CenterY=-67.6202 CenterZ=0 NormalX=0 NormalY=0 NormalZ=1 AngleXU=0 Radius=3
  constraints (8):
    c: Block(g3)
    c: Block(g2)
    c: Block(g1)
    c: Block(g0)
    c: Block(g6)
    c: Block(g7)
    c: Block(g4)
    c: Block(g5)
FEATURE [Part::Extrusion] Extrude054
  Base = -> Sketch063
  Dir = (0,-1,2e-16)
  DirMode = 2
  FaceMakerClass = Part::FaceMakerBullseye
  LengthFwd = 6
  LengthRev = 0
  Placement = pos=(0,9,0) rot=(0,0,1;0rad)
  Solid = true
  Symmetric = false
FEATURE [Sketcher::SketchObject] Sketch064  label="topSketch017"
  FullyConstrained = true
  sketch-geometry (20):
    g0: LineSegment StartX=5.21097e-06 StartY=3 StartZ=0 EndX=5.21097e-06 EndY=19 EndZ=0
    g1: ArcOfCircle CenterX=19 CenterY=19 CenterZ=0 NormalX=0 NormalY=0 NormalZ=1 AngleXU=0 Radius=19 StartAngle=1.5708 EndAngle=3.14159
    g2: ArcOfCircle CenterX=19 CenterY=19 CenterZ=0 NormalX=0 NormalY=0 NormalZ=1 AngleXU=0 Radius=16 StartAngle=1.5708 EndAngle=3.14159
    g3: LineSegment StartX=114 StartY=35 StartZ=0 EndX=19 EndY=35 EndZ=0
    g4: LineSegment StartX=5.21097e-06 StartY=3 StartZ=0 EndX=5.21097e-06 EndY=0 EndZ=0
    g5: LineSegment StartX=3 StartY=0 StartZ=0 EndX=5.21097e-06 EndY=0 EndZ=0
    g6: LineSegment StartX=3 StartY=19 StartZ=0 EndX=3 EndY=0 EndZ=0
    g7: LineSegment StartX=19 StartY=38 StartZ=0 EndX=124 EndY=38 EndZ=0
    g8: Circle CenterX=119 CenterY=35 CenterZ=0 NormalX=0 NormalY=0 NormalZ=1 AngleXU=0 Radius=1
    g9: Circle CenterX=121 CenterY=35 CenterZ=0 NormalX=0 NormalY=0 NormalZ=1 AngleXU=0 Radius=1
    g10: Circle CenterX=121 CenterY=33 CenterZ=0 NormalX=0 NormalY=0 NormalZ=1 AngleXU=0 Radius=1
    g11: BSplineCurve PolesCount=3 KnotsCount=2 Degree=2 IsPeriodic=0
    g12: GeomPoint X=119 Y=35 Z=0
    g13: GeomPoint X=121 Y=33 Z=0
    g14: LineSegment StartX=119 StartY=35 StartZ=0 EndX=114 EndY=35 EndZ=0
    g15: ArcOfCircle CenterX=105 CenterY=19 CenterZ=0 NormalX=0 NormalY=0 NormalZ=1 AngleXU=0 Radius=19 StartAngle=5.7297 EndAngle=6.28319
    g16: ArcOfCircle CenterX=105 CenterY=19 CenterZ=0 NormalX=0 NormalY=0 NormalZ=1 AngleXU=0 Radius=16 StartAngle=5.60905 EndAngle=6.28319
    g17: LineSegment StartX=121 StartY=33 StartZ=0 EndX=121 EndY=19 EndZ=0
    g18: LineSegment StartX=124 StartY=38 StartZ=0 EndX=124 EndY=19 EndZ=0
    g19: LineSegment StartX=117.5 StartY=9.01251 StartZ=0 EndX=121.163 EndY=9.0125 EndZ=0
  constraints (46):
    c: Vertical(g0)
    c: Block(g0)
    c: Coincident(g1,g0)
    c: Block(g1)
    c: Coincident(g2,g1)
    c: Block(g2)
    c: Coincident(g3,g2)
    c: Horizontal(g3)
    c: Tangent(g3,g2)
    c: Coincident(g4,g0)
    c: Distance(g4) = 3
    c: Vertical(g4)
    c: Coincident(g5,g4)
    c: Horizontal(g5)
    c: Coincident(g6,g2)
    c: Coincident(g6,g5)
    c: Vertical(g6)
    c: Horizontal(g7)
    c: Distance(g7) = 105
    c: Coincident(g7,g1)
    c: Block(g3)
    c: Weight(g8) = 1
    c: Equal(g8,g9)
    c: Equal(g8,g10)
    c: InternalAlignment(g8,g11)
    c: InternalAlignment(g9,g11)
    c: InternalAlignment(g10,g11)
    c: InternalAlignment(g12,g11)
    c: InternalAlignment(g13,g11)
    c: Block(g11)
    c: Coincident(g14,g11)
    c: Coincident(g14,g3)
    c: Horizontal(g14)
    c: Block(g15)
    c: Coincident(g16,g15)
    c: Block(g16)
    c: Coincident(g17,g11)
    c: Coincident(g17,g16)
    c: Vertical(g17)
    c: Distance(g17) = 14
    c: Coincident(g18,g7)
    c: Coincident(g18,g15)
    c: Vertical(g18)
    c: Distance(g18) = 19
    c: Coincident(g19,g16)
    c: Coincident(g19,g15)
FEATURE [Sketcher::SketchObject] Sketch065
  FullyConstrained = true
  MapMode = 3
  Placement = pos=(0,0,0) rot=(1,0,0;1.5708rad)
  sketch-geometry (8):
    g0: Circle CenterX=80.351 CenterY=-67.6202 CenterZ=0 NormalX=0 NormalY=0 NormalZ=1 AngleXU=0 Radius=3
    g1: Circle CenterX=80.351 CenterY=-4.92017 CenterZ=0 NormalX=0 NormalY=0 NormalZ=1 AngleXU=0 Radius=3
    g2: Circle CenterX=23.851 CenterY=-4.92017 CenterZ=0 NormalX=0 NormalY=0 NormalZ=1 AngleXU=0 Radius=3
    g3: Circle CenterX=23.851 CenterY=-67.6202 CenterZ=0 NormalX=0 NormalY=0 NormalZ=1 AngleXU=0 Radius=3
    g4: Circle CenterX=23.851 CenterY=-67.6202 CenterZ=0 NormalX=0 NormalY=0 NormalZ=1 AngleXU=0 Radius=5
    g5: Circle CenterX=80.351 CenterY=-67.6202 CenterZ=0 NormalX=0 NormalY=0 NormalZ=1 AngleXU=0 Radius=5
    g6: Circle CenterX=23.851 CenterY=-4.92017 CenterZ=0 NormalX=0 NormalY=0 NormalZ=1 AngleXU=0 Radius=5
    g7: Circle CenterX=80.351 CenterY=-4.92017 CenterZ=0 NormalX=0 NormalY=0 NormalZ=1 AngleXU=0 Radius=5
  constraints (8):
    c: Block(g1)
    c: Block(g0)
    c: Block(g3)
    c: Block(g2)
    c: Block(g5)
    c: Block(g4)
    c: Block(g6)
    c: Block(g7)
FEATURE [Part::Extrusion] Extrude056
  Base = -> Sketch065
  Dir = (0,-1,2e-16)
  DirMode = 2
  FaceMakerClass = Part::FaceMakerBullseye
  LengthFwd = 2
  LengthRev = 0
  Solid = true
  Symmetric = false
FEATURE [Part::Extrusion] Extrude057  label="top025"
  Base = -> Sketch064
  Dir = (0,0,1)
  DirMode = 2
  FaceMakerClass = Part::FaceMakerBullseye
  LengthFwd = 72
  LengthRev = 0
  Solid = true
  Symmetric = false
FEATURE [Sketcher::SketchObject] Sketch066
  FullyConstrained = true
  MapMode = 3
  Placement = pos=(0,0,0) rot=(1,0,0;1.5708rad)
  Support = -> [Extrude057]
  sketch-geometry (8):
    g0: Circle CenterX=80.351 CenterY=-67.6202 CenterZ=0 NormalX=0 NormalY=0 NormalZ=1 AngleXU=0 Radius=3
    g1: Circle CenterX=80.351 CenterY=-4.92017 CenterZ=0 NormalX=0 NormalY=0 NormalZ=1 AngleXU=0 Radius=3
    g2: Circle CenterX=23.851 CenterY=-4.92017 CenterZ=0 NormalX=0 NormalY=0 NormalZ=1 AngleXU=0 Radius=3
    g3: Circle CenterX=23.851 CenterY=-67.6202 CenterZ=0 NormalX=0 NormalY=0 NormalZ=1 AngleXU=0 Radius=3
    g4: Circle CenterX=23.851 CenterY=-67.6202 CenterZ=0 NormalX=0 NormalY=0 NormalZ=1 AngleXU=0 Radius=5
    g5: Circle CenterX=80.351 CenterY=-67.6202 CenterZ=0 NormalX=0 NormalY=0 NormalZ=1 AngleXU=0 Radius=5
    g6: Circle CenterX=23.851 CenterY=-4.92017 CenterZ=0 NormalX=0 NormalY=0 NormalZ=1 AngleXU=0 Radius=5
    g7: Circle CenterX=80.351 CenterY=-4.92017 CenterZ=0 NormalX=0 NormalY=0 NormalZ=1 AngleXU=0 Radius=5
  constraints (8):
    c: Block(g1)
    c: Block(g0)
    c: Block(g3)
    c: Block(g2)
    c: Block(g5)
    c: Block(g4)
    c: Block(g6)
    c: Block(g7)
FEATURE [Part::Extrusion] Extrude055
  Base = -> Sketch066
  Dir = (0,-1,2e-16)
  DirMode = 2
  FaceMakerClass = Part::FaceMakerBullseye
  LengthFwd = 2
  LengthRev = 0
  Solid = true
  Symmetric = false
FEATURE [Part::Fillet] Fillet041
  Base = -> Extrude056
  Edges = 4 edges r=1.99: [Edge6,Edge12,Edge18,Edge24]
FEATURE [Part::Cut] Cut045
  Base = -> Extrude055
  Placement = pos=(0,6,0) rot=(0,0,1;0rad)
  Tool = -> Fillet041
FEATURE [Part::MultiFuse] Fusion095  label="pcbScrewPillars"
  Placement = pos=(-3.2,-1,72.3) rot=(0,0,1;0rad)
  Shapes = -> [Cut045,Extrude054]
FEATURE [Part::Feature] Face113
  shape: bbox 3.2 x 1.5 x 2e-07 mm, 1 faces, 0 solids (baked)
FEATURE [Part::Revolution] Revolve121  label="backCaseScrewRetainer002"
  Angle = 360
  Axis = (0,1,0)
  Base = (0,0,0)
  FaceMakerClass = Part::FaceMakerBullseye
  Placement = pos=(12.5,3,62) rot=(0,0,1;0rad)
  Solid = false
  Source = -> Face113
  Symmetric = false
FEATURE [Part::Feature] Face114
  shape: bbox 3.2 x 1.5 x 2e-07 mm, 1 faces, 0 solids (baked)
FEATURE [Part::Feature] Face115
  shape: bbox 3.2 x 1.5 x 2e-07 mm, 1 faces, 0 solids (baked)
FEATURE [Part::Feature] Face116
  shape: bbox 3.2 x 1.5 x 2e-07 mm, 1 faces, 0 solids (baked)
FEATURE [Part::Revolution] Revolve122  label="frontCaseScrewRetainer004"
  Angle = 360
  Axis = (0,1,0)
  Base = (0,0,0)
  FaceMakerClass = Part::FaceMakerBullseye
  Placement = pos=(89.5,3,68.5) rot=(0,0,1;0rad)
  Solid = false
  Source = -> Face115
  Symmetric = false
FEATURE [Part::Revolution] Revolve123  label="frontCaseScrewRetainer005"
  Angle = 360
  Axis = (0,1,0)
  Base = (0,0,0)
  FaceMakerClass = Part::FaceMakerBullseye
  Placement = pos=(89.5,3,3.5) rot=(0,0,1;0rad)
  Solid = false
  Source = -> Face116
  Symmetric = false
FEATURE [Part::Revolution] Revolve124  label="backCaseScrewRetainer003"
  Angle = 360
  Axis = (0,1,0)
  Base = (0,0,0)
  FaceMakerClass = Part::FaceMakerBullseye
  Placement = pos=(12.5,3,10) rot=(0,0,1;0rad)
  Solid = false
  Source = -> Face114
  Symmetric = false
FEATURE [Part::Feature] Face117
  shape: bbox 3.6 x 3.2 x 2e-07 mm, 1 faces, 0 solids (baked)
FEATURE [Part::Revolution] Revolve125  label="moreFrontCaseScrewRetainer004"
  Angle = 360
  Axis = (0,1,0)
  Base = (0,0,0)
  FaceMakerClass = Part::FaceMakerBullseye
  Placement = pos=(109.5,4.5,68.5) rot=(0,0,1;0rad)
  Solid = false
  Source = -> Face117
  Symmetric = false
FEATURE [Part::Feature] Face118
  shape: bbox 3.6 x 3.2 x 2e-07 mm, 1 faces, 0 solids (baked)
FEATURE [Part::Revolution] Revolve126  label="moreFrontCaseScrewRetainer005"
  Angle = 360
  Axis = (0,1,0)
  Base = (0,0,0)
  FaceMakerClass = Part::FaceMakerBullseye
  Placement = pos=(109.5,4.5,3.5) rot=(0,0,1;0rad)
  Solid = false
  Source = -> Face118
  Symmetric = false
FEATURE [Part::MultiFuse] Fusion096  label="screwRetainers001"
  Shapes = -> [Revolve126,Revolve125,Revolve124,Revolve123,Revolve122,Revolve121]
FEATURE [Part::Feature] Face119
  shape: bbox 10 x 16.5 x 2e-07 mm, 1 faces, 0 solids (baked)
FEATURE [Part::Revolution] Revolve130  label="plugHousing050"
  Angle = 360
  Axis = (0,1,0)
  Base = (0,0,0)
  FaceMakerClass = Part::FaceMakerBullseye
  Placement = pos=(0,0,36.15) rot=(0,0,1;0rad)
  Solid = false
  Source = -> Face119
  Symmetric = false
FEATURE [Part::Feature] Face120
  shape: bbox 10 x 16.5 x 2e-07 mm, 1 faces, 0 solids (baked)
FEATURE [Part::Feature] Face121
  shape: bbox 10 x 16.5 x 2e-07 mm, 1 faces, 0 solids (baked)
FEATURE [Part::Revolution] Revolve127  label="plugHousing047"
  Angle = 360
  Axis = (0,1,0)
  Base = (0,0,0)
  FaceMakerClass = Part::FaceMakerBullseye
  Placement = pos=(0,0,36.15) rot=(0,0,1;0rad)
  Solid = false
  Source = -> Face121
  Symmetric = false
FEATURE [Part::Feature] Face122
  shape: bbox 10 x 16.5 x 2e-07 mm, 1 faces, 0 solids (baked)
FEATURE [Part::Feature] Face123
  shape: bbox 10 x 16.5 x 2e-07 mm, 1 faces, 0 solids (baked)
FEATURE [Part::Revolution] Revolve128  label="plugHousing048"
  Angle = 360
  Axis = (0,1,0)
  Base = (0,0,0)
  FaceMakerClass = Part::FaceMakerBullseye
  Placement = pos=(0,0,36.15) rot=(0,0,1;0rad)
  Solid = false
  Source = -> Face123
  Symmetric = false
FEATURE [Part::MultiFuse] Fusion100  label="plugHousing054"
  Placement = pos=(0,0,0) rot=(0,0,1;1.5708rad)
  Shapes = -> [Revolve130,Revolve128]
FEATURE [Part::Feature] Face124
  shape: bbox 10 x 16.5 x 2e-07 mm, 1 faces, 0 solids (baked)
FEATURE [Part::Feature] Face125
  shape: bbox 10 x 16.5 x 2e-07 mm, 1 faces, 0 solids (baked)
FEATURE [Part::Revolution] Revolve129  label="plugHousing049"
  Angle = 360
  Axis = (0,1,0)
  Base = (0,0,0)
  FaceMakerClass = Part::FaceMakerBullseye
  Placement = pos=(0,0,36.15) rot=(0,0,1;0rad)
  Solid = false
  Source = -> Face125
  Symmetric = false
FEATURE [Part::Feature] Face126
  shape: bbox 10 x 16.5 x 2e-07 mm, 1 faces, 0 solids (baked)
FEATURE [Part::Revolution] Revolve131  label="plugHousing058"
  Angle = 360
  Axis = (0,1,0)
  Base = (0,0,0)
  FaceMakerClass = Part::FaceMakerBullseye
  Placement = pos=(0,0,36.15) rot=(0,0,1;0rad)
  Solid = false
  Source = -> Face120
  Symmetric = false
FEATURE [Part::MultiFuse] Fusion099  label="plugHousing053"
  Placement = pos=(0,0,0) rot=(0,0,1;1.5708rad)
  Shapes = -> [Revolve127,Revolve131]
FEATURE [Part::MultiFuse] Fusion102  label="plugHousing056"
  Placement = pos=(0,19,0) rot=(0,0,1;3.14159rad)
  Shapes = -> [Fusion100,Fusion099]
FEATURE [Part::Revolution] Revolve132  label="plugHousing059"
  Angle = 360
  Axis = (0,1,0)
  Base = (0,0,0)
  FaceMakerClass = Part::FaceMakerBullseye
  Placement = pos=(0,0,36.15) rot=(0,0,1;0rad)
  Solid = false
  Source = -> Face126
  Symmetric = false
FEATURE [Part::Revolution] Revolve133  label="plugHousing060"
  Angle = 360
  Axis = (0,1,0)
  Base = (0,0,0)
  FaceMakerClass = Part::FaceMakerBullseye
  Placement = pos=(0,0,36.15) rot=(0,0,1;0rad)
  Solid = false
  Source = -> Face122
  Symmetric = false
FEATURE [Part::MultiFuse] Fusion097  label="plugHousing051"
  Placement = pos=(0,0,0) rot=(0,0,1;1.5708rad)
  Shapes = -> [Revolve133,Revolve132]
FEATURE [Part::Revolution] Revolve134  label="plugHousing061"
  Angle = 360
  Axis = (0,1,0)
  Base = (0,0,0)
  FaceMakerClass = Part::FaceMakerBullseye
  Placement = pos=(0,0,36.15) rot=(0,0,1;0rad)
  Solid = false
  Source = -> Face124
  Symmetric = false
FEATURE [Part::MultiFuse] Fusion101  label="plugHousing055"
  Placement = pos=(0,0,0) rot=(0,0,1;1.5708rad)
  Shapes = -> [Revolve129,Revolve134]
FEATURE [Part::MultiFuse] Fusion098  label="plugHousing052"
  Placement = pos=(0,19,0) rot=(0,0,1;3.14159rad)
  Shapes = -> [Fusion097,Fusion101]
FEATURE [Part::MultiFuse] Fusion103  label="plugHousing057"
  Placement = pos=(122.621,0,-0.15) rot=(0,0,1;0rad)
  Shapes = -> [Fusion102,Fusion098]
FEATURE [Part::Box] Box028  label="Cube015"
  AttacherType = Attacher::AttachEngine3D
  Height = 28
  Length = 3
  Placement = pos=(110.7,19,22) rot=(0,0,1;0rad)
  Width = 15.7
FEATURE [Part::Cylinder] Cylinder044
  Angle = 360
  AttacherType = Attacher::AttachEngine3D
  Height = 20
  Placement = pos=(0,0,36.15) rot=(0,0,1;0rad)
  Radius = 10.3
FEATURE [Part::Cylinder] Cylinder045
  Angle = 360
  AttacherType = Attacher::AttachEngine3D
  Height = 10
  Placement = pos=(0,0,36.15) rot=(0,0,1;0rad)
  Radius = 4
FEATURE [Part::MultiFuse] Fusion104  label="removeToCreteHoleForPlugHousing040"
  Placement = pos=(70,19,36) rot=(0,1,0;1.5708rad)
  Shapes = -> [Cylinder044,Cylinder045]
FEATURE [Part::Cut] Cut046  label="plugHousingTab003"
  Base = -> Box028
  Tool = -> Fusion104
FEATURE [Part::MultiFuse] Fusion105  label="plugHousing062"
  Shapes = -> [Fusion103,Cut046]
FEATURE [Part::Fillet] Fillet042
  Base = -> Fusion105
  Edges = 1 edges r=2: [Edge25]
FEATURE [Part::Fillet] Fillet043  label="plugHousing063"
  Base = -> Fillet042
  Edges = 1 edges r=2: [Edge8]
  Placement = pos=(7,0,0) rot=(0,0,1;0rad)
FEATURE [Part::Feature] Face127
  shape: bbox 10 x 16.5 x 2e-07 mm, 1 faces, 0 solids (baked)
FEATURE [Part::Feature] Face128
  shape: bbox 10 x 16.5 x 2e-07 mm, 1 faces, 0 solids (baked)
FEATURE [Part::Revolution] Revolve137  label="plugHousing070"
  Angle = 360
  Axis = (0,1,0)
  Base = (0,0,0)
  FaceMakerClass = Part::FaceMakerBullseye
  Placement = pos=(0,0,36.15) rot=(0,0,1;0rad)
  Solid = false
  Source = -> Face127
  Symmetric = false
FEATURE [Part::Revolution] Revolve140  label="plugHousing073"
  Angle = 360
  Axis = (0,1,0)
  Base = (0,0,0)
  FaceMakerClass = Part::FaceMakerBullseye
  Placement = pos=(0,0,36.15) rot=(0,0,1;0rad)
  Solid = false
  Source = -> Face128
  Symmetric = false
FEATURE [Part::Feature] Face129
  shape: bbox 10 x 16.5 x 2e-07 mm, 1 faces, 0 solids (baked)
FEATURE [Part::Revolution] Revolve138  label="plugHousing071"
  Angle = 360
  Axis = (0,1,0)
  Base = (0,0,0)
  FaceMakerClass = Part::FaceMakerBullseye
  Placement = pos=(0,0,36.15) rot=(0,0,1;0rad)
  Solid = false
  Source = -> Face129
  Symmetric = false
FEATURE [Part::Feature] Face130
  shape: bbox 10 x 16.5 x 2e-07 mm, 1 faces, 0 solids (baked)
FEATURE [Part::Revolution] Revolve139  label="plugHousing072"
  Angle = 360
  Axis = (0,1,0)
  Base = (0,0,0)
  FaceMakerClass = Part::FaceMakerBullseye
  Placement = pos=(0,0,36.15) rot=(0,0,1;0rad)
  Solid = false
  Source = -> Face130
  Symmetric = false
FEATURE [Part::Feature] Face131
  shape: bbox 10 x 16.5 x 2e-07 mm, 1 faces, 0 solids (baked)
FEATURE [Part::Revolution] Revolve135  label="plugHousing068"
  Angle = 360
  Axis = (0,1,0)
  Base = (0,0,0)
  FaceMakerClass = Part::FaceMakerBullseye
  Placement = pos=(0,0,36.15) rot=(0,0,1;0rad)
  Solid = false
  Source = -> Face131
  Symmetric = false
FEATURE [Part::MultiFuse] Fusion112  label="plugHousing078"
  Placement = pos=(0,0,0) rot=(0,0,1;1.5708rad)
  Shapes = -> [Revolve135,Revolve139]
FEATURE [Part::Feature] Face132
  shape: bbox 10 x 16.5 x 2e-07 mm, 1 faces, 0 solids (baked)
FEATURE [Part::Revolution] Revolve141  label="plugHousing074"
  Angle = 360
  Axis = (0,1,0)
  Base = (0,0,0)
  FaceMakerClass = Part::FaceMakerBullseye
  Placement = pos=(0,0,36.15) rot=(0,0,1;0rad)
  Solid = false
  Source = -> Face132
  Symmetric = false
FEATURE [Part::MultiFuse] Fusion110  label="plugHousing076"
  Placement = pos=(0,0,0) rot=(0,0,1;1.5708rad)
  Shapes = -> [Revolve141,Revolve140]
FEATURE [Part::Feature] Face133
  shape: bbox 10 x 16.5 x 2e-07 mm, 1 faces, 0 solids (baked)
FEATURE [Part::Revolution] Revolve136  label="plugHousing069"
  Angle = 360
  Axis = (0,1,0)
  Base = (0,0,0)
  FaceMakerClass = Part::FaceMakerBullseye
  Placement = pos=(0,0,36.15) rot=(0,0,1;0rad)
  Solid = false
  Source = -> Face133
  Symmetric = false
FEATURE [Part::MultiFuse] Fusion106  label="plugHousing064"
  Placement = pos=(0,0,0) rot=(0,0,1;1.5708rad)
  Shapes = -> [Revolve138,Revolve136]
FEATURE [Part::MultiFuse] Fusion108  label="plugHousing066"
  Placement = pos=(0,19,0) rot=(0,0,1;3.14159rad)
  Shapes = -> [Fusion106,Fusion112]
FEATURE [Part::Feature] Face134
  shape: bbox 10 x 16.5 x 2e-07 mm, 1 faces, 0 solids (baked)
FEATURE [Part::Revolution] Revolve142  label="plugHousing075"
  Angle = 360
  Axis = (0,1,0)
  Base = (0,0,0)
  FaceMakerClass = Part::FaceMakerBullseye
  Placement = pos=(0,0,36.15) rot=(0,0,1;0rad)
  Solid = false
  Source = -> Face134
  Symmetric = false
FEATURE [Part::MultiFuse] Fusion107  label="plugHousing065"
  Placement = pos=(0,0,0) rot=(0,0,1;1.5708rad)
  Shapes = -> [Revolve137,Revolve142]
FEATURE [Part::MultiFuse] Fusion111  label="plugHousing077"
  Placement = pos=(0,19,0) rot=(0,0,1;3.14159rad)
  Shapes = -> [Fusion110,Fusion107]
FEATURE [Part::MultiFuse] Fusion109  label="plugHousing067"
  Placement = pos=(131.236,0,-0.15) rot=(0,0,1;0rad)
  Shapes = -> [Fusion108,Fusion111]
FEATURE [Part::MultiFuse] Fusion113  label="plugHousing079"
  Shapes = -> [Fillet043,Fusion109]
FEATURE [Part::Feature] Face135
  shape: bbox 3.5 x 17.8 x 2e-07 mm, 1 faces, 0 solids (baked)
FEATURE [Part::Revolution] Revolve143  label="removeToCreateScrewAndThreadedInsertHole049"
  Angle = 360
  Axis = (0,1,0)
  Base = (0,0,0)
  FaceMakerClass = Part::FaceMakerBullseye
  Placement = pos=(12.5,0,10) rot=(0,0,1;0rad)
  Solid = false
  Source = -> Face135
  Symmetric = false
FEATURE [Part::Feature] Face136
  shape: bbox 3.5 x 17.8 x 2e-07 mm, 1 faces, 0 solids (baked)
FEATURE [Part::Revolution] Revolve144  label="removeToCreateScrewAndThreadedInsertHole050"
  Angle = 360
  Axis = (0,1,0)
  Base = (0,0,0)
  FaceMakerClass = Part::FaceMakerBullseye
  Placement = pos=(12.5,0,62) rot=(0,0,1;0rad)
  Solid = false
  Source = -> Face136
  Symmetric = false
FEATURE [Part::Feature] Face137
  shape: bbox 3.5 x 17.8 x 2e-07 mm, 1 faces, 0 solids (baked)
FEATURE [Part::Revolution] Revolve145  label="removeToCreateScrewAndThreadedInsertHole051"
  Angle = 360
  Axis = (0,1,0)
  Base = (0,0,0)
  FaceMakerClass = Part::FaceMakerBullseye
  Placement = pos=(89.5,0,68.5) rot=(0,0,1;0rad)
  Solid = false
  Source = -> Face137
  Symmetric = false
FEATURE [Part::Feature] Face138
  shape: bbox 3.5 x 17.8 x 2e-07 mm, 1 faces, 0 solids (baked)
FEATURE [Part::Revolution] Revolve146  label="removeToCreateScrewAndThreadedInsertHole052"
  Angle = 360
  Axis = (0,1,0)
  Base = (0,0,0)
  FaceMakerClass = Part::FaceMakerBullseye
  Placement = pos=(89.5,0,3.5) rot=(0,0,1;0rad)
  Solid = false
  Source = -> Face138
  Symmetric = false
FEATURE [Part::Feature] Face139
  shape: bbox 3.5 x 17.8 x 2e-07 mm, 1 faces, 0 solids (baked)
FEATURE [Part::Revolution] Revolve147  label="removeToCreateScrewAndThreadedInsertHole053"
  Angle = 360
  Axis = (0,1,0)
  Base = (0,0,0)
  FaceMakerClass = Part::FaceMakerBullseye
  Placement = pos=(109.5,4.7,3.5) rot=(0,0,1;0rad)
  Solid = false
  Source = -> Face139
  Symmetric = false
FEATURE [Part::Feature] Face140
  shape: bbox 3.5 x 17.8 x 2e-07 mm, 1 faces, 0 solids (baked)
FEATURE [Part::Revolution] Revolve148  label="removeToCreateScrewAndThreadedInsertHole054"
  Angle = 360
  Axis = (0,1,0)
  Base = (0,0,0)
  FaceMakerClass = Part::FaceMakerBullseye
  Placement = pos=(109.5,4.7,68.5) rot=(0,0,1;0rad)
  Solid = false
  Source = -> Face140
  Symmetric = false
FEATURE [Part::MultiFuse] Fusion114  label="removeToCreateScrewAndThreadedInsertHole055"
  Shapes = -> [Revolve148,Revolve147,Revolve146,Revolve145,Revolve144,Revolve143]
FEATURE [Part::Cut] Cut047  label="casePillars004"
  Base = -> Cut037
  Tool = -> Fusion114
FEATURE [Part::Feature] Face141
  shape: bbox 3.5 x 17.8 x 2e-07 mm, 1 faces, 0 solids (baked)
FEATURE [Part::Feature] Face142
  shape: bbox 3.5 x 17.8 x 2e-07 mm, 1 faces, 0 solids (baked)
FEATURE [Part::Feature] Face143
  shape: bbox 3.5 x 17.8 x 2e-07 mm, 1 faces, 0 solids (baked)
FEATURE [Part::Revolution] Revolve149  label="removeToCreateScrewAndThreadedInsertHole057"
  Angle = 360
  Axis = (0,1,0)
  Base = (0,0,0)
  FaceMakerClass = Part::FaceMakerBullseye
  Placement = pos=(12.5,0,10) rot=(0,0,1;0rad)
  Solid = false
  Source = -> Face141
  Symmetric = false
FEATURE [Part::Feature] Face144
  shape: bbox 3.5 x 17.8 x 2e-07 mm, 1 faces, 0 solids (baked)
FEATURE [Part::Feature] Face145
  shape: bbox 3.5 x 17.8 x 2e-07 mm, 1 faces, 0 solids (baked)
FEATURE [Part::Feature] Face146
  shape: bbox 3.5 x 17.8 x 2e-07 mm, 1 faces, 0 solids (baked)
FEATURE [Part::Revolution] Revolve150  label="removeToCreateScrewAndThreadedInsertHole058"
  Angle = 360
  Axis = (0,1,0)
  Base = (0,0,0)
  FaceMakerClass = Part::FaceMakerBullseye
  Placement = pos=(12.5,0,62) rot=(0,0,1;0rad)
  Solid = false
  Source = -> Face146
  Symmetric = false
FEATURE [Part::Revolution] Revolve151  label="removeToCreateScrewAndThreadedInsertHole059"
  Angle = 360
  Axis = (0,1,0)
  Base = (0,0,0)
  FaceMakerClass = Part::FaceMakerBullseye
  Placement = pos=(89.5,0,68.5) rot=(0,0,1;0rad)
  Solid = false
  Source = -> Face143
  Symmetric = false
FEATURE [Part::Revolution] Revolve152  label="removeToCreateScrewAndThreadedInsertHole060"
  Angle = 360
  Axis = (0,1,0)
  Base = (0,0,0)
  FaceMakerClass = Part::FaceMakerBullseye
  Placement = pos=(89.5,0,3.5) rot=(0,0,1;0rad)
  Solid = false
  Source = -> Face142
  Symmetric = false
FEATURE [Part::Revolution] Revolve153  label="removeToCreateScrewAndThreadedInsertHole061"
  Angle = 360
  Axis = (0,1,0)
  Base = (0,0,0)
  FaceMakerClass = Part::FaceMakerBullseye
  Placement = pos=(109.5,4.7,3.5) rot=(0,0,1;0rad)
  Solid = false
  Source = -> Face145
  Symmetric = false
FEATURE [Part::Revolution] Revolve154  label="removeToCreateScrewAndThreadedInsertHole062"
  Angle = 360
  Axis = (0,1,0)
  Base = (0,0,0)
  FaceMakerClass = Part::FaceMakerBullseye
  Placement = pos=(109.5,4.7,68.5) rot=(0,0,1;0rad)
  Solid = false
  Source = -> Face144
  Symmetric = false
FEATURE [Part::MultiFuse] Fusion115  label="removeToCreateScrewAndThreadedInsertHole056"
  Shapes = -> [Revolve154,Revolve153,Revolve152,Revolve151,Revolve150,Revolve149]
FEATURE [Part::Feature] Face147
  shape: bbox 9.8 x 26.5 x 2e-07 mm, 1 faces, 0 solids (baked)
FEATURE [Part::Revolution] Revolve155
  Angle = 360
  Axis = (0,1,0)
  Base = (0,0,0)
  FaceMakerClass = Part::FaceMakerBullseye
  Placement = pos=(0,0,0) rot=(0,0,1;1.5708rad)
  Solid = false
  Source = -> Face147
  Symmetric = false
FEATURE [Part::Feature] Face148
  shape: bbox 9.8 x 26.5 x 2e-07 mm, 1 faces, 0 solids (baked)
FEATURE [Part::Revolution] Revolve156
  Angle = 360
  Axis = (0,1,0)
  Base = (0,0,0)
  FaceMakerClass = Part::FaceMakerBullseye
  Placement = pos=(0,0,0) rot=(0,0,1;1.5708rad)
  Solid = false
  Source = -> Face148
  Symmetric = false
FEATURE [Part::MultiFuse] Fusion116
  Placement = pos=(-18,19,36) rot=(0,0,1;0rad)
  Shapes = -> [Revolve156,Revolve155]
FEATURE [Part::Box] Box029  label="Cube016"
  AttacherType = Attacher::AttachEngine3D
  Height = 28
  Length = 3
  Placement = pos=(110.7,19,22) rot=(0,0,1;0rad)
  Width = 15.7
FEATURE [Part::Cylinder] Cylinder046
  Angle = 360
  AttacherType = Attacher::AttachEngine3D
  Height = 10
  Placement = pos=(0,0,36.15) rot=(0,0,1;0rad)
  Radius = 4
FEATURE [Part::Cylinder] Cylinder047
  Angle = 360
  AttacherType = Attacher::AttachEngine3D
  Height = 20
  Placement = pos=(0,0,36.15) rot=(0,0,1;0rad)
  Radius = 10.3
FEATURE [Part::MultiFuse] Fusion117  label="removeToCreteHoleForPlugHousing041"
  Placement = pos=(70,19,36) rot=(0,1,0;1.5708rad)
  Shapes = -> [Cylinder047,Cylinder046]
FEATURE [Part::Cut] Cut049  label="plugHousingTab004"
  Base = -> Box029
  Placement = pos=(-107.4,-14,0) rot=(0,0,1;0rad)
  Tool = -> Fusion117
FEATURE [Part::Box] Box030  label="Cube017"
  AttacherType = Attacher::AttachEngine3D
  Height = 28
  Length = 3
  Placement = pos=(110.7,19,22) rot=(0,0,1;0rad)
  Width = 15.7
FEATURE [Part::Cylinder] Cylinder048
  Angle = 360
  AttacherType = Attacher::AttachEngine3D
  Height = 10
  Placement = pos=(0,0,36.15) rot=(0,0,1;0rad)
  Radius = 4
FEATURE [Part::Cylinder] Cylinder049
  Angle = 360
  AttacherType = Attacher::AttachEngine3D
  Height = 20
  Placement = pos=(0,0,36.15) rot=(0,0,1;0rad)
  Radius = 10.3
FEATURE [Part::MultiFuse] Fusion118  label="removeToCreteHoleForPlugHousing042"
  Placement = pos=(70,19,36) rot=(0,1,0;1.5708rad)
  Shapes = -> [Cylinder049,Cylinder048]
FEATURE [Part::Cut] Cut050  label="plugHousingTab005"
  Base = -> Box030
  Placement = pos=(-107.4,-14,0) rot=(0,0,1;0rad)
  Tool = -> Fusion118
FEATURE [Part::MultiFuse] Fusion119
  Placement = pos=(9.6,23,0) rot=(0,0,1;3.14159rad)
  Shapes = -> [Cut049,Cut050]
FEATURE [Part::Box] Box031  label="Cube018"
  AttacherType = Attacher::AttachEngine3D
  Height = 10
  Length = 3
  Placement = pos=(3.3,4,12) rot=(0,0,1;0rad)
  Width = 10
FEATURE [Part::Fillet] Fillet044
  Base = -> Box031
  Edges = 1 edges r=2: [Edge11]
FEATURE [Part::Box] Box032  label="Cube019"
  AttacherType = Attacher::AttachEngine3D
  Height = 10
  Length = 3
  Placement = pos=(3.3,4,50) rot=(0,0,1;0rad)
  Width = 10
FEATURE [Part::Fillet] Fillet045
  Base = -> Box032
  Edges = 1 edges r=2: [Edge12]
FEATURE [Part::Box] Box033  label="Cube020"
  AttacherType = Attacher::AttachEngine3D
  Height = 28
  Length = 4
  Placement = pos=(5,0,22) rot=(0,0,1;0rad)
  Width = 10
FEATURE [Part::Fillet] Fillet046
  Base = -> Box033
  Edges = 1 edges r=1: [Edge7]
FEATURE [Part::Fillet] Fillet047
  Base = -> Fillet046
  Edges = 1 edges r=2: [Edge5]
FEATURE [Part::Fillet] Fillet048
  Base = -> Fillet047
  Edges = 1 edges r=2: [Edge2]
FEATURE [Part::Cylinder] Cylinder050
  Angle = 360
  AttacherType = Attacher::AttachEngine3D
  Height = 20
  Placement = pos=(0,0,36.15) rot=(0,0,1;0rad)
  Radius = 8.2
FEATURE [Part::Cylinder] Cylinder051
  Angle = 360
  AttacherType = Attacher::AttachEngine3D
  Height = 10
  Placement = pos=(0,0,36.15) rot=(0,0,1;0rad)
  Radius = 4
FEATURE [Part::MultiFuse] Fusion120  label="removeToCreteHoleForPlugHousing043"
  Placement = pos=(-42,19,36) rot=(0,1,0;1.5708rad)
  Shapes = -> [Cylinder050,Cylinder051]
FEATURE [Sketcher::SketchObject] Sketch067  label="topSketch018"
  FullyConstrained = true
  sketch-geometry (4):
    g0: LineSegment StartX=16.8446 StartY=31.512 StartZ=0 EndX=16.3251 EndY=34.4666 EndZ=0
    g1: ArcOfCircle CenterX=19 CenterY=19.2524 CenterZ=0 NormalX=0 NormalY=0 NormalZ=1 AngleXU=0 Radius=15.4476 StartAngle=1.74483 EndAngle=2.72717
    g2: ArcOfCircle CenterX=19 CenterY=19.2524 CenterZ=0 NormalX=0 NormalY=0 NormalZ=1 AngleXU=0 Radius=12.4476 StartAngle=1.74483 EndAngle=2.73189
    g3: LineSegment StartX=4.86004 StartY=25.4725 StartZ=0 EndX=7.58253 EndY=24.2107 EndZ=0
  constraints (7):
    c: Block(g0)
    c: Coincident(g1,g0)
    c: Coincident(g2,g0)
    c: Coincident(g3,g1)
    c: Coincident(g3,g2)
    c: Block(g1)
    c: Block(g2)
FEATURE [Part::Extrusion] Extrude058
  Base = -> Sketch067
  Dir = (0,0,1)
  DirMode = 2
  FaceMakerClass = Part::FaceMakerBullseye
  LengthFwd = 10
  LengthRev = 0
  Placement = pos=(0,0,31) rot=(0,0,1;0rad)
  Solid = true
  Symmetric = false
FEATURE [Part::Cut] Cut051
  Base = -> Extrude058
  Tool = -> Fusion120
FEATURE [Part::Fillet] Fillet049
  Base = -> Cut051
  Edges = 1 edges r=2: [Edge1]
FEATURE [Part::Fillet] Fillet050
  Base = -> Fillet049
  Edges = 1 edges r=2.5: [Edge1]
FEATURE [Part::Fillet] Fillet051
  Base = -> Fillet050
  Edges = 1 edges r=2.5: [Edge2]
FEATURE [Part::MultiFuse] Fusion121  label="wireHolder003"
  Shapes = -> [Fusion116,Fillet051]
FEATURE [Part::MultiFuse] Fusion122
  Shapes = -> [Fillet045,Fusion121]
FEATURE [Part::MultiFuse] Fusion123  label="wireHolder004"
  Shapes = -> [Fusion122,Fillet048]
FEATURE [Part::MultiFuse] Fusion124  label="wireHolder005"
  Shapes = -> [Fillet044,Fusion119,Fusion123]
FEATURE [Sketcher::SketchObject] Sketch068  label="topSketch019"
  FullyConstrained = true
  sketch-geometry (6):
    g0: LineSegment StartX=19 StartY=38 StartZ=0 EndX=117 EndY=38 EndZ=0
    g1: ArcOfCircle CenterX=19 CenterY=19 CenterZ=0 NormalX=0 NormalY=0 NormalZ=1 AngleXU=0 Radius=19 StartAngle=1.5708 EndAngle=3.14159
    g2: LineSegment StartX=117 StartY=38 StartZ=0 EndX=117 EndY=19 EndZ=0
    g3: LineSegment StartX=98 StartY=1.0161e-12 StartZ=0 EndX=5.22862e-06 EndY=1.0161e-12 EndZ=0
    g4: LineSegment StartX=5.22862e-06 StartY=19 StartZ=0 EndX=5.22862e-06 EndY=1.0161e-12 EndZ=0
    g5: ArcOfCircle CenterX=98 CenterY=19 CenterZ=0 NormalX=0 NormalY=0 NormalZ=1 AngleXU=0 Radius=19 StartAngle=4.71239 EndAngle=6.28319
  constraints (16):
    c: Horizontal(g0)
    c: Distance(g0) = 98
    c: Coincident(g1,g0)
    c: Block(g1)
    c: Coincident(g2,g0)
    c: Vertical(g2)
    c: Distance(g2) = 19
    c: Horizontal(g3)
    c: Coincident(g4,g1)
    c: Vertical(g4)
    c: Coincident(g3,g4)
    c: Block(g3)
    c: Coincident(g5,g2)
    c: Coincident(g5,g3)
    c: Block(g0)
    c: Block(g5)
FEATURE [Part::Extrusion] Extrude059  label="sideA002"
  Base = -> Sketch068
  Dir = (0,0,1)
  DirMode = 2
  FaceMakerClass = Part::FaceMakerBullseye
  LengthFwd = 3
  LengthRev = 0
  Placement = pos=(0,0,-2.7) rot=(0,0,1;0rad)
  Solid = true
  Symmetric = false
FEATURE [Sketcher::SketchObject] Sketch069  label="topSketch020"
  FullyConstrained = true
  sketch-geometry (6):
    g0: LineSegment StartX=19 StartY=38 StartZ=0 EndX=117 EndY=38 EndZ=0
    g1: ArcOfCircle CenterX=19 CenterY=19 CenterZ=0 NormalX=0 NormalY=0 NormalZ=1 AngleXU=0 Radius=19 StartAngle=1.5708 EndAngle=3.14159
    g2: LineSegment StartX=117 StartY=38 StartZ=0 EndX=117 EndY=19 EndZ=0
    g3: LineSegment StartX=98 StartY=1.0161e-12 StartZ=0 EndX=5.22862e-06 EndY=1.0161e-12 EndZ=0
    g4: LineSegment StartX=5.22862e-06 StartY=19 StartZ=0 EndX=5.22862e-06 EndY=1.0161e-12 EndZ=0
    g5: ArcOfCircle CenterX=98 CenterY=19 CenterZ=0 NormalX=0 NormalY=0 NormalZ=1 AngleXU=0 Radius=19 StartAngle=4.71239 EndAngle=6.28319
  constraints (16):
    c: Horizontal(g0)
    c: Distance(g0) = 98
    c: Coincident(g1,g0)
    c: Block(g1)
    c: Coincident(g2,g0)
    c: Vertical(g2)
    c: Distance(g2) = 19
    c: Horizontal(g3)
    c: Coincident(g4,g1)
    c: Vertical(g4)
    c: Coincident(g3,g4)
    c: Block(g3)
    c: Coincident(g5,g2)
    c: Coincident(g5,g3)
    c: Block(g0)
    c: Block(g5)
FEATURE [Part::Extrusion] Extrude060  label="sideB002"
  Base = -> Sketch069
  Dir = (0,0,1)
  DirMode = 2
  FaceMakerClass = Part::FaceMakerBullseye
  LengthFwd = 3
  LengthRev = 0
  Placement = pos=(0,0,71.7) rot=(0,0,1;0rad)
  Solid = true
  Symmetric = false
FEATURE [Part::MultiFuse] Fusion127  label="removeFromBottom001"
  Placement = pos=(2,0,0) rot=(0,0,1;0rad)
  Shapes = -> [Extrude059,Extrude060]
FEATURE [Part::Cylinder] Cylinder052
  Angle = 360
  AttacherType = Attacher::AttachEngine3D
  Height = 20
  Placement = pos=(0,0,36.15) rot=(0,0,1;0rad)
  Radius = 14
FEATURE [Part::Cylinder] Cylinder053
  Angle = 360
  AttacherType = Attacher::AttachEngine3D
  Height = 10
  Placement = pos=(0,0,36.15) rot=(0,0,1;0rad)
  Radius = 4
FEATURE [Part::MultiFuse] Fusion128  label="removeToCreteHoleForPlugHousing044"
  Placement = pos=(70,19,36) rot=(0,1,0;1.5708rad)
  Shapes = -> [Cylinder052,Cylinder053]
FEATURE [Part::Cut] Cut052  label="bottom011"
  Base = -> Extrude043
  Tool = -> Fusion128
FEATURE [Part::Cut] Cut054  label="bottom012"
  Base = -> Cut052
  Tool = -> Fusion115
FEATURE [Sketcher::SketchObject] Sketch070
  FullyConstrained = true
  Placement = pos=(117,19,0) rot=(0.57735,0.57735,0.57735;2.0944rad)
  sketch-geometry (48):
    g0: LineSegment StartX=-49.19 StartY=69.25 StartZ=0 EndX=-49.19 EndY=66.25 EndZ=0
    g1: LineSegment StartX=-49.19 StartY=63.5 StartZ=0 EndX=-49.19 EndY=60.5 EndZ=0
    g2: LineSegment StartX=-49.19 StartY=57.75 StartZ=0 EndX=-49.19 EndY=54.75 EndZ=0
    g3: LineSegment StartX=-49.19 StartY=52 StartZ=0 EndX=-49.19 EndY=49 EndZ=0
    g4: LineSegment StartX=-49.19 StartY=46.25 StartZ=0 EndX=-49.19 EndY=43.25 EndZ=0
    g5: LineSegment StartX=-49.19 StartY=40.5 StartZ=0 EndX=-49.19 EndY=37.5 EndZ=0
    g6: LineSegment StartX=-49.19 StartY=34.5 StartZ=0 EndX=-49.19 EndY=31.5 EndZ=0
    g7: LineSegment StartX=-49.19 StartY=28.75 StartZ=0 EndX=-49.19 EndY=25.75 EndZ=0
    g8: LineSegment StartX=-49.19 StartY=23 StartZ=0 EndX=-49.19 EndY=20 EndZ=0
    g9: LineSegment StartX=-49.19 StartY=17.25 StartZ=0 EndX=-49.19 EndY=14.25 EndZ=0
    g10: LineSegment StartX=-49.19 StartY=11.5 StartZ=0 EndX=-49.19 EndY=8.5 EndZ=0
    g11: LineSegment StartX=-49.19 StartY=5.75 StartZ=0 EndX=-49.19 EndY=2.75 EndZ=0
    g12: ArcOfCircle CenterX=-1.5 CenterY=67.75 CenterZ=0 NormalX=0 NormalY=0 NormalZ=1 AngleXU=0 Radius=1.5 StartAngle=4.71239 EndAngle=7.85398
    g13: ArcOfCircle CenterX=-1.5 CenterY=62 CenterZ=0 NormalX=0 NormalY=0 NormalZ=1 AngleXU=0 Radius=1.5 StartAngle=4.71239 EndAngle=7.85398
    g14: ArcOfCircle CenterX=-1.5 CenterY=56.25 CenterZ=0 NormalX=0 NormalY=0 NormalZ=1 AngleXU=0 Radius=1.5 StartAngle=4.71239 EndAngle=7.85398
    g15: ArcOfCircle CenterX=-11.49 CenterY=50.5 CenterZ=0 NormalX=0 NormalY=0 NormalZ=1 AngleXU=0 Radius=1.5 StartAngle=4.71239 EndAngle=7.85398
    g16: ArcOfCircle CenterX=-16.28 CenterY=44.75 CenterZ=0 NormalX=0 NormalY=0 NormalZ=1 AngleXU=0 Radius=1.5 StartAngle=4.71239 EndAngle=7.85398
    g17: ArcOfCircle CenterX=-18.2337 CenterY=39 CenterZ=0 NormalX=0 NormalY=0 NormalZ=1 AngleXU=0 Radius=1.5 StartAngle=4.71485 EndAngle=7.85398
    g18: ArcOfCircle CenterX=-16.2837 CenterY=27.25 CenterZ=0 NormalX=0 NormalY=0 NormalZ=1 AngleXU=0 Radius=1.5 StartAngle=4.71485 EndAngle=7.85398
    g19: ArcOfCircle CenterX=-18.2337 CenterY=33 CenterZ=0 NormalX=0 NormalY=0 NormalZ=1 AngleXU=0 Radius=1.5 StartAngle=4.71485 EndAngle=7.85398
    g20: ArcOfCircle CenterX=-11.49 CenterY=21.5 CenterZ=0 NormalX=0 NormalY=0 NormalZ=1 AngleXU=0 Radius=1.5 StartAngle=4.71239 EndAngle=7.85398
    g21: ArcOfCircle CenterX=-1.5 CenterY=4.25 CenterZ=0 NormalX=0 NormalY=0 NormalZ=1 AngleXU=0 Radius=1.5 StartAngle=4.71239 EndAngle=7.85398
    g22: ArcOfCircle CenterX=-1.5 CenterY=10 CenterZ=0 NormalX=0 NormalY=0 NormalZ=1 AngleXU=0 Radius=1.5 StartAngle=4.71239 EndAngle=7.85398
    g23: ArcOfCircle CenterX=-1.5 CenterY=15.75 CenterZ=0 NormalX=0 NormalY=0 NormalZ=1 AngleXU=0 Radius=1.5 StartAngle=4.71239 EndAngle=7.85398
    g24: LineSegment StartX=-49.19 StartY=69.25 StartZ=0 EndX=-1.5 EndY=69.25 EndZ=0
    g25: LineSegment StartX=-49.19 StartY=66.25 StartZ=0 EndX=-1.5 EndY=66.25 EndZ=0
    g26: LineSegment StartX=-49.19 StartY=63.5 StartZ=0 EndX=-1.5 EndY=63.5 EndZ=0
    g27: LineSegment StartX=-49.19 StartY=60.5 StartZ=0 EndX=-1.5 EndY=60.5 EndZ=0
    g28: LineSegment StartX=-49.19 StartY=57.75 StartZ=0 EndX=-1.5 EndY=57.75 EndZ=0
    g29: LineSegment StartX=-49.19 StartY=54.75 StartZ=0 EndX=-1.5 EndY=54.75 EndZ=0
    g30: LineSegment StartX=-49.19 StartY=52 StartZ=0 EndX=-11.49 EndY=52 EndZ=0
    g31: LineSegment StartX=-49.19 StartY=49 StartZ=0 EndX=-11.49 EndY=49 EndZ=0
    g32: LineSegment StartX=-49.19 StartY=46.25 StartZ=0 EndX=-16.28 EndY=46.25 EndZ=0
    g33: LineSegment StartX=-49.19 StartY=43.25 StartZ=0 EndX=-16.28 EndY=43.25 EndZ=0
    g34: LineSegment StartX=-49.19 StartY=40.5 StartZ=0 EndX=-18.2337 EndY=40.5 EndZ=0
    g35: LineSegment StartX=-49.19 StartY=37.5 StartZ=0 EndX=-18.23 EndY=37.5 EndZ=0
    g36: LineSegment StartX=-49.19 StartY=34.5 StartZ=0 EndX=-18.2337 EndY=34.5 EndZ=0
    g37: LineSegment StartX=-49.19 StartY=31.5 StartZ=0 EndX=-18.23 EndY=31.5 EndZ=0
    g38: LineSegment StartX=-49.19 StartY=28.75 StartZ=0 EndX=-16.2837 EndY=28.75 EndZ=0
    g39: LineSegment StartX=-49.19 StartY=25.75 StartZ=0 EndX=-16.28 EndY=25.75 EndZ=0
    g40: LineSegment StartX=-49.19 StartY=23 StartZ=0 EndX=-11.49 EndY=23 EndZ=0
    g41: LineSegment StartX=-49.19 StartY=20 StartZ=0 EndX=-11.49 EndY=20 EndZ=0
    g42: LineSegment StartX=-49.19 StartY=17.25 StartZ=0 EndX=-1.5 EndY=17.25 EndZ=0
    g43: LineSegment StartX=-49.19 StartY=14.25 StartZ=0 EndX=-1.5 EndY=14.25 EndZ=0
    g44: LineSegment StartX=-49.19 StartY=11.5 StartZ=0 EndX=-1.5 EndY=11.5 EndZ=0
    g45: LineSegment StartX=-49.19 StartY=8.5 StartZ=0 EndX=-1.5 EndY=8.5 EndZ=0
    g46: LineSegment StartX=-49.19 StartY=5.75 StartZ=0 EndX=-1.5 EndY=5.75 EndZ=0
    g47: LineSegment StartX=-49.19 StartY=2.75 StartZ=0 EndX=-1.5 EndY=2.75 EndZ=0
  constraints (120):
    c: Vertical(g0)
    c: Distance(g0) = 3
    c: Block(g0)
    c: Vertical(g1)
    c: Distance(g1) = 3
    c: Vertical(g2)
    c: Equal(g0,g2) = 3
    c: Block(g2)
    c: Vertical(g3)
    c: Equal(g1,g3) = 3
    c: Vertical(g4)
    c: Equal(g0,g4) = 3
    c: Block(g4)
    c: Vertical(g5)
    c: Equal(g1,g5) = 3
    c: Vertical(g6)
    c: Equal(g0,g6) = 3
    c: Block(g6)
    c: Vertical(g7)
    c: Equal(g1,g7) = 3
    c: Vertical(g8)
    c: Equal(g0,g8) = 3
    c: Block(g8)
    c: Vertical(g9)
    c: Equal(g1,g9) = 3
    c: Vertical(g10)
    c: Equal(g0,g10) = 3
    c: Block(g10)
    c: Vertical(g11)
    c: Equal(g1,g11) = 3
    c: Block(g12)
    c: Block(g13)
    c: Block(g14)
    c: Block(g15)
    c: Block(g16)
    c: Block(g17)
    c: Block(g18)
    c: Block(g19)
    c: Block(g20)
    c: Block(g21)
    c: Block(g22)
    c: Block(g23)
    c: Block(g11)
    c: Block(g9)
    c: Block(g7)
    c: Block(g5)
    c: Block(g3)
    c: Block(g1)
    c: Coincident(g24,g0)
    c: Coincident(g24,g12)
    c: Horizontal(g24)
    c: Coincident(g25,g0)
    c: Coincident(g25,g12)
    c: Horizontal(g25)
    c: Coincident(g26,g1)
    c: Coincident(g26,g13)
    c: Horizontal(g26)
    c: Coincident(g27,g1)
    c: Coincident(g27,g13)
    c: Horizontal(g27)
    c: Coincident(g28,g2)
    c: Coincident(g28,g14)
    c: Horizontal(g28)
    c: Coincident(g29,g2)
    c: Coincident(g29,g14)
    c: Horizontal(g29)
    c: Coincident(g30,g3)
    c: Coincident(g30,g15)
    c: Horizontal(g30)
    c: Coincident(g31,g3)
    c: Coincident(g31,g15)
    c: Horizontal(g31)
    c: Coincident(g32,g4)
    c: Coincident(g32,g16)
    c: Horizontal(g32)
    c: Coincident(g33,g4)
    c: Coincident(g33,g16)
    c: Horizontal(g33)
    c: Coincident(g34,g5)
    c: Coincident(g34,g17)
    c: Horizontal(g34)
    c: Coincident(g35,g5)
    c: Coincident(g35,g17)
    c: Horizontal(g35)
    c: Coincident(g36,g6)
    c: Coincident(g36,g19)
    c: Horizontal(g36)
    c: Coincident(g37,g6)
    c: Coincident(g37,g19)
    c: Horizontal(g37)
    c: Coincident(g38,g7)
    c: Coincident(g38,g18)
    c: Horizontal(g38)
    c: Coincident(g39,g7)
    c: Coincident(g39,g18)
    c: Horizontal(g39)
    c: Coincident(g40,g8)
    c: Coincident(g40,g20)
    c: Horizontal(g40)
    c: Coincident(g41,g8)
    c: Coincident(g41,g20)
    c: Horizontal(g41)
    c: Coincident(g42,g9)
    c: Coincident(g42,g23)
    c: Horizontal(g42)
    c: Coincident(g43,g9)
    c: Coincident(g43,g23)
    c: Horizontal(g43)
    c: Coincident(g44,g10)
    c: Coincident(g44,g22)
    c: Horizontal(g44)
    c: Coincident(g45,g10)
    c: Coincident(g45,g22)
    c: Horizontal(g45)
    c: Coincident(g46,g11)
    c: Coincident(g46,g21)
    c: Horizontal(g46)
    c: Coincident(g47,g11)
    c: Coincident(g47,g21)
    c: Horizontal(g47)
FEATURE [Part::Extrusion] Extrude061
  Base = -> Sketch070
  Dir = (1,0,0)
  DirMode = 2
  FaceMakerClass = Part::FaceMakerBullseye
  LengthFwd = 23
  LengthRev = 0
  Placement = pos=(-19,0,0) rot=(0,0,1;0rad)
  Solid = true
  Symmetric = false
FEATURE [Part::Fillet] Fillet052  label="removeToCreateVentalationHoles002"
  Base = -> Extrude061
  Edges = <same value as first occurrence — deduplicated (x6 in doc)>
  Placement = pos=(7,0.02,0) rot=(0,0,1;0rad)
FEATURE [Part::MultiFuse] Fusion130  label="bottom013"
  Shapes = -> [Cut054,Cut034]
FEATURE [Part::Cut] Cut055
  Base = -> Fusion130
  Tool = -> Fillet052
FEATURE [Part::Cylinder] Cylinder054
  Angle = 360
  AttacherType = Attacher::AttachEngine3D
  Height = 20
  Placement = pos=(0,0,36.15) rot=(0,0,1;0rad)
  Radius = 4
FEATURE [Sketcher::SketchObject] Sketch071  label="bottomSketch002"
  FullyConstrained = true
  sketch-geometry (32):
    g0: LineSegment StartX=3.3 StartY=-6.03275e-07 StartZ=0 EndX=98 EndY=-6.03275e-07 EndZ=0
    g1: ArcOfCircle CenterX=98 CenterY=19 CenterZ=0 NormalX=0 NormalY=0 NormalZ=1 AngleXU=0 Radius=19 StartAngle=4.71239 EndAngle=5.71103
    g2: LineSegment StartX=6.3 StartY=8 StartZ=0 EndX=3.3 EndY=8 EndZ=0
    g3: LineSegment StartX=3.3 StartY=8 StartZ=0 EndX=3.3 EndY=-6.03275e-07 EndZ=0
    g4: ArcOfCircle CenterX=8.3 CenterY=5 CenterZ=0 NormalX=0 NormalY=0 NormalZ=1 AngleXU=0 Radius=2 StartAngle=3.14159 EndAngle=4.71239
    g5: LineSegment StartX=6.3 StartY=8 StartZ=0 EndX=6.3 EndY=5 EndZ=0
    g6: ArcOfCircle CenterX=98 CenterY=19 CenterZ=0 NormalX=0 NormalY=0 NormalZ=1 AngleXU=0 Radius=12.7 StartAngle=4.71239 EndAngle=6.28319
    g7: LineSegment StartX=94.7 StartY=3 StartZ=0 EndX=8.3 EndY=3 EndZ=0
    g8-g12: Circle x5 (B-spline internal-alignment scaffolding for g13; pole/knot coordinates omitted)
    g13: BSplineCurve PolesCount=5 KnotsCount=3 Degree=3 IsPeriodic=0
    g14: GeomPoint X=98 Y=6.3 Z=0
    g15: GeomPoint X=96.3938 Y=4.71946 Z=0
    g16: GeomPoint X=94.7 Y=3 Z=0
    g17-g23: Circle x7 (B-spline internal-alignment scaffolding for g24; pole/knot coordinates omitted)
    g24: BSplineCurve PolesCount=7 KnotsCount=5 Degree=3 IsPeriodic=0
    g25-g29: GeomPoint x5 (B-spline internal-alignment scaffolding for g24; pole/knot coordinates omitted)
    g30: ArcOfCircle CenterX=98 CenterY=19 CenterZ=0 NormalX=0 NormalY=0 NormalZ=1 AngleXU=0 Radius=15.7 StartAngle=5.81226 EndAngle=6.28319
    g31: LineSegment StartX=110.7 StartY=19 StartZ=0 EndX=113.7 EndY=19 EndZ=0
  constraints (41):
    c: Horizontal(g0)
    c: Coincident(g1,g0)
    c: Block(g1)
    c: Horizontal(g2)
    c: Distance(g2) = 3
    c: Coincident(g3,g2)
    c: Vertical(g3)
    c: Coincident(g3,g0)
    c: Block(g4)
    c: Block(g2)
    c: Coincident(g5,g2)
    c: Coincident(g5,g4)
    c: Vertical(g5)
    c: Coincident(g6,g1)
    c: Block(g6)
    c: Coincident(g7,g4)
    c: Horizontal(g7)
    c: Block(g0)
    c: Block(g7)
    c: Block(g3)
    c: Coincident(g13,g6)
    c: Weight(g8) = 1
    c: Equal(g8, g9-g12) x4
    c: Coincident(g13,g7)
    c: InternalAlignment(g8-g12 -> g13) x5
    c: InternalAlignment(g14,g13)
    c: InternalAlignment(g15,g13)
    c: InternalAlignment(g16,g13)
    c: Block(g13)
    c: Weight(g17) = 1
    c: Equal(g17, g18-g23) x6
    c: Coincident(g24,g1)
    c: InternalAlignment(g17-g23 -> g24) x7
    c: InternalAlignment(g25-g29 -> g24) x5
    c: Block(g24)
    c: Coincident(g30,g24)
    c: Coincident(g31,g6)
    c: Coincident(g31,g30)
    c: Horizontal(g31)
    c: Block(g31)
    c: Block(g30)
FEATURE [Part::Extrusion] Extrude062  label="bottom014"
  Base = -> Sketch071
  Dir = (0,0,1)
  DirMode = 2
  FaceMakerClass = Part::FaceMakerBullseye
  LengthFwd = 71.4
  LengthRev = 0
  Placement = pos=(0,0,0.3) rot=(0,0,1;0rad)
  Solid = true
  Symmetric = false
FEATURE [Part::Fillet] Fillet054
  Base = -> Extrude062
  Edges = 1 edges r=2.4: [Edge17]
FEATURE [Part::Fillet] Fillet055  label="bottom015"
  Base = -> Fillet054
  Edges = 1 edges r=2.4: [Edge36]
FEATURE [Part::Cylinder] Cylinder055
  Angle = 360
  AttacherType = Attacher::AttachEngine3D
  Height = 10
  Placement = pos=(0,0,36.15) rot=(0,0,1;0rad)
  Radius = 4
FEATURE [Part::MultiFuse] Fusion131  label="removeToCreateHoleForPlugHousing002"
  Placement = pos=(70,19,36.15) rot=(0,1,0;1.5708rad)
  Shapes = -> [Cylinder054,Cylinder055]
FEATURE [Part::Cut] Cut056  label="Bottom001"
  Base = -> Fillet055
  Placement = pos=(9,0,0) rot=(0,0,1;0rad)
  Tool = -> Fusion131
FEATURE [Part::Cut] Cut057
  Base = -> Cut055
  Tool = -> Cut056
FEATURE [Sketcher::SketchObject] Sketch072  label="topSketch021"
  FullyConstrained = true
  sketch-geometry (4):
    g0: ArcOfCircle CenterX=105 CenterY=19 CenterZ=0 NormalX=0 NormalY=0 NormalZ=1 AngleXU=0 Radius=20.6155 StartAngle=5.54125 EndAngle=6.28319
    g1: ArcOfCircle CenterX=105 CenterY=19 CenterZ=0 NormalX=0 NormalY=0 NormalZ=1 AngleXU=0 Radius=13 StartAngle=5.54125 EndAngle=6.28319
    g2: LineSegment StartX=118 StartY=19 StartZ=0 EndX=125.616 EndY=19 EndZ=0
    g3: LineSegment StartX=114.583 StartY=10.2157 StartZ=0 EndX=120.197 EndY=5.06982 EndZ=0
  constraints (7):
    c: Block(g0)
    c: Block(g1)
    c: Coincident(g2,g1)
    c: Coincident(g2,g0)
    c: Horizontal(g2)
    c: Coincident(g3,g1)
    c: Coincident(g3,g0)
FEATURE [Part::Extrusion] Extrude063  label="bottomPlugHousingBit003"
  Base = -> Sketch072
  Dir = (0,0,1)
  DirMode = 2
  FaceMakerClass = Part::FaceMakerBullseye
  LengthFwd = 72
  LengthRev = 0
  Solid = true
  Symmetric = false
FEATURE [Part::Cylinder] Cylinder056
  Angle = 360
  AttacherType = Attacher::AttachEngine3D
  Height = 20
  Placement = pos=(0,0,36.15) rot=(0,0,1;0rad)
  Radius = 14.3
FEATURE [Part::Cylinder] Cylinder057
  Angle = 360
  AttacherType = Attacher::AttachEngine3D
  Height = 10
  Placement = pos=(0,0,36.15) rot=(0,0,1;0rad)
  Radius = 4
FEATURE [Part::Box] Box034  label="removeToCreteHoleForPlugHousing047"
  AttacherType = Attacher::AttachEngine3D
  Height = 28.6
  Length = 20
  Placement = pos=(106.15,0,21.7) rot=(0,0,1;0rad)
  Width = 19
FEATURE [Part::Cylinder] Cylinder058
  Angle = 360
  AttacherType = Attacher::AttachEngine3D
  Height = 20
  Placement = pos=(0,0,36.15) rot=(0,0,1;0rad)
  Radius = 14.3
FEATURE [Part::Cylinder] Cylinder059
  Angle = 360
  AttacherType = Attacher::AttachEngine3D
  Height = 10
  Placement = pos=(0,0,36.15) rot=(0,0,1;0rad)
  Radius = 4
FEATURE [Part::MultiFuse] Fusion134  label="removeToCreteHoleForPlugHousing046"
  Placement = pos=(70,19,36) rot=(0,1,0;1.5708rad)
  Shapes = -> [Cylinder058,Cylinder059]
FEATURE [Part::Cylinder] Cylinder060
  Angle = 360
  AttacherType = Attacher::AttachEngine3D
  Height = 20
  Placement = pos=(0,0,36.15) rot=(0,0,1;0rad)
  Radius = 14
FEATURE [Part::Cylinder] Cylinder061
  Angle = 360
  AttacherType = Attacher::AttachEngine3D
  Height = 10
  Placement = pos=(0,0,36.15) rot=(0,0,1;0rad)
  Radius = 4
FEATURE [Part::MultiFuse] Fusion135  label="removeToCreteHoleForPlugHousing048"
  Placement = pos=(70,19,36) rot=(0,1,0;1.5708rad)
  Shapes = -> [Cylinder060,Cylinder061]
FEATURE [Part::Box] Box035  label="removeToCreteHoleForPlugHousing049"
  AttacherType = Attacher::AttachEngine3D
  Height = 28.6
  Length = 20
  Placement = pos=(106.15,0,21.7) rot=(0,0,1;0rad)
  Width = 19
FEATURE [Part::MultiFuse] Fusion133  label="removeToCreteHoleForPlugHousing045"
  Placement = pos=(0,0,-28.3) rot=(0,0,1;0rad)
  Shapes = -> [Box035,Fusion134]
FEATURE [Part::MultiFuse] Fusion138  label="removeToCreteHoleForPlugHousing051"
  Placement = pos=(70,19,36) rot=(0,1,0;1.5708rad)
  Shapes = -> [Cylinder056,Cylinder057]
FEATURE [Part::MultiFuse] Fusion137  label="removeToCreteHoleForPlugHousing050"
  Placement = pos=(0,0,28.3) rot=(0,0,1;0rad)
  Shapes = -> [Box034,Fusion138]
FEATURE [Part::MultiFuse] Fusion132  label="removeToCreatePlugHousingBottomBit002"
  Shapes = -> [Fusion133,Fusion137]
FEATURE [Part::MultiFuse] Fusion136  label="removeToCreatePlugHousingBottomBit003"
  Shapes = -> [Fusion135,Fusion132]
FEATURE [Part::Cut] Cut058  label="bottomPlugHousingBit002"
  Base = -> Extrude063
  Placement = pos=(-0.09,0,0) rot=(0,0,1;0rad)
  Tool = -> Fusion136
FEATURE [Sketcher::SketchObject] Sketch073  label="bottomSketch003"
  FullyConstrained = true
  sketch-geometry (45):
    g0: LineSegment StartX=6.29999 StartY=8 StartZ=0 EndX=3.29999 EndY=8 EndZ=0
    g1: LineSegment StartX=3.29999 StartY=8 StartZ=0 EndX=3.29999 EndY=-6.03275e-07 EndZ=0
    g2: ArcOfCircle CenterX=8.29999 CenterY=5 CenterZ=0 NormalX=0 NormalY=0 NormalZ=1 AngleXU=0 Radius=2 StartAngle=3.14159 EndAngle=4.71239
    g3: LineSegment StartX=6.29999 StartY=8 StartZ=0 EndX=6.29999 EndY=5 EndZ=0
    g4: ArcOfCircle CenterX=105 CenterY=19 CenterZ=0 NormalX=0 NormalY=0 NormalZ=1 AngleXU=0 Radius=12.7 StartAngle=4.71239 EndAngle=5.94289
    g5-g11: Circle x7 (B-spline internal-alignment scaffolding for g12; pole/knot coordinates omitted)
    g12: BSplineCurve PolesCount=7 KnotsCount=5 Degree=3 IsPeriodic=0
    g13-g17: GeomPoint x5 (B-spline internal-alignment scaffolding for g12; pole/knot coordinates omitted)
    g18: ArcOfCircle CenterX=105 CenterY=19 CenterZ=0 NormalX=0 NormalY=0 NormalZ=1 AngleXU=0 Radius=15.7 StartAngle=5.81226 EndAngle=6.28319
    g19: BSplineCurve PolesCount=5 KnotsCount=3 Degree=3 IsPeriodic=0
    g20: LineSegment StartX=8.29999 StartY=3 StartZ=0 EndX=101.7 EndY=3 EndZ=0
    g21: LineSegment StartX=3.29999 StartY=-6.03275e-07 StartZ=0 EndX=105 EndY=-6.03275e-07 EndZ=0
    g22: LineSegment StartX=120.974 StartY=8.71251 StartZ=0 EndX=122.332 EndY=7.83778 EndZ=0
    g23: LineSegment StartX=105 StartY=-6.03274e-07 StartZ=0 EndX=113 EndY=-6.03274e-07 EndZ=0
    g24: ArcOfCircle CenterX=105 CenterY=19 CenterZ=0 NormalX=0 NormalY=0 NormalZ=1 AngleXU=0 Radius=20.6155 StartAngle=5.11091 EndAngle=5.71103
    g25: ArcOfCircle CenterX=117.7 CenterY=19 CenterZ=0 NormalX=0 NormalY=0 NormalZ=1 AngleXU=0 Radius=3 StartAngle=1.2e-15 EndAngle=2.10468
    g26: Circle CenterX=116.345 CenterY=16.3232 CenterZ=0 NormalX=0 NormalY=0 NormalZ=1 AngleXU=0 Radius=1
    g27: Circle CenterX=117.24 CenterY=15.7584 CenterZ=0 NormalX=0 NormalY=0 NormalZ=1 AngleXU=0 Radius=1
    g28: Circle CenterX=116.972 CenterY=14.7612 CenterZ=0 NormalX=0 NormalY=0 NormalZ=1 AngleXU=0 Radius=1
    g29: BSplineCurve PolesCount=3 KnotsCount=2 Degree=2 IsPeriodic=0
    g30: GeomPoint X=116.345 Y=16.3232 Z=0
    g31: GeomPoint X=116.972 Y=14.7612 Z=0
    g32: Circle CenterX=115.828 CenterY=17.157 CenterZ=0 NormalX=0 NormalY=0 NormalZ=1 AngleXU=0 Radius=1
    g33: Circle CenterX=115.841 CenterY=16.639 CenterZ=0 NormalX=0 NormalY=0 NormalZ=1 AngleXU=0 Radius=1
    g34: Circle CenterX=116.345 CenterY=16.3232 CenterZ=0 NormalX=0 NormalY=0 NormalZ=1 AngleXU=0 Radius=1
    g35: BSplineCurve PolesCount=3 KnotsCount=2 Degree=2 IsPeriodic=0
    g36: GeomPoint X=115.828 Y=17.157 Z=0
    g37: GeomPoint X=116.345 Y=16.3232 Z=0
    g38: LineSegment StartX=115.828 StartY=17.157 StartZ=0 EndX=115.828 EndY=20.8307 EndZ=0
    g39: Circle CenterX=115.828 CenterY=20.8307 CenterZ=0 NormalX=0 NormalY=0 NormalZ=1 AngleXU=0 Radius=1
    g40: Circle CenterX=115.831 CenterY=21.3396 CenterZ=0 NormalX=0 NormalY=0 NormalZ=1 AngleXU=0 Radius=1
    g41: Circle CenterX=116.173 CenterY=21.5825 CenterZ=0 NormalX=0 NormalY=0 NormalZ=1 AngleXU=0 Radius=1
    g42: BSplineCurve PolesCount=3 KnotsCount=2 Degree=2 IsPeriodic=0
    g43: GeomPoint X=115.828 Y=20.8307 Z=0
    g44: GeomPoint X=116.173 Y=21.5825 Z=0
  constraints (70):
    c: Horizontal(g0)
    c: Distance(g0) = 3
    c: Coincident(g1,g0)
    c: Vertical(g1)
    c: Block(g2)
    c: Block(g0)
    c: Coincident(g3,g0)
    c: Coincident(g3,g2)
    c: Vertical(g3)
    c: Block(g1)
    c: Block(g4)
    c: Coincident(g19,g4)
    c: Block(g19)
    c: Equal(g5, g6-g11) x6
    c: InternalAlignment(g5-g11 -> g12) x7
    c: InternalAlignment(g13-g17 -> g12) x5
    c: Block(g12)
    c: Coincident(g18,g12)
    c: Block(g18)
    c: Coincident(g20,g2)
    c: Coincident(g20,g19)
    c: Horizontal(g20)
    c: Distance(g20) = 93.4
    c: Coincident(g21,g1)
    c: Horizontal(g21)
    c: Distance(g21) = 101.7
    c: Horizontal(g23)
    c: Distance(g23) = 8
    c: Coincident(g24,g23)
    c: Block(g23)
    c: Coincident(g22,g24)
    c: Block(g24)
    c: Block(g22)
    c: Distance(g22) = 1.61553
    c: Coincident(g25,g18)
    c: Block(g25)
    c: Weight(g26) = 1
    c: Equal(g26,g27)
    c: Equal(g26,g28)
    c: Coincident(g29,g4)
    c: InternalAlignment(g26,g29)
    c: InternalAlignment(g27,g29)
    c: InternalAlignment(g28,g29)
    c: InternalAlignment(g30,g29)
    c: InternalAlignment(g31,g29)
    c: Block(g29)
    c: Weight(g32) = 1
    c: Equal(g32,g33)
    c: Equal(g32,g34)
    c: Coincident(g35,g29)
    c: InternalAlignment(g32,g35)
    c: InternalAlignment(g33,g35)
    c: InternalAlignment(g34,g35)
    c: InternalAlignment(g36,g35)
    c: InternalAlignment(g37,g35)
    c: Block(g35)
    c: Coincident(g38,g35)
    c: Vertical(g38)
    c: Block(g38)
    c: Coincident(g42,g38)
    c: Weight(g39) = 1
    c: Equal(g39,g40)
    c: Equal(g39,g41)
    c: Coincident(g42,g25)
    c: InternalAlignment(g39,g42)
    c: InternalAlignment(g40,g42)
    c: InternalAlignment(g41,g42)
    c: InternalAlignment(g43,g42)
    c: InternalAlignment(g44,g42)
    c: Block(g42)
FEATURE [Part::Extrusion] Extrude064  label="bottom016"
  Base = -> Sketch073
  Dir = (0,0,1)
  DirMode = 2
  FaceMakerClass = Part::FaceMakerBullseye
  LengthFwd = 71.4
  LengthRev = 0
  Placement = pos=(0,0,0.3) rot=(0,0,1;0rad)
  Solid = true
  Symmetric = false
FEATURE [Part::Revolution] Revolve157  label="removeToCreateScrewAndThreadedInsertHole063"
  Angle = 360
  Axis = (0,1,0)
  Base = (0,0,0)
  FaceMakerClass = Part::FaceMakerBullseye
  Placement = pos=(12.5,0,10) rot=(0,0,1;0rad)
  Solid = false
  Source = -> Face141
  Symmetric = false
FEATURE [Sketcher::SketchObject] Sketch074
  FullyConstrained = true
  Placement = pos=(117,19,0) rot=(0.57735,0.57735,0.57735;2.0944rad)
  sketch-geometry (48):
    g0: LineSegment StartX=-49.19 StartY=69.25 StartZ=0 EndX=-49.19 EndY=66.25 EndZ=0
    g1: LineSegment StartX=-49.19 StartY=63.5 StartZ=0 EndX=-49.19 EndY=60.5 EndZ=0
    g2: LineSegment StartX=-49.19 StartY=57.75 StartZ=0 EndX=-49.19 EndY=54.75 EndZ=0
    g3: LineSegment StartX=-49.19 StartY=52 StartZ=0 EndX=-49.19 EndY=49 EndZ=0
    g4: LineSegment StartX=-49.19 StartY=46.25 StartZ=0 EndX=-49.19 EndY=43.25 EndZ=0
    g5: LineSegment StartX=-49.19 StartY=40.5 StartZ=0 EndX=-49.19 EndY=37.5 EndZ=0
    g6: LineSegment StartX=-49.19 StartY=34.5 StartZ=0 EndX=-49.19 EndY=31.5 EndZ=0
    g7: LineSegment StartX=-49.19 StartY=28.75 StartZ=0 EndX=-49.19 EndY=25.75 EndZ=0
    g8: LineSegment StartX=-49.19 StartY=23 StartZ=0 EndX=-49.19 EndY=20 EndZ=0
    g9: LineSegment StartX=-49.19 StartY=17.25 StartZ=0 EndX=-49.19 EndY=14.25 EndZ=0
    g10: LineSegment StartX=-49.19 StartY=11.5 StartZ=0 EndX=-49.19 EndY=8.5 EndZ=0
    g11: LineSegment StartX=-49.19 StartY=5.75 StartZ=0 EndX=-49.19 EndY=2.75 EndZ=0
    g12: ArcOfCircle CenterX=-1.5 CenterY=67.75 CenterZ=0 NormalX=0 NormalY=0 NormalZ=1 AngleXU=0 Radius=1.5 StartAngle=4.71239 EndAngle=7.85398
    g13: ArcOfCircle CenterX=-1.5 CenterY=62 CenterZ=0 NormalX=0 NormalY=0 NormalZ=1 AngleXU=0 Radius=1.5 StartAngle=4.71239 EndAngle=7.85398
    g14: ArcOfCircle CenterX=-1.5 CenterY=56.25 CenterZ=0 NormalX=0 NormalY=0 NormalZ=1 AngleXU=0 Radius=1.5 StartAngle=4.71239 EndAngle=7.85398
    g15: ArcOfCircle CenterX=-11.49 CenterY=50.5 CenterZ=0 NormalX=0 NormalY=0 NormalZ=1 AngleXU=0 Radius=1.5 StartAngle=4.71239 EndAngle=7.85398
    g16: ArcOfCircle CenterX=-16.28 CenterY=44.75 CenterZ=0 NormalX=0 NormalY=0 NormalZ=1 AngleXU=0 Radius=1.5 StartAngle=4.71239 EndAngle=7.85398
    g17: ArcOfCircle CenterX=-18.2337 CenterY=39 CenterZ=0 NormalX=0 NormalY=0 NormalZ=1 AngleXU=0 Radius=1.5 StartAngle=4.71485 EndAngle=7.85398
    g18: ArcOfCircle CenterX=-16.2837 CenterY=27.25 CenterZ=0 NormalX=0 NormalY=0 NormalZ=1 AngleXU=0 Radius=1.5 StartAngle=4.71485 EndAngle=7.85398
    g19: ArcOfCircle CenterX=-18.2337 CenterY=33 CenterZ=0 NormalX=0 NormalY=0 NormalZ=1 AngleXU=0 Radius=1.5 StartAngle=4.71485 EndAngle=7.85398
    g20: ArcOfCircle CenterX=-11.49 CenterY=21.5 CenterZ=0 NormalX=0 NormalY=0 NormalZ=1 AngleXU=0 Radius=1.5 StartAngle=4.71239 EndAngle=7.85398
    g21: ArcOfCircle CenterX=-1.5 CenterY=4.25 CenterZ=0 NormalX=0 NormalY=0 NormalZ=1 AngleXU=0 Radius=1.5 StartAngle=4.71239 EndAngle=7.85398
    g22: ArcOfCircle CenterX=-1.5 CenterY=10 CenterZ=0 NormalX=0 NormalY=0 NormalZ=1 AngleXU=0 Radius=1.5 StartAngle=4.71239 EndAngle=7.85398
    g23: ArcOfCircle CenterX=-1.5 CenterY=15.75 CenterZ=0 NormalX=0 NormalY=0 NormalZ=1 AngleXU=0 Radius=1.5 StartAngle=4.71239 EndAngle=7.85398
    g24: LineSegment StartX=-49.19 StartY=69.25 StartZ=0 EndX=-1.5 EndY=69.25 EndZ=0
    g25: LineSegment StartX=-49.19 StartY=66.25 StartZ=0 EndX=-1.5 EndY=66.25 EndZ=0
    g26: LineSegment StartX=-49.19 StartY=63.5 StartZ=0 EndX=-1.5 EndY=63.5 EndZ=0
    g27: LineSegment StartX=-49.19 StartY=60.5 StartZ=0 EndX=-1.5 EndY=60.5 EndZ=0
    g28: LineSegment StartX=-49.19 StartY=57.75 StartZ=0 EndX=-1.5 EndY=57.75 EndZ=0
    g29: LineSegment StartX=-49.19 StartY=54.75 StartZ=0 EndX=-1.5 EndY=54.75 EndZ=0
    g30: LineSegment StartX=-49.19 StartY=52 StartZ=0 EndX=-11.49 EndY=52 EndZ=0
    g31: LineSegment StartX=-49.19 StartY=49 StartZ=0 EndX=-11.49 EndY=49 EndZ=0
    g32: LineSegment StartX=-49.19 StartY=46.25 StartZ=0 EndX=-16.28 EndY=46.25 EndZ=0
    g33: LineSegment StartX=-49.19 StartY=43.25 StartZ=0 EndX=-16.28 EndY=43.25 EndZ=0
    g34: LineSegment StartX=-49.19 StartY=40.5 StartZ=0 EndX=-18.2337 EndY=40.5 EndZ=0
    g35: LineSegment StartX=-49.19 StartY=37.5 StartZ=0 EndX=-18.23 EndY=37.5 EndZ=0
    g36: LineSegment StartX=-49.19 StartY=34.5 StartZ=0 EndX=-18.2337 EndY=34.5 EndZ=0
    g37: LineSegment StartX=-49.19 StartY=31.5 StartZ=0 EndX=-18.23 EndY=31.5 EndZ=0
    g38: LineSegment StartX=-49.19 StartY=28.75 StartZ=0 EndX=-16.2837 EndY=28.75 EndZ=0
    g39: LineSegment StartX=-49.19 StartY=25.75 StartZ=0 EndX=-16.28 EndY=25.75 EndZ=0
    g40: LineSegment StartX=-49.19 StartY=23 StartZ=0 EndX=-11.49 EndY=23 EndZ=0
    g41: LineSegment StartX=-49.19 StartY=20 StartZ=0 EndX=-11.49 EndY=20 EndZ=0
    g42: LineSegment StartX=-49.19 StartY=17.25 StartZ=0 EndX=-1.5 EndY=17.25 EndZ=0
    g43: LineSegment StartX=-49.19 StartY=14.25 StartZ=0 EndX=-1.5 EndY=14.25 EndZ=0
    g44: LineSegment StartX=-49.19 StartY=11.5 StartZ=0 EndX=-1.5 EndY=11.5 EndZ=0
    g45: LineSegment StartX=-49.19 StartY=8.5 StartZ=0 EndX=-1.5 EndY=8.5 EndZ=0
    g46: LineSegment StartX=-49.19 StartY=5.75 StartZ=0 EndX=-1.5 EndY=5.75 EndZ=0
    g47: LineSegment StartX=-49.19 StartY=2.75 StartZ=0 EndX=-1.5 EndY=2.75 EndZ=0
  constraints (120):
    c: Vertical(g0)
    c: Distance(g0) = 3
    c: Block(g0)
    c: Vertical(g1)
    c: Distance(g1) = 3
    c: Vertical(g2)
    c: Equal(g0,g2) = 3
    c: Block(g2)
    c: Vertical(g3)
    c: Equal(g1,g3) = 3
    c: Vertical(g4)
    c: Equal(g0,g4) = 3
    c: Block(g4)
    c: Vertical(g5)
    c: Equal(g1,g5) = 3
    c: Vertical(g6)
    c: Equal(g0,g6) = 3
    c: Block(g6)
    c: Vertical(g7)
    c: Equal(g1,g7) = 3
    c: Vertical(g8)
    c: Equal(g0,g8) = 3
    c: Block(g8)
    c: Vertical(g9)
    c: Equal(g1,g9) = 3
    c: Vertical(g10)
    c: Equal(g0,g10) = 3
    c: Block(g10)
    c: Vertical(g11)
    c: Equal(g1,g11) = 3
    c: Block(g12)
    c: Block(g13)
    c: Block(g14)
    c: Block(g15)
    c: Block(g16)
    c: Block(g17)
    c: Block(g18)
    c: Block(g19)
    c: Block(g20)
    c: Block(g21)
    c: Block(g22)
    c: Block(g23)
    c: Block(g11)
    c: Block(g9)
    c: Block(g7)
    c: Block(g5)
    c: Block(g3)
    c: Block(g1)
    c: Coincident(g24,g0)
    c: Coincident(g24,g12)
    c: Horizontal(g24)
    c: Coincident(g25,g0)
    c: Coincident(g25,g12)
    c: Horizontal(g25)
    c: Coincident(g26,g1)
    c: Coincident(g26,g13)
    c: Horizontal(g26)
    c: Coincident(g27,g1)
    c: Coincident(g27,g13)
    c: Horizontal(g27)
    c: Coincident(g28,g2)
    c: Coincident(g28,g14)
    c: Horizontal(g28)
    c: Coincident(g29,g2)
    c: Coincident(g29,g14)
    c: Horizontal(g29)
    c: Coincident(g30,g3)
    c: Coincident(g30,g15)
    c: Horizontal(g30)
    c: Coincident(g31,g3)
    c: Coincident(g31,g15)
    c: Horizontal(g31)
    c: Coincident(g32,g4)
    c: Coincident(g32,g16)
    c: Horizontal(g32)
    c: Coincident(g33,g4)
    c: Coincident(g33,g16)
    c: Horizontal(g33)
    c: Coincident(g34,g5)
    c: Coincident(g34,g17)
    c: Horizontal(g34)
    c: Coincident(g35,g5)
    c: Coincident(g35,g17)
    c: Horizontal(g35)
    c: Coincident(g36,g6)
    c: Coincident(g36,g19)
    c: Horizontal(g36)
    c: Coincident(g37,g6)
    c: Coincident(g37,g19)
    c: Horizontal(g37)
    c: Coincident(g38,g7)
    c: Coincident(g38,g18)
    c: Horizontal(g38)
    c: Coincident(g39,g7)
    c: Coincident(g39,g18)
    c: Horizontal(g39)
    c: Coincident(g40,g8)
    c: Coincident(g40,g20)
    c: Horizontal(g40)
    c: Coincident(g41,g8)
    c: Coincident(g41,g20)
    c: Horizontal(g41)
    c: Coincident(g42,g9)
    c: Coincident(g42,g23)
    c: Horizontal(g42)
    c: Coincident(g43,g9)
    c: Coincident(g43,g23)
    c: Horizontal(g43)
    c: Coincident(g44,g10)
    c: Coincident(g44,g22)
    c: Horizontal(g44)
    c: Coincident(g45,g10)
    c: Coincident(g45,g22)
    c: Horizontal(g45)
    c: Coincident(g46,g11)
    c: Coincident(g46,g21)
    c: Horizontal(g46)
    c: Coincident(g47,g11)
    c: Coincident(g47,g21)
    c: Horizontal(g47)
FEATURE [Part::Extrusion] Extrude065
  Base = -> Sketch074
  Dir = (1,0,0)
  DirMode = 2
  FaceMakerClass = Part::FaceMakerBullseye
  LengthFwd = 23
  LengthRev = 0
  Placement = pos=(-19,0,0) rot=(0,0,1;0rad)
  Solid = true
  Symmetric = false
FEATURE [Part::Fillet] Fillet056  label="removeToCreateVentalationHoles003"
  Base = -> Extrude065
  Edges = <same value as first occurrence — deduplicated (x6 in doc)>
  Placement = pos=(7,0.02,0) rot=(0,0,1;0rad)
FEATURE [Part::Revolution] Revolve158  label="removeToCreateScrewAndThreadedInsertHole065"
  Angle = 360
  Axis = (0,1,0)
  Base = (0,0,0)
  FaceMakerClass = Part::FaceMakerBullseye
  Placement = pos=(12.5,0,62) rot=(0,0,1;0rad)
  Solid = false
  Source = -> Face146
  Symmetric = false
FEATURE [Part::Revolution] Revolve159  label="removeToCreateScrewAndThreadedInsertHole066"
  Angle = 360
  Axis = (0,1,0)
  Base = (0,0,0)
  FaceMakerClass = Part::FaceMakerBullseye
  Placement = pos=(89.5,0,68.5) rot=(0,0,1;0rad)
  Solid = false
  Source = -> Face143
  Symmetric = false
FEATURE [Part::Revolution] Revolve160  label="removeToCreateScrewAndThreadedInsertHole067"
  Angle = 360
  Axis = (0,1,0)
  Base = (0,0,0)
  FaceMakerClass = Part::FaceMakerBullseye
  Placement = pos=(89.5,0,3.5) rot=(0,0,1;0rad)
  Solid = false
  Source = -> Face142
  Symmetric = false
FEATURE [Part::Revolution] Revolve161  label="removeToCreateScrewAndThreadedInsertHole068"
  Angle = 360
  Axis = (0,1,0)
  Base = (0,0,0)
  FaceMakerClass = Part::FaceMakerBullseye
  Placement = pos=(109.5,4.7,3.5) rot=(0,0,1;0rad)
  Solid = false
  Source = -> Face145
  Symmetric = false
FEATURE [Part::Revolution] Revolve162  label="removeToCreateScrewAndThreadedInsertHole069"
  Angle = 360
  Axis = (0,1,0)
  Base = (0,0,0)
  FaceMakerClass = Part::FaceMakerBullseye
  Placement = pos=(109.5,4.7,68.5) rot=(0,0,1;0rad)
  Solid = false
  Source = -> Face144
  Symmetric = false
FEATURE [Part::MultiFuse] Fusion141  label="removeToCreateScrewAndThreadedInsertHole064"
  Shapes = -> [Revolve162,Revolve161,Revolve160,Revolve159,Revolve158,Revolve157]
FEATURE [Part::Cylinder] Cylinder062
  Angle = 360
  AttacherType = Attacher::AttachEngine3D
  Height = 20
  Placement = pos=(0,0,36.15) rot=(0,0,1;0rad)
  Radius = 14
FEATURE [Part::Cylinder] Cylinder063
  Angle = 360
  AttacherType = Attacher::AttachEngine3D
  Height = 10
  Placement = pos=(0,0,36.15) rot=(0,0,1;0rad)
  Radius = 4
FEATURE [Part::MultiFuse] Fusion139  label="removeToCreteHoleForPlugHousing052"
  Placement = pos=(70,19,36) rot=(0,1,0;1.5708rad)
  Shapes = -> [Cylinder062,Cylinder063]
FEATURE [Part::Cut] Cut060  label="bottom017"
  Base = -> Extrude064
  Tool = -> Fusion139
FEATURE [Part::Cut] Cut061  label="bottom019"
  Base = -> Cut060
  Tool = -> Fusion141
FEATURE [Part::MultiFuse] Fusion140  label="bottom018"
  Shapes = -> [Cut061,Cut058]
FEATURE [Part::Cut] Cut059  label="bottom020"
  Base = -> Fusion140
  Tool = -> Fillet056
FEATURE [Part::Box] Box036  label="Cube021"
  AttacherType = Attacher::AttachEngine3D
  Height = 80
  Length = 26
  Placement = pos=(0,-1,-5) rot=(0,0,1;0rad)
  Width = 11
FEATURE [Part::Cut] Cut062  label="removeFromBottom002"
  Base = -> Cut057
  Tool = -> Box036
FEATURE [Part::Cut] Cut063
  Base = -> Cut059
  Tool = -> Cut062
FEATURE [Part::Cut] Cut064  label="pcbStands"
  Base = -> Fusion095
  Tool = -> Fusion127
FEATURE [Sketcher::SketchObject] Sketch075  label="topSketch022"
  FullyConstrained = true
  sketch-geometry (6):
    g0: LineSegment StartX=19 StartY=38 StartZ=0 EndX=117 EndY=38 EndZ=0
    g1: ArcOfCircle CenterX=19 CenterY=19 CenterZ=0 NormalX=0 NormalY=0 NormalZ=1 AngleXU=0 Radius=19 StartAngle=1.5708 EndAngle=3.14159
    g2: LineSegment StartX=117 StartY=38 StartZ=0 EndX=117 EndY=19 EndZ=0
    g3: LineSegment StartX=98 StartY=1.0161e-12 StartZ=0 EndX=5.22862e-06 EndY=1.0161e-12 EndZ=0
    g4: LineSegment StartX=5.22862e-06 StartY=19 StartZ=0 EndX=5.22862e-06 EndY=1.0161e-12 EndZ=0
    g5: ArcOfCircle CenterX=98 CenterY=19 CenterZ=0 NormalX=0 NormalY=0 NormalZ=1 AngleXU=0 Radius=19 StartAngle=4.71239 EndAngle=6.28319
  constraints (16):
    c: Horizontal(g0)
    c: Distance(g0) = 98
    c: Coincident(g1,g0)
    c: Block(g1)
    c: Coincident(g2,g0)
    c: Vertical(g2)
    c: Distance(g2) = 19
    c: Horizontal(g3)
    c: Coincident(g4,g1)
    c: Vertical(g4)
    c: Coincident(g3,g4)
    c: Block(g3)
    c: Coincident(g5,g2)
    c: Coincident(g5,g3)
    c: Block(g0)
    c: Block(g5)
FEATURE [Part::Extrusion] Extrude067  label="sideB003"
  Base = -> Sketch075
  Dir = (0,0,1)
  DirMode = 2
  FaceMakerClass = Part::FaceMakerBullseye
  LengthFwd = 3
  LengthRev = 0
  Placement = pos=(0,0,71.7) rot=(0,0,1;0rad)
  Solid = true
  Symmetric = false
FEATURE [Sketcher::SketchObject] Sketch076  label="topSketch023"
  FullyConstrained = true
  sketch-geometry (6):
    g0: LineSegment StartX=19 StartY=38 StartZ=0 EndX=117 EndY=38 EndZ=0
    g1: ArcOfCircle CenterX=19 CenterY=19 CenterZ=0 NormalX=0 NormalY=0 NormalZ=1 AngleXU=0 Radius=19 StartAngle=1.5708 EndAngle=3.14159
    g2: LineSegment StartX=117 StartY=38 StartZ=0 EndX=117 EndY=19 EndZ=0
    g3: LineSegment StartX=98 StartY=1.0161e-12 StartZ=0 EndX=5.22862e-06 EndY=1.0161e-12 EndZ=0
    g4: LineSegment StartX=5.22862e-06 StartY=19 StartZ=0 EndX=5.22862e-06 EndY=1.0161e-12 EndZ=0
    g5: ArcOfCircle CenterX=98 CenterY=19 CenterZ=0 NormalX=0 NormalY=0 NormalZ=1 AngleXU=0 Radius=19 StartAngle=4.71239 EndAngle=6.28319
  constraints (16):
    c: Horizontal(g0)
    c: Distance(g0) = 98
    c: Coincident(g1,g0)
    c: Block(g1)
    c: Coincident(g2,g0)
    c: Vertical(g2)
    c: Distance(g2) = 19
    c: Horizontal(g3)
    c: Coincident(g4,g1)
    c: Vertical(g4)
    c: Coincident(g3,g4)
    c: Block(g3)
    c: Coincident(g5,g2)
    c: Coincident(g5,g3)
    c: Block(g0)
    c: Block(g5)
FEATURE [Part::Extrusion] Extrude066  label="sideA003"
  Base = -> Sketch076
  Dir = (0,0,1)
  DirMode = 2
  FaceMakerClass = Part::FaceMakerBullseye
  LengthFwd = 3
  LengthRev = 0
  Placement = pos=(0,0,-2.7) rot=(0,0,1;0rad)
  Solid = true
  Symmetric = false
FEATURE [Part::MultiFuse] Fusion142  label="removeFromBottom003"
  Placement = pos=(2,0,0) rot=(0,0,1;0rad)
  Shapes = -> [Extrude066,Extrude067]
FEATURE [Part::Cut] Cut065  label="screwRetainers002"
  Base = -> Fusion096
  Tool = -> Fusion142
FEATURE [Sketcher::SketchObject] Sketch077
  FullyConstrained = true
  Placement = pos=(117,19,0) rot=(0.57735,0.57735,0.57735;2.0944rad)
  sketch-geometry (8):
    g0: LineSegment StartX=-49.19 StartY=63.5 StartZ=0 EndX=-49.19 EndY=60.5 EndZ=0
    g1: LineSegment StartX=-49.19 StartY=11.5 StartZ=0 EndX=-49.19 EndY=8.5 EndZ=0
    g2: ArcOfCircle CenterX=-1.5 CenterY=62 CenterZ=0 NormalX=0 NormalY=0 NormalZ=1 AngleXU=0 Radius=1.5 StartAngle=4.71239 EndAngle=7.85398
    g3: ArcOfCircle CenterX=-1.5 CenterY=10 CenterZ=0 NormalX=0 NormalY=0 NormalZ=1 AngleXU=0 Radius=1.5 StartAngle=4.71239 EndAngle=7.85398
    g4: LineSegment StartX=-49.19 StartY=63.5 StartZ=0 EndX=-1.5 EndY=63.5 EndZ=0
    g5: LineSegment StartX=-49.19 StartY=60.5 StartZ=0 EndX=-1.5 EndY=60.5 EndZ=0
    g6: LineSegment StartX=-49.19 StartY=11.5 StartZ=0 EndX=-1.5 EndY=11.5 EndZ=0
    g7: LineSegment StartX=-49.19 StartY=8.5 StartZ=0 EndX=-1.5 EndY=8.5 EndZ=0
  constraints (19):
    c: Vertical(g0)
    c: Distance(g0) = 3
    c: Vertical(g1)
    c: Block(g1)
    c: Block(g2)
    c: Block(g3)
    c: Block(g0)
    c: Coincident(g4,g0)
    c: Coincident(g4,g2)
    c: Horizontal(g4)
    c: Coincident(g5,g0)
    c: Coincident(g5,g2)
    c: Horizontal(g5)
    c: Coincident(g6,g1)
    c: Coincident(g6,g3)
    c: Horizontal(g6)
    c: Coincident(g7,g1)
    c: Coincident(g7,g3)
    c: Horizontal(g7)
FEATURE [Part::Extrusion] Extrude068
  Base = -> Sketch077
  Dir = (1,0,0)
  DirMode = 2
  FaceMakerClass = Part::FaceMakerBullseye
  LengthFwd = 10
  LengthRev = 0
  Solid = true
  Symmetric = false
FEATURE [Part::Fillet] Fillet057  label="removeFromtMoreFrontCaseScrewRetainers002"
  Base = -> Extrude068
  Edges = 4 edges r=1.49: [Edge6,Edge11,Edge18,Edge23]
  Placement = pos=(-12,0,0) rot=(0,0,1;0rad)
FEATURE [Sketcher::SketchObject] Sketch078
  FullyConstrained = true
  Placement = pos=(117,19,0) rot=(0.57735,0.57735,0.57735;2.0944rad)
  sketch-geometry (8):
    g0: LineSegment StartX=-49.19 StartY=69.25 StartZ=0 EndX=-49.19 EndY=66.25 EndZ=0
    g1: LineSegment StartX=-49.19 StartY=5.75 StartZ=0 EndX=-49.19 EndY=2.75 EndZ=0
    g2: ArcOfCircle CenterX=-1.5 CenterY=67.75 CenterZ=0 NormalX=0 NormalY=0 NormalZ=1 AngleXU=0 Radius=1.5 StartAngle=4.71239 EndAngle=7.85398
    g3: ArcOfCircle CenterX=-1.5 CenterY=4.25 CenterZ=0 NormalX=0 NormalY=0 NormalZ=1 AngleXU=0 Radius=1.5 StartAngle=4.71239 EndAngle=7.85398
    g4: LineSegment StartX=-49.19 StartY=69.25 StartZ=0 EndX=-1.5 EndY=69.25 EndZ=0
    g5: LineSegment StartX=-49.19 StartY=66.25 StartZ=0 EndX=-1.5 EndY=66.25 EndZ=0
    g6: LineSegment StartX=-49.19 StartY=5.75 StartZ=0 EndX=-1.5 EndY=5.75 EndZ=0
    g7: LineSegment StartX=-49.19 StartY=2.75 StartZ=0 EndX=-1.5 EndY=2.75 EndZ=0
  constraints (19):
    c: Vertical(g0)
    c: Distance(g0) = 3
    c: Block(g0)
    c: Vertical(g1)
    c: Block(g2)
    c: Block(g3)
    c: Block(g1)
    c: Coincident(g4,g0)
    c: Coincident(g4,g2)
    c: Horizontal(g4)
    c: Coincident(g5,g0)
    c: Coincident(g5,g2)
    c: Horizontal(g5)
    c: Coincident(g6,g1)
    c: Coincident(g6,g3)
    c: Horizontal(g6)
    c: Coincident(g7,g1)
    c: Coincident(g7,g3)
    c: Horizontal(g7)
FEATURE [Part::Extrusion] Extrude069
  Base = -> Sketch078
  Dir = (1,0,0)
  DirMode = 2
  FaceMakerClass = Part::FaceMakerBullseye
  LengthFwd = 10
  LengthRev = 0
  Solid = true
  Symmetric = false
FEATURE [Part::Fillet] Fillet058  label="removeFromtMoreFrontCaseScrewRetainers003"
  Base = -> Extrude069
  Edges = 4 edges r=1.49: [Edge6,Edge11,Edge18,Edge23]
  Placement = pos=(-4,0,0) rot=(0,0,1;0rad)
FEATURE [Part::Cut] Cut066
  Base = -> Cut065
  Tool = -> Fillet058
FEATURE [Part::Cut] Cut067  label="screwPillars"
  Base = -> Cut066
  Tool = -> Fillet057
FEATURE [Part::MultiFuse] Fusion143  label="bottom021"
  Shapes = -> [Cut031,Cut063]
FEATURE [Part::Cylinder] Cylinder
  Angle = 360
  AttacherType = Attacher::AttachEngine3D
  Height = 10
  Placement = pos=(20.65,12,4.68) rot=(1,0,0;1.5708rad)
  Radius = 2
FEATURE [Part::Cylinder] Cylinder064
  Angle = 360
  AttacherType = Attacher::AttachEngine3D
  Height = 10
  Placement = pos=(20.65,12,67.38) rot=(1,0,0;1.5708rad)
  Radius = 2
FEATURE [Part::Cylinder] Cylinder065
  Angle = 360
  AttacherType = Attacher::AttachEngine3D
  Height = 10
  Placement = pos=(77.15,12,67.38) rot=(1,0,0;1.5708rad)
  Radius = 2
FEATURE [Part::Cylinder] Cylinder066
  Angle = 360
  AttacherType = Attacher::AttachEngine3D
  Height = 10
  Placement = pos=(77.15,12,4.68) rot=(1,0,0;1.5708rad)
  Radius = 2
FEATURE [Part::MultiFuse] Fusion144  label="removeFromThreadedInsertHousing"
  Shapes = -> [Cylinder065,Cylinder064,Cylinder,Cylinder066]
FEATURE [Part::Cut] Cut068  label="pcbStands001"
  Base = -> Cut064
  Tool = -> Fusion144
FEATURE [Part::MultiFuse] Fusion145
  Shapes = -> [Cut068,Fusion143]
FEATURE [Part::MultiFuse] Fusion146
  Shapes = -> [Fusion145]
FEATURE [Part::MultiFuse] Fusion147  label="bottom022"
  Shapes = -> [Cut067,Fusion146]
FEATURE [Part::MultiFuse] Fusion148  label="casePillars005"
  Shapes = -> [Cut047,Fusion092]
FEATURE [Part::MultiFuse] Fusion149  label="bottom023"
  Shapes = -> [Fusion124,Fusion113,Fusion147]
FEATURE [Part::MultiFuse] Fusion150  label="topBits"
  Shapes = -> [Cut025,Fusion148,Cut030,Fillet034]
FEATURE [Part::Feature] Face149 .. Face152  x4 (patterned run collapsed; names and placements below)
  shape: bbox 3.2 x 1.5 x 2e-07 mm, 1 faces, 0 solids (baked)
FEATURE [Part::Feature] Face153
  shape: bbox 3.6 x 3.2 x 2e-07 mm, 1 faces, 0 solids (baked)
FEATURE [Part::Feature] Face154
  shape: bbox 3.6 x 3.2 x 2e-07 mm, 1 faces, 0 solids (baked)
FEATURE [Sketcher::SketchObject] Sketch079  label="topSketch024"
  FullyConstrained = true
  sketch-geometry (6):
    g0: LineSegment StartX=19 StartY=38 StartZ=0 EndX=117 EndY=38 EndZ=0
    g1: ArcOfCircle CenterX=19 CenterY=19 CenterZ=0 NormalX=0 NormalY=0 NormalZ=1 AngleXU=0 Radius=19 StartAngle=1.5708 EndAngle=3.14159
    g2: LineSegment StartX=117 StartY=38 StartZ=0 EndX=117 EndY=19 EndZ=0
    g3: LineSegment StartX=98 StartY=1.0161e-12 StartZ=0 EndX=5.22862e-06 EndY=1.0161e-12 EndZ=0
    g4: LineSegment StartX=5.22862e-06 StartY=19 StartZ=0 EndX=5.22862e-06 EndY=1.0161e-12 EndZ=0
    g5: ArcOfCircle CenterX=98 CenterY=19 CenterZ=0 NormalX=0 NormalY=0 NormalZ=1 AngleXU=0 Radius=19 StartAngle=4.71239 EndAngle=6.28319
  constraints (16):
    c: Horizontal(g0)
    c: Distance(g0) = 98
    c: Coincident(g1,g0)
    c: Block(g1)
    c: Coincident(g2,g0)
    c: Vertical(g2)
    c: Distance(g2) = 19
    c: Horizontal(g3)
    c: Coincident(g4,g1)
    c: Vertical(g4)
    c: Coincident(g3,g4)
    c: Block(g3)
    c: Coincident(g5,g2)
    c: Coincident(g5,g3)
    c: Block(g0)
    c: Block(g5)
FEATURE [Sketcher::SketchObject] Sketch080  label="topSketch025"
  FullyConstrained = true
  sketch-geometry (6):
    g0: LineSegment StartX=19 StartY=38 StartZ=0 EndX=117 EndY=38 EndZ=0
    g1: ArcOfCircle CenterX=19 CenterY=19 CenterZ=0 NormalX=0 NormalY=0 NormalZ=1 AngleXU=0 Radius=19 StartAngle=1.5708 EndAngle=3.14159
    g2: LineSegment StartX=117 StartY=38 StartZ=0 EndX=117 EndY=19 EndZ=0
    g3: LineSegment StartX=98 StartY=1.0161e-12 StartZ=0 EndX=5.22862e-06 EndY=1.0161e-12 EndZ=0
    g4: LineSegment StartX=5.22862e-06 StartY=19 StartZ=0 EndX=5.22862e-06 EndY=1.0161e-12 EndZ=0
    g5: ArcOfCircle CenterX=98 CenterY=19 CenterZ=0 NormalX=0 NormalY=0 NormalZ=1 AngleXU=0 Radius=19 StartAngle=4.71239 EndAngle=6.28319
  constraints (16):
    c: Horizontal(g0)
    c: Distance(g0) = 98
    c: Coincident(g1,g0)
    c: Block(g1)
    c: Coincident(g2,g0)
    c: Vertical(g2)
    c: Distance(g2) = 19
    c: Horizontal(g3)
    c: Coincident(g4,g1)
    c: Vertical(g4)
    c: Coincident(g3,g4)
    c: Block(g3)
    c: Coincident(g5,g2)
    c: Coincident(g5,g3)
    c: Block(g0)
    c: Block(g5)
FEATURE [Part::Extrusion] Extrude070  label="sideA004"
  Base = -> Sketch080
  Dir = (0,0,1)
  DirMode = 2
  FaceMakerClass = Part::FaceMakerBullseye
  LengthFwd = 3
  LengthRev = 0
  Placement = pos=(0,0,-2.7) rot=(0,0,1;0rad)
  Solid = true
  Symmetric = false
FEATURE [Sketcher::SketchObject] Sketch081
  FullyConstrained = true
  Placement = pos=(117,19,0) rot=(0.57735,0.57735,0.57735;2.0944rad)
  sketch-geometry (8):
    g0: LineSegment StartX=-49.19 StartY=63.5 StartZ=0 EndX=-49.19 EndY=60.5 EndZ=0
    g1: LineSegment StartX=-49.19 StartY=11.5 StartZ=0 EndX=-49.19 EndY=8.5 EndZ=0
    g2: ArcOfCircle CenterX=-1.5 CenterY=62 CenterZ=0 NormalX=0 NormalY=0 NormalZ=1 AngleXU=0 Radius=1.5 StartAngle=4.71239 EndAngle=7.85398
    g3: ArcOfCircle CenterX=-1.5 CenterY=10 CenterZ=0 NormalX=0 NormalY=0 NormalZ=1 AngleXU=0 Radius=1.5 StartAngle=4.71239 EndAngle=7.85398
    g4: LineSegment StartX=-49.19 StartY=63.5 StartZ=0 EndX=-1.5 EndY=63.5 EndZ=0
    g5: LineSegment StartX=-49.19 StartY=60.5 StartZ=0 EndX=-1.5 EndY=60.5 EndZ=0
    g6: LineSegment StartX=-49.19 StartY=11.5 StartZ=0 EndX=-1.5 EndY=11.5 EndZ=0
    g7: LineSegment StartX=-49.19 StartY=8.5 StartZ=0 EndX=-1.5 EndY=8.5 EndZ=0
  constraints (19):
    c: Vertical(g0)
    c: Distance(g0) = 3
    c: Vertical(g1)
    c: Block(g1)
    c: Block(g2)
    c: Block(g3)
    c: Block(g0)
    c: Coincident(g4,g0)
    c: Coincident(g4,g2)
    c: Horizontal(g4)
    c: Coincident(g5,g0)
    c: Coincident(g5,g2)
    c: Horizontal(g5)
    c: Coincident(g6,g1)
    c: Coincident(g6,g3)
    c: Horizontal(g6)
    c: Coincident(g7,g1)
    c: Coincident(g7,g3)
    c: Horizontal(g7)
FEATURE [Part::Extrusion] Extrude071  label="sideB004"
  Base = -> Sketch079
  Dir = (0,0,1)
  DirMode = 2
  FaceMakerClass = Part::FaceMakerBullseye
  LengthFwd = 3
  LengthRev = 0
  Placement = pos=(0,0,71.7) rot=(0,0,1;0rad)
  Solid = true
  Symmetric = false
FEATURE [Part::MultiFuse] Fusion152  label="removeFromBottom004"
  Placement = pos=(2,0,0) rot=(0,0,1;0rad)
  Shapes = -> [Extrude070,Extrude071]
FEATURE [Part::Extrusion] Extrude072
  Base = -> Sketch081
  Dir = (1,0,0)
  DirMode = 2
  FaceMakerClass = Part::FaceMakerBullseye
  LengthFwd = 10
  LengthRev = 0
  Solid = true
  Symmetric = false
FEATURE [Part::Fillet] Fillet059  label="removeFromtMoreFrontCaseScrewRetainers004"
  Base = -> Extrude072
  Edges = 4 edges r=1.49: [Edge6,Edge11,Edge18,Edge23]
  Placement = pos=(-12,0,0) rot=(0,0,1;0rad)
FEATURE [Sketcher::SketchObject] Sketch082
  FullyConstrained = true
  Placement = pos=(117,19,0) rot=(0.57735,0.57735,0.57735;2.0944rad)
  sketch-geometry (8):
    g0: LineSegment StartX=-49.19 StartY=69.25 StartZ=0 EndX=-49.19 EndY=66.25 EndZ=0
    g1: LineSegment StartX=-49.19 StartY=5.75 StartZ=0 EndX=-49.19 EndY=2.75 EndZ=0
    g2: ArcOfCircle CenterX=-1.5 CenterY=67.75 CenterZ=0 NormalX=0 NormalY=0 NormalZ=1 AngleXU=0 Radius=1.5 StartAngle=4.71239 EndAngle=7.85398
    g3: ArcOfCircle CenterX=-1.5 CenterY=4.25 CenterZ=0 NormalX=0 NormalY=0 NormalZ=1 AngleXU=0 Radius=1.5 StartAngle=4.71239 EndAngle=7.85398
    g4: LineSegment StartX=-49.19 StartY=69.25 StartZ=0 EndX=-1.5 EndY=69.25 EndZ=0
    g5: LineSegment StartX=-49.19 StartY=66.25 StartZ=0 EndX=-1.5 EndY=66.25 EndZ=0
    g6: LineSegment StartX=-49.19 StartY=5.75 StartZ=0 EndX=-1.5 EndY=5.75 EndZ=0
    g7: LineSegment StartX=-49.19 StartY=2.75 StartZ=0 EndX=-1.5 EndY=2.75 EndZ=0
  constraints (19):
    c: Vertical(g0)
    c: Distance(g0) = 3
    c: Block(g0)
    c: Vertical(g1)
    c: Block(g2)
    c: Block(g3)
    c: Block(g1)
    c: Coincident(g4,g0)
    c: Coincident(g4,g2)
    c: Horizontal(g4)
    c: Coincident(g5,g0)
    c: Coincident(g5,g2)
    c: Horizontal(g5)
    c: Coincident(g6,g1)
    c: Coincident(g6,g3)
    c: Horizontal(g6)
    c: Coincident(g7,g1)
    c: Coincident(g7,g3)
    c: Horizontal(g7)
FEATURE [Part::Extrusion] Extrude073
  Base = -> Sketch082
  Dir = (1,0,0)
  DirMode = 2
  FaceMakerClass = Part::FaceMakerBullseye
  LengthFwd = 10
  LengthRev = 0
  Solid = true
  Symmetric = false
FEATURE [Part::Fillet] Fillet060  label="removeFromtMoreFrontCaseScrewRetainers005"
  Base = -> Extrude073
  Edges = 4 edges r=1.49: [Edge6,Edge11,Edge18,Edge23]
  Placement = pos=(-4,0,0) rot=(0,0,1;0rad)
FEATURE [Part::Revolution] Revolve163  label="backCaseScrewRetainer004"
  Angle = 360
  Axis = (0,1,0)
  Base = (0,0,0)
  FaceMakerClass = Part::FaceMakerBullseye
  Placement = pos=(12.5,3,62) rot=(0,0,1;0rad)
  Solid = false
  Source = -> Face149
  Symmetric = false
FEATURE [Part::Revolution] Revolve164  label="frontCaseScrewRetainer006"
  Angle = 360
  Axis = (0,1,0)
  Base = (0,0,0)
  FaceMakerClass = Part::FaceMakerBullseye
  Placement = pos=(89.5,3,68.5) rot=(0,0,1;0rad)
  Solid = false
  Source = -> Face151
  Symmetric = false
FEATURE [Part::Revolution] Revolve165  label="frontCaseScrewRetainer007"
  Angle = 360
  Axis = (0,1,0)
  Base = (0,0,0)
  FaceMakerClass = Part::FaceMakerBullseye
  Placement = pos=(89.5,3,3.5) rot=(0,0,1;0rad)
  Solid = false
  Source = -> Face152
  Symmetric = false
FEATURE [Part::Revolution] Revolve166  label="backCaseScrewRetainer005"
  Angle = 360
  Axis = (0,1,0)
  Base = (0,0,0)
  FaceMakerClass = Part::FaceMakerBullseye
  Placement = pos=(12.5,3,10) rot=(0,0,1;0rad)
  Solid = false
  Source = -> Face150
  Symmetric = false
FEATURE [Part::Revolution] Revolve167  label="moreFrontCaseScrewRetainer006"
  Angle = 360
  Axis = (0,1,0)
  Base = (0,0,0)
  FaceMakerClass = Part::FaceMakerBullseye
  Placement = pos=(109.5,4.5,68.5) rot=(0,0,1;0rad)
  Solid = false
  Source = -> Face153
  Symmetric = false
FEATURE [Part::Revolution] Revolve168  label="moreFrontCaseScrewRetainer007"
  Angle = 360
  Axis = (0,1,0)
  Base = (0,0,0)
  FaceMakerClass = Part::FaceMakerBullseye
  Placement = pos=(109.5,4.5,3.5) rot=(0,0,1;0rad)
  Solid = false
  Source = -> Face154
  Symmetric = false
FEATURE [Part::MultiFuse] Fusion151  label="screwRetainers003"
  Shapes = -> [Revolve168,Revolve167,Revolve166,Revolve165,Revolve164,Revolve163]
FEATURE [Part::Cut] Cut069  label="screwRetainers004"
  Base = -> Fusion151
  Tool = -> Fusion152
FEATURE [Part::Cut] Cut070
  Base = -> Cut069
  Tool = -> Fillet060
FEATURE [Part::Cut] Cut071  label="screwPillars001"
  Base = -> Cut070
  Tool = -> Fillet059
FEATURE [Part::MultiFuse] Fusion153  label="bottom024"
  Shapes = -> [Fusion149,Cut071]
FEATURE [Part::Cylinder] Cylinder067
  Angle = 360
  AttacherType = Attacher::AttachEngine3D
  Height = 10
  Placement = pos=(20.65,12,4.68) rot=(1,0,0;1.5708rad)
  Radius = 2
FEATURE [Part::Cylinder] Cylinder068
  Angle = 360
  AttacherType = Attacher::AttachEngine3D
  Height = 10
  Placement = pos=(20.65,12,67.38) rot=(1,0,0;1.5708rad)
  Radius = 2
FEATURE [Part::Cylinder] Cylinder069
  Angle = 360
  AttacherType = Attacher::AttachEngine3D
  Height = 10
  Placement = pos=(77.15,12,67.38) rot=(1,0,0;1.5708rad)
  Radius = 2
FEATURE [Part::Cylinder] Cylinder070
  Angle = 360
  AttacherType = Attacher::AttachEngine3D
  Height = 10
  Placement = pos=(77.15,12,4.68) rot=(1,0,0;1.5708rad)
  Radius = 2
FEATURE [Part::MultiFuse] Fusion154  label="removeFromThreadedInsertHousing001"
  Shapes = -> [Cylinder069,Cylinder068,Cylinder067,Cylinder070]
FEATURE [Part::Cut] Cut072  label="bottom025"
  Base = -> Fusion153
  Tool = -> Fusion154
FEATURE [Image::ImagePlane] ImagePlane
  XSize = 339
  YSize = 72
FEATURE [Sketcher::SketchObject] Sketch083
  FullyConstrained = true
  MapMode = 5
  Support = -> [XY_Plane]
  sketch-geometry (338):
    g0: LineSegment StartX=-151.619 StartY=28.8932 StartZ=0 EndX=-140.819 EndY=28.8932 EndZ=0
    g1: LineSegment StartX=-151.619 StartY=24.0313 StartZ=0 EndX=-151.619 EndY=28.8932 EndZ=0
    g2: LineSegment StartX=-140.819 StartY=17.7713 StartZ=0 EndX=-151.619 EndY=17.7713 EndZ=0
    g3: LineSegment StartX=-151.619 StartY=17.7713 StartZ=0 EndX=-151.619 EndY=22.6313 EndZ=0
    g4: LineSegment StartX=-151.619 StartY=22.6313 StartZ=0 EndX=-145.128 EndY=22.6313 EndZ=0
    g5: LineSegment StartX=-145.128 StartY=24.0313 StartZ=0 EndX=-140.819 EndY=28.8932 EndZ=0
    g6: LineSegment StartX=-145.128 StartY=22.6313 StartZ=0 EndX=-140.819 EndY=17.7713 EndZ=0
    g7: ArcOfCircle CenterX=-155.157 CenterY=23.3323 CenterZ=0 NormalX=0 NormalY=0 NormalZ=1 AngleXU=0 Radius=6.92354 StartAngle=1.03434 EndAngle=5.24885
    g8: ArcOfCircle CenterX=-155.157 CenterY=23.3323 CenterZ=0 NormalX=0 NormalY=0 NormalZ=1 AngleXU=0 Radius=12.6269 StartAngle=1.28675 EndAngle=4.99643
    g9: LineSegment StartX=-151.619 StartY=35.4532 StartZ=0 EndX=-151.619 EndY=29.2832 EndZ=0
    g10: LineSegment StartX=-151.619 StartY=17.3813 StartZ=0 EndX=-151.619 EndY=11.2113 EndZ=0
    g11-g21: Circle x11 (B-spline internal-alignment scaffolding for g22; pole/knot coordinates omitted)
    g22: BSplineCurve PolesCount=11 KnotsCount=9 Degree=3 IsPeriodic=0
    g23-g31: GeomPoint x9 (B-spline internal-alignment scaffolding for g22; pole/knot coordinates omitted)
    g32-g49: Circle x18 (B-spline internal-alignment scaffolding for g50; pole/knot coordinates omitted)
    g50: BSplineCurve PolesCount=18 KnotsCount=16 Degree=3 IsPeriodic=0
    g51-g66: GeomPoint x16 (B-spline internal-alignment scaffolding for g50; pole/knot coordinates omitted)
    g67: LineSegment StartX=-117.124 StartY=30.093 StartZ=0 EndX=-117.603 EndY=26.5272 EndZ=0
    g68: LineSegment StartX=-117.603 StartY=17.8472 StartZ=0 EndX=-117.124 EndY=14.2659 EndZ=0
    g69: Ellipse CenterX=-109.671 CenterY=20.025 CenterZ=0 NormalX=0 NormalY=0 NormalZ=1 MajorRadius=3.34798 MinorRadius=2.71052 AngleXU=-1.56793
    g70: GeomPoint X=-109.666 Y=18.0598 Z=0
    g71: GeomPoint X=-109.677 Y=21.9902 Z=0
    g72: Ellipse CenterX=-109.671 CenterY=20.0123 CenterZ=0 NormalX=0 NormalY=0 NormalZ=1 MajorRadius=6.93002 MinorRadius=6.36273 AngleXU=-3.13976
    g73: GeomPoint X=-112.417 Y=20.0073 Z=0
    g74: GeomPoint X=-106.925 Y=20.0173 Z=0
    g75: Ellipse CenterX=-51.7682 CenterY=20.1463 CenterZ=0 NormalX=0 NormalY=0 NormalZ=1 MajorRadius=3.19279 MinorRadius=2.71052 AngleXU=-1.52774
    g76: GeomPoint X=-51.6955 Y=18.4606 Z=0
    g77: GeomPoint X=-51.8408 Y=21.832 Z=0
    g78: GeomPoint X=-54.5142 Y=20.1413 Z=0
    g79: GeomPoint X=-49.0221 Y=20.1513 Z=0
    g80: Ellipse CenterX=-51.7682 CenterY=20.1463 CenterZ=0 NormalX=0 NormalY=0 NormalZ=1 MajorRadius=6.93002 MinorRadius=6.36273 AngleXU=-3.13976
    g81: Ellipse CenterX=-22.8436 CenterY=20.1783 CenterZ=0 NormalX=0 NormalY=0 NormalZ=1 MajorRadius=3.31512 MinorRadius=2.71052 AngleXU=-1.60214
    g82: GeomPoint X=-22.9034 Y=18.2706 Z=0
    g83: GeomPoint X=-22.7838 Y=22.0861 Z=0
    g84: GeomPoint X=-25.5897 Y=20.1733 Z=0
    g85: GeomPoint X=-20.0976 Y=20.1833 Z=0
    g86: Ellipse CenterX=-22.8436 CenterY=20.1783 CenterZ=0 NormalX=0 NormalY=0 NormalZ=1 MajorRadius=6.93002 MinorRadius=6.36273 AngleXU=-3.13976
    g87: LineSegment StartX=-101.889 StartY=14.1107 StartZ=0 EndX=-97.7455 EndY=14.1107 EndZ=0
    g88: LineSegment StartX=-93.8155 StartY=14.1107 StartZ=0 EndX=-89.6755 EndY=14.1107 EndZ=0
    g89: LineSegment StartX=-85.7455 StartY=14.1107 StartZ=0 EndX=-81.6055 EndY=14.1107 EndZ=0
    g90: LineSegment StartX=-101.889 StartY=14.1107 StartZ=0 EndX=-101.889 EndY=25.9907 EndZ=0
    g91: LineSegment StartX=-101.889 StartY=25.9907 StartZ=0 EndX=-97.8594 EndY=25.9907 EndZ=0
    g92: LineSegment StartX=-97.8594 StartY=25.9907 StartZ=0 EndX=-97.8594 EndY=24.0907 EndZ=0
    g93: LineSegment StartX=-97.7455 StartY=14.1107 StartZ=0 EndX=-97.7455 EndY=19.9107 EndZ=0
    g94: LineSegment StartX=-89.6755 StartY=14.1107 StartZ=0 EndX=-89.6755 EndY=19.9107 EndZ=0
    g95: LineSegment StartX=-93.8155 StartY=14.1107 StartZ=0 EndX=-93.8155 EndY=21.0107 EndZ=0
    g96-g106: Circle x11 (B-spline internal-alignment scaffolding for g107; pole/knot coordinates omitted)
    g107: BSplineCurve PolesCount=11 KnotsCount=9 Degree=3 IsPeriodic=0
    g108-g116: GeomPoint x9 (B-spline internal-alignment scaffolding for g107; pole/knot coordinates omitted)
    g117: BSplineCurve PolesCount=11 KnotsCount=9 Degree=3 IsPeriodic=0
    g118-g125: Circle x8 (B-spline internal-alignment scaffolding for g126; pole/knot coordinates omitted)
    g126: BSplineCurve PolesCount=8 KnotsCount=6 Degree=3 IsPeriodic=0
    g127-g132: GeomPoint x6 (B-spline internal-alignment scaffolding for g126; pole/knot coordinates omitted)
    g133: BSplineCurve PolesCount=8 KnotsCount=6 Degree=3 IsPeriodic=0
    g134: LineSegment StartX=-85.7455 StartY=21.0107 StartZ=0 EndX=-85.7455 EndY=14.1107 EndZ=0
    g135: LineSegment StartX=-80.0879 StartY=14.1107 StartZ=0 EndX=-75.944 EndY=14.1107 EndZ=0
    g136: LineSegment StartX=-72.014 StartY=14.1107 StartZ=0 EndX=-67.874 EndY=14.1107 EndZ=0
    g137: LineSegment StartX=-63.944 StartY=14.1107 StartZ=0 EndX=-59.804 EndY=14.1107 EndZ=0
    g138: LineSegment StartX=-80.0879 StartY=14.1107 StartZ=0 EndX=-80.0879 EndY=25.9907 EndZ=0
    g139: LineSegment StartX=-80.0879 StartY=25.9907 StartZ=0 EndX=-76.0579 EndY=25.9907 EndZ=0
    g140: LineSegment StartX=-76.0579 StartY=25.9907 StartZ=0 EndX=-76.0579 EndY=24.0907 EndZ=0
    g141: LineSegment StartX=-75.944 StartY=14.1107 StartZ=0 EndX=-75.944 EndY=19.9107 EndZ=0
    g142: LineSegment StartX=-67.874 StartY=14.1107 StartZ=0 EndX=-67.874 EndY=19.9107 EndZ=0
    g143: LineSegment StartX=-72.014 StartY=14.1107 StartZ=0 EndX=-72.014 EndY=21.0107 EndZ=0
    g144-g148: Circle x5 (B-spline internal-alignment scaffolding for g149; pole/knot coordinates omitted)
    g149: BSplineCurve PolesCount=11 KnotsCount=9 Degree=3 IsPeriodic=0
    g150-g158: GeomPoint x9 (B-spline internal-alignment scaffolding for g149; pole/knot coordinates omitted)
    g159: BSplineCurve PolesCount=11 KnotsCount=9 Degree=3 IsPeriodic=0
    g160-g167: Circle x8 (B-spline internal-alignment scaffolding for g168; pole/knot coordinates omitted)
    g168: BSplineCurve PolesCount=8 KnotsCount=6 Degree=3 IsPeriodic=0
    g169-g174: GeomPoint x6 (B-spline internal-alignment scaffolding for g168; pole/knot coordinates omitted)
    g175: BSplineCurve PolesCount=8 KnotsCount=6 Degree=3 IsPeriodic=0
    g176: LineSegment StartX=-63.944 StartY=21.0107 StartZ=0 EndX=-63.944 EndY=14.1107 EndZ=0
    g177: LineSegment StartX=-59.804 StartY=14.1107 StartZ=0 EndX=-59.804 EndY=21.5868 EndZ=0
    g178: BSplineCurve PolesCount=4 KnotsCount=2 Degree=3 IsPeriodic=0
    g179: GeomPoint X=-59.804 Y=21.5868 Z=0
    g180: GeomPoint X=-60.2379 Y=24.0907 Z=0
    g181: LineSegment StartX=-81.6055 StartY=14.1107 StartZ=0 EndX=-81.6055 EndY=21.5868 EndZ=0
    g182: LineSegment StartX=-151.619 StartY=24.0313 StartZ=0 EndX=-145.128 EndY=24.0313 EndZ=0
    g183: Circle CenterX=-82.0394 CenterY=24.0907 CenterZ=0 NormalX=0 NormalY=0 NormalZ=1 AngleXU=0 Radius=1
    g184: Circle CenterX=-81.7131 CenterY=23.2736 CenterZ=0 NormalX=0 NormalY=0 NormalZ=1 AngleXU=0 Radius=1
    g185: Circle CenterX=-81.6055 CenterY=21.5868 CenterZ=0 NormalX=0 NormalY=0 NormalZ=1 AngleXU=0 Radius=1
    g186: BSplineCurve PolesCount=3 KnotsCount=2 Degree=2 IsPeriodic=0
    g187: GeomPoint X=-82.0394 Y=24.0907 Z=0
    g188: GeomPoint X=-81.6055 Y=21.5868 Z=0
    g189: Ellipse CenterX=-37.3522 CenterY=19.9515 CenterZ=0 NormalX=0 NormalY=0 NormalZ=1 MajorRadius=2.99755 MinorRadius=2.49 AngleXU=1.5708
    g190: GeomPoint X=-37.3522 Y=21.6203 Z=0
    g191: GeomPoint X=-37.3522 Y=18.2826 Z=0
    g192: ArcOfEllipse CenterX=-38.7647 CenterY=20.06 CenterZ=0 NormalX=0 NormalY=0 NormalZ=1 MajorRadius=6.30025 MinorRadius=5.3849 AngleXU=1.57276 StartAngle=5.50632 EndAngle=10.3035
    g193: GeomPoint X=-38.7711 Y=23.3304 Z=0
    g194: GeomPoint X=-38.7583 Y=16.7895 Z=0
    g195: LineSegment StartX=-34.6109 StartY=14.1107 StartZ=0 EndX=-30.8984 EndY=14.1107 EndZ=0
    g196: LineSegment StartX=-30.8984 StartY=14.1107 StartZ=0 EndX=-30.8984 EndY=31.1784 EndZ=0
    g197: LineSegment StartX=-30.8984 StartY=31.1784 StartZ=0 EndX=-34.9984 EndY=31.1784 EndZ=0
    g198: LineSegment StartX=-34.9984 StartY=24.5602 StartZ=0 EndX=-34.9984 EndY=31.1784 EndZ=0
    g199: LineSegment StartX=-34.6109 StartY=16.0476 StartZ=0 EndX=-34.6109 EndY=14.1107 EndZ=0
    g200: LineSegment StartX=-14.8781 StartY=14.1107 StartZ=0 EndX=-10.5106 EndY=14.1107 EndZ=0
    g201: LineSegment StartX=-14.8781 StartY=14.1107 StartZ=0 EndX=-14.8781 EndY=25.8504 EndZ=0
    g202: LineSegment StartX=-14.8781 StartY=25.8504 StartZ=0 EndX=-10.8534 EndY=25.8504 EndZ=0
    g203: LineSegment StartX=-10.8534 StartY=25.8504 StartZ=0 EndX=-10.8534 EndY=24.0923 EndZ=0
    g204: LineSegment StartX=-10.5106 StartY=14.1107 StartZ=0 EndX=-10.5106 EndY=19.7752 EndZ=0
    g205: LineSegment StartX=-5.96397 StartY=25.9304 StartZ=0 EndX=-5.96397 EndY=22.574 EndZ=0
    g206-g214: Circle x9 (B-spline internal-alignment scaffolding for g215; pole/knot coordinates omitted)
    g215: BSplineCurve PolesCount=9 KnotsCount=7 Degree=3 IsPeriodic=0
    g216-g222: GeomPoint x7 (B-spline internal-alignment scaffolding for g215; pole/knot coordinates omitted)
    g223-g232: Circle x10 (B-spline internal-alignment scaffolding for g233; pole/knot coordinates omitted)
    g233: BSplineCurve PolesCount=10 KnotsCount=8 Degree=3 IsPeriodic=0
    g234-g241: GeomPoint x8 (B-spline internal-alignment scaffolding for g233; pole/knot coordinates omitted)
    g242: LineSegment StartX=-1.58923 StartY=21.0696 StartZ=0 EndX=2.62034 EndY=21.0696 EndZ=0
    g243: LineSegment StartX=-1.55856 StartY=18.7342 StartZ=0 EndX=6.45946 EndY=18.7342 EndZ=0
    g244: LineSegment StartX=5.29231 StartY=17.386 StartZ=0 EndX=5.29231 EndY=14.3674 EndZ=0
    g245-g269: Circle x25 (B-spline internal-alignment scaffolding for g270; pole/knot coordinates omitted)
    g270: BSplineCurve PolesCount=25 KnotsCount=23 Degree=3 IsPeriodic=0
    g271-g293: GeomPoint x23 (B-spline internal-alignment scaffolding for g270; pole/knot coordinates omitted)
    g294-g304: Circle x11 (B-spline internal-alignment scaffolding for g305; pole/knot coordinates omitted)
    g305: BSplineCurve PolesCount=11 KnotsCount=9 Degree=3 IsPeriodic=0
    g306-g314: GeomPoint x9 (B-spline internal-alignment scaffolding for g305; pole/knot coordinates omitted)
    g315-g326: Circle x12 (B-spline internal-alignment scaffolding for g327; pole/knot coordinates omitted)
    g327: BSplineCurve PolesCount=12 KnotsCount=10 Degree=3 IsPeriodic=0
    g328-g337: GeomPoint x10 (B-spline internal-alignment scaffolding for g327; pole/knot coordinates omitted)
  constraints (252):
    c: Coincident(g1,g0)
    c: Horizontal(g0)
    c: Vertical(g1)
    c: Coincident(g2,g3)
    c: Coincident(g3,g4)
    c: Horizontal(g4)
    c: Horizontal(g2)
    c: Vertical(g3)
    c: Block(g1)
    c: Distance(g3) = 4.86
    c: Block(g4)
    c: Distance(g0) = 10.8
    c: Distance(g2) = 10.8
    c: Coincident(g5,g0)
    c: Coincident(g6,g4)
    c: Coincident(g6,g2)
    c: Block(g8)
    c: Block(g7)
    c: Coincident(g9,g8)
    c: Coincident(g9,g7)
    c: Vertical(g9)
    c: Coincident(g10,g7)
    c: Coincident(g10,g8)
    c: Vertical(g10)
    c: Weight(g11) = 1
    c: Equal(g11, g12-g21) x10
    c: InternalAlignment(g11-g21 -> g22) x11
    c: InternalAlignment(g23-g31 -> g22) x9
    c: Block(g22)
    c: Weight(g32) = 1
    c: Equal(g32, g33-g49) x17
    c: InternalAlignment(g32-g49 -> g50) x18
    c: InternalAlignment(g51-g66 -> g50) x16
    c: Block(g50)
    c: Coincident(g67,g50)
    c: Coincident(g67,g22)
    c: Coincident(g68,g22)
    c: Coincident(g68,g50)
    c: InternalAlignment(g70,g69)
    c: InternalAlignment(g71,g69)
    c: Block(g69)
    c: InternalAlignment(g73,g72)
    c: InternalAlignment(g74,g72)
    c: Block(g72)
    c: InternalAlignment(g76,g75)
    c: InternalAlignment(g77,g75)
    c: InternalAlignment(g78,g80)
    c: InternalAlignment(g79,g80)
    c: Block(g80)
    c: Coincident(g75,g80)
    c: Block(g75)
    c: InternalAlignment(g82,g81)
    c: InternalAlignment(g83,g81)
    c: InternalAlignment(g84,g86)
    c: InternalAlignment(g85,g86)
    c: Block(g86)
    c: Coincident(g81,g86)
    c: Block(g81)
    c: Horizontal(g87)
    c: Block(g87)
    c: Horizontal(g88)
    c: Distance(g88) = 4.14
    c: Horizontal(g89)
    c: Equal(g88,g89) = 4.14
    c: Block(g89)
    c: Block(g88)
    c: Coincident(g90,g87)
    c: Vertical(g90)
    c: Distance(g90) = 11.88
    c: Coincident(g91,g90)
    c: Horizontal(g91)
    c: Coincident(g92,g91)
    c: Vertical(g92)
    c: Distance(g91) = 4.03
    c: Distance(g92) = 1.9
    c: Coincident(g93,g87)
    c: Vertical(g93)
    c: Vertical(g94)
    c: Coincident(g94,g88)
    c: Distance(g93) = 5.8
    c: Distance(g94) = 5.8
    c: Vertical(g95)
    c: Coincident(g95,g88)
    c: Distance(g95) = 6.9
    c: Coincident(g107,g92)
    c: Weight(g96) = 1
    c: Equal(g96, g97-g106) x10
    c: InternalAlignment(g96-g106 -> g107) x11
    c: InternalAlignment(g108-g116 -> g107) x9
    c: Block(g107)
    c: Block(g117)
    c: Coincident(g126,g93)
    c: Weight(g118) = 1
    c: Equal(g118, g119-g125) x7
    c: Coincident(g126,g95)
    c: InternalAlignment(g118-g125 -> g126) x8
    c: InternalAlignment(g127-g132 -> g126) x6
    c: Coincident(g133,g94)
    c: Block(g126)
    c: Block(g133)
    c: Coincident(g134,g133)
    c: Coincident(g134,g89)
    c: Vertical(g134)
    c: Horizontal(g135)
    c: Block(g135)
    c: Horizontal(g136)
    c: Equal(g88,g136) = 4.14
    c: Horizontal(g137)
    c: Equal(g136,g137) = 4.14
    c: Block(g137)
    c: Block(g136)
    c: Coincident(g138,g135)
    c: Vertical(g138)
    c: Equal(g90,g138) = 11.88
    c: Coincident(g139,g138)
    c: Horizontal(g139)
    c: Coincident(g140,g139)
    c: Vertical(g140)
    c: Equal(g91,g139) = 4.03
    c: Equal(g92,g140) = 1.9
    c: Coincident(g141,g135)
    c: Vertical(g141)
    c: Vertical(g142)
    c: Coincident(g142,g136)
    c: Equal(g93,g141) = 5.8
    c: Equal(g94,g142) = 5.8
    c: Vertical(g143)
    c: Coincident(g143,g136)
    c: Equal(g95,g143) = 6.9
    c: Coincident(g149,g140)
    c: Equal(g96,g144) = 1
    c: Equal(g144, g145-g148) x4
    c: InternalAlignment(g144-g148 -> g149) x5
    c: InternalAlignment(g150-g158 -> g149) x9
    c: Block(g149)
    c: Block(g159)
    c: Coincident(g168,g141)
    c: Equal(g118,g160) = 1
    c: Equal(g160, g161-g167) x7
    c: Coincident(g168,g143)
    c: InternalAlignment(g160-g167 -> g168) x8
    c: InternalAlignment(g169-g174 -> g168) x6
    c: Coincident(g175,g142)
    c: Block(g168)
    c: Block(g175)
    c: Coincident(g176,g175)
    c: Coincident(g176,g137)
    c: Vertical(g176)
    c: Coincident(g177,g137)
    c: Vertical(g177)
    c: Coincident(g178,g177)
    c: Coincident(g178,g159)
    c: InternalAlignment(g179,g178)
    c: InternalAlignment(g180,g178)
    c: Block(g178)
    c: Vertical(g181)
    c: Coincident(g181,g89)
    c: Block(g5)
    c: Coincident(g182,g1)
    c: Coincident(g182,g5)
    c: Horizontal(g182)
    c: Coincident(g186,g117)
    c: Weight(g183) = 1
    c: Equal(g183,g184)
    c: Equal(g183,g185)
    c: Coincident(g186,g181)
    c: InternalAlignment(g183,g186)
    c: InternalAlignment(g184,g186)
    c: InternalAlignment(g185,g186)
    c: InternalAlignment(g187,g186)
    c: InternalAlignment(g188,g186)
    c: Block(g186)
    c: InternalAlignment(g190,g189)
    c: InternalAlignment(g191,g189)
    c: Block(g189)
    c: InternalAlignment(g193,g192)
    c: InternalAlignment(g194,g192)
    c: Block(g192)
    c: Horizontal(g195)
    c: Block(g195)
    c: Coincident(g196,g195)
    c: Vertical(g196)
    c: Block(g196)
    c: Distance(g195) = 3.71244
    c: Coincident(g197,g196)
    c: Horizontal(g197)
    c: Distance(g197) = 4.1
    c: Coincident(g198,g192)
    c: Coincident(g198,g197)
    c: Vertical(g198)
    c: Block(g198)
    c: Coincident(g199,g192)
    c: Coincident(g199,g195)
    c: Vertical(g199)
    c: Block(g199)
    c: Horizontal(g200)
    c: Block(g200)
    c: Coincident(g201,g200)
    c: Vertical(g201)
    c: Block(g201)
    c: Coincident(g202,g201)
    c: Horizontal(g202)
    c: Block(g202)
    c: Coincident(g203,g202)
    c: Vertical(g203)
    c: Block(g203)
    c: Coincident(g204,g200)
    c: Vertical(g204)
    c: Block(g204)
    c: Coincident(g215,g203)
    c: Weight(g206) = 1
    c: Equal(g206, g207-g214) x8
    c: Coincident(g215,g205)
    c: InternalAlignment(g206-g214 -> g215) x9
    c: InternalAlignment(g216-g222 -> g215) x7
    c: Coincident(g233,g204)
    c: Weight(g223) = 1
    c: Equal(g223, g224-g232) x9
    c: Coincident(g233,g205)
    c: InternalAlignment(g223-g232 -> g233) x10
    c: InternalAlignment(g234-g241 -> g233) x8
    c: Vertical(g205)
    c: Block(g205)
    c: Block(g215)
    c: Block(g233)
    c: Horizontal(g242)
    c: Horizontal(g243)
    c: Block(g242)
    c: Block(g243)
    c: Vertical(g244)
    c: Block(g244)
    c: Coincident(g270,g243)
    c: Weight(g245) = 1
    c: Equal(g245, g246-g269) x24
    c: Coincident(g270,g244)
    c: InternalAlignment(g245-g269 -> g270) x25
    c: InternalAlignment(g271-g293 -> g270) x23
    c: Coincident(g305,g242)
    c: Weight(g294) = 1
    c: Equal(g294, g295-g304) x10
    c: Coincident(g305,g242)
    c: InternalAlignment(g294-g304 -> g305) x11
    c: InternalAlignment(g306-g314 -> g305) x9
    c: Block(g305)
    c: Coincident(g327,g243)
    c: Weight(g315) = 1
    c: Equal(g315, g316-g326) x11
    c: Coincident(g327,g244)
    c: InternalAlignment(g315-g326 -> g327) x12
    c: InternalAlignment(g328-g337 -> g327) x10
    c: Block(g327)
    c: Block(g270)
FEATURE [PartDesign::Body] Body  label="CommodoreLogoAndText"
  Group = -> [Sketch083]
  Origin = -> Origin
FEATURE [Part::Extrusion] Extrude074  label="CommodoreLogoAndText001"
  Base = -> Sketch083
  Dir = (0,0,1)
  DirMode = 2
  FaceMakerClass = Part::FaceMakerBullseye
  LengthFwd = 10
  LengthRev = 0
  Solid = true
  Symmetric = false
FEATURE [Part::FeaturePython] Clone  label="CommodoreLogoAndTextScale"  # Draft clone (typed FeaturePython)
  AttacherType = Attacher::AttachEngine3D
  Fuse = false
  Objects = -> [Extrude074]
  Placement = pos=(111,5.37,-11.6) rot=(0,0,1;0rad)
  Scale = (0.62,0.62,1)
FEATURE [Part::Mirroring] Part__Mirroring  label="CommodoreLogoAndTextScale (Mirror #1)"
  Base = (0,0,0)
  Normal = (1,0,0)
  Placement = pos=(123.576,0,0) rot=(0,0,1;0rad)
  Source = -> Clone
FEATURE [Sketcher::SketchObject] Sketch084
  FullyConstrained = true
  MapMode = 5
  Support = -> [XY_Plane001]
  sketch-geometry (338):
    g0: LineSegment StartX=-151.619 StartY=28.8932 StartZ=0 EndX=-140.819 EndY=28.8932 EndZ=0
    g1: LineSegment StartX=-151.619 StartY=24.0313 StartZ=0 EndX=-151.619 EndY=28.8932 EndZ=0
    g2: LineSegment StartX=-140.819 StartY=17.7713 StartZ=0 EndX=-151.619 EndY=17.7713 EndZ=0
    g3: LineSegment StartX=-151.619 StartY=17.7713 StartZ=0 EndX=-151.619 EndY=22.6313 EndZ=0
    g4: LineSegment StartX=-151.619 StartY=22.6313 StartZ=0 EndX=-145.128 EndY=22.6313 EndZ=0
    g5: LineSegment StartX=-145.128 StartY=24.0313 StartZ=0 EndX=-140.819 EndY=28.8932 EndZ=0
    g6: LineSegment StartX=-145.128 StartY=22.6313 StartZ=0 EndX=-140.819 EndY=17.7713 EndZ=0
    g7: ArcOfCircle CenterX=-155.157 CenterY=23.3323 CenterZ=0 NormalX=0 NormalY=0 NormalZ=1 AngleXU=0 Radius=6.92354 StartAngle=1.03434 EndAngle=5.24885
    g8: ArcOfCircle CenterX=-155.157 CenterY=23.3323 CenterZ=0 NormalX=0 NormalY=0 NormalZ=1 AngleXU=0 Radius=12.6269 StartAngle=1.28675 EndAngle=4.99643
    g9: LineSegment StartX=-151.619 StartY=35.4532 StartZ=0 EndX=-151.619 EndY=29.2832 EndZ=0
    g10: LineSegment StartX=-151.619 StartY=17.3813 StartZ=0 EndX=-151.619 EndY=11.2113 EndZ=0
    g11-g21: Circle x11 (B-spline internal-alignment scaffolding for g22; pole/knot coordinates omitted)
    g22: BSplineCurve PolesCount=11 KnotsCount=9 Degree=3 IsPeriodic=0
    g23-g31: GeomPoint x9 (B-spline internal-alignment scaffolding for g22; pole/knot coordinates omitted)
    g32-g49: Circle x18 (B-spline internal-alignment scaffolding for g50; pole/knot coordinates omitted)
    g50: BSplineCurve PolesCount=18 KnotsCount=16 Degree=3 IsPeriodic=0
    g51-g66: GeomPoint x16 (B-spline internal-alignment scaffolding for g50; pole/knot coordinates omitted)
    g67: LineSegment StartX=-117.124 StartY=30.093 StartZ=0 EndX=-117.603 EndY=26.5272 EndZ=0
    g68: LineSegment StartX=-117.603 StartY=17.8472 StartZ=0 EndX=-117.124 EndY=14.2659 EndZ=0
    g69: Ellipse CenterX=-109.671 CenterY=20.025 CenterZ=0 NormalX=0 NormalY=0 NormalZ=1 MajorRadius=3.34798 MinorRadius=2.71052 AngleXU=-1.56793
    g70: GeomPoint X=-109.666 Y=18.0598 Z=0
    g71: GeomPoint X=-109.677 Y=21.9902 Z=0
    g72: Ellipse CenterX=-109.671 CenterY=20.0123 CenterZ=0 NormalX=0 NormalY=0 NormalZ=1 MajorRadius=6.93002 MinorRadius=6.36273 AngleXU=-3.13976
    g73: GeomPoint X=-112.417 Y=20.0073 Z=0
    g74: GeomPoint X=-106.925 Y=20.0173 Z=0
    g75: Ellipse CenterX=-51.7682 CenterY=20.1463 CenterZ=0 NormalX=0 NormalY=0 NormalZ=1 MajorRadius=3.19279 MinorRadius=2.71052 AngleXU=-1.52774
    g76: GeomPoint X=-51.6955 Y=18.4606 Z=0
    g77: GeomPoint X=-51.8408 Y=21.832 Z=0
    g78: GeomPoint X=-54.5142 Y=20.1413 Z=0
    g79: GeomPoint X=-49.0221 Y=20.1513 Z=0
    g80: Ellipse CenterX=-51.7682 CenterY=20.1463 CenterZ=0 NormalX=0 NormalY=0 NormalZ=1 MajorRadius=6.93002 MinorRadius=6.36273 AngleXU=-3.13976
    g81: Ellipse CenterX=-22.8436 CenterY=20.1783 CenterZ=0 NormalX=0 NormalY=0 NormalZ=1 MajorRadius=3.31512 MinorRadius=2.71052 AngleXU=-1.60214
    g82: GeomPoint X=-22.9034 Y=18.2706 Z=0
    g83: GeomPoint X=-22.7838 Y=22.0861 Z=0
    g84: GeomPoint X=-25.5897 Y=20.1733 Z=0
    g85: GeomPoint X=-20.0976 Y=20.1833 Z=0
    g86: Ellipse CenterX=-22.8436 CenterY=20.1783 CenterZ=0 NormalX=0 NormalY=0 NormalZ=1 MajorRadius=6.93002 MinorRadius=6.36273 AngleXU=-3.13976
    g87: LineSegment StartX=-101.889 StartY=14.1107 StartZ=0 EndX=-97.7455 EndY=14.1107 EndZ=0
    g88: LineSegment StartX=-93.8155 StartY=14.1107 StartZ=0 EndX=-89.6755 EndY=14.1107 EndZ=0
    g89: LineSegment StartX=-85.7455 StartY=14.1107 StartZ=0 EndX=-81.6055 EndY=14.1107 EndZ=0
    g90: LineSegment StartX=-101.889 StartY=14.1107 StartZ=0 EndX=-101.889 EndY=25.9907 EndZ=0
    g91: LineSegment StartX=-101.889 StartY=25.9907 StartZ=0 EndX=-97.8594 EndY=25.9907 EndZ=0
    g92: LineSegment StartX=-97.8594 StartY=25.9907 StartZ=0 EndX=-97.8594 EndY=24.0907 EndZ=0
    g93: LineSegment StartX=-97.7455 StartY=14.1107 StartZ=0 EndX=-97.7455 EndY=19.9107 EndZ=0
    g94: LineSegment StartX=-89.6755 StartY=14.1107 StartZ=0 EndX=-89.6755 EndY=19.9107 EndZ=0
    g95: LineSegment StartX=-93.8155 StartY=14.1107 StartZ=0 EndX=-93.8155 EndY=21.0107 EndZ=0
    g96-g106: Circle x11 (B-spline internal-alignment scaffolding for g107; pole/knot coordinates omitted)
    g107: BSplineCurve PolesCount=11 KnotsCount=9 Degree=3 IsPeriodic=0
    g108-g116: GeomPoint x9 (B-spline internal-alignment scaffolding for g107; pole/knot coordinates omitted)
    g117: BSplineCurve PolesCount=11 KnotsCount=9 Degree=3 IsPeriodic=0
    g118-g125: Circle x8 (B-spline internal-alignment scaffolding for g126; pole/knot coordinates omitted)
    g126: BSplineCurve PolesCount=8 KnotsCount=6 Degree=3 IsPeriodic=0
    g127-g132: GeomPoint x6 (B-spline internal-alignment scaffolding for g126; pole/knot coordinates omitted)
    g133: BSplineCurve PolesCount=8 KnotsCount=6 Degree=3 IsPeriodic=0
    g134: LineSegment StartX=-85.7455 StartY=21.0107 StartZ=0 EndX=-85.7455 EndY=14.1107 EndZ=0
    g135: LineSegment StartX=-80.0879 StartY=14.1107 StartZ=0 EndX=-75.944 EndY=14.1107 EndZ=0
    g136: LineSegment StartX=-72.014 StartY=14.1107 StartZ=0 EndX=-67.874 EndY=14.1107 EndZ=0
    g137: LineSegment StartX=-63.944 StartY=14.1107 StartZ=0 EndX=-59.804 EndY=14.1107 EndZ=0
    g138: LineSegment StartX=-80.0879 StartY=14.1107 StartZ=0 EndX=-80.0879 EndY=25.9907 EndZ=0
    g139: LineSegment StartX=-80.0879 StartY=25.9907 StartZ=0 EndX=-76.0579 EndY=25.9907 EndZ=0
    g140: LineSegment StartX=-76.0579 StartY=25.9907 StartZ=0 EndX=-76.0579 EndY=24.0907 EndZ=0
    g141: LineSegment StartX=-75.944 StartY=14.1107 StartZ=0 EndX=-75.944 EndY=19.9107 EndZ=0
    g142: LineSegment StartX=-67.874 StartY=14.1107 StartZ=0 EndX=-67.874 EndY=19.9107 EndZ=0
    g143: LineSegment StartX=-72.014 StartY=14.1107 StartZ=0 EndX=-72.014 EndY=21.0107 EndZ=0
    g144-g148: Circle x5 (B-spline internal-alignment scaffolding for g149; pole/knot coordinates omitted)
    g149: BSplineCurve PolesCount=11 KnotsCount=9 Degree=3 IsPeriodic=0
    g150-g158: GeomPoint x9 (B-spline internal-alignment scaffolding for g149; pole/knot coordinates omitted)
    g159: BSplineCurve PolesCount=11 KnotsCount=9 Degree=3 IsPeriodic=0
    g160-g167: Circle x8 (B-spline internal-alignment scaffolding for g168; pole/knot coordinates omitted)
    g168: BSplineCurve PolesCount=8 KnotsCount=6 Degree=3 IsPeriodic=0
    g169-g174: GeomPoint x6 (B-spline internal-alignment scaffolding for g168; pole/knot coordinates omitted)
    g175: BSplineCurve PolesCount=8 KnotsCount=6 Degree=3 IsPeriodic=0
    g176: LineSegment StartX=-63.944 StartY=21.0107 StartZ=0 EndX=-63.944 EndY=14.1107 EndZ=0
    g177: LineSegment StartX=-59.804 StartY=14.1107 StartZ=0 EndX=-59.804 EndY=21.5868 EndZ=0
    g178: BSplineCurve PolesCount=4 KnotsCount=2 Degree=3 IsPeriodic=0
    g179: GeomPoint X=-59.804 Y=21.5868 Z=0
    g180: GeomPoint X=-60.2379 Y=24.0907 Z=0
    g181: LineSegment StartX=-81.6055 StartY=14.1107 StartZ=0 EndX=-81.6055 EndY=21.5868 EndZ=0
    g182: LineSegment StartX=-151.619 StartY=24.0313 StartZ=0 EndX=-145.128 EndY=24.0313 EndZ=0
    g183: Circle CenterX=-82.0394 CenterY=24.0907 CenterZ=0 NormalX=0 NormalY=0 NormalZ=1 AngleXU=0 Radius=1
    g184: Circle CenterX=-81.7131 CenterY=23.2736 CenterZ=0 NormalX=0 NormalY=0 NormalZ=1 AngleXU=0 Radius=1
    g185: Circle CenterX=-81.6055 CenterY=21.5868 CenterZ=0 NormalX=0 NormalY=0 NormalZ=1 AngleXU=0 Radius=1
    g186: BSplineCurve PolesCount=3 KnotsCount=2 Degree=2 IsPeriodic=0
    g187: GeomPoint X=-82.0394 Y=24.0907 Z=0
    g188: GeomPoint X=-81.6055 Y=21.5868 Z=0
    g189: Ellipse CenterX=-37.3522 CenterY=19.9515 CenterZ=0 NormalX=0 NormalY=0 NormalZ=1 MajorRadius=2.99755 MinorRadius=2.49 AngleXU=1.5708
    g190: GeomPoint X=-37.3522 Y=21.6203 Z=0
    g191: GeomPoint X=-37.3522 Y=18.2826 Z=0
    g192: ArcOfEllipse CenterX=-38.7647 CenterY=20.06 CenterZ=0 NormalX=0 NormalY=0 NormalZ=1 MajorRadius=6.30025 MinorRadius=5.3849 AngleXU=1.57276 StartAngle=5.50632 EndAngle=10.3035
    g193: GeomPoint X=-38.7711 Y=23.3304 Z=0
    g194: GeomPoint X=-38.7583 Y=16.7895 Z=0
    g195: LineSegment StartX=-34.6109 StartY=14.1107 StartZ=0 EndX=-30.8984 EndY=14.1107 EndZ=0
    g196: LineSegment StartX=-30.8984 StartY=14.1107 StartZ=0 EndX=-30.8984 EndY=31.1784 EndZ=0
    g197: LineSegment StartX=-30.8984 StartY=31.1784 StartZ=0 EndX=-34.9984 EndY=31.1784 EndZ=0
    g198: LineSegment StartX=-34.9984 StartY=24.5602 StartZ=0 EndX=-34.9984 EndY=31.1784 EndZ=0
    g199: LineSegment StartX=-34.6109 StartY=16.0476 StartZ=0 EndX=-34.6109 EndY=14.1107 EndZ=0
    g200: LineSegment StartX=-14.8781 StartY=14.1107 StartZ=0 EndX=-10.5106 EndY=14.1107 EndZ=0
    g201: LineSegment StartX=-14.8781 StartY=14.1107 StartZ=0 EndX=-14.8781 EndY=25.8504 EndZ=0
    g202: LineSegment StartX=-14.8781 StartY=25.8504 StartZ=0 EndX=-10.8534 EndY=25.8504 EndZ=0
    g203: LineSegment StartX=-10.8534 StartY=25.8504 StartZ=0 EndX=-10.8534 EndY=24.0923 EndZ=0
    g204: LineSegment StartX=-10.5106 StartY=14.1107 StartZ=0 EndX=-10.5106 EndY=19.7752 EndZ=0
    g205: LineSegment StartX=-5.96397 StartY=25.9304 StartZ=0 EndX=-5.96397 EndY=22.574 EndZ=0
    g206-g214: Circle x9 (B-spline internal-alignment scaffolding for g215; pole/knot coordinates omitted)
    g215: BSplineCurve PolesCount=9 KnotsCount=7 Degree=3 IsPeriodic=0
    g216-g222: GeomPoint x7 (B-spline internal-alignment scaffolding for g215; pole/knot coordinates omitted)
    g223-g232: Circle x10 (B-spline internal-alignment scaffolding for g233; pole/knot coordinates omitted)
    g233: BSplineCurve PolesCount=10 KnotsCount=8 Degree=3 IsPeriodic=0
    g234-g241: GeomPoint x8 (B-spline internal-alignment scaffolding for g233; pole/knot coordinates omitted)
    g242: LineSegment StartX=-1.58923 StartY=21.0696 StartZ=0 EndX=2.62034 EndY=21.0696 EndZ=0
    g243: LineSegment StartX=-1.55856 StartY=18.7342 StartZ=0 EndX=6.45946 EndY=18.7342 EndZ=0
    g244: LineSegment StartX=5.29231 StartY=17.386 StartZ=0 EndX=5.29231 EndY=14.3674 EndZ=0
    g245-g269: Circle x25 (B-spline internal-alignment scaffolding for g270; pole/knot coordinates omitted)
    g270: BSplineCurve PolesCount=25 KnotsCount=23 Degree=3 IsPeriodic=0
    g271-g293: GeomPoint x23 (B-spline internal-alignment scaffolding for g270; pole/knot coordinates omitted)
    g294-g304: Circle x11 (B-spline internal-alignment scaffolding for g305; pole/knot coordinates omitted)
    g305: BSplineCurve PolesCount=11 KnotsCount=9 Degree=3 IsPeriodic=0
    g306-g314: GeomPoint x9 (B-spline internal-alignment scaffolding for g305; pole/knot coordinates omitted)
    g315-g326: Circle x12 (B-spline internal-alignment scaffolding for g327; pole/knot coordinates omitted)
    g327: BSplineCurve PolesCount=12 KnotsCount=10 Degree=3 IsPeriodic=0
    g328-g337: GeomPoint x10 (B-spline internal-alignment scaffolding for g327; pole/knot coordinates omitted)
  constraints (252):
    c: Coincident(g1,g0)
    c: Horizontal(g0)
    c: Vertical(g1)
    c: Coincident(g2,g3)
    c: Coincident(g3,g4)
    c: Horizontal(g4)
    c: Horizontal(g2)
    c: Vertical(g3)
    c: Block(g1)
    c: Distance(g3) = 4.86
    c: Block(g4)
    c: Distance(g0) = 10.8
    c: Distance(g2) = 10.8
    c: Coincident(g5,g0)
    c: Coincident(g6,g4)
    c: Coincident(g6,g2)
    c: Block(g8)
    c: Block(g7)
    c: Coincident(g9,g8)
    c: Coincident(g9,g7)
    c: Vertical(g9)
    c: Coincident(g10,g7)
    c: Coincident(g10,g8)
    c: Vertical(g10)
    c: Weight(g11) = 1
    c: Equal(g11, g12-g21) x10
    c: InternalAlignment(g11-g21 -> g22) x11
    c: InternalAlignment(g23-g31 -> g22) x9
    c: Block(g22)
    c: Weight(g32) = 1
    c: Equal(g32, g33-g49) x17
    c: InternalAlignment(g32-g49 -> g50) x18
    c: InternalAlignment(g51-g66 -> g50) x16
    c: Block(g50)
    c: Coincident(g67,g50)
    c: Coincident(g67,g22)
    c: Coincident(g68,g22)
    c: Coincident(g68,g50)
    c: InternalAlignment(g70,g69)
    c: InternalAlignment(g71,g69)
    c: Block(g69)
    c: InternalAlignment(g73,g72)
    c: InternalAlignment(g74,g72)
    c: Block(g72)
    c: InternalAlignment(g76,g75)
    c: InternalAlignment(g77,g75)
    c: InternalAlignment(g78,g80)
    c: InternalAlignment(g79,g80)
    c: Block(g80)
    c: Coincident(g75,g80)
    c: Block(g75)
    c: InternalAlignment(g82,g81)
    c: InternalAlignment(g83,g81)
    c: InternalAlignment(g84,g86)
    c: InternalAlignment(g85,g86)
    c: Block(g86)
    c: Coincident(g81,g86)
    c: Block(g81)
    c: Horizontal(g87)
    c: Block(g87)
    c: Horizontal(g88)
    c: Distance(g88) = 4.14
    c: Horizontal(g89)
    c: Equal(g88,g89) = 4.14
    c: Block(g89)
    c: Block(g88)
    c: Coincident(g90,g87)
    c: Vertical(g90)
    c: Distance(g90) = 11.88
    c: Coincident(g91,g90)
    c: Horizontal(g91)
    c: Coincident(g92,g91)
    c: Vertical(g92)
    c: Distance(g91) = 4.03
    c: Distance(g92) = 1.9
    c: Coincident(g93,g87)
    c: Vertical(g93)
    c: Vertical(g94)
    c: Coincident(g94,g88)
    c: Distance(g93) = 5.8
    c: Distance(g94) = 5.8
    c: Vertical(g95)
    c: Coincident(g95,g88)
    c: Distance(g95) = 6.9
    c: Coincident(g107,g92)
    c: Weight(g96) = 1
    c: Equal(g96, g97-g106) x10
    c: InternalAlignment(g96-g106 -> g107) x11
    c: InternalAlignment(g108-g116 -> g107) x9
    c: Block(g107)
    c: Block(g117)
    c: Coincident(g126,g93)
    c: Weight(g118) = 1
    c: Equal(g118, g119-g125) x7
    c: Coincident(g126,g95)
    c: InternalAlignment(g118-g125 -> g126) x8
    c: InternalAlignment(g127-g132 -> g126) x6
    c: Coincident(g133,g94)
    c: Block(g126)
    c: Block(g133)
    c: Coincident(g134,g133)
    c: Coincident(g134,g89)
    c: Vertical(g134)
    c: Horizontal(g135)
    c: Block(g135)
    c: Horizontal(g136)
    c: Equal(g88,g136) = 4.14
    c: Horizontal(g137)
    c: Equal(g136,g137) = 4.14
    c: Block(g137)
    c: Block(g136)
    c: Coincident(g138,g135)
    c: Vertical(g138)
    c: Equal(g90,g138) = 11.88
    c: Coincident(g139,g138)
    c: Horizontal(g139)
    c: Coincident(g140,g139)
    c: Vertical(g140)
    c: Equal(g91,g139) = 4.03
    c: Equal(g92,g140) = 1.9
    c: Coincident(g141,g135)
    c: Vertical(g141)
    c: Vertical(g142)
    c: Coincident(g142,g136)
    c: Equal(g93,g141) = 5.8
    c: Equal(g94,g142) = 5.8
    c: Vertical(g143)
    c: Coincident(g143,g136)
    c: Equal(g95,g143) = 6.9
    c: Coincident(g149,g140)
    c: Equal(g96,g144) = 1
    c: Equal(g144, g145-g148) x4
    c: InternalAlignment(g144-g148 -> g149) x5
    c: InternalAlignment(g150-g158 -> g149) x9
    c: Block(g149)
    c: Block(g159)
    c: Coincident(g168,g141)
    c: Equal(g118,g160) = 1
    c: Equal(g160, g161-g167) x7
    c: Coincident(g168,g143)
    c: InternalAlignment(g160-g167 -> g168) x8
    c: InternalAlignment(g169-g174 -> g168) x6
    c: Coincident(g175,g142)
    c: Block(g168)
    c: Block(g175)
    c: Coincident(g176,g175)
    c: Coincident(g176,g137)
    c: Vertical(g176)
    c: Coincident(g177,g137)
    c: Vertical(g177)
    c: Coincident(g178,g177)
    c: Coincident(g178,g159)
    c: InternalAlignment(g179,g178)
    c: InternalAlignment(g180,g178)
    c: Block(g178)
    c: Vertical(g181)
    c: Coincident(g181,g89)
    c: Block(g5)
    c: Coincident(g182,g1)
    c: Coincident(g182,g5)
    c: Horizontal(g182)
    c: Coincident(g186,g117)
    c: Weight(g183) = 1
    c: Equal(g183,g184)
    c: Equal(g183,g185)
    c: Coincident(g186,g181)
    c: InternalAlignment(g183,g186)
    c: InternalAlignment(g184,g186)
    c: InternalAlignment(g185,g186)
    c: InternalAlignment(g187,g186)
    c: InternalAlignment(g188,g186)
    c: Block(g186)
    c: InternalAlignment(g190,g189)
    c: InternalAlignment(g191,g189)
    c: Block(g189)
    c: InternalAlignment(g193,g192)
    c: InternalAlignment(g194,g192)
    c: Block(g192)
    c: Horizontal(g195)
    c: Block(g195)
    c: Coincident(g196,g195)
    c: Vertical(g196)
    c: Block(g196)
    c: Distance(g195) = 3.71244
    c: Coincident(g197,g196)
    c: Horizontal(g197)
    c: Distance(g197) = 4.1
    c: Coincident(g198,g192)
    c: Coincident(g198,g197)
    c: Vertical(g198)
    c: Block(g198)
    c: Coincident(g199,g192)
    c: Coincident(g199,g195)
    c: Vertical(g199)
    c: Block(g199)
    c: Horizontal(g200)
    c: Block(g200)
    c: Coincident(g201,g200)
    c: Vertical(g201)
    c: Block(g201)
    c: Coincident(g202,g201)
    c: Horizontal(g202)
    c: Block(g202)
    c: Coincident(g203,g202)
    c: Vertical(g203)
    c: Block(g203)
    c: Coincident(g204,g200)
    c: Vertical(g204)
    c: Block(g204)
    c: Coincident(g215,g203)
    c: Weight(g206) = 1
    c: Equal(g206, g207-g214) x8
    c: Coincident(g215,g205)
    c: InternalAlignment(g206-g214 -> g215) x9
    c: InternalAlignment(g216-g222 -> g215) x7
    c: Coincident(g233,g204)
    c: Weight(g223) = 1
    c: Equal(g223, g224-g232) x9
    c: Coincident(g233,g205)
    c: InternalAlignment(g223-g232 -> g233) x10
    c: InternalAlignment(g234-g241 -> g233) x8
    c: Vertical(g205)
    c: Block(g205)
    c: Block(g215)
    c: Block(g233)
    c: Horizontal(g242)
    c: Horizontal(g243)
    c: Block(g242)
    c: Block(g243)
    c: Vertical(g244)
    c: Block(g244)
    c: Coincident(g270,g243)
    c: Weight(g245) = 1
    c: Equal(g245, g246-g269) x24
    c: Coincident(g270,g244)
    c: InternalAlignment(g245-g269 -> g270) x25
    c: InternalAlignment(g271-g293 -> g270) x23
    c: Coincident(g305,g242)
    c: Weight(g294) = 1
    c: Equal(g294, g295-g304) x10
    c: Coincident(g305,g242)
    c: InternalAlignment(g294-g304 -> g305) x11
    c: InternalAlignment(g306-g314 -> g305) x9
    c: Block(g305)
    c: Coincident(g327,g243)
    c: Weight(g315) = 1
    c: Equal(g315, g316-g326) x11
    c: Coincident(g327,g244)
    c: InternalAlignment(g315-g326 -> g327) x12
    c: InternalAlignment(g328-g337 -> g327) x10
    c: Block(g327)
    c: Block(g270)
FEATURE [Part::Extrusion] Extrude075  label="CommodoreLogoAndText002"
  Base = -> Sketch084
  Dir = (0,0,1)
  DirMode = 2
  FaceMakerClass = Part::FaceMakerBullseye
  LengthFwd = 10
  LengthRev = 0
  Solid = true
  Symmetric = false
FEATURE [Part::FeaturePython] Clone001  label="CommodoreLogoAndTextScale001"  # Draft clone (typed FeaturePython)
  AttacherType = Attacher::AttachEngine3D
  Fuse = false
  Objects = -> [Extrude075]
  Placement = pos=(112.566,5.37,73.6) rot=(0,0,1;0rad)
  Scale = (0.62,0.62,1)
FEATURE [Part::Cut] Cut073  label="sideA005"
  Base = -> Extrude002
  Tool = -> Part__Mirroring
FEATURE [Part::Cut] Cut074  label="sideB005"
  Base = -> Extrude028
  Tool = -> Clone001
FEATURE [Part::Box] Box037  label="Cube022"
  AttacherType = Attacher::AttachEngine3D
  Height = 10
  Length = 7
  Placement = pos=(9,4.8,0) rot=(0,0,1;0rad)
  Width = 6.7
FEATURE [Sketcher::SketchObject] Sketch085
  FullyConstrained = true
  Placement = pos=(0,0,0) rot=(-1,0,0;4.71239rad)
  sketch-geometry (10):
    g0: LineSegment StartX=0 StartY=4e-16 StartZ=0 EndX=-7 EndY=4e-16 EndZ=0
    g1: LineSegment StartX=-7 StartY=10 StartZ=0 EndX=-6.5 EndY=10 EndZ=0
    g2: LineSegment StartX=0 StartY=10 StartZ=0 EndX=-0.5 EndY=10 EndZ=0
    g3: ArcOfCircle CenterX=-3.5 CenterY=10 CenterZ=0 NormalX=0 NormalY=0 NormalZ=1 AngleXU=0 Radius=3 StartAngle=3.14159 EndAngle=6.28319
    g4: LineSegment StartX=-7 StartY=4e-16 StartZ=0 EndX=-10.5 EndY=4e-16 EndZ=0
    g5: LineSegment StartX=0 StartY=4e-16 StartZ=0 EndX=3.5 EndY=4e-16 EndZ=0
    g6: ArcOfCircle CenterX=-10.5 CenterY=3.5 CenterZ=0 NormalX=0 NormalY=0 NormalZ=1 AngleXU=0 Radius=3.5 StartAngle=4.71239 EndAngle=6.28319
    g7: ArcOfCircle CenterX=3.5 CenterY=3.5 CenterZ=0 NormalX=0 NormalY=0 NormalZ=1 AngleXU=0 Radius=3.5 StartAngle=3.14159 EndAngle=4.71239
    g8: LineSegment StartX=-7 StartY=3.5 StartZ=0 EndX=-7 EndY=10 EndZ=0
    g9: LineSegment StartX=0 StartY=10 StartZ=0 EndX=0 EndY=3.5 EndZ=0
  constraints (26):
    c: Coincident(g0,g-1)
    c: Horizontal(g0)
    c: Distance(g0) = 7
    c: Horizontal(g1)
    c: Distance(g1) = 0.5
    c: Horizontal(g2)
    c: Distance(g2) = 0.5
    c: Coincident(g3,g1)
    c: Coincident(g3,g2)
    c: Block(g3)
    c: Coincident(g4,g0)
    c: Horizontal(g4)
    c: Distance(g4) = 3.5
    c: Coincident(g5,g0)
    c: Distance(g5) = 3.5
    c: Horizontal(g5)
    c: Coincident(g6,g4)
    c: Block(g6)
    c: Coincident(g7,g5)
    c: Block(g7)
    c: Coincident(g8,g6)
    c: Coincident(g8,g1)
    c: Vertical(g8)
    c: Coincident(g9,g2)
    c: Coincident(g9,g7)
    c: Vertical(g9)
